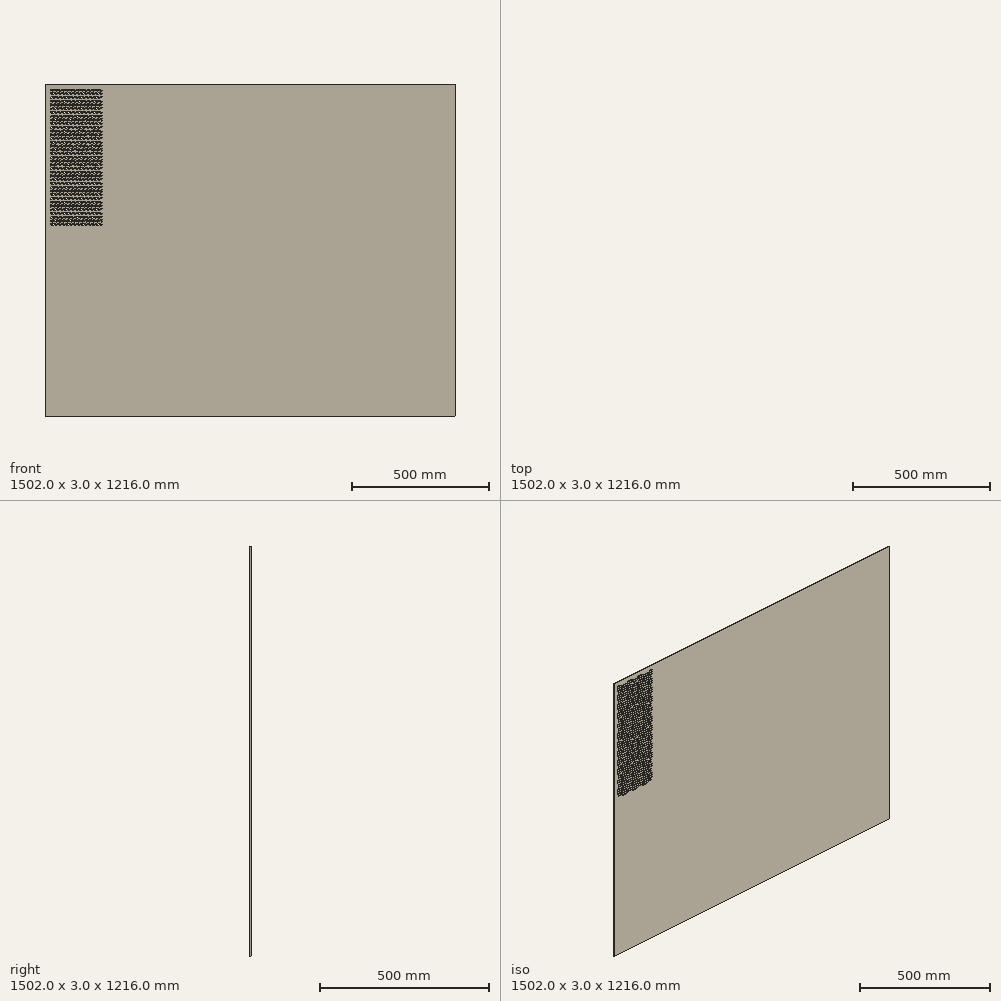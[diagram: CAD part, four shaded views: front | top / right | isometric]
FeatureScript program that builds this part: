
annotation { "Feature Type Name" : "Feature", "Feature Type Description" : "" }
export const myFeature = defineFeature(function(context is Context, id is Id, definition is map)
    precondition{}
    {
        {
            var Q0;
            Q0=qCreatedBy(makeId("Front.planeOp"),FACE);
            var sketch = newSketch(context, id + "F0", { "sketchPlane" : qUnion([Q0])});
            skLineSegment(sketch, "E0.bottom", {"start": v(-752.48, 576.01) * mm, "end": v(749.52, 576.01) * mm});
            skLineSegment(sketch, "E0.top", {"start": v(-752.48, -639.99) * mm, "end": v(749.52, -639.99) * mm});
            skLineSegment(sketch, "E0.left", {"start": v(-752.48, 576.01) * mm, "end": v(-752.48, -639.99) * mm});
            skLineSegment(sketch, "E0.right", {"start": v(749.52, 576.01) * mm, "end": v(749.52, -639.99) * mm});
            skCircle(sketch, "E1", {"center": v(-732.48, 556.01) * mm, "radius": 1.6 * mm});
            skCircle(sketch, "E2", {"center": v(-727.48, 556.01) * mm, "radius": 1.6 * mm});
            skCircle(sketch, "E3", {"center": v(-729.98, 551.01) * mm, "radius": 1.6 * mm});
            skCircle(sketch, "E4", {"center": v(-724.98, 551.01) * mm, "radius": 1.6 * mm});
            skCircle(sketch, "E5.0.1.0", {"center": v(-732.48, 546.01) * mm, "radius": 1.6 * mm});
            skCircle(sketch, "E5.0.1.1", {"center": v(-727.48, 546.01) * mm, "radius": 1.6 * mm});
            skCircle(sketch, "E5.0.1.2", {"center": v(-729.98, 541.01) * mm, "radius": 1.6 * mm});
            skCircle(sketch, "E5.0.1.3", {"center": v(-724.98, 541.01) * mm, "radius": 1.6 * mm});
            skCircle(sketch, "E5.0.2.0", {"center": v(-732.48, 536.01) * mm, "radius": 1.6 * mm});
            skCircle(sketch, "E5.0.2.1", {"center": v(-727.48, 536.01) * mm, "radius": 1.6 * mm});
            skCircle(sketch, "E5.0.2.2", {"center": v(-729.98, 531.01) * mm, "radius": 1.6 * mm});
            skCircle(sketch, "E5.0.2.3", {"center": v(-724.98, 531.01) * mm, "radius": 1.6 * mm});
            skCircle(sketch, "E5.0.3.0", {"center": v(-732.48, 526.01) * mm, "radius": 1.6 * mm});
            skCircle(sketch, "E5.0.3.1", {"center": v(-727.48, 526.01) * mm, "radius": 1.6 * mm});
            skCircle(sketch, "E5.0.3.2", {"center": v(-729.98, 521.01) * mm, "radius": 1.6 * mm});
            skCircle(sketch, "E5.0.3.3", {"center": v(-724.98, 521.01) * mm, "radius": 1.6 * mm});
            skCircle(sketch, "E5.0.4.0", {"center": v(-732.48, 516.01) * mm, "radius": 1.6 * mm});
            skCircle(sketch, "E5.0.4.1", {"center": v(-727.48, 516.01) * mm, "radius": 1.6 * mm});
            skCircle(sketch, "E5.0.4.2", {"center": v(-729.98, 511.01) * mm, "radius": 1.6 * mm});
            skCircle(sketch, "E5.0.4.3", {"center": v(-724.98, 511.01) * mm, "radius": 1.6 * mm});
            skCircle(sketch, "E5.0.5.0", {"center": v(-732.48, 506.01) * mm, "radius": 1.6 * mm});
            skCircle(sketch, "E5.0.5.1", {"center": v(-727.48, 506.01) * mm, "radius": 1.6 * mm});
            skCircle(sketch, "E5.0.5.2", {"center": v(-729.98, 501.01) * mm, "radius": 1.6 * mm});
            skCircle(sketch, "E5.0.5.3", {"center": v(-724.98, 501.01) * mm, "radius": 1.6 * mm});
            skCircle(sketch, "E5.0.6.0", {"center": v(-732.48, 496.01) * mm, "radius": 1.6 * mm});
            skCircle(sketch, "E5.0.6.1", {"center": v(-727.48, 496.01) * mm, "radius": 1.6 * mm});
            skCircle(sketch, "E5.0.6.2", {"center": v(-729.98, 491.01) * mm, "radius": 1.6 * mm});
            skCircle(sketch, "E5.0.6.3", {"center": v(-724.98, 491.01) * mm, "radius": 1.6 * mm});
            skCircle(sketch, "E5.0.7.0", {"center": v(-732.48, 486.01) * mm, "radius": 1.6 * mm});
            skCircle(sketch, "E5.0.7.1", {"center": v(-727.48, 486.01) * mm, "radius": 1.6 * mm});
            skCircle(sketch, "E5.0.7.2", {"center": v(-729.98, 481.01) * mm, "radius": 1.6 * mm});
            skCircle(sketch, "E5.0.7.3", {"center": v(-724.98, 481.01) * mm, "radius": 1.6 * mm});
            skCircle(sketch, "E5.0.8.0", {"center": v(-732.48, 476.01) * mm, "radius": 1.6 * mm});
            skCircle(sketch, "E5.0.8.1", {"center": v(-727.48, 476.01) * mm, "radius": 1.6 * mm});
            skCircle(sketch, "E5.0.8.2", {"center": v(-729.98, 471.01) * mm, "radius": 1.6 * mm});
            skCircle(sketch, "E5.0.8.3", {"center": v(-724.98, 471.01) * mm, "radius": 1.6 * mm});
            skCircle(sketch, "E5.0.9.0", {"center": v(-732.48, 466.01) * mm, "radius": 1.6 * mm});
            skCircle(sketch, "E5.0.9.1", {"center": v(-727.48, 466.01) * mm, "radius": 1.6 * mm});
            skCircle(sketch, "E5.0.9.2", {"center": v(-729.98, 461.01) * mm, "radius": 1.6 * mm});
            skCircle(sketch, "E5.0.9.3", {"center": v(-724.98, 461.01) * mm, "radius": 1.6 * mm});
            skCircle(sketch, "E5.0.10.0", {"center": v(-732.48, 456.01) * mm, "radius": 1.6 * mm});
            skCircle(sketch, "E5.0.10.1", {"center": v(-727.48, 456.01) * mm, "radius": 1.6 * mm});
            skCircle(sketch, "E5.0.10.2", {"center": v(-729.98, 451.01) * mm, "radius": 1.6 * mm});
            skCircle(sketch, "E5.0.10.3", {"center": v(-724.98, 451.01) * mm, "radius": 1.6 * mm});
            skCircle(sketch, "E5.0.11.0", {"center": v(-732.48, 446.01) * mm, "radius": 1.6 * mm});
            skCircle(sketch, "E5.0.11.1", {"center": v(-727.48, 446.01) * mm, "radius": 1.6 * mm});
            skCircle(sketch, "E5.0.11.2", {"center": v(-729.98, 441.01) * mm, "radius": 1.6 * mm});
            skCircle(sketch, "E5.0.11.3", {"center": v(-724.98, 441.01) * mm, "radius": 1.6 * mm});
            skCircle(sketch, "E5.0.12.0", {"center": v(-732.48, 436.01) * mm, "radius": 1.6 * mm});
            skCircle(sketch, "E5.0.12.1", {"center": v(-727.48, 436.01) * mm, "radius": 1.6 * mm});
            skCircle(sketch, "E5.0.12.2", {"center": v(-729.98, 431.01) * mm, "radius": 1.6 * mm});
            skCircle(sketch, "E5.0.12.3", {"center": v(-724.98, 431.01) * mm, "radius": 1.6 * mm});
            skCircle(sketch, "E5.0.13.0", {"center": v(-732.48, 426.01) * mm, "radius": 1.6 * mm});
            skCircle(sketch, "E5.0.13.1", {"center": v(-727.48, 426.01) * mm, "radius": 1.6 * mm});
            skCircle(sketch, "E5.0.13.2", {"center": v(-729.98, 421.01) * mm, "radius": 1.6 * mm});
            skCircle(sketch, "E5.0.13.3", {"center": v(-724.98, 421.01) * mm, "radius": 1.6 * mm});
            skCircle(sketch, "E5.0.14.0", {"center": v(-732.48, 416.01) * mm, "radius": 1.6 * mm});
            skCircle(sketch, "E5.0.14.1", {"center": v(-727.48, 416.01) * mm, "radius": 1.6 * mm});
            skCircle(sketch, "E5.0.14.2", {"center": v(-729.98, 411.01) * mm, "radius": 1.6 * mm});
            skCircle(sketch, "E5.0.14.3", {"center": v(-724.98, 411.01) * mm, "radius": 1.6 * mm});
            skCircle(sketch, "E5.0.15.0", {"center": v(-732.48, 406.01) * mm, "radius": 1.6 * mm});
            skCircle(sketch, "E5.0.15.1", {"center": v(-727.48, 406.01) * mm, "radius": 1.6 * mm});
            skCircle(sketch, "E5.0.15.2", {"center": v(-729.98, 401.01) * mm, "radius": 1.6 * mm});
            skCircle(sketch, "E5.0.15.3", {"center": v(-724.98, 401.01) * mm, "radius": 1.6 * mm});
            skCircle(sketch, "E5.0.16.0", {"center": v(-732.48, 396.01) * mm, "radius": 1.6 * mm});
            skCircle(sketch, "E5.0.16.1", {"center": v(-727.48, 396.01) * mm, "radius": 1.6 * mm});
            skCircle(sketch, "E5.0.16.2", {"center": v(-729.98, 391.01) * mm, "radius": 1.6 * mm});
            skCircle(sketch, "E5.0.16.3", {"center": v(-724.98, 391.01) * mm, "radius": 1.6 * mm});
            skCircle(sketch, "E5.0.17.0", {"center": v(-732.48, 386.01) * mm, "radius": 1.6 * mm});
            skCircle(sketch, "E5.0.17.1", {"center": v(-727.48, 386.01) * mm, "radius": 1.6 * mm});
            skCircle(sketch, "E5.0.17.2", {"center": v(-729.98, 381.01) * mm, "radius": 1.6 * mm});
            skCircle(sketch, "E5.0.17.3", {"center": v(-724.98, 381.01) * mm, "radius": 1.6 * mm});
            skCircle(sketch, "E5.0.18.0", {"center": v(-732.48, 376.01) * mm, "radius": 1.6 * mm});
            skCircle(sketch, "E5.0.18.1", {"center": v(-727.48, 376.01) * mm, "radius": 1.6 * mm});
            skCircle(sketch, "E5.0.18.2", {"center": v(-729.98, 371.01) * mm, "radius": 1.6 * mm});
            skCircle(sketch, "E5.0.18.3", {"center": v(-724.98, 371.01) * mm, "radius": 1.6 * mm});
            skCircle(sketch, "E5.0.19.0", {"center": v(-732.48, 366.01) * mm, "radius": 1.6 * mm});
            skCircle(sketch, "E5.0.19.1", {"center": v(-727.48, 366.01) * mm, "radius": 1.6 * mm});
            skCircle(sketch, "E5.0.19.2", {"center": v(-729.98, 361.01) * mm, "radius": 1.6 * mm});
            skCircle(sketch, "E5.0.19.3", {"center": v(-724.98, 361.01) * mm, "radius": 1.6 * mm});
            skCircle(sketch, "E5.0.20.0", {"center": v(-732.48, 356.01) * mm, "radius": 1.6 * mm});
            skCircle(sketch, "E5.0.20.1", {"center": v(-727.48, 356.01) * mm, "radius": 1.6 * mm});
            skCircle(sketch, "E5.0.20.2", {"center": v(-729.98, 351.01) * mm, "radius": 1.6 * mm});
            skCircle(sketch, "E5.0.20.3", {"center": v(-724.98, 351.01) * mm, "radius": 1.6 * mm});
            skCircle(sketch, "E5.0.21.0", {"center": v(-732.48, 346.01) * mm, "radius": 1.6 * mm});
            skCircle(sketch, "E5.0.21.1", {"center": v(-727.48, 346.01) * mm, "radius": 1.6 * mm});
            skCircle(sketch, "E5.0.21.2", {"center": v(-729.98, 341.01) * mm, "radius": 1.6 * mm});
            skCircle(sketch, "E5.0.21.3", {"center": v(-724.98, 341.01) * mm, "radius": 1.6 * mm});
            skCircle(sketch, "E5.0.22.0", {"center": v(-732.48, 336.01) * mm, "radius": 1.6 * mm});
            skCircle(sketch, "E5.0.22.1", {"center": v(-727.48, 336.01) * mm, "radius": 1.6 * mm});
            skCircle(sketch, "E5.0.22.2", {"center": v(-729.98, 331.01) * mm, "radius": 1.6 * mm});
            skCircle(sketch, "E5.0.22.3", {"center": v(-724.98, 331.01) * mm, "radius": 1.6 * mm});
            skCircle(sketch, "E5.0.23.0", {"center": v(-732.48, 326.01) * mm, "radius": 1.6 * mm});
            skCircle(sketch, "E5.0.23.1", {"center": v(-727.48, 326.01) * mm, "radius": 1.6 * mm});
            skCircle(sketch, "E5.0.23.2", {"center": v(-729.98, 321.01) * mm, "radius": 1.6 * mm});
            skCircle(sketch, "E5.0.23.3", {"center": v(-724.98, 321.01) * mm, "radius": 1.6 * mm});
            skCircle(sketch, "E5.0.24.0", {"center": v(-732.48, 316.01) * mm, "radius": 1.6 * mm});
            skCircle(sketch, "E5.0.24.1", {"center": v(-727.48, 316.01) * mm, "radius": 1.6 * mm});
            skCircle(sketch, "E5.0.24.2", {"center": v(-729.98, 311.01) * mm, "radius": 1.6 * mm});
            skCircle(sketch, "E5.0.24.3", {"center": v(-724.98, 311.01) * mm, "radius": 1.6 * mm});
            skCircle(sketch, "E5.0.25.0", {"center": v(-732.48, 306.01) * mm, "radius": 1.6 * mm});
            skCircle(sketch, "E5.0.25.1", {"center": v(-727.48, 306.01) * mm, "radius": 1.6 * mm});
            skCircle(sketch, "E5.0.25.2", {"center": v(-729.98, 301.01) * mm, "radius": 1.6 * mm});
            skCircle(sketch, "E5.0.25.3", {"center": v(-724.98, 301.01) * mm, "radius": 1.6 * mm});
            skCircle(sketch, "E5.0.26.0", {"center": v(-732.48, 296.01) * mm, "radius": 1.6 * mm});
            skCircle(sketch, "E5.0.26.1", {"center": v(-727.48, 296.01) * mm, "radius": 1.6 * mm});
            skCircle(sketch, "E5.0.26.2", {"center": v(-729.98, 291.01) * mm, "radius": 1.6 * mm});
            skCircle(sketch, "E5.0.26.3", {"center": v(-724.98, 291.01) * mm, "radius": 1.6 * mm});
            skCircle(sketch, "E5.0.27.0", {"center": v(-732.48, 286.01) * mm, "radius": 1.6 * mm});
            skCircle(sketch, "E5.0.27.1", {"center": v(-727.48, 286.01) * mm, "radius": 1.6 * mm});
            skCircle(sketch, "E5.0.27.2", {"center": v(-729.98, 281.01) * mm, "radius": 1.6 * mm});
            skCircle(sketch, "E5.0.27.3", {"center": v(-724.98, 281.01) * mm, "radius": 1.6 * mm});
            skCircle(sketch, "E5.0.28.0", {"center": v(-732.48, 276.01) * mm, "radius": 1.6 * mm});
            skCircle(sketch, "E5.0.28.1", {"center": v(-727.48, 276.01) * mm, "radius": 1.6 * mm});
            skCircle(sketch, "E5.0.28.2", {"center": v(-729.98, 271.01) * mm, "radius": 1.6 * mm});
            skCircle(sketch, "E5.0.28.3", {"center": v(-724.98, 271.01) * mm, "radius": 1.6 * mm});
            skCircle(sketch, "E5.0.29.0", {"center": v(-732.48, 266.01) * mm, "radius": 1.6 * mm});
            skCircle(sketch, "E5.0.29.1", {"center": v(-727.48, 266.01) * mm, "radius": 1.6 * mm});
            skCircle(sketch, "E5.0.29.2", {"center": v(-729.98, 261.01) * mm, "radius": 1.6 * mm});
            skCircle(sketch, "E5.0.29.3", {"center": v(-724.98, 261.01) * mm, "radius": 1.6 * mm});
            skCircle(sketch, "E5.0.30.0", {"center": v(-732.48, 256.01) * mm, "radius": 1.6 * mm});
            skCircle(sketch, "E5.0.30.1", {"center": v(-727.48, 256.01) * mm, "radius": 1.6 * mm});
            skCircle(sketch, "E5.0.30.2", {"center": v(-729.98, 251.01) * mm, "radius": 1.6 * mm});
            skCircle(sketch, "E5.0.30.3", {"center": v(-724.98, 251.01) * mm, "radius": 1.6 * mm});
            skCircle(sketch, "E5.0.31.0", {"center": v(-732.48, 246.01) * mm, "radius": 1.6 * mm});
            skCircle(sketch, "E5.0.31.1", {"center": v(-727.48, 246.01) * mm, "radius": 1.6 * mm});
            skCircle(sketch, "E5.0.31.2", {"center": v(-729.98, 241.01) * mm, "radius": 1.6 * mm});
            skCircle(sketch, "E5.0.31.3", {"center": v(-724.98, 241.01) * mm, "radius": 1.6 * mm});
            skCircle(sketch, "E5.0.32.0", {"center": v(-732.48, 236.01) * mm, "radius": 1.6 * mm});
            skCircle(sketch, "E5.0.32.1", {"center": v(-727.48, 236.01) * mm, "radius": 1.6 * mm});
            skCircle(sketch, "E5.0.32.2", {"center": v(-729.98, 231.01) * mm, "radius": 1.6 * mm});
            skCircle(sketch, "E5.0.32.3", {"center": v(-724.98, 231.01) * mm, "radius": 1.6 * mm});
            skCircle(sketch, "E5.0.33.0", {"center": v(-732.48, 226.01) * mm, "radius": 1.6 * mm});
            skCircle(sketch, "E5.0.33.1", {"center": v(-727.48, 226.01) * mm, "radius": 1.6 * mm});
            skCircle(sketch, "E5.0.33.2", {"center": v(-729.98, 221.01) * mm, "radius": 1.6 * mm});
            skCircle(sketch, "E5.0.33.3", {"center": v(-724.98, 221.01) * mm, "radius": 1.6 * mm});
            skCircle(sketch, "E5.0.34.0", {"center": v(-732.48, 216.01) * mm, "radius": 1.6 * mm});
            skCircle(sketch, "E5.0.34.1", {"center": v(-727.48, 216.01) * mm, "radius": 1.6 * mm});
            skCircle(sketch, "E5.0.34.2", {"center": v(-729.98, 211.01) * mm, "radius": 1.6 * mm});
            skCircle(sketch, "E5.0.34.3", {"center": v(-724.98, 211.01) * mm, "radius": 1.6 * mm});
            skCircle(sketch, "E5.0.35.0", {"center": v(-732.48, 206.01) * mm, "radius": 1.6 * mm});
            skCircle(sketch, "E5.0.35.1", {"center": v(-727.48, 206.01) * mm, "radius": 1.6 * mm});
            skCircle(sketch, "E5.0.35.2", {"center": v(-729.98, 201.01) * mm, "radius": 1.6 * mm});
            skCircle(sketch, "E5.0.35.3", {"center": v(-724.98, 201.01) * mm, "radius": 1.6 * mm});
            skCircle(sketch, "E5.0.36.0", {"center": v(-732.48, 196.01) * mm, "radius": 1.6 * mm});
            skCircle(sketch, "E5.0.36.1", {"center": v(-727.48, 196.01) * mm, "radius": 1.6 * mm});
            skCircle(sketch, "E5.0.36.2", {"center": v(-729.98, 191.01) * mm, "radius": 1.6 * mm});
            skCircle(sketch, "E5.0.36.3", {"center": v(-724.98, 191.01) * mm, "radius": 1.6 * mm});
            skCircle(sketch, "E5.0.37.0", {"center": v(-732.48, 186.01) * mm, "radius": 1.6 * mm});
            skCircle(sketch, "E5.0.37.1", {"center": v(-727.48, 186.01) * mm, "radius": 1.6 * mm});
            skCircle(sketch, "E5.0.37.2", {"center": v(-729.98, 181.01) * mm, "radius": 1.6 * mm});
            skCircle(sketch, "E5.0.37.3", {"center": v(-724.98, 181.01) * mm, "radius": 1.6 * mm});
            skCircle(sketch, "E5.0.38.0", {"center": v(-732.48, 176.01) * mm, "radius": 1.6 * mm});
            skCircle(sketch, "E5.0.38.1", {"center": v(-727.48, 176.01) * mm, "radius": 1.6 * mm});
            skCircle(sketch, "E5.0.38.2", {"center": v(-729.98, 171.01) * mm, "radius": 1.6 * mm});
            skCircle(sketch, "E5.0.38.3", {"center": v(-724.98, 171.01) * mm, "radius": 1.6 * mm});
            skCircle(sketch, "E5.0.39.0", {"center": v(-732.48, 166.01) * mm, "radius": 1.6 * mm});
            skCircle(sketch, "E5.0.39.1", {"center": v(-727.48, 166.01) * mm, "radius": 1.6 * mm});
            skCircle(sketch, "E5.0.39.2", {"center": v(-729.98, 161.01) * mm, "radius": 1.6 * mm});
            skCircle(sketch, "E5.0.39.3", {"center": v(-724.98, 161.01) * mm, "radius": 1.6 * mm});
            skCircle(sketch, "E5.0.40.0", {"center": v(-732.48, 156.01) * mm, "radius": 1.6 * mm});
            skCircle(sketch, "E5.0.40.1", {"center": v(-727.48, 156.01) * mm, "radius": 1.6 * mm});
            skCircle(sketch, "E5.0.40.2", {"center": v(-729.98, 151.01) * mm, "radius": 1.6 * mm});
            skCircle(sketch, "E5.0.40.3", {"center": v(-724.98, 151.01) * mm, "radius": 1.6 * mm});
            skCircle(sketch, "E5.0.41.0", {"center": v(-732.48, 146.01) * mm, "radius": 1.6 * mm});
            skCircle(sketch, "E5.0.41.1", {"center": v(-727.48, 146.01) * mm, "radius": 1.6 * mm});
            skCircle(sketch, "E5.0.41.2", {"center": v(-729.98, 141.01) * mm, "radius": 1.6 * mm});
            skCircle(sketch, "E5.0.41.3", {"center": v(-724.98, 141.01) * mm, "radius": 1.6 * mm});
            skCircle(sketch, "E5.0.42.0", {"center": v(-732.48, 136.01) * mm, "radius": 1.6 * mm});
            skCircle(sketch, "E5.0.42.1", {"center": v(-727.48, 136.01) * mm, "radius": 1.6 * mm});
            skCircle(sketch, "E5.0.42.2", {"center": v(-729.98, 131.01) * mm, "radius": 1.6 * mm});
            skCircle(sketch, "E5.0.42.3", {"center": v(-724.98, 131.01) * mm, "radius": 1.6 * mm});
            skCircle(sketch, "E5.0.43.0", {"center": v(-732.48, 126.01) * mm, "radius": 1.6 * mm});
            skCircle(sketch, "E5.0.43.1", {"center": v(-727.48, 126.01) * mm, "radius": 1.6 * mm});
            skCircle(sketch, "E5.0.43.2", {"center": v(-729.98, 121.01) * mm, "radius": 1.6 * mm});
            skCircle(sketch, "E5.0.43.3", {"center": v(-724.98, 121.01) * mm, "radius": 1.6 * mm});
            skCircle(sketch, "E5.0.44.0", {"center": v(-732.48, 116.01) * mm, "radius": 1.6 * mm});
            skCircle(sketch, "E5.0.44.1", {"center": v(-727.48, 116.01) * mm, "radius": 1.6 * mm});
            skCircle(sketch, "E5.0.44.2", {"center": v(-729.98, 111.01) * mm, "radius": 1.6 * mm});
            skCircle(sketch, "E5.0.44.3", {"center": v(-724.98, 111.01) * mm, "radius": 1.6 * mm});
            skCircle(sketch, "E5.0.45.0", {"center": v(-732.48, 106.01) * mm, "radius": 1.6 * mm});
            skCircle(sketch, "E5.0.45.1", {"center": v(-727.48, 106.01) * mm, "radius": 1.6 * mm});
            skCircle(sketch, "E5.0.45.2", {"center": v(-729.98, 101.01) * mm, "radius": 1.6 * mm});
            skCircle(sketch, "E5.0.45.3", {"center": v(-724.98, 101.01) * mm, "radius": 1.6 * mm});
            skCircle(sketch, "E5.0.46.0", {"center": v(-732.48, 96.01) * mm, "radius": 1.6 * mm});
            skCircle(sketch, "E5.0.46.1", {"center": v(-727.48, 96.01) * mm, "radius": 1.6 * mm});
            skCircle(sketch, "E5.0.46.2", {"center": v(-729.98, 91.01) * mm, "radius": 1.6 * mm});
            skCircle(sketch, "E5.0.46.3", {"center": v(-724.98, 91.01) * mm, "radius": 1.6 * mm});
            skCircle(sketch, "E5.0.47.0", {"center": v(-732.48, 86.01) * mm, "radius": 1.6 * mm});
            skCircle(sketch, "E5.0.47.1", {"center": v(-727.48, 86.01) * mm, "radius": 1.6 * mm});
            skCircle(sketch, "E5.0.47.2", {"center": v(-729.98, 81.01) * mm, "radius": 1.6 * mm});
            skCircle(sketch, "E5.0.47.3", {"center": v(-724.98, 81.01) * mm, "radius": 1.6 * mm});
            skCircle(sketch, "E5.0.48.0", {"center": v(-732.48, 76.01) * mm, "radius": 1.6 * mm});
            skCircle(sketch, "E5.0.48.1", {"center": v(-727.48, 76.01) * mm, "radius": 1.6 * mm});
            skCircle(sketch, "E5.0.48.2", {"center": v(-729.98, 71.01) * mm, "radius": 1.6 * mm});
            skCircle(sketch, "E5.0.48.3", {"center": v(-724.98, 71.01) * mm, "radius": 1.6 * mm});
            skCircle(sketch, "E5.0.49.0", {"center": v(-732.48, 66.01) * mm, "radius": 1.6 * mm});
            skCircle(sketch, "E5.0.49.1", {"center": v(-727.48, 66.01) * mm, "radius": 1.6 * mm});
            skCircle(sketch, "E5.0.49.2", {"center": v(-729.98, 61.01) * mm, "radius": 1.6 * mm});
            skCircle(sketch, "E5.0.49.3", {"center": v(-724.98, 61.01) * mm, "radius": 1.6 * mm});
            skCircle(sketch, "E5.1.0.0", {"center": v(-722.48, 556.01) * mm, "radius": 1.6 * mm});
            skCircle(sketch, "E5.1.0.1", {"center": v(-717.48, 556.01) * mm, "radius": 1.6 * mm});
            skCircle(sketch, "E5.1.0.2", {"center": v(-719.98, 551.01) * mm, "radius": 1.6 * mm});
            skCircle(sketch, "E5.1.0.3", {"center": v(-714.98, 551.01) * mm, "radius": 1.6 * mm});
            skCircle(sketch, "E5.1.1.0", {"center": v(-722.48, 546.01) * mm, "radius": 1.6 * mm});
            skCircle(sketch, "E5.1.1.1", {"center": v(-717.48, 546.01) * mm, "radius": 1.6 * mm});
            skCircle(sketch, "E5.1.1.2", {"center": v(-719.98, 541.01) * mm, "radius": 1.6 * mm});
            skCircle(sketch, "E5.1.1.3", {"center": v(-714.98, 541.01) * mm, "radius": 1.6 * mm});
            skCircle(sketch, "E5.1.2.0", {"center": v(-722.48, 536.01) * mm, "radius": 1.6 * mm});
            skCircle(sketch, "E5.1.2.1", {"center": v(-717.48, 536.01) * mm, "radius": 1.6 * mm});
            skCircle(sketch, "E5.1.2.2", {"center": v(-719.98, 531.01) * mm, "radius": 1.6 * mm});
            skCircle(sketch, "E5.1.2.3", {"center": v(-714.98, 531.01) * mm, "radius": 1.6 * mm});
            skCircle(sketch, "E5.1.3.0", {"center": v(-722.48, 526.01) * mm, "radius": 1.6 * mm});
            skCircle(sketch, "E5.1.3.1", {"center": v(-717.48, 526.01) * mm, "radius": 1.6 * mm});
            skCircle(sketch, "E5.1.3.2", {"center": v(-719.98, 521.01) * mm, "radius": 1.6 * mm});
            skCircle(sketch, "E5.1.3.3", {"center": v(-714.98, 521.01) * mm, "radius": 1.6 * mm});
            skCircle(sketch, "E5.1.4.0", {"center": v(-722.48, 516.01) * mm, "radius": 1.6 * mm});
            skCircle(sketch, "E5.1.4.1", {"center": v(-717.48, 516.01) * mm, "radius": 1.6 * mm});
            skCircle(sketch, "E5.1.4.2", {"center": v(-719.98, 511.01) * mm, "radius": 1.6 * mm});
            skCircle(sketch, "E5.1.4.3", {"center": v(-714.98, 511.01) * mm, "radius": 1.6 * mm});
            skCircle(sketch, "E5.1.5.0", {"center": v(-722.48, 506.01) * mm, "radius": 1.6 * mm});
            skCircle(sketch, "E5.1.5.1", {"center": v(-717.48, 506.01) * mm, "radius": 1.6 * mm});
            skCircle(sketch, "E5.1.5.2", {"center": v(-719.98, 501.01) * mm, "radius": 1.6 * mm});
            skCircle(sketch, "E5.1.5.3", {"center": v(-714.98, 501.01) * mm, "radius": 1.6 * mm});
            skCircle(sketch, "E5.1.6.0", {"center": v(-722.48, 496.01) * mm, "radius": 1.6 * mm});
            skCircle(sketch, "E5.1.6.1", {"center": v(-717.48, 496.01) * mm, "radius": 1.6 * mm});
            skCircle(sketch, "E5.1.6.2", {"center": v(-719.98, 491.01) * mm, "radius": 1.6 * mm});
            skCircle(sketch, "E5.1.6.3", {"center": v(-714.98, 491.01) * mm, "radius": 1.6 * mm});
            skCircle(sketch, "E5.1.7.0", {"center": v(-722.48, 486.01) * mm, "radius": 1.6 * mm});
            skCircle(sketch, "E5.1.7.1", {"center": v(-717.48, 486.01) * mm, "radius": 1.6 * mm});
            skCircle(sketch, "E5.1.7.2", {"center": v(-719.98, 481.01) * mm, "radius": 1.6 * mm});
            skCircle(sketch, "E5.1.7.3", {"center": v(-714.98, 481.01) * mm, "radius": 1.6 * mm});
            skCircle(sketch, "E5.1.8.0", {"center": v(-722.48, 476.01) * mm, "radius": 1.6 * mm});
            skCircle(sketch, "E5.1.8.1", {"center": v(-717.48, 476.01) * mm, "radius": 1.6 * mm});
            skCircle(sketch, "E5.1.8.2", {"center": v(-719.98, 471.01) * mm, "radius": 1.6 * mm});
            skCircle(sketch, "E5.1.8.3", {"center": v(-714.98, 471.01) * mm, "radius": 1.6 * mm});
            skCircle(sketch, "E5.1.9.0", {"center": v(-722.48, 466.01) * mm, "radius": 1.6 * mm});
            skCircle(sketch, "E5.1.9.1", {"center": v(-717.48, 466.01) * mm, "radius": 1.6 * mm});
            skCircle(sketch, "E5.1.9.2", {"center": v(-719.98, 461.01) * mm, "radius": 1.6 * mm});
            skCircle(sketch, "E5.1.9.3", {"center": v(-714.98, 461.01) * mm, "radius": 1.6 * mm});
            skCircle(sketch, "E5.1.10.0", {"center": v(-722.48, 456.01) * mm, "radius": 1.6 * mm});
            skCircle(sketch, "E5.1.10.1", {"center": v(-717.48, 456.01) * mm, "radius": 1.6 * mm});
            skCircle(sketch, "E5.1.10.2", {"center": v(-719.98, 451.01) * mm, "radius": 1.6 * mm});
            skCircle(sketch, "E5.1.10.3", {"center": v(-714.98, 451.01) * mm, "radius": 1.6 * mm});
            skCircle(sketch, "E5.1.11.0", {"center": v(-722.48, 446.01) * mm, "radius": 1.6 * mm});
            skCircle(sketch, "E5.1.11.1", {"center": v(-717.48, 446.01) * mm, "radius": 1.6 * mm});
            skCircle(sketch, "E5.1.11.2", {"center": v(-719.98, 441.01) * mm, "radius": 1.6 * mm});
            skCircle(sketch, "E5.1.11.3", {"center": v(-714.98, 441.01) * mm, "radius": 1.6 * mm});
            skCircle(sketch, "E5.1.12.0", {"center": v(-722.48, 436.01) * mm, "radius": 1.6 * mm});
            skCircle(sketch, "E5.1.12.1", {"center": v(-717.48, 436.01) * mm, "radius": 1.6 * mm});
            skCircle(sketch, "E5.1.12.2", {"center": v(-719.98, 431.01) * mm, "radius": 1.6 * mm});
            skCircle(sketch, "E5.1.12.3", {"center": v(-714.98, 431.01) * mm, "radius": 1.6 * mm});
            skCircle(sketch, "E5.1.13.0", {"center": v(-722.48, 426.01) * mm, "radius": 1.6 * mm});
            skCircle(sketch, "E5.1.13.1", {"center": v(-717.48, 426.01) * mm, "radius": 1.6 * mm});
            skCircle(sketch, "E5.1.13.2", {"center": v(-719.98, 421.01) * mm, "radius": 1.6 * mm});
            skCircle(sketch, "E5.1.13.3", {"center": v(-714.98, 421.01) * mm, "radius": 1.6 * mm});
            skCircle(sketch, "E5.1.14.0", {"center": v(-722.48, 416.01) * mm, "radius": 1.6 * mm});
            skCircle(sketch, "E5.1.14.1", {"center": v(-717.48, 416.01) * mm, "radius": 1.6 * mm});
            skCircle(sketch, "E5.1.14.2", {"center": v(-719.98, 411.01) * mm, "radius": 1.6 * mm});
            skCircle(sketch, "E5.1.14.3", {"center": v(-714.98, 411.01) * mm, "radius": 1.6 * mm});
            skCircle(sketch, "E5.1.15.0", {"center": v(-722.48, 406.01) * mm, "radius": 1.6 * mm});
            skCircle(sketch, "E5.1.15.1", {"center": v(-717.48, 406.01) * mm, "radius": 1.6 * mm});
            skCircle(sketch, "E5.1.15.2", {"center": v(-719.98, 401.01) * mm, "radius": 1.6 * mm});
            skCircle(sketch, "E5.1.15.3", {"center": v(-714.98, 401.01) * mm, "radius": 1.6 * mm});
            skCircle(sketch, "E5.1.16.0", {"center": v(-722.48, 396.01) * mm, "radius": 1.6 * mm});
            skCircle(sketch, "E5.1.16.1", {"center": v(-717.48, 396.01) * mm, "radius": 1.6 * mm});
            skCircle(sketch, "E5.1.16.2", {"center": v(-719.98, 391.01) * mm, "radius": 1.6 * mm});
            skCircle(sketch, "E5.1.16.3", {"center": v(-714.98, 391.01) * mm, "radius": 1.6 * mm});
            skCircle(sketch, "E5.1.17.0", {"center": v(-722.48, 386.01) * mm, "radius": 1.6 * mm});
            skCircle(sketch, "E5.1.17.1", {"center": v(-717.48, 386.01) * mm, "radius": 1.6 * mm});
            skCircle(sketch, "E5.1.17.2", {"center": v(-719.98, 381.01) * mm, "radius": 1.6 * mm});
            skCircle(sketch, "E5.1.17.3", {"center": v(-714.98, 381.01) * mm, "radius": 1.6 * mm});
            skCircle(sketch, "E5.1.18.0", {"center": v(-722.48, 376.01) * mm, "radius": 1.6 * mm});
            skCircle(sketch, "E5.1.18.1", {"center": v(-717.48, 376.01) * mm, "radius": 1.6 * mm});
            skCircle(sketch, "E5.1.18.2", {"center": v(-719.98, 371.01) * mm, "radius": 1.6 * mm});
            skCircle(sketch, "E5.1.18.3", {"center": v(-714.98, 371.01) * mm, "radius": 1.6 * mm});
            skCircle(sketch, "E5.1.19.0", {"center": v(-722.48, 366.01) * mm, "radius": 1.6 * mm});
            skCircle(sketch, "E5.1.19.1", {"center": v(-717.48, 366.01) * mm, "radius": 1.6 * mm});
            skCircle(sketch, "E5.1.19.2", {"center": v(-719.98, 361.01) * mm, "radius": 1.6 * mm});
            skCircle(sketch, "E5.1.19.3", {"center": v(-714.98, 361.01) * mm, "radius": 1.6 * mm});
            skCircle(sketch, "E5.1.20.0", {"center": v(-722.48, 356.01) * mm, "radius": 1.6 * mm});
            skCircle(sketch, "E5.1.20.1", {"center": v(-717.48, 356.01) * mm, "radius": 1.6 * mm});
            skCircle(sketch, "E5.1.20.2", {"center": v(-719.98, 351.01) * mm, "radius": 1.6 * mm});
            skCircle(sketch, "E5.1.20.3", {"center": v(-714.98, 351.01) * mm, "radius": 1.6 * mm});
            skCircle(sketch, "E5.1.21.0", {"center": v(-722.48, 346.01) * mm, "radius": 1.6 * mm});
            skCircle(sketch, "E5.1.21.1", {"center": v(-717.48, 346.01) * mm, "radius": 1.6 * mm});
            skCircle(sketch, "E5.1.21.2", {"center": v(-719.98, 341.01) * mm, "radius": 1.6 * mm});
            skCircle(sketch, "E5.1.21.3", {"center": v(-714.98, 341.01) * mm, "radius": 1.6 * mm});
            skCircle(sketch, "E5.1.22.0", {"center": v(-722.48, 336.01) * mm, "radius": 1.6 * mm});
            skCircle(sketch, "E5.1.22.1", {"center": v(-717.48, 336.01) * mm, "radius": 1.6 * mm});
            skCircle(sketch, "E5.1.22.2", {"center": v(-719.98, 331.01) * mm, "radius": 1.6 * mm});
            skCircle(sketch, "E5.1.22.3", {"center": v(-714.98, 331.01) * mm, "radius": 1.6 * mm});
            skCircle(sketch, "E5.1.23.0", {"center": v(-722.48, 326.01) * mm, "radius": 1.6 * mm});
            skCircle(sketch, "E5.1.23.1", {"center": v(-717.48, 326.01) * mm, "radius": 1.6 * mm});
            skCircle(sketch, "E5.1.23.2", {"center": v(-719.98, 321.01) * mm, "radius": 1.6 * mm});
            skCircle(sketch, "E5.1.23.3", {"center": v(-714.98, 321.01) * mm, "radius": 1.6 * mm});
            skCircle(sketch, "E5.1.24.0", {"center": v(-722.48, 316.01) * mm, "radius": 1.6 * mm});
            skCircle(sketch, "E5.1.24.1", {"center": v(-717.48, 316.01) * mm, "radius": 1.6 * mm});
            skCircle(sketch, "E5.1.24.2", {"center": v(-719.98, 311.01) * mm, "radius": 1.6 * mm});
            skCircle(sketch, "E5.1.24.3", {"center": v(-714.98, 311.01) * mm, "radius": 1.6 * mm});
            skCircle(sketch, "E5.1.25.0", {"center": v(-722.48, 306.01) * mm, "radius": 1.6 * mm});
            skCircle(sketch, "E5.1.25.1", {"center": v(-717.48, 306.01) * mm, "radius": 1.6 * mm});
            skCircle(sketch, "E5.1.25.2", {"center": v(-719.98, 301.01) * mm, "radius": 1.6 * mm});
            skCircle(sketch, "E5.1.25.3", {"center": v(-714.98, 301.01) * mm, "radius": 1.6 * mm});
            skCircle(sketch, "E5.1.26.0", {"center": v(-722.48, 296.01) * mm, "radius": 1.6 * mm});
            skCircle(sketch, "E5.1.26.1", {"center": v(-717.48, 296.01) * mm, "radius": 1.6 * mm});
            skCircle(sketch, "E5.1.26.2", {"center": v(-719.98, 291.01) * mm, "radius": 1.6 * mm});
            skCircle(sketch, "E5.1.26.3", {"center": v(-714.98, 291.01) * mm, "radius": 1.6 * mm});
            skCircle(sketch, "E5.1.27.0", {"center": v(-722.48, 286.01) * mm, "radius": 1.6 * mm});
            skCircle(sketch, "E5.1.27.1", {"center": v(-717.48, 286.01) * mm, "radius": 1.6 * mm});
            skCircle(sketch, "E5.1.27.2", {"center": v(-719.98, 281.01) * mm, "radius": 1.6 * mm});
            skCircle(sketch, "E5.1.27.3", {"center": v(-714.98, 281.01) * mm, "radius": 1.6 * mm});
            skCircle(sketch, "E5.1.28.0", {"center": v(-722.48, 276.01) * mm, "radius": 1.6 * mm});
            skCircle(sketch, "E5.1.28.1", {"center": v(-717.48, 276.01) * mm, "radius": 1.6 * mm});
            skCircle(sketch, "E5.1.28.2", {"center": v(-719.98, 271.01) * mm, "radius": 1.6 * mm});
            skCircle(sketch, "E5.1.28.3", {"center": v(-714.98, 271.01) * mm, "radius": 1.6 * mm});
            skCircle(sketch, "E5.1.29.0", {"center": v(-722.48, 266.01) * mm, "radius": 1.6 * mm});
            skCircle(sketch, "E5.1.29.1", {"center": v(-717.48, 266.01) * mm, "radius": 1.6 * mm});
            skCircle(sketch, "E5.1.29.2", {"center": v(-719.98, 261.01) * mm, "radius": 1.6 * mm});
            skCircle(sketch, "E5.1.29.3", {"center": v(-714.98, 261.01) * mm, "radius": 1.6 * mm});
            skCircle(sketch, "E5.1.30.0", {"center": v(-722.48, 256.01) * mm, "radius": 1.6 * mm});
            skCircle(sketch, "E5.1.30.1", {"center": v(-717.48, 256.01) * mm, "radius": 1.6 * mm});
            skCircle(sketch, "E5.1.30.2", {"center": v(-719.98, 251.01) * mm, "radius": 1.6 * mm});
            skCircle(sketch, "E5.1.30.3", {"center": v(-714.98, 251.01) * mm, "radius": 1.6 * mm});
            skCircle(sketch, "E5.1.31.0", {"center": v(-722.48, 246.01) * mm, "radius": 1.6 * mm});
            skCircle(sketch, "E5.1.31.1", {"center": v(-717.48, 246.01) * mm, "radius": 1.6 * mm});
            skCircle(sketch, "E5.1.31.2", {"center": v(-719.98, 241.01) * mm, "radius": 1.6 * mm});
            skCircle(sketch, "E5.1.31.3", {"center": v(-714.98, 241.01) * mm, "radius": 1.6 * mm});
            skCircle(sketch, "E5.1.32.0", {"center": v(-722.48, 236.01) * mm, "radius": 1.6 * mm});
            skCircle(sketch, "E5.1.32.1", {"center": v(-717.48, 236.01) * mm, "radius": 1.6 * mm});
            skCircle(sketch, "E5.1.32.2", {"center": v(-719.98, 231.01) * mm, "radius": 1.6 * mm});
            skCircle(sketch, "E5.1.32.3", {"center": v(-714.98, 231.01) * mm, "radius": 1.6 * mm});
            skCircle(sketch, "E5.1.33.0", {"center": v(-722.48, 226.01) * mm, "radius": 1.6 * mm});
            skCircle(sketch, "E5.1.33.1", {"center": v(-717.48, 226.01) * mm, "radius": 1.6 * mm});
            skCircle(sketch, "E5.1.33.2", {"center": v(-719.98, 221.01) * mm, "radius": 1.6 * mm});
            skCircle(sketch, "E5.1.33.3", {"center": v(-714.98, 221.01) * mm, "radius": 1.6 * mm});
            skCircle(sketch, "E5.1.34.0", {"center": v(-722.48, 216.01) * mm, "radius": 1.6 * mm});
            skCircle(sketch, "E5.1.34.1", {"center": v(-717.48, 216.01) * mm, "radius": 1.6 * mm});
            skCircle(sketch, "E5.1.34.2", {"center": v(-719.98, 211.01) * mm, "radius": 1.6 * mm});
            skCircle(sketch, "E5.1.34.3", {"center": v(-714.98, 211.01) * mm, "radius": 1.6 * mm});
            skCircle(sketch, "E5.1.35.0", {"center": v(-722.48, 206.01) * mm, "radius": 1.6 * mm});
            skCircle(sketch, "E5.1.35.1", {"center": v(-717.48, 206.01) * mm, "radius": 1.6 * mm});
            skCircle(sketch, "E5.1.35.2", {"center": v(-719.98, 201.01) * mm, "radius": 1.6 * mm});
            skCircle(sketch, "E5.1.35.3", {"center": v(-714.98, 201.01) * mm, "radius": 1.6 * mm});
            skCircle(sketch, "E5.1.36.0", {"center": v(-722.48, 196.01) * mm, "radius": 1.6 * mm});
            skCircle(sketch, "E5.1.36.1", {"center": v(-717.48, 196.01) * mm, "radius": 1.6 * mm});
            skCircle(sketch, "E5.1.36.2", {"center": v(-719.98, 191.01) * mm, "radius": 1.6 * mm});
            skCircle(sketch, "E5.1.36.3", {"center": v(-714.98, 191.01) * mm, "radius": 1.6 * mm});
            skCircle(sketch, "E5.1.37.0", {"center": v(-722.48, 186.01) * mm, "radius": 1.6 * mm});
            skCircle(sketch, "E5.1.37.1", {"center": v(-717.48, 186.01) * mm, "radius": 1.6 * mm});
            skCircle(sketch, "E5.1.37.2", {"center": v(-719.98, 181.01) * mm, "radius": 1.6 * mm});
            skCircle(sketch, "E5.1.37.3", {"center": v(-714.98, 181.01) * mm, "radius": 1.6 * mm});
            skCircle(sketch, "E5.1.38.0", {"center": v(-722.48, 176.01) * mm, "radius": 1.6 * mm});
            skCircle(sketch, "E5.1.38.1", {"center": v(-717.48, 176.01) * mm, "radius": 1.6 * mm});
            skCircle(sketch, "E5.1.38.2", {"center": v(-719.98, 171.01) * mm, "radius": 1.6 * mm});
            skCircle(sketch, "E5.1.38.3", {"center": v(-714.98, 171.01) * mm, "radius": 1.6 * mm});
            skCircle(sketch, "E5.1.39.0", {"center": v(-722.48, 166.01) * mm, "radius": 1.6 * mm});
            skCircle(sketch, "E5.1.39.1", {"center": v(-717.48, 166.01) * mm, "radius": 1.6 * mm});
            skCircle(sketch, "E5.1.39.2", {"center": v(-719.98, 161.01) * mm, "radius": 1.6 * mm});
            skCircle(sketch, "E5.1.39.3", {"center": v(-714.98, 161.01) * mm, "radius": 1.6 * mm});
            skCircle(sketch, "E5.1.40.0", {"center": v(-722.48, 156.01) * mm, "radius": 1.6 * mm});
            skCircle(sketch, "E5.1.40.1", {"center": v(-717.48, 156.01) * mm, "radius": 1.6 * mm});
            skCircle(sketch, "E5.1.40.2", {"center": v(-719.98, 151.01) * mm, "radius": 1.6 * mm});
            skCircle(sketch, "E5.1.40.3", {"center": v(-714.98, 151.01) * mm, "radius": 1.6 * mm});
            skCircle(sketch, "E5.1.41.0", {"center": v(-722.48, 146.01) * mm, "radius": 1.6 * mm});
            skCircle(sketch, "E5.1.41.1", {"center": v(-717.48, 146.01) * mm, "radius": 1.6 * mm});
            skCircle(sketch, "E5.1.41.2", {"center": v(-719.98, 141.01) * mm, "radius": 1.6 * mm});
            skCircle(sketch, "E5.1.41.3", {"center": v(-714.98, 141.01) * mm, "radius": 1.6 * mm});
            skCircle(sketch, "E5.1.42.0", {"center": v(-722.48, 136.01) * mm, "radius": 1.6 * mm});
            skCircle(sketch, "E5.1.42.1", {"center": v(-717.48, 136.01) * mm, "radius": 1.6 * mm});
            skCircle(sketch, "E5.1.42.2", {"center": v(-719.98, 131.01) * mm, "radius": 1.6 * mm});
            skCircle(sketch, "E5.1.42.3", {"center": v(-714.98, 131.01) * mm, "radius": 1.6 * mm});
            skCircle(sketch, "E5.1.43.0", {"center": v(-722.48, 126.01) * mm, "radius": 1.6 * mm});
            skCircle(sketch, "E5.1.43.1", {"center": v(-717.48, 126.01) * mm, "radius": 1.6 * mm});
            skCircle(sketch, "E5.1.43.2", {"center": v(-719.98, 121.01) * mm, "radius": 1.6 * mm});
            skCircle(sketch, "E5.1.43.3", {"center": v(-714.98, 121.01) * mm, "radius": 1.6 * mm});
            skCircle(sketch, "E5.1.44.0", {"center": v(-722.48, 116.01) * mm, "radius": 1.6 * mm});
            skCircle(sketch, "E5.1.44.1", {"center": v(-717.48, 116.01) * mm, "radius": 1.6 * mm});
            skCircle(sketch, "E5.1.44.2", {"center": v(-719.98, 111.01) * mm, "radius": 1.6 * mm});
            skCircle(sketch, "E5.1.44.3", {"center": v(-714.98, 111.01) * mm, "radius": 1.6 * mm});
            skCircle(sketch, "E5.1.45.0", {"center": v(-722.48, 106.01) * mm, "radius": 1.6 * mm});
            skCircle(sketch, "E5.1.45.1", {"center": v(-717.48, 106.01) * mm, "radius": 1.6 * mm});
            skCircle(sketch, "E5.1.45.2", {"center": v(-719.98, 101.01) * mm, "radius": 1.6 * mm});
            skCircle(sketch, "E5.1.45.3", {"center": v(-714.98, 101.01) * mm, "radius": 1.6 * mm});
            skCircle(sketch, "E5.1.46.0", {"center": v(-722.48, 96.01) * mm, "radius": 1.6 * mm});
            skCircle(sketch, "E5.1.46.1", {"center": v(-717.48, 96.01) * mm, "radius": 1.6 * mm});
            skCircle(sketch, "E5.1.46.2", {"center": v(-719.98, 91.01) * mm, "radius": 1.6 * mm});
            skCircle(sketch, "E5.1.46.3", {"center": v(-714.98, 91.01) * mm, "radius": 1.6 * mm});
            skCircle(sketch, "E5.1.47.0", {"center": v(-722.48, 86.01) * mm, "radius": 1.6 * mm});
            skCircle(sketch, "E5.1.47.1", {"center": v(-717.48, 86.01) * mm, "radius": 1.6 * mm});
            skCircle(sketch, "E5.1.47.2", {"center": v(-719.98, 81.01) * mm, "radius": 1.6 * mm});
            skCircle(sketch, "E5.1.47.3", {"center": v(-714.98, 81.01) * mm, "radius": 1.6 * mm});
            skCircle(sketch, "E5.1.48.0", {"center": v(-722.48, 76.01) * mm, "radius": 1.6 * mm});
            skCircle(sketch, "E5.1.48.1", {"center": v(-717.48, 76.01) * mm, "radius": 1.6 * mm});
            skCircle(sketch, "E5.1.48.2", {"center": v(-719.98, 71.01) * mm, "radius": 1.6 * mm});
            skCircle(sketch, "E5.1.48.3", {"center": v(-714.98, 71.01) * mm, "radius": 1.6 * mm});
            skCircle(sketch, "E5.1.49.0", {"center": v(-722.48, 66.01) * mm, "radius": 1.6 * mm});
            skCircle(sketch, "E5.1.49.1", {"center": v(-717.48, 66.01) * mm, "radius": 1.6 * mm});
            skCircle(sketch, "E5.1.49.2", {"center": v(-719.98, 61.01) * mm, "radius": 1.6 * mm});
            skCircle(sketch, "E5.1.49.3", {"center": v(-714.98, 61.01) * mm, "radius": 1.6 * mm});
            skCircle(sketch, "E5.2.0.0", {"center": v(-712.48, 556.01) * mm, "radius": 1.6 * mm});
            skCircle(sketch, "E5.2.0.1", {"center": v(-707.48, 556.01) * mm, "radius": 1.6 * mm});
            skCircle(sketch, "E5.2.0.2", {"center": v(-709.98, 551.01) * mm, "radius": 1.6 * mm});
            skCircle(sketch, "E5.2.0.3", {"center": v(-704.98, 551.01) * mm, "radius": 1.6 * mm});
            skCircle(sketch, "E5.2.1.0", {"center": v(-712.48, 546.01) * mm, "radius": 1.6 * mm});
            skCircle(sketch, "E5.2.1.1", {"center": v(-707.48, 546.01) * mm, "radius": 1.6 * mm});
            skCircle(sketch, "E5.2.1.2", {"center": v(-709.98, 541.01) * mm, "radius": 1.6 * mm});
            skCircle(sketch, "E5.2.1.3", {"center": v(-704.98, 541.01) * mm, "radius": 1.6 * mm});
            skCircle(sketch, "E5.2.2.0", {"center": v(-712.48, 536.01) * mm, "radius": 1.6 * mm});
            skCircle(sketch, "E5.2.2.1", {"center": v(-707.48, 536.01) * mm, "radius": 1.6 * mm});
            skCircle(sketch, "E5.2.2.2", {"center": v(-709.98, 531.01) * mm, "radius": 1.6 * mm});
            skCircle(sketch, "E5.2.2.3", {"center": v(-704.98, 531.01) * mm, "radius": 1.6 * mm});
            skCircle(sketch, "E5.2.3.0", {"center": v(-712.48, 526.01) * mm, "radius": 1.6 * mm});
            skCircle(sketch, "E5.2.3.1", {"center": v(-707.48, 526.01) * mm, "radius": 1.6 * mm});
            skCircle(sketch, "E5.2.3.2", {"center": v(-709.98, 521.01) * mm, "radius": 1.6 * mm});
            skCircle(sketch, "E5.2.3.3", {"center": v(-704.98, 521.01) * mm, "radius": 1.6 * mm});
            skCircle(sketch, "E5.2.4.0", {"center": v(-712.48, 516.01) * mm, "radius": 1.6 * mm});
            skCircle(sketch, "E5.2.4.1", {"center": v(-707.48, 516.01) * mm, "radius": 1.6 * mm});
            skCircle(sketch, "E5.2.4.2", {"center": v(-709.98, 511.01) * mm, "radius": 1.6 * mm});
            skCircle(sketch, "E5.2.4.3", {"center": v(-704.98, 511.01) * mm, "radius": 1.6 * mm});
            skCircle(sketch, "E5.2.5.0", {"center": v(-712.48, 506.01) * mm, "radius": 1.6 * mm});
            skCircle(sketch, "E5.2.5.1", {"center": v(-707.48, 506.01) * mm, "radius": 1.6 * mm});
            skCircle(sketch, "E5.2.5.2", {"center": v(-709.98, 501.01) * mm, "radius": 1.6 * mm});
            skCircle(sketch, "E5.2.5.3", {"center": v(-704.98, 501.01) * mm, "radius": 1.6 * mm});
            skCircle(sketch, "E5.2.6.0", {"center": v(-712.48, 496.01) * mm, "radius": 1.6 * mm});
            skCircle(sketch, "E5.2.6.1", {"center": v(-707.48, 496.01) * mm, "radius": 1.6 * mm});
            skCircle(sketch, "E5.2.6.2", {"center": v(-709.98, 491.01) * mm, "radius": 1.6 * mm});
            skCircle(sketch, "E5.2.6.3", {"center": v(-704.98, 491.01) * mm, "radius": 1.6 * mm});
            skCircle(sketch, "E5.2.7.0", {"center": v(-712.48, 486.01) * mm, "radius": 1.6 * mm});
            skCircle(sketch, "E5.2.7.1", {"center": v(-707.48, 486.01) * mm, "radius": 1.6 * mm});
            skCircle(sketch, "E5.2.7.2", {"center": v(-709.98, 481.01) * mm, "radius": 1.6 * mm});
            skCircle(sketch, "E5.2.7.3", {"center": v(-704.98, 481.01) * mm, "radius": 1.6 * mm});
            skCircle(sketch, "E5.2.8.0", {"center": v(-712.48, 476.01) * mm, "radius": 1.6 * mm});
            skCircle(sketch, "E5.2.8.1", {"center": v(-707.48, 476.01) * mm, "radius": 1.6 * mm});
            skCircle(sketch, "E5.2.8.2", {"center": v(-709.98, 471.01) * mm, "radius": 1.6 * mm});
            skCircle(sketch, "E5.2.8.3", {"center": v(-704.98, 471.01) * mm, "radius": 1.6 * mm});
            skCircle(sketch, "E5.2.9.0", {"center": v(-712.48, 466.01) * mm, "radius": 1.6 * mm});
            skCircle(sketch, "E5.2.9.1", {"center": v(-707.48, 466.01) * mm, "radius": 1.6 * mm});
            skCircle(sketch, "E5.2.9.2", {"center": v(-709.98, 461.01) * mm, "radius": 1.6 * mm});
            skCircle(sketch, "E5.2.9.3", {"center": v(-704.98, 461.01) * mm, "radius": 1.6 * mm});
            skCircle(sketch, "E5.2.10.0", {"center": v(-712.48, 456.01) * mm, "radius": 1.6 * mm});
            skCircle(sketch, "E5.2.10.1", {"center": v(-707.48, 456.01) * mm, "radius": 1.6 * mm});
            skCircle(sketch, "E5.2.10.2", {"center": v(-709.98, 451.01) * mm, "radius": 1.6 * mm});
            skCircle(sketch, "E5.2.10.3", {"center": v(-704.98, 451.01) * mm, "radius": 1.6 * mm});
            skCircle(sketch, "E5.2.11.0", {"center": v(-712.48, 446.01) * mm, "radius": 1.6 * mm});
            skCircle(sketch, "E5.2.11.1", {"center": v(-707.48, 446.01) * mm, "radius": 1.6 * mm});
            skCircle(sketch, "E5.2.11.2", {"center": v(-709.98, 441.01) * mm, "radius": 1.6 * mm});
            skCircle(sketch, "E5.2.11.3", {"center": v(-704.98, 441.01) * mm, "radius": 1.6 * mm});
            skCircle(sketch, "E5.2.12.0", {"center": v(-712.48, 436.01) * mm, "radius": 1.6 * mm});
            skCircle(sketch, "E5.2.12.1", {"center": v(-707.48, 436.01) * mm, "radius": 1.6 * mm});
            skCircle(sketch, "E5.2.12.2", {"center": v(-709.98, 431.01) * mm, "radius": 1.6 * mm});
            skCircle(sketch, "E5.2.12.3", {"center": v(-704.98, 431.01) * mm, "radius": 1.6 * mm});
            skCircle(sketch, "E5.2.13.0", {"center": v(-712.48, 426.01) * mm, "radius": 1.6 * mm});
            skCircle(sketch, "E5.2.13.1", {"center": v(-707.48, 426.01) * mm, "radius": 1.6 * mm});
            skCircle(sketch, "E5.2.13.2", {"center": v(-709.98, 421.01) * mm, "radius": 1.6 * mm});
            skCircle(sketch, "E5.2.13.3", {"center": v(-704.98, 421.01) * mm, "radius": 1.6 * mm});
            skCircle(sketch, "E5.2.14.0", {"center": v(-712.48, 416.01) * mm, "radius": 1.6 * mm});
            skCircle(sketch, "E5.2.14.1", {"center": v(-707.48, 416.01) * mm, "radius": 1.6 * mm});
            skCircle(sketch, "E5.2.14.2", {"center": v(-709.98, 411.01) * mm, "radius": 1.6 * mm});
            skCircle(sketch, "E5.2.14.3", {"center": v(-704.98, 411.01) * mm, "radius": 1.6 * mm});
            skCircle(sketch, "E5.2.15.0", {"center": v(-712.48, 406.01) * mm, "radius": 1.6 * mm});
            skCircle(sketch, "E5.2.15.1", {"center": v(-707.48, 406.01) * mm, "radius": 1.6 * mm});
            skCircle(sketch, "E5.2.15.2", {"center": v(-709.98, 401.01) * mm, "radius": 1.6 * mm});
            skCircle(sketch, "E5.2.15.3", {"center": v(-704.98, 401.01) * mm, "radius": 1.6 * mm});
            skCircle(sketch, "E5.2.16.0", {"center": v(-712.48, 396.01) * mm, "radius": 1.6 * mm});
            skCircle(sketch, "E5.2.16.1", {"center": v(-707.48, 396.01) * mm, "radius": 1.6 * mm});
            skCircle(sketch, "E5.2.16.2", {"center": v(-709.98, 391.01) * mm, "radius": 1.6 * mm});
            skCircle(sketch, "E5.2.16.3", {"center": v(-704.98, 391.01) * mm, "radius": 1.6 * mm});
            skCircle(sketch, "E5.2.17.0", {"center": v(-712.48, 386.01) * mm, "radius": 1.6 * mm});
            skCircle(sketch, "E5.2.17.1", {"center": v(-707.48, 386.01) * mm, "radius": 1.6 * mm});
            skCircle(sketch, "E5.2.17.2", {"center": v(-709.98, 381.01) * mm, "radius": 1.6 * mm});
            skCircle(sketch, "E5.2.17.3", {"center": v(-704.98, 381.01) * mm, "radius": 1.6 * mm});
            skCircle(sketch, "E5.2.18.0", {"center": v(-712.48, 376.01) * mm, "radius": 1.6 * mm});
            skCircle(sketch, "E5.2.18.1", {"center": v(-707.48, 376.01) * mm, "radius": 1.6 * mm});
            skCircle(sketch, "E5.2.18.2", {"center": v(-709.98, 371.01) * mm, "radius": 1.6 * mm});
            skCircle(sketch, "E5.2.18.3", {"center": v(-704.98, 371.01) * mm, "radius": 1.6 * mm});
            skCircle(sketch, "E5.2.19.0", {"center": v(-712.48, 366.01) * mm, "radius": 1.6 * mm});
            skCircle(sketch, "E5.2.19.1", {"center": v(-707.48, 366.01) * mm, "radius": 1.6 * mm});
            skCircle(sketch, "E5.2.19.2", {"center": v(-709.98, 361.01) * mm, "radius": 1.6 * mm});
            skCircle(sketch, "E5.2.19.3", {"center": v(-704.98, 361.01) * mm, "radius": 1.6 * mm});
            skCircle(sketch, "E5.2.20.0", {"center": v(-712.48, 356.01) * mm, "radius": 1.6 * mm});
            skCircle(sketch, "E5.2.20.1", {"center": v(-707.48, 356.01) * mm, "radius": 1.6 * mm});
            skCircle(sketch, "E5.2.20.2", {"center": v(-709.98, 351.01) * mm, "radius": 1.6 * mm});
            skCircle(sketch, "E5.2.20.3", {"center": v(-704.98, 351.01) * mm, "radius": 1.6 * mm});
            skCircle(sketch, "E5.2.21.0", {"center": v(-712.48, 346.01) * mm, "radius": 1.6 * mm});
            skCircle(sketch, "E5.2.21.1", {"center": v(-707.48, 346.01) * mm, "radius": 1.6 * mm});
            skCircle(sketch, "E5.2.21.2", {"center": v(-709.98, 341.01) * mm, "radius": 1.6 * mm});
            skCircle(sketch, "E5.2.21.3", {"center": v(-704.98, 341.01) * mm, "radius": 1.6 * mm});
            skCircle(sketch, "E5.2.22.0", {"center": v(-712.48, 336.01) * mm, "radius": 1.6 * mm});
            skCircle(sketch, "E5.2.22.1", {"center": v(-707.48, 336.01) * mm, "radius": 1.6 * mm});
            skCircle(sketch, "E5.2.22.2", {"center": v(-709.98, 331.01) * mm, "radius": 1.6 * mm});
            skCircle(sketch, "E5.2.22.3", {"center": v(-704.98, 331.01) * mm, "radius": 1.6 * mm});
            skCircle(sketch, "E5.2.23.0", {"center": v(-712.48, 326.01) * mm, "radius": 1.6 * mm});
            skCircle(sketch, "E5.2.23.1", {"center": v(-707.48, 326.01) * mm, "radius": 1.6 * mm});
            skCircle(sketch, "E5.2.23.2", {"center": v(-709.98, 321.01) * mm, "radius": 1.6 * mm});
            skCircle(sketch, "E5.2.23.3", {"center": v(-704.98, 321.01) * mm, "radius": 1.6 * mm});
            skCircle(sketch, "E5.2.24.0", {"center": v(-712.48, 316.01) * mm, "radius": 1.6 * mm});
            skCircle(sketch, "E5.2.24.1", {"center": v(-707.48, 316.01) * mm, "radius": 1.6 * mm});
            skCircle(sketch, "E5.2.24.2", {"center": v(-709.98, 311.01) * mm, "radius": 1.6 * mm});
            skCircle(sketch, "E5.2.24.3", {"center": v(-704.98, 311.01) * mm, "radius": 1.6 * mm});
            skCircle(sketch, "E5.2.25.0", {"center": v(-712.48, 306.01) * mm, "radius": 1.6 * mm});
            skCircle(sketch, "E5.2.25.1", {"center": v(-707.48, 306.01) * mm, "radius": 1.6 * mm});
            skCircle(sketch, "E5.2.25.2", {"center": v(-709.98, 301.01) * mm, "radius": 1.6 * mm});
            skCircle(sketch, "E5.2.25.3", {"center": v(-704.98, 301.01) * mm, "radius": 1.6 * mm});
            skCircle(sketch, "E5.2.26.0", {"center": v(-712.48, 296.01) * mm, "radius": 1.6 * mm});
            skCircle(sketch, "E5.2.26.1", {"center": v(-707.48, 296.01) * mm, "radius": 1.6 * mm});
            skCircle(sketch, "E5.2.26.2", {"center": v(-709.98, 291.01) * mm, "radius": 1.6 * mm});
            skCircle(sketch, "E5.2.26.3", {"center": v(-704.98, 291.01) * mm, "radius": 1.6 * mm});
            skCircle(sketch, "E5.2.27.0", {"center": v(-712.48, 286.01) * mm, "radius": 1.6 * mm});
            skCircle(sketch, "E5.2.27.1", {"center": v(-707.48, 286.01) * mm, "radius": 1.6 * mm});
            skCircle(sketch, "E5.2.27.2", {"center": v(-709.98, 281.01) * mm, "radius": 1.6 * mm});
            skCircle(sketch, "E5.2.27.3", {"center": v(-704.98, 281.01) * mm, "radius": 1.6 * mm});
            skCircle(sketch, "E5.2.28.0", {"center": v(-712.48, 276.01) * mm, "radius": 1.6 * mm});
            skCircle(sketch, "E5.2.28.1", {"center": v(-707.48, 276.01) * mm, "radius": 1.6 * mm});
            skCircle(sketch, "E5.2.28.2", {"center": v(-709.98, 271.01) * mm, "radius": 1.6 * mm});
            skCircle(sketch, "E5.2.28.3", {"center": v(-704.98, 271.01) * mm, "radius": 1.6 * mm});
            skCircle(sketch, "E5.2.29.0", {"center": v(-712.48, 266.01) * mm, "radius": 1.6 * mm});
            skCircle(sketch, "E5.2.29.1", {"center": v(-707.48, 266.01) * mm, "radius": 1.6 * mm});
            skCircle(sketch, "E5.2.29.2", {"center": v(-709.98, 261.01) * mm, "radius": 1.6 * mm});
            skCircle(sketch, "E5.2.29.3", {"center": v(-704.98, 261.01) * mm, "radius": 1.6 * mm});
            skCircle(sketch, "E5.2.30.0", {"center": v(-712.48, 256.01) * mm, "radius": 1.6 * mm});
            skCircle(sketch, "E5.2.30.1", {"center": v(-707.48, 256.01) * mm, "radius": 1.6 * mm});
            skCircle(sketch, "E5.2.30.2", {"center": v(-709.98, 251.01) * mm, "radius": 1.6 * mm});
            skCircle(sketch, "E5.2.30.3", {"center": v(-704.98, 251.01) * mm, "radius": 1.6 * mm});
            skCircle(sketch, "E5.2.31.0", {"center": v(-712.48, 246.01) * mm, "radius": 1.6 * mm});
            skCircle(sketch, "E5.2.31.1", {"center": v(-707.48, 246.01) * mm, "radius": 1.6 * mm});
            skCircle(sketch, "E5.2.31.2", {"center": v(-709.98, 241.01) * mm, "radius": 1.6 * mm});
            skCircle(sketch, "E5.2.31.3", {"center": v(-704.98, 241.01) * mm, "radius": 1.6 * mm});
            skCircle(sketch, "E5.2.32.0", {"center": v(-712.48, 236.01) * mm, "radius": 1.6 * mm});
            skCircle(sketch, "E5.2.32.1", {"center": v(-707.48, 236.01) * mm, "radius": 1.6 * mm});
            skCircle(sketch, "E5.2.32.2", {"center": v(-709.98, 231.01) * mm, "radius": 1.6 * mm});
            skCircle(sketch, "E5.2.32.3", {"center": v(-704.98, 231.01) * mm, "radius": 1.6 * mm});
            skCircle(sketch, "E5.2.33.0", {"center": v(-712.48, 226.01) * mm, "radius": 1.6 * mm});
            skCircle(sketch, "E5.2.33.1", {"center": v(-707.48, 226.01) * mm, "radius": 1.6 * mm});
            skCircle(sketch, "E5.2.33.2", {"center": v(-709.98, 221.01) * mm, "radius": 1.6 * mm});
            skCircle(sketch, "E5.2.33.3", {"center": v(-704.98, 221.01) * mm, "radius": 1.6 * mm});
            skCircle(sketch, "E5.2.34.0", {"center": v(-712.48, 216.01) * mm, "radius": 1.6 * mm});
            skCircle(sketch, "E5.2.34.1", {"center": v(-707.48, 216.01) * mm, "radius": 1.6 * mm});
            skCircle(sketch, "E5.2.34.2", {"center": v(-709.98, 211.01) * mm, "radius": 1.6 * mm});
            skCircle(sketch, "E5.2.34.3", {"center": v(-704.98, 211.01) * mm, "radius": 1.6 * mm});
            skCircle(sketch, "E5.2.35.0", {"center": v(-712.48, 206.01) * mm, "radius": 1.6 * mm});
            skCircle(sketch, "E5.2.35.1", {"center": v(-707.48, 206.01) * mm, "radius": 1.6 * mm});
            skCircle(sketch, "E5.2.35.2", {"center": v(-709.98, 201.01) * mm, "radius": 1.6 * mm});
            skCircle(sketch, "E5.2.35.3", {"center": v(-704.98, 201.01) * mm, "radius": 1.6 * mm});
            skCircle(sketch, "E5.2.36.0", {"center": v(-712.48, 196.01) * mm, "radius": 1.6 * mm});
            skCircle(sketch, "E5.2.36.1", {"center": v(-707.48, 196.01) * mm, "radius": 1.6 * mm});
            skCircle(sketch, "E5.2.36.2", {"center": v(-709.98, 191.01) * mm, "radius": 1.6 * mm});
            skCircle(sketch, "E5.2.36.3", {"center": v(-704.98, 191.01) * mm, "radius": 1.6 * mm});
            skCircle(sketch, "E5.2.37.0", {"center": v(-712.48, 186.01) * mm, "radius": 1.6 * mm});
            skCircle(sketch, "E5.2.37.1", {"center": v(-707.48, 186.01) * mm, "radius": 1.6 * mm});
            skCircle(sketch, "E5.2.37.2", {"center": v(-709.98, 181.01) * mm, "radius": 1.6 * mm});
            skCircle(sketch, "E5.2.37.3", {"center": v(-704.98, 181.01) * mm, "radius": 1.6 * mm});
            skCircle(sketch, "E5.2.38.0", {"center": v(-712.48, 176.01) * mm, "radius": 1.6 * mm});
            skCircle(sketch, "E5.2.38.1", {"center": v(-707.48, 176.01) * mm, "radius": 1.6 * mm});
            skCircle(sketch, "E5.2.38.2", {"center": v(-709.98, 171.01) * mm, "radius": 1.6 * mm});
            skCircle(sketch, "E5.2.38.3", {"center": v(-704.98, 171.01) * mm, "radius": 1.6 * mm});
            skCircle(sketch, "E5.2.39.0", {"center": v(-712.48, 166.01) * mm, "radius": 1.6 * mm});
            skCircle(sketch, "E5.2.39.1", {"center": v(-707.48, 166.01) * mm, "radius": 1.6 * mm});
            skCircle(sketch, "E5.2.39.2", {"center": v(-709.98, 161.01) * mm, "radius": 1.6 * mm});
            skCircle(sketch, "E5.2.39.3", {"center": v(-704.98, 161.01) * mm, "radius": 1.6 * mm});
            skCircle(sketch, "E5.2.40.0", {"center": v(-712.48, 156.01) * mm, "radius": 1.6 * mm});
            skCircle(sketch, "E5.2.40.1", {"center": v(-707.48, 156.01) * mm, "radius": 1.6 * mm});
            skCircle(sketch, "E5.2.40.2", {"center": v(-709.98, 151.01) * mm, "radius": 1.6 * mm});
            skCircle(sketch, "E5.2.40.3", {"center": v(-704.98, 151.01) * mm, "radius": 1.6 * mm});
            skCircle(sketch, "E5.2.41.0", {"center": v(-712.48, 146.01) * mm, "radius": 1.6 * mm});
            skCircle(sketch, "E5.2.41.1", {"center": v(-707.48, 146.01) * mm, "radius": 1.6 * mm});
            skCircle(sketch, "E5.2.41.2", {"center": v(-709.98, 141.01) * mm, "radius": 1.6 * mm});
            skCircle(sketch, "E5.2.41.3", {"center": v(-704.98, 141.01) * mm, "radius": 1.6 * mm});
            skCircle(sketch, "E5.2.42.0", {"center": v(-712.48, 136.01) * mm, "radius": 1.6 * mm});
            skCircle(sketch, "E5.2.42.1", {"center": v(-707.48, 136.01) * mm, "radius": 1.6 * mm});
            skCircle(sketch, "E5.2.42.2", {"center": v(-709.98, 131.01) * mm, "radius": 1.6 * mm});
            skCircle(sketch, "E5.2.42.3", {"center": v(-704.98, 131.01) * mm, "radius": 1.6 * mm});
            skCircle(sketch, "E5.2.43.0", {"center": v(-712.48, 126.01) * mm, "radius": 1.6 * mm});
            skCircle(sketch, "E5.2.43.1", {"center": v(-707.48, 126.01) * mm, "radius": 1.6 * mm});
            skCircle(sketch, "E5.2.43.2", {"center": v(-709.98, 121.01) * mm, "radius": 1.6 * mm});
            skCircle(sketch, "E5.2.43.3", {"center": v(-704.98, 121.01) * mm, "radius": 1.6 * mm});
            skCircle(sketch, "E5.2.44.0", {"center": v(-712.48, 116.01) * mm, "radius": 1.6 * mm});
            skCircle(sketch, "E5.2.44.1", {"center": v(-707.48, 116.01) * mm, "radius": 1.6 * mm});
            skCircle(sketch, "E5.2.44.2", {"center": v(-709.98, 111.01) * mm, "radius": 1.6 * mm});
            skCircle(sketch, "E5.2.44.3", {"center": v(-704.98, 111.01) * mm, "radius": 1.6 * mm});
            skCircle(sketch, "E5.2.45.0", {"center": v(-712.48, 106.01) * mm, "radius": 1.6 * mm});
            skCircle(sketch, "E5.2.45.1", {"center": v(-707.48, 106.01) * mm, "radius": 1.6 * mm});
            skCircle(sketch, "E5.2.45.2", {"center": v(-709.98, 101.01) * mm, "radius": 1.6 * mm});
            skCircle(sketch, "E5.2.45.3", {"center": v(-704.98, 101.01) * mm, "radius": 1.6 * mm});
            skCircle(sketch, "E5.2.46.0", {"center": v(-712.48, 96.01) * mm, "radius": 1.6 * mm});
            skCircle(sketch, "E5.2.46.1", {"center": v(-707.48, 96.01) * mm, "radius": 1.6 * mm});
            skCircle(sketch, "E5.2.46.2", {"center": v(-709.98, 91.01) * mm, "radius": 1.6 * mm});
            skCircle(sketch, "E5.2.46.3", {"center": v(-704.98, 91.01) * mm, "radius": 1.6 * mm});
            skCircle(sketch, "E5.2.47.0", {"center": v(-712.48, 86.01) * mm, "radius": 1.6 * mm});
            skCircle(sketch, "E5.2.47.1", {"center": v(-707.48, 86.01) * mm, "radius": 1.6 * mm});
            skCircle(sketch, "E5.2.47.2", {"center": v(-709.98, 81.01) * mm, "radius": 1.6 * mm});
            skCircle(sketch, "E5.2.47.3", {"center": v(-704.98, 81.01) * mm, "radius": 1.6 * mm});
            skCircle(sketch, "E5.2.48.0", {"center": v(-712.48, 76.01) * mm, "radius": 1.6 * mm});
            skCircle(sketch, "E5.2.48.1", {"center": v(-707.48, 76.01) * mm, "radius": 1.6 * mm});
            skCircle(sketch, "E5.2.48.2", {"center": v(-709.98, 71.01) * mm, "radius": 1.6 * mm});
            skCircle(sketch, "E5.2.48.3", {"center": v(-704.98, 71.01) * mm, "radius": 1.6 * mm});
            skCircle(sketch, "E5.2.49.0", {"center": v(-712.48, 66.01) * mm, "radius": 1.6 * mm});
            skCircle(sketch, "E5.2.49.1", {"center": v(-707.48, 66.01) * mm, "radius": 1.6 * mm});
            skCircle(sketch, "E5.2.49.2", {"center": v(-709.98, 61.01) * mm, "radius": 1.6 * mm});
            skCircle(sketch, "E5.2.49.3", {"center": v(-704.98, 61.01) * mm, "radius": 1.6 * mm});
            skCircle(sketch, "E5.3.0.0", {"center": v(-702.48, 556.01) * mm, "radius": 1.6 * mm});
            skCircle(sketch, "E5.3.0.1", {"center": v(-697.48, 556.01) * mm, "radius": 1.6 * mm});
            skCircle(sketch, "E5.3.0.2", {"center": v(-699.98, 551.01) * mm, "radius": 1.6 * mm});
            skCircle(sketch, "E5.3.0.3", {"center": v(-694.98, 551.01) * mm, "radius": 1.6 * mm});
            skCircle(sketch, "E5.3.1.0", {"center": v(-702.48, 546.01) * mm, "radius": 1.6 * mm});
            skCircle(sketch, "E5.3.1.1", {"center": v(-697.48, 546.01) * mm, "radius": 1.6 * mm});
            skCircle(sketch, "E5.3.1.2", {"center": v(-699.98, 541.01) * mm, "radius": 1.6 * mm});
            skCircle(sketch, "E5.3.1.3", {"center": v(-694.98, 541.01) * mm, "radius": 1.6 * mm});
            skCircle(sketch, "E5.3.2.0", {"center": v(-702.48, 536.01) * mm, "radius": 1.6 * mm});
            skCircle(sketch, "E5.3.2.1", {"center": v(-697.48, 536.01) * mm, "radius": 1.6 * mm});
            skCircle(sketch, "E5.3.2.2", {"center": v(-699.98, 531.01) * mm, "radius": 1.6 * mm});
            skCircle(sketch, "E5.3.2.3", {"center": v(-694.98, 531.01) * mm, "radius": 1.6 * mm});
            skCircle(sketch, "E5.3.3.0", {"center": v(-702.48, 526.01) * mm, "radius": 1.6 * mm});
            skCircle(sketch, "E5.3.3.1", {"center": v(-697.48, 526.01) * mm, "radius": 1.6 * mm});
            skCircle(sketch, "E5.3.3.2", {"center": v(-699.98, 521.01) * mm, "radius": 1.6 * mm});
            skCircle(sketch, "E5.3.3.3", {"center": v(-694.98, 521.01) * mm, "radius": 1.6 * mm});
            skCircle(sketch, "E5.3.4.0", {"center": v(-702.48, 516.01) * mm, "radius": 1.6 * mm});
            skCircle(sketch, "E5.3.4.1", {"center": v(-697.48, 516.01) * mm, "radius": 1.6 * mm});
            skCircle(sketch, "E5.3.4.2", {"center": v(-699.98, 511.01) * mm, "radius": 1.6 * mm});
            skCircle(sketch, "E5.3.4.3", {"center": v(-694.98, 511.01) * mm, "radius": 1.6 * mm});
            skCircle(sketch, "E5.3.5.0", {"center": v(-702.48, 506.01) * mm, "radius": 1.6 * mm});
            skCircle(sketch, "E5.3.5.1", {"center": v(-697.48, 506.01) * mm, "radius": 1.6 * mm});
            skCircle(sketch, "E5.3.5.2", {"center": v(-699.98, 501.01) * mm, "radius": 1.6 * mm});
            skCircle(sketch, "E5.3.5.3", {"center": v(-694.98, 501.01) * mm, "radius": 1.6 * mm});
            skCircle(sketch, "E5.3.6.0", {"center": v(-702.48, 496.01) * mm, "radius": 1.6 * mm});
            skCircle(sketch, "E5.3.6.1", {"center": v(-697.48, 496.01) * mm, "radius": 1.6 * mm});
            skCircle(sketch, "E5.3.6.2", {"center": v(-699.98, 491.01) * mm, "radius": 1.6 * mm});
            skCircle(sketch, "E5.3.6.3", {"center": v(-694.98, 491.01) * mm, "radius": 1.6 * mm});
            skCircle(sketch, "E5.3.7.0", {"center": v(-702.48, 486.01) * mm, "radius": 1.6 * mm});
            skCircle(sketch, "E5.3.7.1", {"center": v(-697.48, 486.01) * mm, "radius": 1.6 * mm});
            skCircle(sketch, "E5.3.7.2", {"center": v(-699.98, 481.01) * mm, "radius": 1.6 * mm});
            skCircle(sketch, "E5.3.7.3", {"center": v(-694.98, 481.01) * mm, "radius": 1.6 * mm});
            skCircle(sketch, "E5.3.8.0", {"center": v(-702.48, 476.01) * mm, "radius": 1.6 * mm});
            skCircle(sketch, "E5.3.8.1", {"center": v(-697.48, 476.01) * mm, "radius": 1.6 * mm});
            skCircle(sketch, "E5.3.8.2", {"center": v(-699.98, 471.01) * mm, "radius": 1.6 * mm});
            skCircle(sketch, "E5.3.8.3", {"center": v(-694.98, 471.01) * mm, "radius": 1.6 * mm});
            skCircle(sketch, "E5.3.9.0", {"center": v(-702.48, 466.01) * mm, "radius": 1.6 * mm});
            skCircle(sketch, "E5.3.9.1", {"center": v(-697.48, 466.01) * mm, "radius": 1.6 * mm});
            skCircle(sketch, "E5.3.9.2", {"center": v(-699.98, 461.01) * mm, "radius": 1.6 * mm});
            skCircle(sketch, "E5.3.9.3", {"center": v(-694.98, 461.01) * mm, "radius": 1.6 * mm});
            skCircle(sketch, "E5.3.10.0", {"center": v(-702.48, 456.01) * mm, "radius": 1.6 * mm});
            skCircle(sketch, "E5.3.10.1", {"center": v(-697.48, 456.01) * mm, "radius": 1.6 * mm});
            skCircle(sketch, "E5.3.10.2", {"center": v(-699.98, 451.01) * mm, "radius": 1.6 * mm});
            skCircle(sketch, "E5.3.10.3", {"center": v(-694.98, 451.01) * mm, "radius": 1.6 * mm});
            skCircle(sketch, "E5.3.11.0", {"center": v(-702.48, 446.01) * mm, "radius": 1.6 * mm});
            skCircle(sketch, "E5.3.11.1", {"center": v(-697.48, 446.01) * mm, "radius": 1.6 * mm});
            skCircle(sketch, "E5.3.11.2", {"center": v(-699.98, 441.01) * mm, "radius": 1.6 * mm});
            skCircle(sketch, "E5.3.11.3", {"center": v(-694.98, 441.01) * mm, "radius": 1.6 * mm});
            skCircle(sketch, "E5.3.12.0", {"center": v(-702.48, 436.01) * mm, "radius": 1.6 * mm});
            skCircle(sketch, "E5.3.12.1", {"center": v(-697.48, 436.01) * mm, "radius": 1.6 * mm});
            skCircle(sketch, "E5.3.12.2", {"center": v(-699.98, 431.01) * mm, "radius": 1.6 * mm});
            skCircle(sketch, "E5.3.12.3", {"center": v(-694.98, 431.01) * mm, "radius": 1.6 * mm});
            skCircle(sketch, "E5.3.13.0", {"center": v(-702.48, 426.01) * mm, "radius": 1.6 * mm});
            skCircle(sketch, "E5.3.13.1", {"center": v(-697.48, 426.01) * mm, "radius": 1.6 * mm});
            skCircle(sketch, "E5.3.13.2", {"center": v(-699.98, 421.01) * mm, "radius": 1.6 * mm});
            skCircle(sketch, "E5.3.13.3", {"center": v(-694.98, 421.01) * mm, "radius": 1.6 * mm});
            skCircle(sketch, "E5.3.14.0", {"center": v(-702.48, 416.01) * mm, "radius": 1.6 * mm});
            skCircle(sketch, "E5.3.14.1", {"center": v(-697.48, 416.01) * mm, "radius": 1.6 * mm});
            skCircle(sketch, "E5.3.14.2", {"center": v(-699.98, 411.01) * mm, "radius": 1.6 * mm});
            skCircle(sketch, "E5.3.14.3", {"center": v(-694.98, 411.01) * mm, "radius": 1.6 * mm});
            skCircle(sketch, "E5.3.15.0", {"center": v(-702.48, 406.01) * mm, "radius": 1.6 * mm});
            skCircle(sketch, "E5.3.15.1", {"center": v(-697.48, 406.01) * mm, "radius": 1.6 * mm});
            skCircle(sketch, "E5.3.15.2", {"center": v(-699.98, 401.01) * mm, "radius": 1.6 * mm});
            skCircle(sketch, "E5.3.15.3", {"center": v(-694.98, 401.01) * mm, "radius": 1.6 * mm});
            skCircle(sketch, "E5.3.16.0", {"center": v(-702.48, 396.01) * mm, "radius": 1.6 * mm});
            skCircle(sketch, "E5.3.16.1", {"center": v(-697.48, 396.01) * mm, "radius": 1.6 * mm});
            skCircle(sketch, "E5.3.16.2", {"center": v(-699.98, 391.01) * mm, "radius": 1.6 * mm});
            skCircle(sketch, "E5.3.16.3", {"center": v(-694.98, 391.01) * mm, "radius": 1.6 * mm});
            skCircle(sketch, "E5.3.17.0", {"center": v(-702.48, 386.01) * mm, "radius": 1.6 * mm});
            skCircle(sketch, "E5.3.17.1", {"center": v(-697.48, 386.01) * mm, "radius": 1.6 * mm});
            skCircle(sketch, "E5.3.17.2", {"center": v(-699.98, 381.01) * mm, "radius": 1.6 * mm});
            skCircle(sketch, "E5.3.17.3", {"center": v(-694.98, 381.01) * mm, "radius": 1.6 * mm});
            skCircle(sketch, "E5.3.18.0", {"center": v(-702.48, 376.01) * mm, "radius": 1.6 * mm});
            skCircle(sketch, "E5.3.18.1", {"center": v(-697.48, 376.01) * mm, "radius": 1.6 * mm});
            skCircle(sketch, "E5.3.18.2", {"center": v(-699.98, 371.01) * mm, "radius": 1.6 * mm});
            skCircle(sketch, "E5.3.18.3", {"center": v(-694.98, 371.01) * mm, "radius": 1.6 * mm});
            skCircle(sketch, "E5.3.19.0", {"center": v(-702.48, 366.01) * mm, "radius": 1.6 * mm});
            skCircle(sketch, "E5.3.19.1", {"center": v(-697.48, 366.01) * mm, "radius": 1.6 * mm});
            skCircle(sketch, "E5.3.19.2", {"center": v(-699.98, 361.01) * mm, "radius": 1.6 * mm});
            skCircle(sketch, "E5.3.19.3", {"center": v(-694.98, 361.01) * mm, "radius": 1.6 * mm});
            skCircle(sketch, "E5.3.20.0", {"center": v(-702.48, 356.01) * mm, "radius": 1.6 * mm});
            skCircle(sketch, "E5.3.20.1", {"center": v(-697.48, 356.01) * mm, "radius": 1.6 * mm});
            skCircle(sketch, "E5.3.20.2", {"center": v(-699.98, 351.01) * mm, "radius": 1.6 * mm});
            skCircle(sketch, "E5.3.20.3", {"center": v(-694.98, 351.01) * mm, "radius": 1.6 * mm});
            skCircle(sketch, "E5.3.21.0", {"center": v(-702.48, 346.01) * mm, "radius": 1.6 * mm});
            skCircle(sketch, "E5.3.21.1", {"center": v(-697.48, 346.01) * mm, "radius": 1.6 * mm});
            skCircle(sketch, "E5.3.21.2", {"center": v(-699.98, 341.01) * mm, "radius": 1.6 * mm});
            skCircle(sketch, "E5.3.21.3", {"center": v(-694.98, 341.01) * mm, "radius": 1.6 * mm});
            skCircle(sketch, "E5.3.22.0", {"center": v(-702.48, 336.01) * mm, "radius": 1.6 * mm});
            skCircle(sketch, "E5.3.22.1", {"center": v(-697.48, 336.01) * mm, "radius": 1.6 * mm});
            skCircle(sketch, "E5.3.22.2", {"center": v(-699.98, 331.01) * mm, "radius": 1.6 * mm});
            skCircle(sketch, "E5.3.22.3", {"center": v(-694.98, 331.01) * mm, "radius": 1.6 * mm});
            skCircle(sketch, "E5.3.23.0", {"center": v(-702.48, 326.01) * mm, "radius": 1.6 * mm});
            skCircle(sketch, "E5.3.23.1", {"center": v(-697.48, 326.01) * mm, "radius": 1.6 * mm});
            skCircle(sketch, "E5.3.23.2", {"center": v(-699.98, 321.01) * mm, "radius": 1.6 * mm});
            skCircle(sketch, "E5.3.23.3", {"center": v(-694.98, 321.01) * mm, "radius": 1.6 * mm});
            skCircle(sketch, "E5.3.24.0", {"center": v(-702.48, 316.01) * mm, "radius": 1.6 * mm});
            skCircle(sketch, "E5.3.24.1", {"center": v(-697.48, 316.01) * mm, "radius": 1.6 * mm});
            skCircle(sketch, "E5.3.24.2", {"center": v(-699.98, 311.01) * mm, "radius": 1.6 * mm});
            skCircle(sketch, "E5.3.24.3", {"center": v(-694.98, 311.01) * mm, "radius": 1.6 * mm});
            skCircle(sketch, "E5.3.25.0", {"center": v(-702.48, 306.01) * mm, "radius": 1.6 * mm});
            skCircle(sketch, "E5.3.25.1", {"center": v(-697.48, 306.01) * mm, "radius": 1.6 * mm});
            skCircle(sketch, "E5.3.25.2", {"center": v(-699.98, 301.01) * mm, "radius": 1.6 * mm});
            skCircle(sketch, "E5.3.25.3", {"center": v(-694.98, 301.01) * mm, "radius": 1.6 * mm});
            skCircle(sketch, "E5.3.26.0", {"center": v(-702.48, 296.01) * mm, "radius": 1.6 * mm});
            skCircle(sketch, "E5.3.26.1", {"center": v(-697.48, 296.01) * mm, "radius": 1.6 * mm});
            skCircle(sketch, "E5.3.26.2", {"center": v(-699.98, 291.01) * mm, "radius": 1.6 * mm});
            skCircle(sketch, "E5.3.26.3", {"center": v(-694.98, 291.01) * mm, "radius": 1.6 * mm});
            skCircle(sketch, "E5.3.27.0", {"center": v(-702.48, 286.01) * mm, "radius": 1.6 * mm});
            skCircle(sketch, "E5.3.27.1", {"center": v(-697.48, 286.01) * mm, "radius": 1.6 * mm});
            skCircle(sketch, "E5.3.27.2", {"center": v(-699.98, 281.01) * mm, "radius": 1.6 * mm});
            skCircle(sketch, "E5.3.27.3", {"center": v(-694.98, 281.01) * mm, "radius": 1.6 * mm});
            skCircle(sketch, "E5.3.28.0", {"center": v(-702.48, 276.01) * mm, "radius": 1.6 * mm});
            skCircle(sketch, "E5.3.28.1", {"center": v(-697.48, 276.01) * mm, "radius": 1.6 * mm});
            skCircle(sketch, "E5.3.28.2", {"center": v(-699.98, 271.01) * mm, "radius": 1.6 * mm});
            skCircle(sketch, "E5.3.28.3", {"center": v(-694.98, 271.01) * mm, "radius": 1.6 * mm});
            skCircle(sketch, "E5.3.29.0", {"center": v(-702.48, 266.01) * mm, "radius": 1.6 * mm});
            skCircle(sketch, "E5.3.29.1", {"center": v(-697.48, 266.01) * mm, "radius": 1.6 * mm});
            skCircle(sketch, "E5.3.29.2", {"center": v(-699.98, 261.01) * mm, "radius": 1.6 * mm});
            skCircle(sketch, "E5.3.29.3", {"center": v(-694.98, 261.01) * mm, "radius": 1.6 * mm});
            skCircle(sketch, "E5.3.30.0", {"center": v(-702.48, 256.01) * mm, "radius": 1.6 * mm});
            skCircle(sketch, "E5.3.30.1", {"center": v(-697.48, 256.01) * mm, "radius": 1.6 * mm});
            skCircle(sketch, "E5.3.30.2", {"center": v(-699.98, 251.01) * mm, "radius": 1.6 * mm});
            skCircle(sketch, "E5.3.30.3", {"center": v(-694.98, 251.01) * mm, "radius": 1.6 * mm});
            skCircle(sketch, "E5.3.31.0", {"center": v(-702.48, 246.01) * mm, "radius": 1.6 * mm});
            skCircle(sketch, "E5.3.31.1", {"center": v(-697.48, 246.01) * mm, "radius": 1.6 * mm});
            skCircle(sketch, "E5.3.31.2", {"center": v(-699.98, 241.01) * mm, "radius": 1.6 * mm});
            skCircle(sketch, "E5.3.31.3", {"center": v(-694.98, 241.01) * mm, "radius": 1.6 * mm});
            skCircle(sketch, "E5.3.32.0", {"center": v(-702.48, 236.01) * mm, "radius": 1.6 * mm});
            skCircle(sketch, "E5.3.32.1", {"center": v(-697.48, 236.01) * mm, "radius": 1.6 * mm});
            skCircle(sketch, "E5.3.32.2", {"center": v(-699.98, 231.01) * mm, "radius": 1.6 * mm});
            skCircle(sketch, "E5.3.32.3", {"center": v(-694.98, 231.01) * mm, "radius": 1.6 * mm});
            skCircle(sketch, "E5.3.33.0", {"center": v(-702.48, 226.01) * mm, "radius": 1.6 * mm});
            skCircle(sketch, "E5.3.33.1", {"center": v(-697.48, 226.01) * mm, "radius": 1.6 * mm});
            skCircle(sketch, "E5.3.33.2", {"center": v(-699.98, 221.01) * mm, "radius": 1.6 * mm});
            skCircle(sketch, "E5.3.33.3", {"center": v(-694.98, 221.01) * mm, "radius": 1.6 * mm});
            skCircle(sketch, "E5.3.34.0", {"center": v(-702.48, 216.01) * mm, "radius": 1.6 * mm});
            skCircle(sketch, "E5.3.34.1", {"center": v(-697.48, 216.01) * mm, "radius": 1.6 * mm});
            skCircle(sketch, "E5.3.34.2", {"center": v(-699.98, 211.01) * mm, "radius": 1.6 * mm});
            skCircle(sketch, "E5.3.34.3", {"center": v(-694.98, 211.01) * mm, "radius": 1.6 * mm});
            skCircle(sketch, "E5.3.35.0", {"center": v(-702.48, 206.01) * mm, "radius": 1.6 * mm});
            skCircle(sketch, "E5.3.35.1", {"center": v(-697.48, 206.01) * mm, "radius": 1.6 * mm});
            skCircle(sketch, "E5.3.35.2", {"center": v(-699.98, 201.01) * mm, "radius": 1.6 * mm});
            skCircle(sketch, "E5.3.35.3", {"center": v(-694.98, 201.01) * mm, "radius": 1.6 * mm});
            skCircle(sketch, "E5.3.36.0", {"center": v(-702.48, 196.01) * mm, "radius": 1.6 * mm});
            skCircle(sketch, "E5.3.36.1", {"center": v(-697.48, 196.01) * mm, "radius": 1.6 * mm});
            skCircle(sketch, "E5.3.36.2", {"center": v(-699.98, 191.01) * mm, "radius": 1.6 * mm});
            skCircle(sketch, "E5.3.36.3", {"center": v(-694.98, 191.01) * mm, "radius": 1.6 * mm});
            skCircle(sketch, "E5.3.37.0", {"center": v(-702.48, 186.01) * mm, "radius": 1.6 * mm});
            skCircle(sketch, "E5.3.37.1", {"center": v(-697.48, 186.01) * mm, "radius": 1.6 * mm});
            skCircle(sketch, "E5.3.37.2", {"center": v(-699.98, 181.01) * mm, "radius": 1.6 * mm});
            skCircle(sketch, "E5.3.37.3", {"center": v(-694.98, 181.01) * mm, "radius": 1.6 * mm});
            skCircle(sketch, "E5.3.38.0", {"center": v(-702.48, 176.01) * mm, "radius": 1.6 * mm});
            skCircle(sketch, "E5.3.38.1", {"center": v(-697.48, 176.01) * mm, "radius": 1.6 * mm});
            skCircle(sketch, "E5.3.38.2", {"center": v(-699.98, 171.01) * mm, "radius": 1.6 * mm});
            skCircle(sketch, "E5.3.38.3", {"center": v(-694.98, 171.01) * mm, "radius": 1.6 * mm});
            skCircle(sketch, "E5.3.39.0", {"center": v(-702.48, 166.01) * mm, "radius": 1.6 * mm});
            skCircle(sketch, "E5.3.39.1", {"center": v(-697.48, 166.01) * mm, "radius": 1.6 * mm});
            skCircle(sketch, "E5.3.39.2", {"center": v(-699.98, 161.01) * mm, "radius": 1.6 * mm});
            skCircle(sketch, "E5.3.39.3", {"center": v(-694.98, 161.01) * mm, "radius": 1.6 * mm});
            skCircle(sketch, "E5.3.40.0", {"center": v(-702.48, 156.01) * mm, "radius": 1.6 * mm});
            skCircle(sketch, "E5.3.40.1", {"center": v(-697.48, 156.01) * mm, "radius": 1.6 * mm});
            skCircle(sketch, "E5.3.40.2", {"center": v(-699.98, 151.01) * mm, "radius": 1.6 * mm});
            skCircle(sketch, "E5.3.40.3", {"center": v(-694.98, 151.01) * mm, "radius": 1.6 * mm});
            skCircle(sketch, "E5.3.41.0", {"center": v(-702.48, 146.01) * mm, "radius": 1.6 * mm});
            skCircle(sketch, "E5.3.41.1", {"center": v(-697.48, 146.01) * mm, "radius": 1.6 * mm});
            skCircle(sketch, "E5.3.41.2", {"center": v(-699.98, 141.01) * mm, "radius": 1.6 * mm});
            skCircle(sketch, "E5.3.41.3", {"center": v(-694.98, 141.01) * mm, "radius": 1.6 * mm});
            skCircle(sketch, "E5.3.42.0", {"center": v(-702.48, 136.01) * mm, "radius": 1.6 * mm});
            skCircle(sketch, "E5.3.42.1", {"center": v(-697.48, 136.01) * mm, "radius": 1.6 * mm});
            skCircle(sketch, "E5.3.42.2", {"center": v(-699.98, 131.01) * mm, "radius": 1.6 * mm});
            skCircle(sketch, "E5.3.42.3", {"center": v(-694.98, 131.01) * mm, "radius": 1.6 * mm});
            skCircle(sketch, "E5.3.43.0", {"center": v(-702.48, 126.01) * mm, "radius": 1.6 * mm});
            skCircle(sketch, "E5.3.43.1", {"center": v(-697.48, 126.01) * mm, "radius": 1.6 * mm});
            skCircle(sketch, "E5.3.43.2", {"center": v(-699.98, 121.01) * mm, "radius": 1.6 * mm});
            skCircle(sketch, "E5.3.43.3", {"center": v(-694.98, 121.01) * mm, "radius": 1.6 * mm});
            skCircle(sketch, "E5.3.44.0", {"center": v(-702.48, 116.01) * mm, "radius": 1.6 * mm});
            skCircle(sketch, "E5.3.44.1", {"center": v(-697.48, 116.01) * mm, "radius": 1.6 * mm});
            skCircle(sketch, "E5.3.44.2", {"center": v(-699.98, 111.01) * mm, "radius": 1.6 * mm});
            skCircle(sketch, "E5.3.44.3", {"center": v(-694.98, 111.01) * mm, "radius": 1.6 * mm});
            skCircle(sketch, "E5.3.45.0", {"center": v(-702.48, 106.01) * mm, "radius": 1.6 * mm});
            skCircle(sketch, "E5.3.45.1", {"center": v(-697.48, 106.01) * mm, "radius": 1.6 * mm});
            skCircle(sketch, "E5.3.45.2", {"center": v(-699.98, 101.01) * mm, "radius": 1.6 * mm});
            skCircle(sketch, "E5.3.45.3", {"center": v(-694.98, 101.01) * mm, "radius": 1.6 * mm});
            skCircle(sketch, "E5.3.46.0", {"center": v(-702.48, 96.01) * mm, "radius": 1.6 * mm});
            skCircle(sketch, "E5.3.46.1", {"center": v(-697.48, 96.01) * mm, "radius": 1.6 * mm});
            skCircle(sketch, "E5.3.46.2", {"center": v(-699.98, 91.01) * mm, "radius": 1.6 * mm});
            skCircle(sketch, "E5.3.46.3", {"center": v(-694.98, 91.01) * mm, "radius": 1.6 * mm});
            skCircle(sketch, "E5.3.47.0", {"center": v(-702.48, 86.01) * mm, "radius": 1.6 * mm});
            skCircle(sketch, "E5.3.47.1", {"center": v(-697.48, 86.01) * mm, "radius": 1.6 * mm});
            skCircle(sketch, "E5.3.47.2", {"center": v(-699.98, 81.01) * mm, "radius": 1.6 * mm});
            skCircle(sketch, "E5.3.47.3", {"center": v(-694.98, 81.01) * mm, "radius": 1.6 * mm});
            skCircle(sketch, "E5.3.48.0", {"center": v(-702.48, 76.01) * mm, "radius": 1.6 * mm});
            skCircle(sketch, "E5.3.48.1", {"center": v(-697.48, 76.01) * mm, "radius": 1.6 * mm});
            skCircle(sketch, "E5.3.48.2", {"center": v(-699.98, 71.01) * mm, "radius": 1.6 * mm});
            skCircle(sketch, "E5.3.48.3", {"center": v(-694.98, 71.01) * mm, "radius": 1.6 * mm});
            skCircle(sketch, "E5.3.49.0", {"center": v(-702.48, 66.01) * mm, "radius": 1.6 * mm});
            skCircle(sketch, "E5.3.49.1", {"center": v(-697.48, 66.01) * mm, "radius": 1.6 * mm});
            skCircle(sketch, "E5.3.49.2", {"center": v(-699.98, 61.01) * mm, "radius": 1.6 * mm});
            skCircle(sketch, "E5.3.49.3", {"center": v(-694.98, 61.01) * mm, "radius": 1.6 * mm});
            skCircle(sketch, "E5.4.0.0", {"center": v(-692.48, 556.01) * mm, "radius": 1.6 * mm});
            skCircle(sketch, "E5.4.0.1", {"center": v(-687.48, 556.01) * mm, "radius": 1.6 * mm});
            skCircle(sketch, "E5.4.0.2", {"center": v(-689.98, 551.01) * mm, "radius": 1.6 * mm});
            skCircle(sketch, "E5.4.0.3", {"center": v(-684.98, 551.01) * mm, "radius": 1.6 * mm});
            skCircle(sketch, "E5.4.1.0", {"center": v(-692.48, 546.01) * mm, "radius": 1.6 * mm});
            skCircle(sketch, "E5.4.1.1", {"center": v(-687.48, 546.01) * mm, "radius": 1.6 * mm});
            skCircle(sketch, "E5.4.1.2", {"center": v(-689.98, 541.01) * mm, "radius": 1.6 * mm});
            skCircle(sketch, "E5.4.1.3", {"center": v(-684.98, 541.01) * mm, "radius": 1.6 * mm});
            skCircle(sketch, "E5.4.2.0", {"center": v(-692.48, 536.01) * mm, "radius": 1.6 * mm});
            skCircle(sketch, "E5.4.2.1", {"center": v(-687.48, 536.01) * mm, "radius": 1.6 * mm});
            skCircle(sketch, "E5.4.2.2", {"center": v(-689.98, 531.01) * mm, "radius": 1.6 * mm});
            skCircle(sketch, "E5.4.2.3", {"center": v(-684.98, 531.01) * mm, "radius": 1.6 * mm});
            skCircle(sketch, "E5.4.3.0", {"center": v(-692.48, 526.01) * mm, "radius": 1.6 * mm});
            skCircle(sketch, "E5.4.3.1", {"center": v(-687.48, 526.01) * mm, "radius": 1.6 * mm});
            skCircle(sketch, "E5.4.3.2", {"center": v(-689.98, 521.01) * mm, "radius": 1.6 * mm});
            skCircle(sketch, "E5.4.3.3", {"center": v(-684.98, 521.01) * mm, "radius": 1.6 * mm});
            skCircle(sketch, "E5.4.4.0", {"center": v(-692.48, 516.01) * mm, "radius": 1.6 * mm});
            skCircle(sketch, "E5.4.4.1", {"center": v(-687.48, 516.01) * mm, "radius": 1.6 * mm});
            skCircle(sketch, "E5.4.4.2", {"center": v(-689.98, 511.01) * mm, "radius": 1.6 * mm});
            skCircle(sketch, "E5.4.4.3", {"center": v(-684.98, 511.01) * mm, "radius": 1.6 * mm});
            skCircle(sketch, "E5.4.5.0", {"center": v(-692.48, 506.01) * mm, "radius": 1.6 * mm});
            skCircle(sketch, "E5.4.5.1", {"center": v(-687.48, 506.01) * mm, "radius": 1.6 * mm});
            skCircle(sketch, "E5.4.5.2", {"center": v(-689.98, 501.01) * mm, "radius": 1.6 * mm});
            skCircle(sketch, "E5.4.5.3", {"center": v(-684.98, 501.01) * mm, "radius": 1.6 * mm});
            skCircle(sketch, "E5.4.6.0", {"center": v(-692.48, 496.01) * mm, "radius": 1.6 * mm});
            skCircle(sketch, "E5.4.6.1", {"center": v(-687.48, 496.01) * mm, "radius": 1.6 * mm});
            skCircle(sketch, "E5.4.6.2", {"center": v(-689.98, 491.01) * mm, "radius": 1.6 * mm});
            skCircle(sketch, "E5.4.6.3", {"center": v(-684.98, 491.01) * mm, "radius": 1.6 * mm});
            skCircle(sketch, "E5.4.7.0", {"center": v(-692.48, 486.01) * mm, "radius": 1.6 * mm});
            skCircle(sketch, "E5.4.7.1", {"center": v(-687.48, 486.01) * mm, "radius": 1.6 * mm});
            skCircle(sketch, "E5.4.7.2", {"center": v(-689.98, 481.01) * mm, "radius": 1.6 * mm});
            skCircle(sketch, "E5.4.7.3", {"center": v(-684.98, 481.01) * mm, "radius": 1.6 * mm});
            skCircle(sketch, "E5.4.8.0", {"center": v(-692.48, 476.01) * mm, "radius": 1.6 * mm});
            skCircle(sketch, "E5.4.8.1", {"center": v(-687.48, 476.01) * mm, "radius": 1.6 * mm});
            skCircle(sketch, "E5.4.8.2", {"center": v(-689.98, 471.01) * mm, "radius": 1.6 * mm});
            skCircle(sketch, "E5.4.8.3", {"center": v(-684.98, 471.01) * mm, "radius": 1.6 * mm});
            skCircle(sketch, "E5.4.9.0", {"center": v(-692.48, 466.01) * mm, "radius": 1.6 * mm});
            skCircle(sketch, "E5.4.9.1", {"center": v(-687.48, 466.01) * mm, "radius": 1.6 * mm});
            skCircle(sketch, "E5.4.9.2", {"center": v(-689.98, 461.01) * mm, "radius": 1.6 * mm});
            skCircle(sketch, "E5.4.9.3", {"center": v(-684.98, 461.01) * mm, "radius": 1.6 * mm});
            skCircle(sketch, "E5.4.10.0", {"center": v(-692.48, 456.01) * mm, "radius": 1.6 * mm});
            skCircle(sketch, "E5.4.10.1", {"center": v(-687.48, 456.01) * mm, "radius": 1.6 * mm});
            skCircle(sketch, "E5.4.10.2", {"center": v(-689.98, 451.01) * mm, "radius": 1.6 * mm});
            skCircle(sketch, "E5.4.10.3", {"center": v(-684.98, 451.01) * mm, "radius": 1.6 * mm});
            skCircle(sketch, "E5.4.11.0", {"center": v(-692.48, 446.01) * mm, "radius": 1.6 * mm});
            skCircle(sketch, "E5.4.11.1", {"center": v(-687.48, 446.01) * mm, "radius": 1.6 * mm});
            skCircle(sketch, "E5.4.11.2", {"center": v(-689.98, 441.01) * mm, "radius": 1.6 * mm});
            skCircle(sketch, "E5.4.11.3", {"center": v(-684.98, 441.01) * mm, "radius": 1.6 * mm});
            skCircle(sketch, "E5.4.12.0", {"center": v(-692.48, 436.01) * mm, "radius": 1.6 * mm});
            skCircle(sketch, "E5.4.12.1", {"center": v(-687.48, 436.01) * mm, "radius": 1.6 * mm});
            skCircle(sketch, "E5.4.12.2", {"center": v(-689.98, 431.01) * mm, "radius": 1.6 * mm});
            skCircle(sketch, "E5.4.12.3", {"center": v(-684.98, 431.01) * mm, "radius": 1.6 * mm});
            skCircle(sketch, "E5.4.13.0", {"center": v(-692.48, 426.01) * mm, "radius": 1.6 * mm});
            skCircle(sketch, "E5.4.13.1", {"center": v(-687.48, 426.01) * mm, "radius": 1.6 * mm});
            skCircle(sketch, "E5.4.13.2", {"center": v(-689.98, 421.01) * mm, "radius": 1.6 * mm});
            skCircle(sketch, "E5.4.13.3", {"center": v(-684.98, 421.01) * mm, "radius": 1.6 * mm});
            skCircle(sketch, "E5.4.14.0", {"center": v(-692.48, 416.01) * mm, "radius": 1.6 * mm});
            skCircle(sketch, "E5.4.14.1", {"center": v(-687.48, 416.01) * mm, "radius": 1.6 * mm});
            skCircle(sketch, "E5.4.14.2", {"center": v(-689.98, 411.01) * mm, "radius": 1.6 * mm});
            skCircle(sketch, "E5.4.14.3", {"center": v(-684.98, 411.01) * mm, "radius": 1.6 * mm});
            skCircle(sketch, "E5.4.15.0", {"center": v(-692.48, 406.01) * mm, "radius": 1.6 * mm});
            skCircle(sketch, "E5.4.15.1", {"center": v(-687.48, 406.01) * mm, "radius": 1.6 * mm});
            skCircle(sketch, "E5.4.15.2", {"center": v(-689.98, 401.01) * mm, "radius": 1.6 * mm});
            skCircle(sketch, "E5.4.15.3", {"center": v(-684.98, 401.01) * mm, "radius": 1.6 * mm});
            skCircle(sketch, "E5.4.16.0", {"center": v(-692.48, 396.01) * mm, "radius": 1.6 * mm});
            skCircle(sketch, "E5.4.16.1", {"center": v(-687.48, 396.01) * mm, "radius": 1.6 * mm});
            skCircle(sketch, "E5.4.16.2", {"center": v(-689.98, 391.01) * mm, "radius": 1.6 * mm});
            skCircle(sketch, "E5.4.16.3", {"center": v(-684.98, 391.01) * mm, "radius": 1.6 * mm});
            skCircle(sketch, "E5.4.17.0", {"center": v(-692.48, 386.01) * mm, "radius": 1.6 * mm});
            skCircle(sketch, "E5.4.17.1", {"center": v(-687.48, 386.01) * mm, "radius": 1.6 * mm});
            skCircle(sketch, "E5.4.17.2", {"center": v(-689.98, 381.01) * mm, "radius": 1.6 * mm});
            skCircle(sketch, "E5.4.17.3", {"center": v(-684.98, 381.01) * mm, "radius": 1.6 * mm});
            skCircle(sketch, "E5.4.18.0", {"center": v(-692.48, 376.01) * mm, "radius": 1.6 * mm});
            skCircle(sketch, "E5.4.18.1", {"center": v(-687.48, 376.01) * mm, "radius": 1.6 * mm});
            skCircle(sketch, "E5.4.18.2", {"center": v(-689.98, 371.01) * mm, "radius": 1.6 * mm});
            skCircle(sketch, "E5.4.18.3", {"center": v(-684.98, 371.01) * mm, "radius": 1.6 * mm});
            skCircle(sketch, "E5.4.19.0", {"center": v(-692.48, 366.01) * mm, "radius": 1.6 * mm});
            skCircle(sketch, "E5.4.19.1", {"center": v(-687.48, 366.01) * mm, "radius": 1.6 * mm});
            skCircle(sketch, "E5.4.19.2", {"center": v(-689.98, 361.01) * mm, "radius": 1.6 * mm});
            skCircle(sketch, "E5.4.19.3", {"center": v(-684.98, 361.01) * mm, "radius": 1.6 * mm});
            skCircle(sketch, "E5.4.20.0", {"center": v(-692.48, 356.01) * mm, "radius": 1.6 * mm});
            skCircle(sketch, "E5.4.20.1", {"center": v(-687.48, 356.01) * mm, "radius": 1.6 * mm});
            skCircle(sketch, "E5.4.20.2", {"center": v(-689.98, 351.01) * mm, "radius": 1.6 * mm});
            skCircle(sketch, "E5.4.20.3", {"center": v(-684.98, 351.01) * mm, "radius": 1.6 * mm});
            skCircle(sketch, "E5.4.21.0", {"center": v(-692.48, 346.01) * mm, "radius": 1.6 * mm});
            skCircle(sketch, "E5.4.21.1", {"center": v(-687.48, 346.01) * mm, "radius": 1.6 * mm});
            skCircle(sketch, "E5.4.21.2", {"center": v(-689.98, 341.01) * mm, "radius": 1.6 * mm});
            skCircle(sketch, "E5.4.21.3", {"center": v(-684.98, 341.01) * mm, "radius": 1.6 * mm});
            skCircle(sketch, "E5.4.22.0", {"center": v(-692.48, 336.01) * mm, "radius": 1.6 * mm});
            skCircle(sketch, "E5.4.22.1", {"center": v(-687.48, 336.01) * mm, "radius": 1.6 * mm});
            skCircle(sketch, "E5.4.22.2", {"center": v(-689.98, 331.01) * mm, "radius": 1.6 * mm});
            skCircle(sketch, "E5.4.22.3", {"center": v(-684.98, 331.01) * mm, "radius": 1.6 * mm});
            skCircle(sketch, "E5.4.23.0", {"center": v(-692.48, 326.01) * mm, "radius": 1.6 * mm});
            skCircle(sketch, "E5.4.23.1", {"center": v(-687.48, 326.01) * mm, "radius": 1.6 * mm});
            skCircle(sketch, "E5.4.23.2", {"center": v(-689.98, 321.01) * mm, "radius": 1.6 * mm});
            skCircle(sketch, "E5.4.23.3", {"center": v(-684.98, 321.01) * mm, "radius": 1.6 * mm});
            skCircle(sketch, "E5.4.24.0", {"center": v(-692.48, 316.01) * mm, "radius": 1.6 * mm});
            skCircle(sketch, "E5.4.24.1", {"center": v(-687.48, 316.01) * mm, "radius": 1.6 * mm});
            skCircle(sketch, "E5.4.24.2", {"center": v(-689.98, 311.01) * mm, "radius": 1.6 * mm});
            skCircle(sketch, "E5.4.24.3", {"center": v(-684.98, 311.01) * mm, "radius": 1.6 * mm});
            skCircle(sketch, "E5.4.25.0", {"center": v(-692.48, 306.01) * mm, "radius": 1.6 * mm});
            skCircle(sketch, "E5.4.25.1", {"center": v(-687.48, 306.01) * mm, "radius": 1.6 * mm});
            skCircle(sketch, "E5.4.25.2", {"center": v(-689.98, 301.01) * mm, "radius": 1.6 * mm});
            skCircle(sketch, "E5.4.25.3", {"center": v(-684.98, 301.01) * mm, "radius": 1.6 * mm});
            skCircle(sketch, "E5.4.26.0", {"center": v(-692.48, 296.01) * mm, "radius": 1.6 * mm});
            skCircle(sketch, "E5.4.26.1", {"center": v(-687.48, 296.01) * mm, "radius": 1.6 * mm});
            skCircle(sketch, "E5.4.26.2", {"center": v(-689.98, 291.01) * mm, "radius": 1.6 * mm});
            skCircle(sketch, "E5.4.26.3", {"center": v(-684.98, 291.01) * mm, "radius": 1.6 * mm});
            skCircle(sketch, "E5.4.27.0", {"center": v(-692.48, 286.01) * mm, "radius": 1.6 * mm});
            skCircle(sketch, "E5.4.27.1", {"center": v(-687.48, 286.01) * mm, "radius": 1.6 * mm});
            skCircle(sketch, "E5.4.27.2", {"center": v(-689.98, 281.01) * mm, "radius": 1.6 * mm});
            skCircle(sketch, "E5.4.27.3", {"center": v(-684.98, 281.01) * mm, "radius": 1.6 * mm});
            skCircle(sketch, "E5.4.28.0", {"center": v(-692.48, 276.01) * mm, "radius": 1.6 * mm});
            skCircle(sketch, "E5.4.28.1", {"center": v(-687.48, 276.01) * mm, "radius": 1.6 * mm});
            skCircle(sketch, "E5.4.28.2", {"center": v(-689.98, 271.01) * mm, "radius": 1.6 * mm});
            skCircle(sketch, "E5.4.28.3", {"center": v(-684.98, 271.01) * mm, "radius": 1.6 * mm});
            skCircle(sketch, "E5.4.29.0", {"center": v(-692.48, 266.01) * mm, "radius": 1.6 * mm});
            skCircle(sketch, "E5.4.29.1", {"center": v(-687.48, 266.01) * mm, "radius": 1.6 * mm});
            skCircle(sketch, "E5.4.29.2", {"center": v(-689.98, 261.01) * mm, "radius": 1.6 * mm});
            skCircle(sketch, "E5.4.29.3", {"center": v(-684.98, 261.01) * mm, "radius": 1.6 * mm});
            skCircle(sketch, "E5.4.30.0", {"center": v(-692.48, 256.01) * mm, "radius": 1.6 * mm});
            skCircle(sketch, "E5.4.30.1", {"center": v(-687.48, 256.01) * mm, "radius": 1.6 * mm});
            skCircle(sketch, "E5.4.30.2", {"center": v(-689.98, 251.01) * mm, "radius": 1.6 * mm});
            skCircle(sketch, "E5.4.30.3", {"center": v(-684.98, 251.01) * mm, "radius": 1.6 * mm});
            skCircle(sketch, "E5.4.31.0", {"center": v(-692.48, 246.01) * mm, "radius": 1.6 * mm});
            skCircle(sketch, "E5.4.31.1", {"center": v(-687.48, 246.01) * mm, "radius": 1.6 * mm});
            skCircle(sketch, "E5.4.31.2", {"center": v(-689.98, 241.01) * mm, "radius": 1.6 * mm});
            skCircle(sketch, "E5.4.31.3", {"center": v(-684.98, 241.01) * mm, "radius": 1.6 * mm});
            skCircle(sketch, "E5.4.32.0", {"center": v(-692.48, 236.01) * mm, "radius": 1.6 * mm});
            skCircle(sketch, "E5.4.32.1", {"center": v(-687.48, 236.01) * mm, "radius": 1.6 * mm});
            skCircle(sketch, "E5.4.32.2", {"center": v(-689.98, 231.01) * mm, "radius": 1.6 * mm});
            skCircle(sketch, "E5.4.32.3", {"center": v(-684.98, 231.01) * mm, "radius": 1.6 * mm});
            skCircle(sketch, "E5.4.33.0", {"center": v(-692.48, 226.01) * mm, "radius": 1.6 * mm});
            skCircle(sketch, "E5.4.33.1", {"center": v(-687.48, 226.01) * mm, "radius": 1.6 * mm});
            skCircle(sketch, "E5.4.33.2", {"center": v(-689.98, 221.01) * mm, "radius": 1.6 * mm});
            skCircle(sketch, "E5.4.33.3", {"center": v(-684.98, 221.01) * mm, "radius": 1.6 * mm});
            skCircle(sketch, "E5.4.34.0", {"center": v(-692.48, 216.01) * mm, "radius": 1.6 * mm});
            skCircle(sketch, "E5.4.34.1", {"center": v(-687.48, 216.01) * mm, "radius": 1.6 * mm});
            skCircle(sketch, "E5.4.34.2", {"center": v(-689.98, 211.01) * mm, "radius": 1.6 * mm});
            skCircle(sketch, "E5.4.34.3", {"center": v(-684.98, 211.01) * mm, "radius": 1.6 * mm});
            skCircle(sketch, "E5.4.35.0", {"center": v(-692.48, 206.01) * mm, "radius": 1.6 * mm});
            skCircle(sketch, "E5.4.35.1", {"center": v(-687.48, 206.01) * mm, "radius": 1.6 * mm});
            skCircle(sketch, "E5.4.35.2", {"center": v(-689.98, 201.01) * mm, "radius": 1.6 * mm});
            skCircle(sketch, "E5.4.35.3", {"center": v(-684.98, 201.01) * mm, "radius": 1.6 * mm});
            skCircle(sketch, "E5.4.36.0", {"center": v(-692.48, 196.01) * mm, "radius": 1.6 * mm});
            skCircle(sketch, "E5.4.36.1", {"center": v(-687.48, 196.01) * mm, "radius": 1.6 * mm});
            skCircle(sketch, "E5.4.36.2", {"center": v(-689.98, 191.01) * mm, "radius": 1.6 * mm});
            skCircle(sketch, "E5.4.36.3", {"center": v(-684.98, 191.01) * mm, "radius": 1.6 * mm});
            skCircle(sketch, "E5.4.37.0", {"center": v(-692.48, 186.01) * mm, "radius": 1.6 * mm});
            skCircle(sketch, "E5.4.37.1", {"center": v(-687.48, 186.01) * mm, "radius": 1.6 * mm});
            skCircle(sketch, "E5.4.37.2", {"center": v(-689.98, 181.01) * mm, "radius": 1.6 * mm});
            skCircle(sketch, "E5.4.37.3", {"center": v(-684.98, 181.01) * mm, "radius": 1.6 * mm});
            skCircle(sketch, "E5.4.38.0", {"center": v(-692.48, 176.01) * mm, "radius": 1.6 * mm});
            skCircle(sketch, "E5.4.38.1", {"center": v(-687.48, 176.01) * mm, "radius": 1.6 * mm});
            skCircle(sketch, "E5.4.38.2", {"center": v(-689.98, 171.01) * mm, "radius": 1.6 * mm});
            skCircle(sketch, "E5.4.38.3", {"center": v(-684.98, 171.01) * mm, "radius": 1.6 * mm});
            skCircle(sketch, "E5.4.39.0", {"center": v(-692.48, 166.01) * mm, "radius": 1.6 * mm});
            skCircle(sketch, "E5.4.39.1", {"center": v(-687.48, 166.01) * mm, "radius": 1.6 * mm});
            skCircle(sketch, "E5.4.39.2", {"center": v(-689.98, 161.01) * mm, "radius": 1.6 * mm});
            skCircle(sketch, "E5.4.39.3", {"center": v(-684.98, 161.01) * mm, "radius": 1.6 * mm});
            skCircle(sketch, "E5.4.40.0", {"center": v(-692.48, 156.01) * mm, "radius": 1.6 * mm});
            skCircle(sketch, "E5.4.40.1", {"center": v(-687.48, 156.01) * mm, "radius": 1.6 * mm});
            skCircle(sketch, "E5.4.40.2", {"center": v(-689.98, 151.01) * mm, "radius": 1.6 * mm});
            skCircle(sketch, "E5.4.40.3", {"center": v(-684.98, 151.01) * mm, "radius": 1.6 * mm});
            skCircle(sketch, "E5.4.41.0", {"center": v(-692.48, 146.01) * mm, "radius": 1.6 * mm});
            skCircle(sketch, "E5.4.41.1", {"center": v(-687.48, 146.01) * mm, "radius": 1.6 * mm});
            skCircle(sketch, "E5.4.41.2", {"center": v(-689.98, 141.01) * mm, "radius": 1.6 * mm});
            skCircle(sketch, "E5.4.41.3", {"center": v(-684.98, 141.01) * mm, "radius": 1.6 * mm});
            skCircle(sketch, "E5.4.42.0", {"center": v(-692.48, 136.01) * mm, "radius": 1.6 * mm});
            skCircle(sketch, "E5.4.42.1", {"center": v(-687.48, 136.01) * mm, "radius": 1.6 * mm});
            skCircle(sketch, "E5.4.42.2", {"center": v(-689.98, 131.01) * mm, "radius": 1.6 * mm});
            skCircle(sketch, "E5.4.42.3", {"center": v(-684.98, 131.01) * mm, "radius": 1.6 * mm});
            skCircle(sketch, "E5.4.43.0", {"center": v(-692.48, 126.01) * mm, "radius": 1.6 * mm});
            skCircle(sketch, "E5.4.43.1", {"center": v(-687.48, 126.01) * mm, "radius": 1.6 * mm});
            skCircle(sketch, "E5.4.43.2", {"center": v(-689.98, 121.01) * mm, "radius": 1.6 * mm});
            skCircle(sketch, "E5.4.43.3", {"center": v(-684.98, 121.01) * mm, "radius": 1.6 * mm});
            skCircle(sketch, "E5.4.44.0", {"center": v(-692.48, 116.01) * mm, "radius": 1.6 * mm});
            skCircle(sketch, "E5.4.44.1", {"center": v(-687.48, 116.01) * mm, "radius": 1.6 * mm});
            skCircle(sketch, "E5.4.44.2", {"center": v(-689.98, 111.01) * mm, "radius": 1.6 * mm});
            skCircle(sketch, "E5.4.44.3", {"center": v(-684.98, 111.01) * mm, "radius": 1.6 * mm});
            skCircle(sketch, "E5.4.45.0", {"center": v(-692.48, 106.01) * mm, "radius": 1.6 * mm});
            skCircle(sketch, "E5.4.45.1", {"center": v(-687.48, 106.01) * mm, "radius": 1.6 * mm});
            skCircle(sketch, "E5.4.45.2", {"center": v(-689.98, 101.01) * mm, "radius": 1.6 * mm});
            skCircle(sketch, "E5.4.45.3", {"center": v(-684.98, 101.01) * mm, "radius": 1.6 * mm});
            skCircle(sketch, "E5.4.46.0", {"center": v(-692.48, 96.01) * mm, "radius": 1.6 * mm});
            skCircle(sketch, "E5.4.46.1", {"center": v(-687.48, 96.01) * mm, "radius": 1.6 * mm});
            skCircle(sketch, "E5.4.46.2", {"center": v(-689.98, 91.01) * mm, "radius": 1.6 * mm});
            skCircle(sketch, "E5.4.46.3", {"center": v(-684.98, 91.01) * mm, "radius": 1.6 * mm});
            skCircle(sketch, "E5.4.47.0", {"center": v(-692.48, 86.01) * mm, "radius": 1.6 * mm});
            skCircle(sketch, "E5.4.47.1", {"center": v(-687.48, 86.01) * mm, "radius": 1.6 * mm});
            skCircle(sketch, "E5.4.47.2", {"center": v(-689.98, 81.01) * mm, "radius": 1.6 * mm});
            skCircle(sketch, "E5.4.47.3", {"center": v(-684.98, 81.01) * mm, "radius": 1.6 * mm});
            skCircle(sketch, "E5.4.48.0", {"center": v(-692.48, 76.01) * mm, "radius": 1.6 * mm});
            skCircle(sketch, "E5.4.48.1", {"center": v(-687.48, 76.01) * mm, "radius": 1.6 * mm});
            skCircle(sketch, "E5.4.48.2", {"center": v(-689.98, 71.01) * mm, "radius": 1.6 * mm});
            skCircle(sketch, "E5.4.48.3", {"center": v(-684.98, 71.01) * mm, "radius": 1.6 * mm});
            skCircle(sketch, "E5.4.49.0", {"center": v(-692.48, 66.01) * mm, "radius": 1.6 * mm});
            skCircle(sketch, "E5.4.49.1", {"center": v(-687.48, 66.01) * mm, "radius": 1.6 * mm});
            skCircle(sketch, "E5.4.49.2", {"center": v(-689.98, 61.01) * mm, "radius": 1.6 * mm});
            skCircle(sketch, "E5.4.49.3", {"center": v(-684.98, 61.01) * mm, "radius": 1.6 * mm});
            skCircle(sketch, "E5.5.0.0", {"center": v(-682.48, 556.01) * mm, "radius": 1.6 * mm});
            skCircle(sketch, "E5.5.0.1", {"center": v(-677.48, 556.01) * mm, "radius": 1.6 * mm});
            skCircle(sketch, "E5.5.0.2", {"center": v(-679.98, 551.01) * mm, "radius": 1.6 * mm});
            skCircle(sketch, "E5.5.0.3", {"center": v(-674.98, 551.01) * mm, "radius": 1.6 * mm});
            skCircle(sketch, "E5.5.1.0", {"center": v(-682.48, 546.01) * mm, "radius": 1.6 * mm});
            skCircle(sketch, "E5.5.1.1", {"center": v(-677.48, 546.01) * mm, "radius": 1.6 * mm});
            skCircle(sketch, "E5.5.1.2", {"center": v(-679.98, 541.01) * mm, "radius": 1.6 * mm});
            skCircle(sketch, "E5.5.1.3", {"center": v(-674.98, 541.01) * mm, "radius": 1.6 * mm});
            skCircle(sketch, "E5.5.2.0", {"center": v(-682.48, 536.01) * mm, "radius": 1.6 * mm});
            skCircle(sketch, "E5.5.2.1", {"center": v(-677.48, 536.01) * mm, "radius": 1.6 * mm});
            skCircle(sketch, "E5.5.2.2", {"center": v(-679.98, 531.01) * mm, "radius": 1.6 * mm});
            skCircle(sketch, "E5.5.2.3", {"center": v(-674.98, 531.01) * mm, "radius": 1.6 * mm});
            skCircle(sketch, "E5.5.3.0", {"center": v(-682.48, 526.01) * mm, "radius": 1.6 * mm});
            skCircle(sketch, "E5.5.3.1", {"center": v(-677.48, 526.01) * mm, "radius": 1.6 * mm});
            skCircle(sketch, "E5.5.3.2", {"center": v(-679.98, 521.01) * mm, "radius": 1.6 * mm});
            skCircle(sketch, "E5.5.3.3", {"center": v(-674.98, 521.01) * mm, "radius": 1.6 * mm});
            skCircle(sketch, "E5.5.4.0", {"center": v(-682.48, 516.01) * mm, "radius": 1.6 * mm});
            skCircle(sketch, "E5.5.4.1", {"center": v(-677.48, 516.01) * mm, "radius": 1.6 * mm});
            skCircle(sketch, "E5.5.4.2", {"center": v(-679.98, 511.01) * mm, "radius": 1.6 * mm});
            skCircle(sketch, "E5.5.4.3", {"center": v(-674.98, 511.01) * mm, "radius": 1.6 * mm});
            skCircle(sketch, "E5.5.5.0", {"center": v(-682.48, 506.01) * mm, "radius": 1.6 * mm});
            skCircle(sketch, "E5.5.5.1", {"center": v(-677.48, 506.01) * mm, "radius": 1.6 * mm});
            skCircle(sketch, "E5.5.5.2", {"center": v(-679.98, 501.01) * mm, "radius": 1.6 * mm});
            skCircle(sketch, "E5.5.5.3", {"center": v(-674.98, 501.01) * mm, "radius": 1.6 * mm});
            skCircle(sketch, "E5.5.6.0", {"center": v(-682.48, 496.01) * mm, "radius": 1.6 * mm});
            skCircle(sketch, "E5.5.6.1", {"center": v(-677.48, 496.01) * mm, "radius": 1.6 * mm});
            skCircle(sketch, "E5.5.6.2", {"center": v(-679.98, 491.01) * mm, "radius": 1.6 * mm});
            skCircle(sketch, "E5.5.6.3", {"center": v(-674.98, 491.01) * mm, "radius": 1.6 * mm});
            skCircle(sketch, "E5.5.7.0", {"center": v(-682.48, 486.01) * mm, "radius": 1.6 * mm});
            skCircle(sketch, "E5.5.7.1", {"center": v(-677.48, 486.01) * mm, "radius": 1.6 * mm});
            skCircle(sketch, "E5.5.7.2", {"center": v(-679.98, 481.01) * mm, "radius": 1.6 * mm});
            skCircle(sketch, "E5.5.7.3", {"center": v(-674.98, 481.01) * mm, "radius": 1.6 * mm});
            skCircle(sketch, "E5.5.8.0", {"center": v(-682.48, 476.01) * mm, "radius": 1.6 * mm});
            skCircle(sketch, "E5.5.8.1", {"center": v(-677.48, 476.01) * mm, "radius": 1.6 * mm});
            skCircle(sketch, "E5.5.8.2", {"center": v(-679.98, 471.01) * mm, "radius": 1.6 * mm});
            skCircle(sketch, "E5.5.8.3", {"center": v(-674.98, 471.01) * mm, "radius": 1.6 * mm});
            skCircle(sketch, "E5.5.9.0", {"center": v(-682.48, 466.01) * mm, "radius": 1.6 * mm});
            skCircle(sketch, "E5.5.9.1", {"center": v(-677.48, 466.01) * mm, "radius": 1.6 * mm});
            skCircle(sketch, "E5.5.9.2", {"center": v(-679.98, 461.01) * mm, "radius": 1.6 * mm});
            skCircle(sketch, "E5.5.9.3", {"center": v(-674.98, 461.01) * mm, "radius": 1.6 * mm});
            skCircle(sketch, "E5.5.10.0", {"center": v(-682.48, 456.01) * mm, "radius": 1.6 * mm});
            skCircle(sketch, "E5.5.10.1", {"center": v(-677.48, 456.01) * mm, "radius": 1.6 * mm});
            skCircle(sketch, "E5.5.10.2", {"center": v(-679.98, 451.01) * mm, "radius": 1.6 * mm});
            skCircle(sketch, "E5.5.10.3", {"center": v(-674.98, 451.01) * mm, "radius": 1.6 * mm});
            skCircle(sketch, "E5.5.11.0", {"center": v(-682.48, 446.01) * mm, "radius": 1.6 * mm});
            skCircle(sketch, "E5.5.11.1", {"center": v(-677.48, 446.01) * mm, "radius": 1.6 * mm});
            skCircle(sketch, "E5.5.11.2", {"center": v(-679.98, 441.01) * mm, "radius": 1.6 * mm});
            skCircle(sketch, "E5.5.11.3", {"center": v(-674.98, 441.01) * mm, "radius": 1.6 * mm});
            skCircle(sketch, "E5.5.12.0", {"center": v(-682.48, 436.01) * mm, "radius": 1.6 * mm});
            skCircle(sketch, "E5.5.12.1", {"center": v(-677.48, 436.01) * mm, "radius": 1.6 * mm});
            skCircle(sketch, "E5.5.12.2", {"center": v(-679.98, 431.01) * mm, "radius": 1.6 * mm});
            skCircle(sketch, "E5.5.12.3", {"center": v(-674.98, 431.01) * mm, "radius": 1.6 * mm});
            skCircle(sketch, "E5.5.13.0", {"center": v(-682.48, 426.01) * mm, "radius": 1.6 * mm});
            skCircle(sketch, "E5.5.13.1", {"center": v(-677.48, 426.01) * mm, "radius": 1.6 * mm});
            skCircle(sketch, "E5.5.13.2", {"center": v(-679.98, 421.01) * mm, "radius": 1.6 * mm});
            skCircle(sketch, "E5.5.13.3", {"center": v(-674.98, 421.01) * mm, "radius": 1.6 * mm});
            skCircle(sketch, "E5.5.14.0", {"center": v(-682.48, 416.01) * mm, "radius": 1.6 * mm});
            skCircle(sketch, "E5.5.14.1", {"center": v(-677.48, 416.01) * mm, "radius": 1.6 * mm});
            skCircle(sketch, "E5.5.14.2", {"center": v(-679.98, 411.01) * mm, "radius": 1.6 * mm});
            skCircle(sketch, "E5.5.14.3", {"center": v(-674.98, 411.01) * mm, "radius": 1.6 * mm});
            skCircle(sketch, "E5.5.15.0", {"center": v(-682.48, 406.01) * mm, "radius": 1.6 * mm});
            skCircle(sketch, "E5.5.15.1", {"center": v(-677.48, 406.01) * mm, "radius": 1.6 * mm});
            skCircle(sketch, "E5.5.15.2", {"center": v(-679.98, 401.01) * mm, "radius": 1.6 * mm});
            skCircle(sketch, "E5.5.15.3", {"center": v(-674.98, 401.01) * mm, "radius": 1.6 * mm});
            skCircle(sketch, "E5.5.16.0", {"center": v(-682.48, 396.01) * mm, "radius": 1.6 * mm});
            skCircle(sketch, "E5.5.16.1", {"center": v(-677.48, 396.01) * mm, "radius": 1.6 * mm});
            skCircle(sketch, "E5.5.16.2", {"center": v(-679.98, 391.01) * mm, "radius": 1.6 * mm});
            skCircle(sketch, "E5.5.16.3", {"center": v(-674.98, 391.01) * mm, "radius": 1.6 * mm});
            skCircle(sketch, "E5.5.17.0", {"center": v(-682.48, 386.01) * mm, "radius": 1.6 * mm});
            skCircle(sketch, "E5.5.17.1", {"center": v(-677.48, 386.01) * mm, "radius": 1.6 * mm});
            skCircle(sketch, "E5.5.17.2", {"center": v(-679.98, 381.01) * mm, "radius": 1.6 * mm});
            skCircle(sketch, "E5.5.17.3", {"center": v(-674.98, 381.01) * mm, "radius": 1.6 * mm});
            skCircle(sketch, "E5.5.18.0", {"center": v(-682.48, 376.01) * mm, "radius": 1.6 * mm});
            skCircle(sketch, "E5.5.18.1", {"center": v(-677.48, 376.01) * mm, "radius": 1.6 * mm});
            skCircle(sketch, "E5.5.18.2", {"center": v(-679.98, 371.01) * mm, "radius": 1.6 * mm});
            skCircle(sketch, "E5.5.18.3", {"center": v(-674.98, 371.01) * mm, "radius": 1.6 * mm});
            skCircle(sketch, "E5.5.19.0", {"center": v(-682.48, 366.01) * mm, "radius": 1.6 * mm});
            skCircle(sketch, "E5.5.19.1", {"center": v(-677.48, 366.01) * mm, "radius": 1.6 * mm});
            skCircle(sketch, "E5.5.19.2", {"center": v(-679.98, 361.01) * mm, "radius": 1.6 * mm});
            skCircle(sketch, "E5.5.19.3", {"center": v(-674.98, 361.01) * mm, "radius": 1.6 * mm});
            skCircle(sketch, "E5.5.20.0", {"center": v(-682.48, 356.01) * mm, "radius": 1.6 * mm});
            skCircle(sketch, "E5.5.20.1", {"center": v(-677.48, 356.01) * mm, "radius": 1.6 * mm});
            skCircle(sketch, "E5.5.20.2", {"center": v(-679.98, 351.01) * mm, "radius": 1.6 * mm});
            skCircle(sketch, "E5.5.20.3", {"center": v(-674.98, 351.01) * mm, "radius": 1.6 * mm});
            skCircle(sketch, "E5.5.21.0", {"center": v(-682.48, 346.01) * mm, "radius": 1.6 * mm});
            skCircle(sketch, "E5.5.21.1", {"center": v(-677.48, 346.01) * mm, "radius": 1.6 * mm});
            skCircle(sketch, "E5.5.21.2", {"center": v(-679.98, 341.01) * mm, "radius": 1.6 * mm});
            skCircle(sketch, "E5.5.21.3", {"center": v(-674.98, 341.01) * mm, "radius": 1.6 * mm});
            skCircle(sketch, "E5.5.22.0", {"center": v(-682.48, 336.01) * mm, "radius": 1.6 * mm});
            skCircle(sketch, "E5.5.22.1", {"center": v(-677.48, 336.01) * mm, "radius": 1.6 * mm});
            skCircle(sketch, "E5.5.22.2", {"center": v(-679.98, 331.01) * mm, "radius": 1.6 * mm});
            skCircle(sketch, "E5.5.22.3", {"center": v(-674.98, 331.01) * mm, "radius": 1.6 * mm});
            skCircle(sketch, "E5.5.23.0", {"center": v(-682.48, 326.01) * mm, "radius": 1.6 * mm});
            skCircle(sketch, "E5.5.23.1", {"center": v(-677.48, 326.01) * mm, "radius": 1.6 * mm});
            skCircle(sketch, "E5.5.23.2", {"center": v(-679.98, 321.01) * mm, "radius": 1.6 * mm});
            skCircle(sketch, "E5.5.23.3", {"center": v(-674.98, 321.01) * mm, "radius": 1.6 * mm});
            skCircle(sketch, "E5.5.24.0", {"center": v(-682.48, 316.01) * mm, "radius": 1.6 * mm});
            skCircle(sketch, "E5.5.24.1", {"center": v(-677.48, 316.01) * mm, "radius": 1.6 * mm});
            skCircle(sketch, "E5.5.24.2", {"center": v(-679.98, 311.01) * mm, "radius": 1.6 * mm});
            skCircle(sketch, "E5.5.24.3", {"center": v(-674.98, 311.01) * mm, "radius": 1.6 * mm});
            skCircle(sketch, "E5.5.25.0", {"center": v(-682.48, 306.01) * mm, "radius": 1.6 * mm});
            skCircle(sketch, "E5.5.25.1", {"center": v(-677.48, 306.01) * mm, "radius": 1.6 * mm});
            skCircle(sketch, "E5.5.25.2", {"center": v(-679.98, 301.01) * mm, "radius": 1.6 * mm});
            skCircle(sketch, "E5.5.25.3", {"center": v(-674.98, 301.01) * mm, "radius": 1.6 * mm});
            skCircle(sketch, "E5.5.26.0", {"center": v(-682.48, 296.01) * mm, "radius": 1.6 * mm});
            skCircle(sketch, "E5.5.26.1", {"center": v(-677.48, 296.01) * mm, "radius": 1.6 * mm});
            skCircle(sketch, "E5.5.26.2", {"center": v(-679.98, 291.01) * mm, "radius": 1.6 * mm});
            skCircle(sketch, "E5.5.26.3", {"center": v(-674.98, 291.01) * mm, "radius": 1.6 * mm});
            skCircle(sketch, "E5.5.27.0", {"center": v(-682.48, 286.01) * mm, "radius": 1.6 * mm});
            skCircle(sketch, "E5.5.27.1", {"center": v(-677.48, 286.01) * mm, "radius": 1.6 * mm});
            skCircle(sketch, "E5.5.27.2", {"center": v(-679.98, 281.01) * mm, "radius": 1.6 * mm});
            skCircle(sketch, "E5.5.27.3", {"center": v(-674.98, 281.01) * mm, "radius": 1.6 * mm});
            skCircle(sketch, "E5.5.28.0", {"center": v(-682.48, 276.01) * mm, "radius": 1.6 * mm});
            skCircle(sketch, "E5.5.28.1", {"center": v(-677.48, 276.01) * mm, "radius": 1.6 * mm});
            skCircle(sketch, "E5.5.28.2", {"center": v(-679.98, 271.01) * mm, "radius": 1.6 * mm});
            skCircle(sketch, "E5.5.28.3", {"center": v(-674.98, 271.01) * mm, "radius": 1.6 * mm});
            skCircle(sketch, "E5.5.29.0", {"center": v(-682.48, 266.01) * mm, "radius": 1.6 * mm});
            skCircle(sketch, "E5.5.29.1", {"center": v(-677.48, 266.01) * mm, "radius": 1.6 * mm});
            skCircle(sketch, "E5.5.29.2", {"center": v(-679.98, 261.01) * mm, "radius": 1.6 * mm});
            skCircle(sketch, "E5.5.29.3", {"center": v(-674.98, 261.01) * mm, "radius": 1.6 * mm});
            skCircle(sketch, "E5.5.30.0", {"center": v(-682.48, 256.01) * mm, "radius": 1.6 * mm});
            skCircle(sketch, "E5.5.30.1", {"center": v(-677.48, 256.01) * mm, "radius": 1.6 * mm});
            skCircle(sketch, "E5.5.30.2", {"center": v(-679.98, 251.01) * mm, "radius": 1.6 * mm});
            skCircle(sketch, "E5.5.30.3", {"center": v(-674.98, 251.01) * mm, "radius": 1.6 * mm});
            skCircle(sketch, "E5.5.31.0", {"center": v(-682.48, 246.01) * mm, "radius": 1.6 * mm});
            skCircle(sketch, "E5.5.31.1", {"center": v(-677.48, 246.01) * mm, "radius": 1.6 * mm});
            skCircle(sketch, "E5.5.31.2", {"center": v(-679.98, 241.01) * mm, "radius": 1.6 * mm});
            skCircle(sketch, "E5.5.31.3", {"center": v(-674.98, 241.01) * mm, "radius": 1.6 * mm});
            skCircle(sketch, "E5.5.32.0", {"center": v(-682.48, 236.01) * mm, "radius": 1.6 * mm});
            skCircle(sketch, "E5.5.32.1", {"center": v(-677.48, 236.01) * mm, "radius": 1.6 * mm});
            skCircle(sketch, "E5.5.32.2", {"center": v(-679.98, 231.01) * mm, "radius": 1.6 * mm});
            skCircle(sketch, "E5.5.32.3", {"center": v(-674.98, 231.01) * mm, "radius": 1.6 * mm});
            skCircle(sketch, "E5.5.33.0", {"center": v(-682.48, 226.01) * mm, "radius": 1.6 * mm});
            skCircle(sketch, "E5.5.33.1", {"center": v(-677.48, 226.01) * mm, "radius": 1.6 * mm});
            skCircle(sketch, "E5.5.33.2", {"center": v(-679.98, 221.01) * mm, "radius": 1.6 * mm});
            skCircle(sketch, "E5.5.33.3", {"center": v(-674.98, 221.01) * mm, "radius": 1.6 * mm});
            skCircle(sketch, "E5.5.34.0", {"center": v(-682.48, 216.01) * mm, "radius": 1.6 * mm});
            skCircle(sketch, "E5.5.34.1", {"center": v(-677.48, 216.01) * mm, "radius": 1.6 * mm});
            skCircle(sketch, "E5.5.34.2", {"center": v(-679.98, 211.01) * mm, "radius": 1.6 * mm});
            skCircle(sketch, "E5.5.34.3", {"center": v(-674.98, 211.01) * mm, "radius": 1.6 * mm});
            skCircle(sketch, "E5.5.35.0", {"center": v(-682.48, 206.01) * mm, "radius": 1.6 * mm});
            skCircle(sketch, "E5.5.35.1", {"center": v(-677.48, 206.01) * mm, "radius": 1.6 * mm});
            skCircle(sketch, "E5.5.35.2", {"center": v(-679.98, 201.01) * mm, "radius": 1.6 * mm});
            skCircle(sketch, "E5.5.35.3", {"center": v(-674.98, 201.01) * mm, "radius": 1.6 * mm});
            skCircle(sketch, "E5.5.36.0", {"center": v(-682.48, 196.01) * mm, "radius": 1.6 * mm});
            skCircle(sketch, "E5.5.36.1", {"center": v(-677.48, 196.01) * mm, "radius": 1.6 * mm});
            skCircle(sketch, "E5.5.36.2", {"center": v(-679.98, 191.01) * mm, "radius": 1.6 * mm});
            skCircle(sketch, "E5.5.36.3", {"center": v(-674.98, 191.01) * mm, "radius": 1.6 * mm});
            skCircle(sketch, "E5.5.37.0", {"center": v(-682.48, 186.01) * mm, "radius": 1.6 * mm});
            skCircle(sketch, "E5.5.37.1", {"center": v(-677.48, 186.01) * mm, "radius": 1.6 * mm});
            skCircle(sketch, "E5.5.37.2", {"center": v(-679.98, 181.01) * mm, "radius": 1.6 * mm});
            skCircle(sketch, "E5.5.37.3", {"center": v(-674.98, 181.01) * mm, "radius": 1.6 * mm});
            skCircle(sketch, "E5.5.38.0", {"center": v(-682.48, 176.01) * mm, "radius": 1.6 * mm});
            skCircle(sketch, "E5.5.38.1", {"center": v(-677.48, 176.01) * mm, "radius": 1.6 * mm});
            skCircle(sketch, "E5.5.38.2", {"center": v(-679.98, 171.01) * mm, "radius": 1.6 * mm});
            skCircle(sketch, "E5.5.38.3", {"center": v(-674.98, 171.01) * mm, "radius": 1.6 * mm});
            skCircle(sketch, "E5.5.39.0", {"center": v(-682.48, 166.01) * mm, "radius": 1.6 * mm});
            skCircle(sketch, "E5.5.39.1", {"center": v(-677.48, 166.01) * mm, "radius": 1.6 * mm});
            skCircle(sketch, "E5.5.39.2", {"center": v(-679.98, 161.01) * mm, "radius": 1.6 * mm});
            skCircle(sketch, "E5.5.39.3", {"center": v(-674.98, 161.01) * mm, "radius": 1.6 * mm});
            skCircle(sketch, "E5.5.40.0", {"center": v(-682.48, 156.01) * mm, "radius": 1.6 * mm});
            skCircle(sketch, "E5.5.40.1", {"center": v(-677.48, 156.01) * mm, "radius": 1.6 * mm});
            skCircle(sketch, "E5.5.40.2", {"center": v(-679.98, 151.01) * mm, "radius": 1.6 * mm});
            skCircle(sketch, "E5.5.40.3", {"center": v(-674.98, 151.01) * mm, "radius": 1.6 * mm});
            skCircle(sketch, "E5.5.41.0", {"center": v(-682.48, 146.01) * mm, "radius": 1.6 * mm});
            skCircle(sketch, "E5.5.41.1", {"center": v(-677.48, 146.01) * mm, "radius": 1.6 * mm});
            skCircle(sketch, "E5.5.41.2", {"center": v(-679.98, 141.01) * mm, "radius": 1.6 * mm});
            skCircle(sketch, "E5.5.41.3", {"center": v(-674.98, 141.01) * mm, "radius": 1.6 * mm});
            skCircle(sketch, "E5.5.42.0", {"center": v(-682.48, 136.01) * mm, "radius": 1.6 * mm});
            skCircle(sketch, "E5.5.42.1", {"center": v(-677.48, 136.01) * mm, "radius": 1.6 * mm});
            skCircle(sketch, "E5.5.42.2", {"center": v(-679.98, 131.01) * mm, "radius": 1.6 * mm});
            skCircle(sketch, "E5.5.42.3", {"center": v(-674.98, 131.01) * mm, "radius": 1.6 * mm});
            skCircle(sketch, "E5.5.43.0", {"center": v(-682.48, 126.01) * mm, "radius": 1.6 * mm});
            skCircle(sketch, "E5.5.43.1", {"center": v(-677.48, 126.01) * mm, "radius": 1.6 * mm});
            skCircle(sketch, "E5.5.43.2", {"center": v(-679.98, 121.01) * mm, "radius": 1.6 * mm});
            skCircle(sketch, "E5.5.43.3", {"center": v(-674.98, 121.01) * mm, "radius": 1.6 * mm});
            skCircle(sketch, "E5.5.44.0", {"center": v(-682.48, 116.01) * mm, "radius": 1.6 * mm});
            skCircle(sketch, "E5.5.44.1", {"center": v(-677.48, 116.01) * mm, "radius": 1.6 * mm});
            skCircle(sketch, "E5.5.44.2", {"center": v(-679.98, 111.01) * mm, "radius": 1.6 * mm});
            skCircle(sketch, "E5.5.44.3", {"center": v(-674.98, 111.01) * mm, "radius": 1.6 * mm});
            skCircle(sketch, "E5.5.45.0", {"center": v(-682.48, 106.01) * mm, "radius": 1.6 * mm});
            skCircle(sketch, "E5.5.45.1", {"center": v(-677.48, 106.01) * mm, "radius": 1.6 * mm});
            skCircle(sketch, "E5.5.45.2", {"center": v(-679.98, 101.01) * mm, "radius": 1.6 * mm});
            skCircle(sketch, "E5.5.45.3", {"center": v(-674.98, 101.01) * mm, "radius": 1.6 * mm});
            skCircle(sketch, "E5.5.46.0", {"center": v(-682.48, 96.01) * mm, "radius": 1.6 * mm});
            skCircle(sketch, "E5.5.46.1", {"center": v(-677.48, 96.01) * mm, "radius": 1.6 * mm});
            skCircle(sketch, "E5.5.46.2", {"center": v(-679.98, 91.01) * mm, "radius": 1.6 * mm});
            skCircle(sketch, "E5.5.46.3", {"center": v(-674.98, 91.01) * mm, "radius": 1.6 * mm});
            skCircle(sketch, "E5.5.47.0", {"center": v(-682.48, 86.01) * mm, "radius": 1.6 * mm});
            skCircle(sketch, "E5.5.47.1", {"center": v(-677.48, 86.01) * mm, "radius": 1.6 * mm});
            skCircle(sketch, "E5.5.47.2", {"center": v(-679.98, 81.01) * mm, "radius": 1.6 * mm});
            skCircle(sketch, "E5.5.47.3", {"center": v(-674.98, 81.01) * mm, "radius": 1.6 * mm});
            skCircle(sketch, "E5.5.48.0", {"center": v(-682.48, 76.01) * mm, "radius": 1.6 * mm});
            skCircle(sketch, "E5.5.48.1", {"center": v(-677.48, 76.01) * mm, "radius": 1.6 * mm});
            skCircle(sketch, "E5.5.48.2", {"center": v(-679.98, 71.01) * mm, "radius": 1.6 * mm});
            skCircle(sketch, "E5.5.48.3", {"center": v(-674.98, 71.01) * mm, "radius": 1.6 * mm});
            skCircle(sketch, "E5.5.49.0", {"center": v(-682.48, 66.01) * mm, "radius": 1.6 * mm});
            skCircle(sketch, "E5.5.49.1", {"center": v(-677.48, 66.01) * mm, "radius": 1.6 * mm});
            skCircle(sketch, "E5.5.49.2", {"center": v(-679.98, 61.01) * mm, "radius": 1.6 * mm});
            skCircle(sketch, "E5.5.49.3", {"center": v(-674.98, 61.01) * mm, "radius": 1.6 * mm});
            skCircle(sketch, "E5.6.0.0", {"center": v(-672.48, 556.01) * mm, "radius": 1.6 * mm});
            skCircle(sketch, "E5.6.0.1", {"center": v(-667.48, 556.01) * mm, "radius": 1.6 * mm});
            skCircle(sketch, "E5.6.0.2", {"center": v(-669.98, 551.01) * mm, "radius": 1.6 * mm});
            skCircle(sketch, "E5.6.0.3", {"center": v(-664.98, 551.01) * mm, "radius": 1.6 * mm});
            skCircle(sketch, "E5.6.1.0", {"center": v(-672.48, 546.01) * mm, "radius": 1.6 * mm});
            skCircle(sketch, "E5.6.1.1", {"center": v(-667.48, 546.01) * mm, "radius": 1.6 * mm});
            skCircle(sketch, "E5.6.1.2", {"center": v(-669.98, 541.01) * mm, "radius": 1.6 * mm});
            skCircle(sketch, "E5.6.1.3", {"center": v(-664.98, 541.01) * mm, "radius": 1.6 * mm});
            skCircle(sketch, "E5.6.2.0", {"center": v(-672.48, 536.01) * mm, "radius": 1.6 * mm});
            skCircle(sketch, "E5.6.2.1", {"center": v(-667.48, 536.01) * mm, "radius": 1.6 * mm});
            skCircle(sketch, "E5.6.2.2", {"center": v(-669.98, 531.01) * mm, "radius": 1.6 * mm});
            skCircle(sketch, "E5.6.2.3", {"center": v(-664.98, 531.01) * mm, "radius": 1.6 * mm});
            skCircle(sketch, "E5.6.3.0", {"center": v(-672.48, 526.01) * mm, "radius": 1.6 * mm});
            skCircle(sketch, "E5.6.3.1", {"center": v(-667.48, 526.01) * mm, "radius": 1.6 * mm});
            skCircle(sketch, "E5.6.3.2", {"center": v(-669.98, 521.01) * mm, "radius": 1.6 * mm});
            skCircle(sketch, "E5.6.3.3", {"center": v(-664.98, 521.01) * mm, "radius": 1.6 * mm});
            skCircle(sketch, "E5.6.4.0", {"center": v(-672.48, 516.01) * mm, "radius": 1.6 * mm});
            skCircle(sketch, "E5.6.4.1", {"center": v(-667.48, 516.01) * mm, "radius": 1.6 * mm});
            skCircle(sketch, "E5.6.4.2", {"center": v(-669.98, 511.01) * mm, "radius": 1.6 * mm});
            skCircle(sketch, "E5.6.4.3", {"center": v(-664.98, 511.01) * mm, "radius": 1.6 * mm});
            skCircle(sketch, "E5.6.5.0", {"center": v(-672.48, 506.01) * mm, "radius": 1.6 * mm});
            skCircle(sketch, "E5.6.5.1", {"center": v(-667.48, 506.01) * mm, "radius": 1.6 * mm});
            skCircle(sketch, "E5.6.5.2", {"center": v(-669.98, 501.01) * mm, "radius": 1.6 * mm});
            skCircle(sketch, "E5.6.5.3", {"center": v(-664.98, 501.01) * mm, "radius": 1.6 * mm});
            skCircle(sketch, "E5.6.6.0", {"center": v(-672.48, 496.01) * mm, "radius": 1.6 * mm});
            skCircle(sketch, "E5.6.6.1", {"center": v(-667.48, 496.01) * mm, "radius": 1.6 * mm});
            skCircle(sketch, "E5.6.6.2", {"center": v(-669.98, 491.01) * mm, "radius": 1.6 * mm});
            skCircle(sketch, "E5.6.6.3", {"center": v(-664.98, 491.01) * mm, "radius": 1.6 * mm});
            skCircle(sketch, "E5.6.7.0", {"center": v(-672.48, 486.01) * mm, "radius": 1.6 * mm});
            skCircle(sketch, "E5.6.7.1", {"center": v(-667.48, 486.01) * mm, "radius": 1.6 * mm});
            skCircle(sketch, "E5.6.7.2", {"center": v(-669.98, 481.01) * mm, "radius": 1.6 * mm});
            skCircle(sketch, "E5.6.7.3", {"center": v(-664.98, 481.01) * mm, "radius": 1.6 * mm});
            skCircle(sketch, "E5.6.8.0", {"center": v(-672.48, 476.01) * mm, "radius": 1.6 * mm});
            skCircle(sketch, "E5.6.8.1", {"center": v(-667.48, 476.01) * mm, "radius": 1.6 * mm});
            skCircle(sketch, "E5.6.8.2", {"center": v(-669.98, 471.01) * mm, "radius": 1.6 * mm});
            skCircle(sketch, "E5.6.8.3", {"center": v(-664.98, 471.01) * mm, "radius": 1.6 * mm});
            skCircle(sketch, "E5.6.9.0", {"center": v(-672.48, 466.01) * mm, "radius": 1.6 * mm});
            skCircle(sketch, "E5.6.9.1", {"center": v(-667.48, 466.01) * mm, "radius": 1.6 * mm});
            skCircle(sketch, "E5.6.9.2", {"center": v(-669.98, 461.01) * mm, "radius": 1.6 * mm});
            skCircle(sketch, "E5.6.9.3", {"center": v(-664.98, 461.01) * mm, "radius": 1.6 * mm});
            skCircle(sketch, "E5.6.10.0", {"center": v(-672.48, 456.01) * mm, "radius": 1.6 * mm});
            skCircle(sketch, "E5.6.10.1", {"center": v(-667.48, 456.01) * mm, "radius": 1.6 * mm});
            skCircle(sketch, "E5.6.10.2", {"center": v(-669.98, 451.01) * mm, "radius": 1.6 * mm});
            skCircle(sketch, "E5.6.10.3", {"center": v(-664.98, 451.01) * mm, "radius": 1.6 * mm});
            skCircle(sketch, "E5.6.11.0", {"center": v(-672.48, 446.01) * mm, "radius": 1.6 * mm});
            skCircle(sketch, "E5.6.11.1", {"center": v(-667.48, 446.01) * mm, "radius": 1.6 * mm});
            skCircle(sketch, "E5.6.11.2", {"center": v(-669.98, 441.01) * mm, "radius": 1.6 * mm});
            skCircle(sketch, "E5.6.11.3", {"center": v(-664.98, 441.01) * mm, "radius": 1.6 * mm});
            skCircle(sketch, "E5.6.12.0", {"center": v(-672.48, 436.01) * mm, "radius": 1.6 * mm});
            skCircle(sketch, "E5.6.12.1", {"center": v(-667.48, 436.01) * mm, "radius": 1.6 * mm});
            skCircle(sketch, "E5.6.12.2", {"center": v(-669.98, 431.01) * mm, "radius": 1.6 * mm});
            skCircle(sketch, "E5.6.12.3", {"center": v(-664.98, 431.01) * mm, "radius": 1.6 * mm});
            skCircle(sketch, "E5.6.13.0", {"center": v(-672.48, 426.01) * mm, "radius": 1.6 * mm});
            skCircle(sketch, "E5.6.13.1", {"center": v(-667.48, 426.01) * mm, "radius": 1.6 * mm});
            skCircle(sketch, "E5.6.13.2", {"center": v(-669.98, 421.01) * mm, "radius": 1.6 * mm});
            skCircle(sketch, "E5.6.13.3", {"center": v(-664.98, 421.01) * mm, "radius": 1.6 * mm});
            skCircle(sketch, "E5.6.14.0", {"center": v(-672.48, 416.01) * mm, "radius": 1.6 * mm});
            skCircle(sketch, "E5.6.14.1", {"center": v(-667.48, 416.01) * mm, "radius": 1.6 * mm});
            skCircle(sketch, "E5.6.14.2", {"center": v(-669.98, 411.01) * mm, "radius": 1.6 * mm});
            skCircle(sketch, "E5.6.14.3", {"center": v(-664.98, 411.01) * mm, "radius": 1.6 * mm});
            skCircle(sketch, "E5.6.15.0", {"center": v(-672.48, 406.01) * mm, "radius": 1.6 * mm});
            skCircle(sketch, "E5.6.15.1", {"center": v(-667.48, 406.01) * mm, "radius": 1.6 * mm});
            skCircle(sketch, "E5.6.15.2", {"center": v(-669.98, 401.01) * mm, "radius": 1.6 * mm});
            skCircle(sketch, "E5.6.15.3", {"center": v(-664.98, 401.01) * mm, "radius": 1.6 * mm});
            skCircle(sketch, "E5.6.16.0", {"center": v(-672.48, 396.01) * mm, "radius": 1.6 * mm});
            skCircle(sketch, "E5.6.16.1", {"center": v(-667.48, 396.01) * mm, "radius": 1.6 * mm});
            skCircle(sketch, "E5.6.16.2", {"center": v(-669.98, 391.01) * mm, "radius": 1.6 * mm});
            skCircle(sketch, "E5.6.16.3", {"center": v(-664.98, 391.01) * mm, "radius": 1.6 * mm});
            skCircle(sketch, "E5.6.17.0", {"center": v(-672.48, 386.01) * mm, "radius": 1.6 * mm});
            skCircle(sketch, "E5.6.17.1", {"center": v(-667.48, 386.01) * mm, "radius": 1.6 * mm});
            skCircle(sketch, "E5.6.17.2", {"center": v(-669.98, 381.01) * mm, "radius": 1.6 * mm});
            skCircle(sketch, "E5.6.17.3", {"center": v(-664.98, 381.01) * mm, "radius": 1.6 * mm});
            skCircle(sketch, "E5.6.18.0", {"center": v(-672.48, 376.01) * mm, "radius": 1.6 * mm});
            skCircle(sketch, "E5.6.18.1", {"center": v(-667.48, 376.01) * mm, "radius": 1.6 * mm});
            skCircle(sketch, "E5.6.18.2", {"center": v(-669.98, 371.01) * mm, "radius": 1.6 * mm});
            skCircle(sketch, "E5.6.18.3", {"center": v(-664.98, 371.01) * mm, "radius": 1.6 * mm});
            skCircle(sketch, "E5.6.19.0", {"center": v(-672.48, 366.01) * mm, "radius": 1.6 * mm});
            skCircle(sketch, "E5.6.19.1", {"center": v(-667.48, 366.01) * mm, "radius": 1.6 * mm});
            skCircle(sketch, "E5.6.19.2", {"center": v(-669.98, 361.01) * mm, "radius": 1.6 * mm});
            skCircle(sketch, "E5.6.19.3", {"center": v(-664.98, 361.01) * mm, "radius": 1.6 * mm});
            skCircle(sketch, "E5.6.20.0", {"center": v(-672.48, 356.01) * mm, "radius": 1.6 * mm});
            skCircle(sketch, "E5.6.20.1", {"center": v(-667.48, 356.01) * mm, "radius": 1.6 * mm});
            skCircle(sketch, "E5.6.20.2", {"center": v(-669.98, 351.01) * mm, "radius": 1.6 * mm});
            skCircle(sketch, "E5.6.20.3", {"center": v(-664.98, 351.01) * mm, "radius": 1.6 * mm});
            skCircle(sketch, "E5.6.21.0", {"center": v(-672.48, 346.01) * mm, "radius": 1.6 * mm});
            skCircle(sketch, "E5.6.21.1", {"center": v(-667.48, 346.01) * mm, "radius": 1.6 * mm});
            skCircle(sketch, "E5.6.21.2", {"center": v(-669.98, 341.01) * mm, "radius": 1.6 * mm});
            skCircle(sketch, "E5.6.21.3", {"center": v(-664.98, 341.01) * mm, "radius": 1.6 * mm});
            skCircle(sketch, "E5.6.22.0", {"center": v(-672.48, 336.01) * mm, "radius": 1.6 * mm});
            skCircle(sketch, "E5.6.22.1", {"center": v(-667.48, 336.01) * mm, "radius": 1.6 * mm});
            skCircle(sketch, "E5.6.22.2", {"center": v(-669.98, 331.01) * mm, "radius": 1.6 * mm});
            skCircle(sketch, "E5.6.22.3", {"center": v(-664.98, 331.01) * mm, "radius": 1.6 * mm});
            skCircle(sketch, "E5.6.23.0", {"center": v(-672.48, 326.01) * mm, "radius": 1.6 * mm});
            skCircle(sketch, "E5.6.23.1", {"center": v(-667.48, 326.01) * mm, "radius": 1.6 * mm});
            skCircle(sketch, "E5.6.23.2", {"center": v(-669.98, 321.01) * mm, "radius": 1.6 * mm});
            skCircle(sketch, "E5.6.23.3", {"center": v(-664.98, 321.01) * mm, "radius": 1.6 * mm});
            skCircle(sketch, "E5.6.24.0", {"center": v(-672.48, 316.01) * mm, "radius": 1.6 * mm});
            skCircle(sketch, "E5.6.24.1", {"center": v(-667.48, 316.01) * mm, "radius": 1.6 * mm});
            skCircle(sketch, "E5.6.24.2", {"center": v(-669.98, 311.01) * mm, "radius": 1.6 * mm});
            skCircle(sketch, "E5.6.24.3", {"center": v(-664.98, 311.01) * mm, "radius": 1.6 * mm});
            skCircle(sketch, "E5.6.25.0", {"center": v(-672.48, 306.01) * mm, "radius": 1.6 * mm});
            skCircle(sketch, "E5.6.25.1", {"center": v(-667.48, 306.01) * mm, "radius": 1.6 * mm});
            skCircle(sketch, "E5.6.25.2", {"center": v(-669.98, 301.01) * mm, "radius": 1.6 * mm});
            skCircle(sketch, "E5.6.25.3", {"center": v(-664.98, 301.01) * mm, "radius": 1.6 * mm});
            skCircle(sketch, "E5.6.26.0", {"center": v(-672.48, 296.01) * mm, "radius": 1.6 * mm});
            skCircle(sketch, "E5.6.26.1", {"center": v(-667.48, 296.01) * mm, "radius": 1.6 * mm});
            skCircle(sketch, "E5.6.26.2", {"center": v(-669.98, 291.01) * mm, "radius": 1.6 * mm});
            skCircle(sketch, "E5.6.26.3", {"center": v(-664.98, 291.01) * mm, "radius": 1.6 * mm});
            skCircle(sketch, "E5.6.27.0", {"center": v(-672.48, 286.01) * mm, "radius": 1.6 * mm});
            skCircle(sketch, "E5.6.27.1", {"center": v(-667.48, 286.01) * mm, "radius": 1.6 * mm});
            skCircle(sketch, "E5.6.27.2", {"center": v(-669.98, 281.01) * mm, "radius": 1.6 * mm});
            skCircle(sketch, "E5.6.27.3", {"center": v(-664.98, 281.01) * mm, "radius": 1.6 * mm});
            skCircle(sketch, "E5.6.28.0", {"center": v(-672.48, 276.01) * mm, "radius": 1.6 * mm});
            skCircle(sketch, "E5.6.28.1", {"center": v(-667.48, 276.01) * mm, "radius": 1.6 * mm});
            skCircle(sketch, "E5.6.28.2", {"center": v(-669.98, 271.01) * mm, "radius": 1.6 * mm});
            skCircle(sketch, "E5.6.28.3", {"center": v(-664.98, 271.01) * mm, "radius": 1.6 * mm});
            skCircle(sketch, "E5.6.29.0", {"center": v(-672.48, 266.01) * mm, "radius": 1.6 * mm});
            skCircle(sketch, "E5.6.29.1", {"center": v(-667.48, 266.01) * mm, "radius": 1.6 * mm});
            skCircle(sketch, "E5.6.29.2", {"center": v(-669.98, 261.01) * mm, "radius": 1.6 * mm});
            skCircle(sketch, "E5.6.29.3", {"center": v(-664.98, 261.01) * mm, "radius": 1.6 * mm});
            skCircle(sketch, "E5.6.30.0", {"center": v(-672.48, 256.01) * mm, "radius": 1.6 * mm});
            skCircle(sketch, "E5.6.30.1", {"center": v(-667.48, 256.01) * mm, "radius": 1.6 * mm});
            skCircle(sketch, "E5.6.30.2", {"center": v(-669.98, 251.01) * mm, "radius": 1.6 * mm});
            skCircle(sketch, "E5.6.30.3", {"center": v(-664.98, 251.01) * mm, "radius": 1.6 * mm});
            skCircle(sketch, "E5.6.31.0", {"center": v(-672.48, 246.01) * mm, "radius": 1.6 * mm});
            skCircle(sketch, "E5.6.31.1", {"center": v(-667.48, 246.01) * mm, "radius": 1.6 * mm});
            skCircle(sketch, "E5.6.31.2", {"center": v(-669.98, 241.01) * mm, "radius": 1.6 * mm});
            skCircle(sketch, "E5.6.31.3", {"center": v(-664.98, 241.01) * mm, "radius": 1.6 * mm});
            skCircle(sketch, "E5.6.32.0", {"center": v(-672.48, 236.01) * mm, "radius": 1.6 * mm});
            skCircle(sketch, "E5.6.32.1", {"center": v(-667.48, 236.01) * mm, "radius": 1.6 * mm});
            skCircle(sketch, "E5.6.32.2", {"center": v(-669.98, 231.01) * mm, "radius": 1.6 * mm});
            skCircle(sketch, "E5.6.32.3", {"center": v(-664.98, 231.01) * mm, "radius": 1.6 * mm});
            skCircle(sketch, "E5.6.33.0", {"center": v(-672.48, 226.01) * mm, "radius": 1.6 * mm});
            skCircle(sketch, "E5.6.33.1", {"center": v(-667.48, 226.01) * mm, "radius": 1.6 * mm});
            skCircle(sketch, "E5.6.33.2", {"center": v(-669.98, 221.01) * mm, "radius": 1.6 * mm});
            skCircle(sketch, "E5.6.33.3", {"center": v(-664.98, 221.01) * mm, "radius": 1.6 * mm});
            skCircle(sketch, "E5.6.34.0", {"center": v(-672.48, 216.01) * mm, "radius": 1.6 * mm});
            skCircle(sketch, "E5.6.34.1", {"center": v(-667.48, 216.01) * mm, "radius": 1.6 * mm});
            skCircle(sketch, "E5.6.34.2", {"center": v(-669.98, 211.01) * mm, "radius": 1.6 * mm});
            skCircle(sketch, "E5.6.34.3", {"center": v(-664.98, 211.01) * mm, "radius": 1.6 * mm});
            skCircle(sketch, "E5.6.35.0", {"center": v(-672.48, 206.01) * mm, "radius": 1.6 * mm});
            skCircle(sketch, "E5.6.35.1", {"center": v(-667.48, 206.01) * mm, "radius": 1.6 * mm});
            skCircle(sketch, "E5.6.35.2", {"center": v(-669.98, 201.01) * mm, "radius": 1.6 * mm});
            skCircle(sketch, "E5.6.35.3", {"center": v(-664.98, 201.01) * mm, "radius": 1.6 * mm});
            skCircle(sketch, "E5.6.36.0", {"center": v(-672.48, 196.01) * mm, "radius": 1.6 * mm});
            skCircle(sketch, "E5.6.36.1", {"center": v(-667.48, 196.01) * mm, "radius": 1.6 * mm});
            skCircle(sketch, "E5.6.36.2", {"center": v(-669.98, 191.01) * mm, "radius": 1.6 * mm});
            skCircle(sketch, "E5.6.36.3", {"center": v(-664.98, 191.01) * mm, "radius": 1.6 * mm});
            skCircle(sketch, "E5.6.37.0", {"center": v(-672.48, 186.01) * mm, "radius": 1.6 * mm});
            skCircle(sketch, "E5.6.37.1", {"center": v(-667.48, 186.01) * mm, "radius": 1.6 * mm});
            skCircle(sketch, "E5.6.37.2", {"center": v(-669.98, 181.01) * mm, "radius": 1.6 * mm});
            skCircle(sketch, "E5.6.37.3", {"center": v(-664.98, 181.01) * mm, "radius": 1.6 * mm});
            skCircle(sketch, "E5.6.38.0", {"center": v(-672.48, 176.01) * mm, "radius": 1.6 * mm});
            skCircle(sketch, "E5.6.38.1", {"center": v(-667.48, 176.01) * mm, "radius": 1.6 * mm});
            skCircle(sketch, "E5.6.38.2", {"center": v(-669.98, 171.01) * mm, "radius": 1.6 * mm});
            skCircle(sketch, "E5.6.38.3", {"center": v(-664.98, 171.01) * mm, "radius": 1.6 * mm});
            skCircle(sketch, "E5.6.39.0", {"center": v(-672.48, 166.01) * mm, "radius": 1.6 * mm});
            skCircle(sketch, "E5.6.39.1", {"center": v(-667.48, 166.01) * mm, "radius": 1.6 * mm});
            skCircle(sketch, "E5.6.39.2", {"center": v(-669.98, 161.01) * mm, "radius": 1.6 * mm});
            skCircle(sketch, "E5.6.39.3", {"center": v(-664.98, 161.01) * mm, "radius": 1.6 * mm});
            skCircle(sketch, "E5.6.40.0", {"center": v(-672.48, 156.01) * mm, "radius": 1.6 * mm});
            skCircle(sketch, "E5.6.40.1", {"center": v(-667.48, 156.01) * mm, "radius": 1.6 * mm});
            skCircle(sketch, "E5.6.40.2", {"center": v(-669.98, 151.01) * mm, "radius": 1.6 * mm});
            skCircle(sketch, "E5.6.40.3", {"center": v(-664.98, 151.01) * mm, "radius": 1.6 * mm});
            skCircle(sketch, "E5.6.41.0", {"center": v(-672.48, 146.01) * mm, "radius": 1.6 * mm});
            skCircle(sketch, "E5.6.41.1", {"center": v(-667.48, 146.01) * mm, "radius": 1.6 * mm});
            skCircle(sketch, "E5.6.41.2", {"center": v(-669.98, 141.01) * mm, "radius": 1.6 * mm});
            skCircle(sketch, "E5.6.41.3", {"center": v(-664.98, 141.01) * mm, "radius": 1.6 * mm});
            skCircle(sketch, "E5.6.42.0", {"center": v(-672.48, 136.01) * mm, "radius": 1.6 * mm});
            skCircle(sketch, "E5.6.42.1", {"center": v(-667.48, 136.01) * mm, "radius": 1.6 * mm});
            skCircle(sketch, "E5.6.42.2", {"center": v(-669.98, 131.01) * mm, "radius": 1.6 * mm});
            skCircle(sketch, "E5.6.42.3", {"center": v(-664.98, 131.01) * mm, "radius": 1.6 * mm});
            skCircle(sketch, "E5.6.43.0", {"center": v(-672.48, 126.01) * mm, "radius": 1.6 * mm});
            skCircle(sketch, "E5.6.43.1", {"center": v(-667.48, 126.01) * mm, "radius": 1.6 * mm});
            skCircle(sketch, "E5.6.43.2", {"center": v(-669.98, 121.01) * mm, "radius": 1.6 * mm});
            skCircle(sketch, "E5.6.43.3", {"center": v(-664.98, 121.01) * mm, "radius": 1.6 * mm});
            skCircle(sketch, "E5.6.44.0", {"center": v(-672.48, 116.01) * mm, "radius": 1.6 * mm});
            skCircle(sketch, "E5.6.44.1", {"center": v(-667.48, 116.01) * mm, "radius": 1.6 * mm});
            skCircle(sketch, "E5.6.44.2", {"center": v(-669.98, 111.01) * mm, "radius": 1.6 * mm});
            skCircle(sketch, "E5.6.44.3", {"center": v(-664.98, 111.01) * mm, "radius": 1.6 * mm});
            skCircle(sketch, "E5.6.45.0", {"center": v(-672.48, 106.01) * mm, "radius": 1.6 * mm});
            skCircle(sketch, "E5.6.45.1", {"center": v(-667.48, 106.01) * mm, "radius": 1.6 * mm});
            skCircle(sketch, "E5.6.45.2", {"center": v(-669.98, 101.01) * mm, "radius": 1.6 * mm});
            skCircle(sketch, "E5.6.45.3", {"center": v(-664.98, 101.01) * mm, "radius": 1.6 * mm});
            skCircle(sketch, "E5.6.46.0", {"center": v(-672.48, 96.01) * mm, "radius": 1.6 * mm});
            skCircle(sketch, "E5.6.46.1", {"center": v(-667.48, 96.01) * mm, "radius": 1.6 * mm});
            skCircle(sketch, "E5.6.46.2", {"center": v(-669.98, 91.01) * mm, "radius": 1.6 * mm});
            skCircle(sketch, "E5.6.46.3", {"center": v(-664.98, 91.01) * mm, "radius": 1.6 * mm});
            skCircle(sketch, "E5.6.47.0", {"center": v(-672.48, 86.01) * mm, "radius": 1.6 * mm});
            skCircle(sketch, "E5.6.47.1", {"center": v(-667.48, 86.01) * mm, "radius": 1.6 * mm});
            skCircle(sketch, "E5.6.47.2", {"center": v(-669.98, 81.01) * mm, "radius": 1.6 * mm});
            skCircle(sketch, "E5.6.47.3", {"center": v(-664.98, 81.01) * mm, "radius": 1.6 * mm});
            skCircle(sketch, "E5.6.48.0", {"center": v(-672.48, 76.01) * mm, "radius": 1.6 * mm});
            skCircle(sketch, "E5.6.48.1", {"center": v(-667.48, 76.01) * mm, "radius": 1.6 * mm});
            skCircle(sketch, "E5.6.48.2", {"center": v(-669.98, 71.01) * mm, "radius": 1.6 * mm});
            skCircle(sketch, "E5.6.48.3", {"center": v(-664.98, 71.01) * mm, "radius": 1.6 * mm});
            skCircle(sketch, "E5.6.49.0", {"center": v(-672.48, 66.01) * mm, "radius": 1.6 * mm});
            skCircle(sketch, "E5.6.49.1", {"center": v(-667.48, 66.01) * mm, "radius": 1.6 * mm});
            skCircle(sketch, "E5.6.49.2", {"center": v(-669.98, 61.01) * mm, "radius": 1.6 * mm});
            skCircle(sketch, "E5.6.49.3", {"center": v(-664.98, 61.01) * mm, "radius": 1.6 * mm});
            skCircle(sketch, "E5.7.0.0", {"center": v(-662.48, 556.01) * mm, "radius": 1.6 * mm});
            skCircle(sketch, "E5.7.0.1", {"center": v(-657.48, 556.01) * mm, "radius": 1.6 * mm});
            skCircle(sketch, "E5.7.0.2", {"center": v(-659.98, 551.01) * mm, "radius": 1.6 * mm});
            skCircle(sketch, "E5.7.0.3", {"center": v(-654.98, 551.01) * mm, "radius": 1.6 * mm});
            skCircle(sketch, "E5.7.1.0", {"center": v(-662.48, 546.01) * mm, "radius": 1.6 * mm});
            skCircle(sketch, "E5.7.1.1", {"center": v(-657.48, 546.01) * mm, "radius": 1.6 * mm});
            skCircle(sketch, "E5.7.1.2", {"center": v(-659.98, 541.01) * mm, "radius": 1.6 * mm});
            skCircle(sketch, "E5.7.1.3", {"center": v(-654.98, 541.01) * mm, "radius": 1.6 * mm});
            skCircle(sketch, "E5.7.2.0", {"center": v(-662.48, 536.01) * mm, "radius": 1.6 * mm});
            skCircle(sketch, "E5.7.2.1", {"center": v(-657.48, 536.01) * mm, "radius": 1.6 * mm});
            skCircle(sketch, "E5.7.2.2", {"center": v(-659.98, 531.01) * mm, "radius": 1.6 * mm});
            skCircle(sketch, "E5.7.2.3", {"center": v(-654.98, 531.01) * mm, "radius": 1.6 * mm});
            skCircle(sketch, "E5.7.3.0", {"center": v(-662.48, 526.01) * mm, "radius": 1.6 * mm});
            skCircle(sketch, "E5.7.3.1", {"center": v(-657.48, 526.01) * mm, "radius": 1.6 * mm});
            skCircle(sketch, "E5.7.3.2", {"center": v(-659.98, 521.01) * mm, "radius": 1.6 * mm});
            skCircle(sketch, "E5.7.3.3", {"center": v(-654.98, 521.01) * mm, "radius": 1.6 * mm});
            skCircle(sketch, "E5.7.4.0", {"center": v(-662.48, 516.01) * mm, "radius": 1.6 * mm});
            skCircle(sketch, "E5.7.4.1", {"center": v(-657.48, 516.01) * mm, "radius": 1.6 * mm});
            skCircle(sketch, "E5.7.4.2", {"center": v(-659.98, 511.01) * mm, "radius": 1.6 * mm});
            skCircle(sketch, "E5.7.4.3", {"center": v(-654.98, 511.01) * mm, "radius": 1.6 * mm});
            skCircle(sketch, "E5.7.5.0", {"center": v(-662.48, 506.01) * mm, "radius": 1.6 * mm});
            skCircle(sketch, "E5.7.5.1", {"center": v(-657.48, 506.01) * mm, "radius": 1.6 * mm});
            skCircle(sketch, "E5.7.5.2", {"center": v(-659.98, 501.01) * mm, "radius": 1.6 * mm});
            skCircle(sketch, "E5.7.5.3", {"center": v(-654.98, 501.01) * mm, "radius": 1.6 * mm});
            skCircle(sketch, "E5.7.6.0", {"center": v(-662.48, 496.01) * mm, "radius": 1.6 * mm});
            skCircle(sketch, "E5.7.6.1", {"center": v(-657.48, 496.01) * mm, "radius": 1.6 * mm});
            skCircle(sketch, "E5.7.6.2", {"center": v(-659.98, 491.01) * mm, "radius": 1.6 * mm});
            skCircle(sketch, "E5.7.6.3", {"center": v(-654.98, 491.01) * mm, "radius": 1.6 * mm});
            skCircle(sketch, "E5.7.7.0", {"center": v(-662.48, 486.01) * mm, "radius": 1.6 * mm});
            skCircle(sketch, "E5.7.7.1", {"center": v(-657.48, 486.01) * mm, "radius": 1.6 * mm});
            skCircle(sketch, "E5.7.7.2", {"center": v(-659.98, 481.01) * mm, "radius": 1.6 * mm});
            skCircle(sketch, "E5.7.7.3", {"center": v(-654.98, 481.01) * mm, "radius": 1.6 * mm});
            skCircle(sketch, "E5.7.8.0", {"center": v(-662.48, 476.01) * mm, "radius": 1.6 * mm});
            skCircle(sketch, "E5.7.8.1", {"center": v(-657.48, 476.01) * mm, "radius": 1.6 * mm});
            skCircle(sketch, "E5.7.8.2", {"center": v(-659.98, 471.01) * mm, "radius": 1.6 * mm});
            skCircle(sketch, "E5.7.8.3", {"center": v(-654.98, 471.01) * mm, "radius": 1.6 * mm});
            skCircle(sketch, "E5.7.9.0", {"center": v(-662.48, 466.01) * mm, "radius": 1.6 * mm});
            skCircle(sketch, "E5.7.9.1", {"center": v(-657.48, 466.01) * mm, "radius": 1.6 * mm});
            skCircle(sketch, "E5.7.9.2", {"center": v(-659.98, 461.01) * mm, "radius": 1.6 * mm});
            skCircle(sketch, "E5.7.9.3", {"center": v(-654.98, 461.01) * mm, "radius": 1.6 * mm});
            skCircle(sketch, "E5.7.10.0", {"center": v(-662.48, 456.01) * mm, "radius": 1.6 * mm});
            skCircle(sketch, "E5.7.10.1", {"center": v(-657.48, 456.01) * mm, "radius": 1.6 * mm});
            skCircle(sketch, "E5.7.10.2", {"center": v(-659.98, 451.01) * mm, "radius": 1.6 * mm});
            skCircle(sketch, "E5.7.10.3", {"center": v(-654.98, 451.01) * mm, "radius": 1.6 * mm});
            skCircle(sketch, "E5.7.11.0", {"center": v(-662.48, 446.01) * mm, "radius": 1.6 * mm});
            skCircle(sketch, "E5.7.11.1", {"center": v(-657.48, 446.01) * mm, "radius": 1.6 * mm});
            skCircle(sketch, "E5.7.11.2", {"center": v(-659.98, 441.01) * mm, "radius": 1.6 * mm});
            skCircle(sketch, "E5.7.11.3", {"center": v(-654.98, 441.01) * mm, "radius": 1.6 * mm});
            skCircle(sketch, "E5.7.12.0", {"center": v(-662.48, 436.01) * mm, "radius": 1.6 * mm});
            skCircle(sketch, "E5.7.12.1", {"center": v(-657.48, 436.01) * mm, "radius": 1.6 * mm});
            skCircle(sketch, "E5.7.12.2", {"center": v(-659.98, 431.01) * mm, "radius": 1.6 * mm});
            skCircle(sketch, "E5.7.12.3", {"center": v(-654.98, 431.01) * mm, "radius": 1.6 * mm});
            skCircle(sketch, "E5.7.13.0", {"center": v(-662.48, 426.01) * mm, "radius": 1.6 * mm});
            skCircle(sketch, "E5.7.13.1", {"center": v(-657.48, 426.01) * mm, "radius": 1.6 * mm});
            skCircle(sketch, "E5.7.13.2", {"center": v(-659.98, 421.01) * mm, "radius": 1.6 * mm});
            skCircle(sketch, "E5.7.13.3", {"center": v(-654.98, 421.01) * mm, "radius": 1.6 * mm});
            skCircle(sketch, "E5.7.14.0", {"center": v(-662.48, 416.01) * mm, "radius": 1.6 * mm});
            skCircle(sketch, "E5.7.14.1", {"center": v(-657.48, 416.01) * mm, "radius": 1.6 * mm});
            skCircle(sketch, "E5.7.14.2", {"center": v(-659.98, 411.01) * mm, "radius": 1.6 * mm});
            skCircle(sketch, "E5.7.14.3", {"center": v(-654.98, 411.01) * mm, "radius": 1.6 * mm});
            skCircle(sketch, "E5.7.15.0", {"center": v(-662.48, 406.01) * mm, "radius": 1.6 * mm});
            skCircle(sketch, "E5.7.15.1", {"center": v(-657.48, 406.01) * mm, "radius": 1.6 * mm});
            skCircle(sketch, "E5.7.15.2", {"center": v(-659.98, 401.01) * mm, "radius": 1.6 * mm});
            skCircle(sketch, "E5.7.15.3", {"center": v(-654.98, 401.01) * mm, "radius": 1.6 * mm});
            skCircle(sketch, "E5.7.16.0", {"center": v(-662.48, 396.01) * mm, "radius": 1.6 * mm});
            skCircle(sketch, "E5.7.16.1", {"center": v(-657.48, 396.01) * mm, "radius": 1.6 * mm});
            skCircle(sketch, "E5.7.16.2", {"center": v(-659.98, 391.01) * mm, "radius": 1.6 * mm});
            skCircle(sketch, "E5.7.16.3", {"center": v(-654.98, 391.01) * mm, "radius": 1.6 * mm});
            skCircle(sketch, "E5.7.17.0", {"center": v(-662.48, 386.01) * mm, "radius": 1.6 * mm});
            skCircle(sketch, "E5.7.17.1", {"center": v(-657.48, 386.01) * mm, "radius": 1.6 * mm});
            skCircle(sketch, "E5.7.17.2", {"center": v(-659.98, 381.01) * mm, "radius": 1.6 * mm});
            skCircle(sketch, "E5.7.17.3", {"center": v(-654.98, 381.01) * mm, "radius": 1.6 * mm});
            skCircle(sketch, "E5.7.18.0", {"center": v(-662.48, 376.01) * mm, "radius": 1.6 * mm});
            skCircle(sketch, "E5.7.18.1", {"center": v(-657.48, 376.01) * mm, "radius": 1.6 * mm});
            skCircle(sketch, "E5.7.18.2", {"center": v(-659.98, 371.01) * mm, "radius": 1.6 * mm});
            skCircle(sketch, "E5.7.18.3", {"center": v(-654.98, 371.01) * mm, "radius": 1.6 * mm});
            skCircle(sketch, "E5.7.19.0", {"center": v(-662.48, 366.01) * mm, "radius": 1.6 * mm});
            skCircle(sketch, "E5.7.19.1", {"center": v(-657.48, 366.01) * mm, "radius": 1.6 * mm});
            skCircle(sketch, "E5.7.19.2", {"center": v(-659.98, 361.01) * mm, "radius": 1.6 * mm});
            skCircle(sketch, "E5.7.19.3", {"center": v(-654.98, 361.01) * mm, "radius": 1.6 * mm});
            skCircle(sketch, "E5.7.20.0", {"center": v(-662.48, 356.01) * mm, "radius": 1.6 * mm});
            skCircle(sketch, "E5.7.20.1", {"center": v(-657.48, 356.01) * mm, "radius": 1.6 * mm});
            skCircle(sketch, "E5.7.20.2", {"center": v(-659.98, 351.01) * mm, "radius": 1.6 * mm});
            skCircle(sketch, "E5.7.20.3", {"center": v(-654.98, 351.01) * mm, "radius": 1.6 * mm});
            skCircle(sketch, "E5.7.21.0", {"center": v(-662.48, 346.01) * mm, "radius": 1.6 * mm});
            skCircle(sketch, "E5.7.21.1", {"center": v(-657.48, 346.01) * mm, "radius": 1.6 * mm});
            skCircle(sketch, "E5.7.21.2", {"center": v(-659.98, 341.01) * mm, "radius": 1.6 * mm});
            skCircle(sketch, "E5.7.21.3", {"center": v(-654.98, 341.01) * mm, "radius": 1.6 * mm});
            skCircle(sketch, "E5.7.22.0", {"center": v(-662.48, 336.01) * mm, "radius": 1.6 * mm});
            skCircle(sketch, "E5.7.22.1", {"center": v(-657.48, 336.01) * mm, "radius": 1.6 * mm});
            skCircle(sketch, "E5.7.22.2", {"center": v(-659.98, 331.01) * mm, "radius": 1.6 * mm});
            skCircle(sketch, "E5.7.22.3", {"center": v(-654.98, 331.01) * mm, "radius": 1.6 * mm});
            skCircle(sketch, "E5.7.23.0", {"center": v(-662.48, 326.01) * mm, "radius": 1.6 * mm});
            skCircle(sketch, "E5.7.23.1", {"center": v(-657.48, 326.01) * mm, "radius": 1.6 * mm});
            skCircle(sketch, "E5.7.23.2", {"center": v(-659.98, 321.01) * mm, "radius": 1.6 * mm});
            skCircle(sketch, "E5.7.23.3", {"center": v(-654.98, 321.01) * mm, "radius": 1.6 * mm});
            skCircle(sketch, "E5.7.24.0", {"center": v(-662.48, 316.01) * mm, "radius": 1.6 * mm});
            skCircle(sketch, "E5.7.24.1", {"center": v(-657.48, 316.01) * mm, "radius": 1.6 * mm});
            skCircle(sketch, "E5.7.24.2", {"center": v(-659.98, 311.01) * mm, "radius": 1.6 * mm});
            skCircle(sketch, "E5.7.24.3", {"center": v(-654.98, 311.01) * mm, "radius": 1.6 * mm});
            skCircle(sketch, "E5.7.25.0", {"center": v(-662.48, 306.01) * mm, "radius": 1.6 * mm});
            skCircle(sketch, "E5.7.25.1", {"center": v(-657.48, 306.01) * mm, "radius": 1.6 * mm});
            skCircle(sketch, "E5.7.25.2", {"center": v(-659.98, 301.01) * mm, "radius": 1.6 * mm});
            skCircle(sketch, "E5.7.25.3", {"center": v(-654.98, 301.01) * mm, "radius": 1.6 * mm});
            skCircle(sketch, "E5.7.26.0", {"center": v(-662.48, 296.01) * mm, "radius": 1.6 * mm});
            skCircle(sketch, "E5.7.26.1", {"center": v(-657.48, 296.01) * mm, "radius": 1.6 * mm});
            skCircle(sketch, "E5.7.26.2", {"center": v(-659.98, 291.01) * mm, "radius": 1.6 * mm});
            skCircle(sketch, "E5.7.26.3", {"center": v(-654.98, 291.01) * mm, "radius": 1.6 * mm});
            skCircle(sketch, "E5.7.27.0", {"center": v(-662.48, 286.01) * mm, "radius": 1.6 * mm});
            skCircle(sketch, "E5.7.27.1", {"center": v(-657.48, 286.01) * mm, "radius": 1.6 * mm});
            skCircle(sketch, "E5.7.27.2", {"center": v(-659.98, 281.01) * mm, "radius": 1.6 * mm});
            skCircle(sketch, "E5.7.27.3", {"center": v(-654.98, 281.01) * mm, "radius": 1.6 * mm});
            skCircle(sketch, "E5.7.28.0", {"center": v(-662.48, 276.01) * mm, "radius": 1.6 * mm});
            skCircle(sketch, "E5.7.28.1", {"center": v(-657.48, 276.01) * mm, "radius": 1.6 * mm});
            skCircle(sketch, "E5.7.28.2", {"center": v(-659.98, 271.01) * mm, "radius": 1.6 * mm});
            skCircle(sketch, "E5.7.28.3", {"center": v(-654.98, 271.01) * mm, "radius": 1.6 * mm});
            skCircle(sketch, "E5.7.29.0", {"center": v(-662.48, 266.01) * mm, "radius": 1.6 * mm});
            skCircle(sketch, "E5.7.29.1", {"center": v(-657.48, 266.01) * mm, "radius": 1.6 * mm});
            skCircle(sketch, "E5.7.29.2", {"center": v(-659.98, 261.01) * mm, "radius": 1.6 * mm});
            skCircle(sketch, "E5.7.29.3", {"center": v(-654.98, 261.01) * mm, "radius": 1.6 * mm});
            skCircle(sketch, "E5.7.30.0", {"center": v(-662.48, 256.01) * mm, "radius": 1.6 * mm});
            skCircle(sketch, "E5.7.30.1", {"center": v(-657.48, 256.01) * mm, "radius": 1.6 * mm});
            skCircle(sketch, "E5.7.30.2", {"center": v(-659.98, 251.01) * mm, "radius": 1.6 * mm});
            skCircle(sketch, "E5.7.30.3", {"center": v(-654.98, 251.01) * mm, "radius": 1.6 * mm});
            skCircle(sketch, "E5.7.31.0", {"center": v(-662.48, 246.01) * mm, "radius": 1.6 * mm});
            skCircle(sketch, "E5.7.31.1", {"center": v(-657.48, 246.01) * mm, "radius": 1.6 * mm});
            skCircle(sketch, "E5.7.31.2", {"center": v(-659.98, 241.01) * mm, "radius": 1.6 * mm});
            skCircle(sketch, "E5.7.31.3", {"center": v(-654.98, 241.01) * mm, "radius": 1.6 * mm});
            skCircle(sketch, "E5.7.32.0", {"center": v(-662.48, 236.01) * mm, "radius": 1.6 * mm});
            skCircle(sketch, "E5.7.32.1", {"center": v(-657.48, 236.01) * mm, "radius": 1.6 * mm});
            skCircle(sketch, "E5.7.32.2", {"center": v(-659.98, 231.01) * mm, "radius": 1.6 * mm});
            skCircle(sketch, "E5.7.32.3", {"center": v(-654.98, 231.01) * mm, "radius": 1.6 * mm});
            skCircle(sketch, "E5.7.33.0", {"center": v(-662.48, 226.01) * mm, "radius": 1.6 * mm});
            skCircle(sketch, "E5.7.33.1", {"center": v(-657.48, 226.01) * mm, "radius": 1.6 * mm});
            skCircle(sketch, "E5.7.33.2", {"center": v(-659.98, 221.01) * mm, "radius": 1.6 * mm});
            skCircle(sketch, "E5.7.33.3", {"center": v(-654.98, 221.01) * mm, "radius": 1.6 * mm});
            skCircle(sketch, "E5.7.34.0", {"center": v(-662.48, 216.01) * mm, "radius": 1.6 * mm});
            skCircle(sketch, "E5.7.34.1", {"center": v(-657.48, 216.01) * mm, "radius": 1.6 * mm});
            skCircle(sketch, "E5.7.34.2", {"center": v(-659.98, 211.01) * mm, "radius": 1.6 * mm});
            skCircle(sketch, "E5.7.34.3", {"center": v(-654.98, 211.01) * mm, "radius": 1.6 * mm});
            skCircle(sketch, "E5.7.35.0", {"center": v(-662.48, 206.01) * mm, "radius": 1.6 * mm});
            skCircle(sketch, "E5.7.35.1", {"center": v(-657.48, 206.01) * mm, "radius": 1.6 * mm});
            skCircle(sketch, "E5.7.35.2", {"center": v(-659.98, 201.01) * mm, "radius": 1.6 * mm});
            skCircle(sketch, "E5.7.35.3", {"center": v(-654.98, 201.01) * mm, "radius": 1.6 * mm});
            skCircle(sketch, "E5.7.36.0", {"center": v(-662.48, 196.01) * mm, "radius": 1.6 * mm});
            skCircle(sketch, "E5.7.36.1", {"center": v(-657.48, 196.01) * mm, "radius": 1.6 * mm});
            skCircle(sketch, "E5.7.36.2", {"center": v(-659.98, 191.01) * mm, "radius": 1.6 * mm});
            skCircle(sketch, "E5.7.36.3", {"center": v(-654.98, 191.01) * mm, "radius": 1.6 * mm});
            skCircle(sketch, "E5.7.37.0", {"center": v(-662.48, 186.01) * mm, "radius": 1.6 * mm});
            skCircle(sketch, "E5.7.37.1", {"center": v(-657.48, 186.01) * mm, "radius": 1.6 * mm});
            skCircle(sketch, "E5.7.37.2", {"center": v(-659.98, 181.01) * mm, "radius": 1.6 * mm});
            skCircle(sketch, "E5.7.37.3", {"center": v(-654.98, 181.01) * mm, "radius": 1.6 * mm});
            skCircle(sketch, "E5.7.38.0", {"center": v(-662.48, 176.01) * mm, "radius": 1.6 * mm});
            skCircle(sketch, "E5.7.38.1", {"center": v(-657.48, 176.01) * mm, "radius": 1.6 * mm});
            skCircle(sketch, "E5.7.38.2", {"center": v(-659.98, 171.01) * mm, "radius": 1.6 * mm});
            skCircle(sketch, "E5.7.38.3", {"center": v(-654.98, 171.01) * mm, "radius": 1.6 * mm});
            skCircle(sketch, "E5.7.39.0", {"center": v(-662.48, 166.01) * mm, "radius": 1.6 * mm});
            skCircle(sketch, "E5.7.39.1", {"center": v(-657.48, 166.01) * mm, "radius": 1.6 * mm});
            skCircle(sketch, "E5.7.39.2", {"center": v(-659.98, 161.01) * mm, "radius": 1.6 * mm});
            skCircle(sketch, "E5.7.39.3", {"center": v(-654.98, 161.01) * mm, "radius": 1.6 * mm});
            skCircle(sketch, "E5.7.40.0", {"center": v(-662.48, 156.01) * mm, "radius": 1.6 * mm});
            skCircle(sketch, "E5.7.40.1", {"center": v(-657.48, 156.01) * mm, "radius": 1.6 * mm});
            skCircle(sketch, "E5.7.40.2", {"center": v(-659.98, 151.01) * mm, "radius": 1.6 * mm});
            skCircle(sketch, "E5.7.40.3", {"center": v(-654.98, 151.01) * mm, "radius": 1.6 * mm});
            skCircle(sketch, "E5.7.41.0", {"center": v(-662.48, 146.01) * mm, "radius": 1.6 * mm});
            skCircle(sketch, "E5.7.41.1", {"center": v(-657.48, 146.01) * mm, "radius": 1.6 * mm});
            skCircle(sketch, "E5.7.41.2", {"center": v(-659.98, 141.01) * mm, "radius": 1.6 * mm});
            skCircle(sketch, "E5.7.41.3", {"center": v(-654.98, 141.01) * mm, "radius": 1.6 * mm});
            skCircle(sketch, "E5.7.42.0", {"center": v(-662.48, 136.01) * mm, "radius": 1.6 * mm});
            skCircle(sketch, "E5.7.42.1", {"center": v(-657.48, 136.01) * mm, "radius": 1.6 * mm});
            skCircle(sketch, "E5.7.42.2", {"center": v(-659.98, 131.01) * mm, "radius": 1.6 * mm});
            skCircle(sketch, "E5.7.42.3", {"center": v(-654.98, 131.01) * mm, "radius": 1.6 * mm});
            skCircle(sketch, "E5.7.43.0", {"center": v(-662.48, 126.01) * mm, "radius": 1.6 * mm});
            skCircle(sketch, "E5.7.43.1", {"center": v(-657.48, 126.01) * mm, "radius": 1.6 * mm});
            skCircle(sketch, "E5.7.43.2", {"center": v(-659.98, 121.01) * mm, "radius": 1.6 * mm});
            skCircle(sketch, "E5.7.43.3", {"center": v(-654.98, 121.01) * mm, "radius": 1.6 * mm});
            skCircle(sketch, "E5.7.44.0", {"center": v(-662.48, 116.01) * mm, "radius": 1.6 * mm});
            skCircle(sketch, "E5.7.44.1", {"center": v(-657.48, 116.01) * mm, "radius": 1.6 * mm});
            skCircle(sketch, "E5.7.44.2", {"center": v(-659.98, 111.01) * mm, "radius": 1.6 * mm});
            skCircle(sketch, "E5.7.44.3", {"center": v(-654.98, 111.01) * mm, "radius": 1.6 * mm});
            skCircle(sketch, "E5.7.45.0", {"center": v(-662.48, 106.01) * mm, "radius": 1.6 * mm});
            skCircle(sketch, "E5.7.45.1", {"center": v(-657.48, 106.01) * mm, "radius": 1.6 * mm});
            skCircle(sketch, "E5.7.45.2", {"center": v(-659.98, 101.01) * mm, "radius": 1.6 * mm});
            skCircle(sketch, "E5.7.45.3", {"center": v(-654.98, 101.01) * mm, "radius": 1.6 * mm});
            skCircle(sketch, "E5.7.46.0", {"center": v(-662.48, 96.01) * mm, "radius": 1.6 * mm});
            skCircle(sketch, "E5.7.46.1", {"center": v(-657.48, 96.01) * mm, "radius": 1.6 * mm});
            skCircle(sketch, "E5.7.46.2", {"center": v(-659.98, 91.01) * mm, "radius": 1.6 * mm});
            skCircle(sketch, "E5.7.46.3", {"center": v(-654.98, 91.01) * mm, "radius": 1.6 * mm});
            skCircle(sketch, "E5.7.47.0", {"center": v(-662.48, 86.01) * mm, "radius": 1.6 * mm});
            skCircle(sketch, "E5.7.47.1", {"center": v(-657.48, 86.01) * mm, "radius": 1.6 * mm});
            skCircle(sketch, "E5.7.47.2", {"center": v(-659.98, 81.01) * mm, "radius": 1.6 * mm});
            skCircle(sketch, "E5.7.47.3", {"center": v(-654.98, 81.01) * mm, "radius": 1.6 * mm});
            skCircle(sketch, "E5.7.48.0", {"center": v(-662.48, 76.01) * mm, "radius": 1.6 * mm});
            skCircle(sketch, "E5.7.48.1", {"center": v(-657.48, 76.01) * mm, "radius": 1.6 * mm});
            skCircle(sketch, "E5.7.48.2", {"center": v(-659.98, 71.01) * mm, "radius": 1.6 * mm});
            skCircle(sketch, "E5.7.48.3", {"center": v(-654.98, 71.01) * mm, "radius": 1.6 * mm});
            skCircle(sketch, "E5.7.49.0", {"center": v(-662.48, 66.01) * mm, "radius": 1.6 * mm});
            skCircle(sketch, "E5.7.49.1", {"center": v(-657.48, 66.01) * mm, "radius": 1.6 * mm});
            skCircle(sketch, "E5.7.49.2", {"center": v(-659.98, 61.01) * mm, "radius": 1.6 * mm});
            skCircle(sketch, "E5.7.49.3", {"center": v(-654.98, 61.01) * mm, "radius": 1.6 * mm});
            skCircle(sketch, "E5.8.0.0", {"center": v(-652.48, 556.01) * mm, "radius": 1.6 * mm});
            skCircle(sketch, "E5.8.0.1", {"center": v(-647.48, 556.01) * mm, "radius": 1.6 * mm});
            skCircle(sketch, "E5.8.0.2", {"center": v(-649.98, 551.01) * mm, "radius": 1.6 * mm});
            skCircle(sketch, "E5.8.0.3", {"center": v(-644.98, 551.01) * mm, "radius": 1.6 * mm});
            skCircle(sketch, "E5.8.1.0", {"center": v(-652.48, 546.01) * mm, "radius": 1.6 * mm});
            skCircle(sketch, "E5.8.1.1", {"center": v(-647.48, 546.01) * mm, "radius": 1.6 * mm});
            skCircle(sketch, "E5.8.1.2", {"center": v(-649.98, 541.01) * mm, "radius": 1.6 * mm});
            skCircle(sketch, "E5.8.1.3", {"center": v(-644.98, 541.01) * mm, "radius": 1.6 * mm});
            skCircle(sketch, "E5.8.2.0", {"center": v(-652.48, 536.01) * mm, "radius": 1.6 * mm});
            skCircle(sketch, "E5.8.2.1", {"center": v(-647.48, 536.01) * mm, "radius": 1.6 * mm});
            skCircle(sketch, "E5.8.2.2", {"center": v(-649.98, 531.01) * mm, "radius": 1.6 * mm});
            skCircle(sketch, "E5.8.2.3", {"center": v(-644.98, 531.01) * mm, "radius": 1.6 * mm});
            skCircle(sketch, "E5.8.3.0", {"center": v(-652.48, 526.01) * mm, "radius": 1.6 * mm});
            skCircle(sketch, "E5.8.3.1", {"center": v(-647.48, 526.01) * mm, "radius": 1.6 * mm});
            skCircle(sketch, "E5.8.3.2", {"center": v(-649.98, 521.01) * mm, "radius": 1.6 * mm});
            skCircle(sketch, "E5.8.3.3", {"center": v(-644.98, 521.01) * mm, "radius": 1.6 * mm});
            skCircle(sketch, "E5.8.4.0", {"center": v(-652.48, 516.01) * mm, "radius": 1.6 * mm});
            skCircle(sketch, "E5.8.4.1", {"center": v(-647.48, 516.01) * mm, "radius": 1.6 * mm});
            skCircle(sketch, "E5.8.4.2", {"center": v(-649.98, 511.01) * mm, "radius": 1.6 * mm});
            skCircle(sketch, "E5.8.4.3", {"center": v(-644.98, 511.01) * mm, "radius": 1.6 * mm});
            skCircle(sketch, "E5.8.5.0", {"center": v(-652.48, 506.01) * mm, "radius": 1.6 * mm});
            skCircle(sketch, "E5.8.5.1", {"center": v(-647.48, 506.01) * mm, "radius": 1.6 * mm});
            skCircle(sketch, "E5.8.5.2", {"center": v(-649.98, 501.01) * mm, "radius": 1.6 * mm});
            skCircle(sketch, "E5.8.5.3", {"center": v(-644.98, 501.01) * mm, "radius": 1.6 * mm});
            skCircle(sketch, "E5.8.6.0", {"center": v(-652.48, 496.01) * mm, "radius": 1.6 * mm});
            skCircle(sketch, "E5.8.6.1", {"center": v(-647.48, 496.01) * mm, "radius": 1.6 * mm});
            skCircle(sketch, "E5.8.6.2", {"center": v(-649.98, 491.01) * mm, "radius": 1.6 * mm});
            skCircle(sketch, "E5.8.6.3", {"center": v(-644.98, 491.01) * mm, "radius": 1.6 * mm});
            skCircle(sketch, "E5.8.7.0", {"center": v(-652.48, 486.01) * mm, "radius": 1.6 * mm});
            skCircle(sketch, "E5.8.7.1", {"center": v(-647.48, 486.01) * mm, "radius": 1.6 * mm});
            skCircle(sketch, "E5.8.7.2", {"center": v(-649.98, 481.01) * mm, "radius": 1.6 * mm});
            skCircle(sketch, "E5.8.7.3", {"center": v(-644.98, 481.01) * mm, "radius": 1.6 * mm});
            skCircle(sketch, "E5.8.8.0", {"center": v(-652.48, 476.01) * mm, "radius": 1.6 * mm});
            skCircle(sketch, "E5.8.8.1", {"center": v(-647.48, 476.01) * mm, "radius": 1.6 * mm});
            skCircle(sketch, "E5.8.8.2", {"center": v(-649.98, 471.01) * mm, "radius": 1.6 * mm});
            skCircle(sketch, "E5.8.8.3", {"center": v(-644.98, 471.01) * mm, "radius": 1.6 * mm});
            skCircle(sketch, "E5.8.9.0", {"center": v(-652.48, 466.01) * mm, "radius": 1.6 * mm});
            skCircle(sketch, "E5.8.9.1", {"center": v(-647.48, 466.01) * mm, "radius": 1.6 * mm});
            skCircle(sketch, "E5.8.9.2", {"center": v(-649.98, 461.01) * mm, "radius": 1.6 * mm});
            skCircle(sketch, "E5.8.9.3", {"center": v(-644.98, 461.01) * mm, "radius": 1.6 * mm});
            skCircle(sketch, "E5.8.10.0", {"center": v(-652.48, 456.01) * mm, "radius": 1.6 * mm});
            skCircle(sketch, "E5.8.10.1", {"center": v(-647.48, 456.01) * mm, "radius": 1.6 * mm});
            skCircle(sketch, "E5.8.10.2", {"center": v(-649.98, 451.01) * mm, "radius": 1.6 * mm});
            skCircle(sketch, "E5.8.10.3", {"center": v(-644.98, 451.01) * mm, "radius": 1.6 * mm});
            skCircle(sketch, "E5.8.11.0", {"center": v(-652.48, 446.01) * mm, "radius": 1.6 * mm});
            skCircle(sketch, "E5.8.11.1", {"center": v(-647.48, 446.01) * mm, "radius": 1.6 * mm});
            skCircle(sketch, "E5.8.11.2", {"center": v(-649.98, 441.01) * mm, "radius": 1.6 * mm});
            skCircle(sketch, "E5.8.11.3", {"center": v(-644.98, 441.01) * mm, "radius": 1.6 * mm});
            skCircle(sketch, "E5.8.12.0", {"center": v(-652.48, 436.01) * mm, "radius": 1.6 * mm});
            skCircle(sketch, "E5.8.12.1", {"center": v(-647.48, 436.01) * mm, "radius": 1.6 * mm});
            skCircle(sketch, "E5.8.12.2", {"center": v(-649.98, 431.01) * mm, "radius": 1.6 * mm});
            skCircle(sketch, "E5.8.12.3", {"center": v(-644.98, 431.01) * mm, "radius": 1.6 * mm});
            skCircle(sketch, "E5.8.13.0", {"center": v(-652.48, 426.01) * mm, "radius": 1.6 * mm});
            skCircle(sketch, "E5.8.13.1", {"center": v(-647.48, 426.01) * mm, "radius": 1.6 * mm});
            skCircle(sketch, "E5.8.13.2", {"center": v(-649.98, 421.01) * mm, "radius": 1.6 * mm});
            skCircle(sketch, "E5.8.13.3", {"center": v(-644.98, 421.01) * mm, "radius": 1.6 * mm});
            skCircle(sketch, "E5.8.14.0", {"center": v(-652.48, 416.01) * mm, "radius": 1.6 * mm});
            skCircle(sketch, "E5.8.14.1", {"center": v(-647.48, 416.01) * mm, "radius": 1.6 * mm});
            skCircle(sketch, "E5.8.14.2", {"center": v(-649.98, 411.01) * mm, "radius": 1.6 * mm});
            skCircle(sketch, "E5.8.14.3", {"center": v(-644.98, 411.01) * mm, "radius": 1.6 * mm});
            skCircle(sketch, "E5.8.15.0", {"center": v(-652.48, 406.01) * mm, "radius": 1.6 * mm});
            skCircle(sketch, "E5.8.15.1", {"center": v(-647.48, 406.01) * mm, "radius": 1.6 * mm});
            skCircle(sketch, "E5.8.15.2", {"center": v(-649.98, 401.01) * mm, "radius": 1.6 * mm});
            skCircle(sketch, "E5.8.15.3", {"center": v(-644.98, 401.01) * mm, "radius": 1.6 * mm});
            skCircle(sketch, "E5.8.16.0", {"center": v(-652.48, 396.01) * mm, "radius": 1.6 * mm});
            skCircle(sketch, "E5.8.16.1", {"center": v(-647.48, 396.01) * mm, "radius": 1.6 * mm});
            skCircle(sketch, "E5.8.16.2", {"center": v(-649.98, 391.01) * mm, "radius": 1.6 * mm});
            skCircle(sketch, "E5.8.16.3", {"center": v(-644.98, 391.01) * mm, "radius": 1.6 * mm});
            skCircle(sketch, "E5.8.17.0", {"center": v(-652.48, 386.01) * mm, "radius": 1.6 * mm});
            skCircle(sketch, "E5.8.17.1", {"center": v(-647.48, 386.01) * mm, "radius": 1.6 * mm});
            skCircle(sketch, "E5.8.17.2", {"center": v(-649.98, 381.01) * mm, "radius": 1.6 * mm});
            skCircle(sketch, "E5.8.17.3", {"center": v(-644.98, 381.01) * mm, "radius": 1.6 * mm});
            skCircle(sketch, "E5.8.18.0", {"center": v(-652.48, 376.01) * mm, "radius": 1.6 * mm});
            skCircle(sketch, "E5.8.18.1", {"center": v(-647.48, 376.01) * mm, "radius": 1.6 * mm});
            skCircle(sketch, "E5.8.18.2", {"center": v(-649.98, 371.01) * mm, "radius": 1.6 * mm});
            skCircle(sketch, "E5.8.18.3", {"center": v(-644.98, 371.01) * mm, "radius": 1.6 * mm});
            skCircle(sketch, "E5.8.19.0", {"center": v(-652.48, 366.01) * mm, "radius": 1.6 * mm});
            skCircle(sketch, "E5.8.19.1", {"center": v(-647.48, 366.01) * mm, "radius": 1.6 * mm});
            skCircle(sketch, "E5.8.19.2", {"center": v(-649.98, 361.01) * mm, "radius": 1.6 * mm});
            skCircle(sketch, "E5.8.19.3", {"center": v(-644.98, 361.01) * mm, "radius": 1.6 * mm});
            skCircle(sketch, "E5.8.20.0", {"center": v(-652.48, 356.01) * mm, "radius": 1.6 * mm});
            skCircle(sketch, "E5.8.20.1", {"center": v(-647.48, 356.01) * mm, "radius": 1.6 * mm});
            skCircle(sketch, "E5.8.20.2", {"center": v(-649.98, 351.01) * mm, "radius": 1.6 * mm});
            skCircle(sketch, "E5.8.20.3", {"center": v(-644.98, 351.01) * mm, "radius": 1.6 * mm});
            skCircle(sketch, "E5.8.21.0", {"center": v(-652.48, 346.01) * mm, "radius": 1.6 * mm});
            skCircle(sketch, "E5.8.21.1", {"center": v(-647.48, 346.01) * mm, "radius": 1.6 * mm});
            skCircle(sketch, "E5.8.21.2", {"center": v(-649.98, 341.01) * mm, "radius": 1.6 * mm});
            skCircle(sketch, "E5.8.21.3", {"center": v(-644.98, 341.01) * mm, "radius": 1.6 * mm});
            skCircle(sketch, "E5.8.22.0", {"center": v(-652.48, 336.01) * mm, "radius": 1.6 * mm});
            skCircle(sketch, "E5.8.22.1", {"center": v(-647.48, 336.01) * mm, "radius": 1.6 * mm});
            skCircle(sketch, "E5.8.22.2", {"center": v(-649.98, 331.01) * mm, "radius": 1.6 * mm});
            skCircle(sketch, "E5.8.22.3", {"center": v(-644.98, 331.01) * mm, "radius": 1.6 * mm});
            skCircle(sketch, "E5.8.23.0", {"center": v(-652.48, 326.01) * mm, "radius": 1.6 * mm});
            skCircle(sketch, "E5.8.23.1", {"center": v(-647.48, 326.01) * mm, "radius": 1.6 * mm});
            skCircle(sketch, "E5.8.23.2", {"center": v(-649.98, 321.01) * mm, "radius": 1.6 * mm});
            skCircle(sketch, "E5.8.23.3", {"center": v(-644.98, 321.01) * mm, "radius": 1.6 * mm});
            skCircle(sketch, "E5.8.24.0", {"center": v(-652.48, 316.01) * mm, "radius": 1.6 * mm});
            skCircle(sketch, "E5.8.24.1", {"center": v(-647.48, 316.01) * mm, "radius": 1.6 * mm});
            skCircle(sketch, "E5.8.24.2", {"center": v(-649.98, 311.01) * mm, "radius": 1.6 * mm});
            skCircle(sketch, "E5.8.24.3", {"center": v(-644.98, 311.01) * mm, "radius": 1.6 * mm});
            skCircle(sketch, "E5.8.25.0", {"center": v(-652.48, 306.01) * mm, "radius": 1.6 * mm});
            skCircle(sketch, "E5.8.25.1", {"center": v(-647.48, 306.01) * mm, "radius": 1.6 * mm});
            skCircle(sketch, "E5.8.25.2", {"center": v(-649.98, 301.01) * mm, "radius": 1.6 * mm});
            skCircle(sketch, "E5.8.25.3", {"center": v(-644.98, 301.01) * mm, "radius": 1.6 * mm});
            skCircle(sketch, "E5.8.26.0", {"center": v(-652.48, 296.01) * mm, "radius": 1.6 * mm});
            skCircle(sketch, "E5.8.26.1", {"center": v(-647.48, 296.01) * mm, "radius": 1.6 * mm});
            skCircle(sketch, "E5.8.26.2", {"center": v(-649.98, 291.01) * mm, "radius": 1.6 * mm});
            skCircle(sketch, "E5.8.26.3", {"center": v(-644.98, 291.01) * mm, "radius": 1.6 * mm});
            skCircle(sketch, "E5.8.27.0", {"center": v(-652.48, 286.01) * mm, "radius": 1.6 * mm});
            skCircle(sketch, "E5.8.27.1", {"center": v(-647.48, 286.01) * mm, "radius": 1.6 * mm});
            skCircle(sketch, "E5.8.27.2", {"center": v(-649.98, 281.01) * mm, "radius": 1.6 * mm});
            skCircle(sketch, "E5.8.27.3", {"center": v(-644.98, 281.01) * mm, "radius": 1.6 * mm});
            skCircle(sketch, "E5.8.28.0", {"center": v(-652.48, 276.01) * mm, "radius": 1.6 * mm});
            skCircle(sketch, "E5.8.28.1", {"center": v(-647.48, 276.01) * mm, "radius": 1.6 * mm});
            skCircle(sketch, "E5.8.28.2", {"center": v(-649.98, 271.01) * mm, "radius": 1.6 * mm});
            skCircle(sketch, "E5.8.28.3", {"center": v(-644.98, 271.01) * mm, "radius": 1.6 * mm});
            skCircle(sketch, "E5.8.29.0", {"center": v(-652.48, 266.01) * mm, "radius": 1.6 * mm});
            skCircle(sketch, "E5.8.29.1", {"center": v(-647.48, 266.01) * mm, "radius": 1.6 * mm});
            skCircle(sketch, "E5.8.29.2", {"center": v(-649.98, 261.01) * mm, "radius": 1.6 * mm});
            skCircle(sketch, "E5.8.29.3", {"center": v(-644.98, 261.01) * mm, "radius": 1.6 * mm});
            skCircle(sketch, "E5.8.30.0", {"center": v(-652.48, 256.01) * mm, "radius": 1.6 * mm});
            skCircle(sketch, "E5.8.30.1", {"center": v(-647.48, 256.01) * mm, "radius": 1.6 * mm});
            skCircle(sketch, "E5.8.30.2", {"center": v(-649.98, 251.01) * mm, "radius": 1.6 * mm});
            skCircle(sketch, "E5.8.30.3", {"center": v(-644.98, 251.01) * mm, "radius": 1.6 * mm});
            skCircle(sketch, "E5.8.31.0", {"center": v(-652.48, 246.01) * mm, "radius": 1.6 * mm});
            skCircle(sketch, "E5.8.31.1", {"center": v(-647.48, 246.01) * mm, "radius": 1.6 * mm});
            skCircle(sketch, "E5.8.31.2", {"center": v(-649.98, 241.01) * mm, "radius": 1.6 * mm});
            skCircle(sketch, "E5.8.31.3", {"center": v(-644.98, 241.01) * mm, "radius": 1.6 * mm});
            skCircle(sketch, "E5.8.32.0", {"center": v(-652.48, 236.01) * mm, "radius": 1.6 * mm});
            skCircle(sketch, "E5.8.32.1", {"center": v(-647.48, 236.01) * mm, "radius": 1.6 * mm});
            skCircle(sketch, "E5.8.32.2", {"center": v(-649.98, 231.01) * mm, "radius": 1.6 * mm});
            skCircle(sketch, "E5.8.32.3", {"center": v(-644.98, 231.01) * mm, "radius": 1.6 * mm});
            skCircle(sketch, "E5.8.33.0", {"center": v(-652.48, 226.01) * mm, "radius": 1.6 * mm});
            skCircle(sketch, "E5.8.33.1", {"center": v(-647.48, 226.01) * mm, "radius": 1.6 * mm});
            skCircle(sketch, "E5.8.33.2", {"center": v(-649.98, 221.01) * mm, "radius": 1.6 * mm});
            skCircle(sketch, "E5.8.33.3", {"center": v(-644.98, 221.01) * mm, "radius": 1.6 * mm});
            skCircle(sketch, "E5.8.34.0", {"center": v(-652.48, 216.01) * mm, "radius": 1.6 * mm});
            skCircle(sketch, "E5.8.34.1", {"center": v(-647.48, 216.01) * mm, "radius": 1.6 * mm});
            skCircle(sketch, "E5.8.34.2", {"center": v(-649.98, 211.01) * mm, "radius": 1.6 * mm});
            skCircle(sketch, "E5.8.34.3", {"center": v(-644.98, 211.01) * mm, "radius": 1.6 * mm});
            skCircle(sketch, "E5.8.35.0", {"center": v(-652.48, 206.01) * mm, "radius": 1.6 * mm});
            skCircle(sketch, "E5.8.35.1", {"center": v(-647.48, 206.01) * mm, "radius": 1.6 * mm});
            skCircle(sketch, "E5.8.35.2", {"center": v(-649.98, 201.01) * mm, "radius": 1.6 * mm});
            skCircle(sketch, "E5.8.35.3", {"center": v(-644.98, 201.01) * mm, "radius": 1.6 * mm});
            skCircle(sketch, "E5.8.36.0", {"center": v(-652.48, 196.01) * mm, "radius": 1.6 * mm});
            skCircle(sketch, "E5.8.36.1", {"center": v(-647.48, 196.01) * mm, "radius": 1.6 * mm});
            skCircle(sketch, "E5.8.36.2", {"center": v(-649.98, 191.01) * mm, "radius": 1.6 * mm});
            skCircle(sketch, "E5.8.36.3", {"center": v(-644.98, 191.01) * mm, "radius": 1.6 * mm});
            skCircle(sketch, "E5.8.37.0", {"center": v(-652.48, 186.01) * mm, "radius": 1.6 * mm});
            skCircle(sketch, "E5.8.37.1", {"center": v(-647.48, 186.01) * mm, "radius": 1.6 * mm});
            skCircle(sketch, "E5.8.37.2", {"center": v(-649.98, 181.01) * mm, "radius": 1.6 * mm});
            skCircle(sketch, "E5.8.37.3", {"center": v(-644.98, 181.01) * mm, "radius": 1.6 * mm});
            skCircle(sketch, "E5.8.38.0", {"center": v(-652.48, 176.01) * mm, "radius": 1.6 * mm});
            skCircle(sketch, "E5.8.38.1", {"center": v(-647.48, 176.01) * mm, "radius": 1.6 * mm});
            skCircle(sketch, "E5.8.38.2", {"center": v(-649.98, 171.01) * mm, "radius": 1.6 * mm});
            skCircle(sketch, "E5.8.38.3", {"center": v(-644.98, 171.01) * mm, "radius": 1.6 * mm});
            skCircle(sketch, "E5.8.39.0", {"center": v(-652.48, 166.01) * mm, "radius": 1.6 * mm});
            skCircle(sketch, "E5.8.39.1", {"center": v(-647.48, 166.01) * mm, "radius": 1.6 * mm});
            skCircle(sketch, "E5.8.39.2", {"center": v(-649.98, 161.01) * mm, "radius": 1.6 * mm});
            skCircle(sketch, "E5.8.39.3", {"center": v(-644.98, 161.01) * mm, "radius": 1.6 * mm});
            skCircle(sketch, "E5.8.40.0", {"center": v(-652.48, 156.01) * mm, "radius": 1.6 * mm});
            skCircle(sketch, "E5.8.40.1", {"center": v(-647.48, 156.01) * mm, "radius": 1.6 * mm});
            skCircle(sketch, "E5.8.40.2", {"center": v(-649.98, 151.01) * mm, "radius": 1.6 * mm});
            skCircle(sketch, "E5.8.40.3", {"center": v(-644.98, 151.01) * mm, "radius": 1.6 * mm});
            skCircle(sketch, "E5.8.41.0", {"center": v(-652.48, 146.01) * mm, "radius": 1.6 * mm});
            skCircle(sketch, "E5.8.41.1", {"center": v(-647.48, 146.01) * mm, "radius": 1.6 * mm});
            skCircle(sketch, "E5.8.41.2", {"center": v(-649.98, 141.01) * mm, "radius": 1.6 * mm});
            skCircle(sketch, "E5.8.41.3", {"center": v(-644.98, 141.01) * mm, "radius": 1.6 * mm});
            skCircle(sketch, "E5.8.42.0", {"center": v(-652.48, 136.01) * mm, "radius": 1.6 * mm});
            skCircle(sketch, "E5.8.42.1", {"center": v(-647.48, 136.01) * mm, "radius": 1.6 * mm});
            skCircle(sketch, "E5.8.42.2", {"center": v(-649.98, 131.01) * mm, "radius": 1.6 * mm});
            skCircle(sketch, "E5.8.42.3", {"center": v(-644.98, 131.01) * mm, "radius": 1.6 * mm});
            skCircle(sketch, "E5.8.43.0", {"center": v(-652.48, 126.01) * mm, "radius": 1.6 * mm});
            skCircle(sketch, "E5.8.43.1", {"center": v(-647.48, 126.01) * mm, "radius": 1.6 * mm});
            skCircle(sketch, "E5.8.43.2", {"center": v(-649.98, 121.01) * mm, "radius": 1.6 * mm});
            skCircle(sketch, "E5.8.43.3", {"center": v(-644.98, 121.01) * mm, "radius": 1.6 * mm});
            skCircle(sketch, "E5.8.44.0", {"center": v(-652.48, 116.01) * mm, "radius": 1.6 * mm});
            skCircle(sketch, "E5.8.44.1", {"center": v(-647.48, 116.01) * mm, "radius": 1.6 * mm});
            skCircle(sketch, "E5.8.44.2", {"center": v(-649.98, 111.01) * mm, "radius": 1.6 * mm});
            skCircle(sketch, "E5.8.44.3", {"center": v(-644.98, 111.01) * mm, "radius": 1.6 * mm});
            skCircle(sketch, "E5.8.45.0", {"center": v(-652.48, 106.01) * mm, "radius": 1.6 * mm});
            skCircle(sketch, "E5.8.45.1", {"center": v(-647.48, 106.01) * mm, "radius": 1.6 * mm});
            skCircle(sketch, "E5.8.45.2", {"center": v(-649.98, 101.01) * mm, "radius": 1.6 * mm});
            skCircle(sketch, "E5.8.45.3", {"center": v(-644.98, 101.01) * mm, "radius": 1.6 * mm});
            skCircle(sketch, "E5.8.46.0", {"center": v(-652.48, 96.01) * mm, "radius": 1.6 * mm});
            skCircle(sketch, "E5.8.46.1", {"center": v(-647.48, 96.01) * mm, "radius": 1.6 * mm});
            skCircle(sketch, "E5.8.46.2", {"center": v(-649.98, 91.01) * mm, "radius": 1.6 * mm});
            skCircle(sketch, "E5.8.46.3", {"center": v(-644.98, 91.01) * mm, "radius": 1.6 * mm});
            skCircle(sketch, "E5.8.47.0", {"center": v(-652.48, 86.01) * mm, "radius": 1.6 * mm});
            skCircle(sketch, "E5.8.47.1", {"center": v(-647.48, 86.01) * mm, "radius": 1.6 * mm});
            skCircle(sketch, "E5.8.47.2", {"center": v(-649.98, 81.01) * mm, "radius": 1.6 * mm});
            skCircle(sketch, "E5.8.47.3", {"center": v(-644.98, 81.01) * mm, "radius": 1.6 * mm});
            skCircle(sketch, "E5.8.48.0", {"center": v(-652.48, 76.01) * mm, "radius": 1.6 * mm});
            skCircle(sketch, "E5.8.48.1", {"center": v(-647.48, 76.01) * mm, "radius": 1.6 * mm});
            skCircle(sketch, "E5.8.48.2", {"center": v(-649.98, 71.01) * mm, "radius": 1.6 * mm});
            skCircle(sketch, "E5.8.48.3", {"center": v(-644.98, 71.01) * mm, "radius": 1.6 * mm});
            skCircle(sketch, "E5.8.49.0", {"center": v(-652.48, 66.01) * mm, "radius": 1.6 * mm});
            skCircle(sketch, "E5.8.49.1", {"center": v(-647.48, 66.01) * mm, "radius": 1.6 * mm});
            skCircle(sketch, "E5.8.49.2", {"center": v(-649.98, 61.01) * mm, "radius": 1.6 * mm});
            skCircle(sketch, "E5.8.49.3", {"center": v(-644.98, 61.01) * mm, "radius": 1.6 * mm});
            skCircle(sketch, "E5.9.0.0", {"center": v(-642.48, 556.01) * mm, "radius": 1.6 * mm});
            skCircle(sketch, "E5.9.0.1", {"center": v(-637.48, 556.01) * mm, "radius": 1.6 * mm});
            skCircle(sketch, "E5.9.0.2", {"center": v(-639.98, 551.01) * mm, "radius": 1.6 * mm});
            skCircle(sketch, "E5.9.0.3", {"center": v(-634.98, 551.01) * mm, "radius": 1.6 * mm});
            skCircle(sketch, "E5.9.1.0", {"center": v(-642.48, 546.01) * mm, "radius": 1.6 * mm});
            skCircle(sketch, "E5.9.1.1", {"center": v(-637.48, 546.01) * mm, "radius": 1.6 * mm});
            skCircle(sketch, "E5.9.1.2", {"center": v(-639.98, 541.01) * mm, "radius": 1.6 * mm});
            skCircle(sketch, "E5.9.1.3", {"center": v(-634.98, 541.01) * mm, "radius": 1.6 * mm});
            skCircle(sketch, "E5.9.2.0", {"center": v(-642.48, 536.01) * mm, "radius": 1.6 * mm});
            skCircle(sketch, "E5.9.2.1", {"center": v(-637.48, 536.01) * mm, "radius": 1.6 * mm});
            skCircle(sketch, "E5.9.2.2", {"center": v(-639.98, 531.01) * mm, "radius": 1.6 * mm});
            skCircle(sketch, "E5.9.2.3", {"center": v(-634.98, 531.01) * mm, "radius": 1.6 * mm});
            skCircle(sketch, "E5.9.3.0", {"center": v(-642.48, 526.01) * mm, "radius": 1.6 * mm});
            skCircle(sketch, "E5.9.3.1", {"center": v(-637.48, 526.01) * mm, "radius": 1.6 * mm});
            skCircle(sketch, "E5.9.3.2", {"center": v(-639.98, 521.01) * mm, "radius": 1.6 * mm});
            skCircle(sketch, "E5.9.3.3", {"center": v(-634.98, 521.01) * mm, "radius": 1.6 * mm});
            skCircle(sketch, "E5.9.4.0", {"center": v(-642.48, 516.01) * mm, "radius": 1.6 * mm});
            skCircle(sketch, "E5.9.4.1", {"center": v(-637.48, 516.01) * mm, "radius": 1.6 * mm});
            skCircle(sketch, "E5.9.4.2", {"center": v(-639.98, 511.01) * mm, "radius": 1.6 * mm});
            skCircle(sketch, "E5.9.4.3", {"center": v(-634.98, 511.01) * mm, "radius": 1.6 * mm});
            skCircle(sketch, "E5.9.5.0", {"center": v(-642.48, 506.01) * mm, "radius": 1.6 * mm});
            skCircle(sketch, "E5.9.5.1", {"center": v(-637.48, 506.01) * mm, "radius": 1.6 * mm});
            skCircle(sketch, "E5.9.5.2", {"center": v(-639.98, 501.01) * mm, "radius": 1.6 * mm});
            skCircle(sketch, "E5.9.5.3", {"center": v(-634.98, 501.01) * mm, "radius": 1.6 * mm});
            skCircle(sketch, "E5.9.6.0", {"center": v(-642.48, 496.01) * mm, "radius": 1.6 * mm});
            skCircle(sketch, "E5.9.6.1", {"center": v(-637.48, 496.01) * mm, "radius": 1.6 * mm});
            skCircle(sketch, "E5.9.6.2", {"center": v(-639.98, 491.01) * mm, "radius": 1.6 * mm});
            skCircle(sketch, "E5.9.6.3", {"center": v(-634.98, 491.01) * mm, "radius": 1.6 * mm});
            skCircle(sketch, "E5.9.7.0", {"center": v(-642.48, 486.01) * mm, "radius": 1.6 * mm});
            skCircle(sketch, "E5.9.7.1", {"center": v(-637.48, 486.01) * mm, "radius": 1.6 * mm});
            skCircle(sketch, "E5.9.7.2", {"center": v(-639.98, 481.01) * mm, "radius": 1.6 * mm});
            skCircle(sketch, "E5.9.7.3", {"center": v(-634.98, 481.01) * mm, "radius": 1.6 * mm});
            skCircle(sketch, "E5.9.8.0", {"center": v(-642.48, 476.01) * mm, "radius": 1.6 * mm});
            skCircle(sketch, "E5.9.8.1", {"center": v(-637.48, 476.01) * mm, "radius": 1.6 * mm});
            skCircle(sketch, "E5.9.8.2", {"center": v(-639.98, 471.01) * mm, "radius": 1.6 * mm});
            skCircle(sketch, "E5.9.8.3", {"center": v(-634.98, 471.01) * mm, "radius": 1.6 * mm});
            skCircle(sketch, "E5.9.9.0", {"center": v(-642.48, 466.01) * mm, "radius": 1.6 * mm});
            skCircle(sketch, "E5.9.9.1", {"center": v(-637.48, 466.01) * mm, "radius": 1.6 * mm});
            skCircle(sketch, "E5.9.9.2", {"center": v(-639.98, 461.01) * mm, "radius": 1.6 * mm});
            skCircle(sketch, "E5.9.9.3", {"center": v(-634.98, 461.01) * mm, "radius": 1.6 * mm});
            skCircle(sketch, "E5.9.10.0", {"center": v(-642.48, 456.01) * mm, "radius": 1.6 * mm});
            skCircle(sketch, "E5.9.10.1", {"center": v(-637.48, 456.01) * mm, "radius": 1.6 * mm});
            skCircle(sketch, "E5.9.10.2", {"center": v(-639.98, 451.01) * mm, "radius": 1.6 * mm});
            skCircle(sketch, "E5.9.10.3", {"center": v(-634.98, 451.01) * mm, "radius": 1.6 * mm});
            skCircle(sketch, "E5.9.11.0", {"center": v(-642.48, 446.01) * mm, "radius": 1.6 * mm});
            skCircle(sketch, "E5.9.11.1", {"center": v(-637.48, 446.01) * mm, "radius": 1.6 * mm});
            skCircle(sketch, "E5.9.11.2", {"center": v(-639.98, 441.01) * mm, "radius": 1.6 * mm});
            skCircle(sketch, "E5.9.11.3", {"center": v(-634.98, 441.01) * mm, "radius": 1.6 * mm});
            skCircle(sketch, "E5.9.12.0", {"center": v(-642.48, 436.01) * mm, "radius": 1.6 * mm});
            skCircle(sketch, "E5.9.12.1", {"center": v(-637.48, 436.01) * mm, "radius": 1.6 * mm});
            skCircle(sketch, "E5.9.12.2", {"center": v(-639.98, 431.01) * mm, "radius": 1.6 * mm});
            skCircle(sketch, "E5.9.12.3", {"center": v(-634.98, 431.01) * mm, "radius": 1.6 * mm});
            skCircle(sketch, "E5.9.13.0", {"center": v(-642.48, 426.01) * mm, "radius": 1.6 * mm});
            skCircle(sketch, "E5.9.13.1", {"center": v(-637.48, 426.01) * mm, "radius": 1.6 * mm});
            skCircle(sketch, "E5.9.13.2", {"center": v(-639.98, 421.01) * mm, "radius": 1.6 * mm});
            skCircle(sketch, "E5.9.13.3", {"center": v(-634.98, 421.01) * mm, "radius": 1.6 * mm});
            skCircle(sketch, "E5.9.14.0", {"center": v(-642.48, 416.01) * mm, "radius": 1.6 * mm});
            skCircle(sketch, "E5.9.14.1", {"center": v(-637.48, 416.01) * mm, "radius": 1.6 * mm});
            skCircle(sketch, "E5.9.14.2", {"center": v(-639.98, 411.01) * mm, "radius": 1.6 * mm});
            skCircle(sketch, "E5.9.14.3", {"center": v(-634.98, 411.01) * mm, "radius": 1.6 * mm});
            skCircle(sketch, "E5.9.15.0", {"center": v(-642.48, 406.01) * mm, "radius": 1.6 * mm});
            skCircle(sketch, "E5.9.15.1", {"center": v(-637.48, 406.01) * mm, "radius": 1.6 * mm});
            skCircle(sketch, "E5.9.15.2", {"center": v(-639.98, 401.01) * mm, "radius": 1.6 * mm});
            skCircle(sketch, "E5.9.15.3", {"center": v(-634.98, 401.01) * mm, "radius": 1.6 * mm});
            skCircle(sketch, "E5.9.16.0", {"center": v(-642.48, 396.01) * mm, "radius": 1.6 * mm});
            skCircle(sketch, "E5.9.16.1", {"center": v(-637.48, 396.01) * mm, "radius": 1.6 * mm});
            skCircle(sketch, "E5.9.16.2", {"center": v(-639.98, 391.01) * mm, "radius": 1.6 * mm});
            skCircle(sketch, "E5.9.16.3", {"center": v(-634.98, 391.01) * mm, "radius": 1.6 * mm});
            skCircle(sketch, "E5.9.17.0", {"center": v(-642.48, 386.01) * mm, "radius": 1.6 * mm});
            skCircle(sketch, "E5.9.17.1", {"center": v(-637.48, 386.01) * mm, "radius": 1.6 * mm});
            skCircle(sketch, "E5.9.17.2", {"center": v(-639.98, 381.01) * mm, "radius": 1.6 * mm});
            skCircle(sketch, "E5.9.17.3", {"center": v(-634.98, 381.01) * mm, "radius": 1.6 * mm});
            skCircle(sketch, "E5.9.18.0", {"center": v(-642.48, 376.01) * mm, "radius": 1.6 * mm});
            skCircle(sketch, "E5.9.18.1", {"center": v(-637.48, 376.01) * mm, "radius": 1.6 * mm});
            skCircle(sketch, "E5.9.18.2", {"center": v(-639.98, 371.01) * mm, "radius": 1.6 * mm});
            skCircle(sketch, "E5.9.18.3", {"center": v(-634.98, 371.01) * mm, "radius": 1.6 * mm});
            skCircle(sketch, "E5.9.19.0", {"center": v(-642.48, 366.01) * mm, "radius": 1.6 * mm});
            skCircle(sketch, "E5.9.19.1", {"center": v(-637.48, 366.01) * mm, "radius": 1.6 * mm});
            skCircle(sketch, "E5.9.19.2", {"center": v(-639.98, 361.01) * mm, "radius": 1.6 * mm});
            skCircle(sketch, "E5.9.19.3", {"center": v(-634.98, 361.01) * mm, "radius": 1.6 * mm});
            skCircle(sketch, "E5.9.20.0", {"center": v(-642.48, 356.01) * mm, "radius": 1.6 * mm});
            skCircle(sketch, "E5.9.20.1", {"center": v(-637.48, 356.01) * mm, "radius": 1.6 * mm});
            skCircle(sketch, "E5.9.20.2", {"center": v(-639.98, 351.01) * mm, "radius": 1.6 * mm});
            skCircle(sketch, "E5.9.20.3", {"center": v(-634.98, 351.01) * mm, "radius": 1.6 * mm});
            skCircle(sketch, "E5.9.21.0", {"center": v(-642.48, 346.01) * mm, "radius": 1.6 * mm});
            skCircle(sketch, "E5.9.21.1", {"center": v(-637.48, 346.01) * mm, "radius": 1.6 * mm});
            skCircle(sketch, "E5.9.21.2", {"center": v(-639.98, 341.01) * mm, "radius": 1.6 * mm});
            skCircle(sketch, "E5.9.21.3", {"center": v(-634.98, 341.01) * mm, "radius": 1.6 * mm});
            skCircle(sketch, "E5.9.22.0", {"center": v(-642.48, 336.01) * mm, "radius": 1.6 * mm});
            skCircle(sketch, "E5.9.22.1", {"center": v(-637.48, 336.01) * mm, "radius": 1.6 * mm});
            skCircle(sketch, "E5.9.22.2", {"center": v(-639.98, 331.01) * mm, "radius": 1.6 * mm});
            skCircle(sketch, "E5.9.22.3", {"center": v(-634.98, 331.01) * mm, "radius": 1.6 * mm});
            skCircle(sketch, "E5.9.23.0", {"center": v(-642.48, 326.01) * mm, "radius": 1.6 * mm});
            skCircle(sketch, "E5.9.23.1", {"center": v(-637.48, 326.01) * mm, "radius": 1.6 * mm});
            skCircle(sketch, "E5.9.23.2", {"center": v(-639.98, 321.01) * mm, "radius": 1.6 * mm});
            skCircle(sketch, "E5.9.23.3", {"center": v(-634.98, 321.01) * mm, "radius": 1.6 * mm});
            skCircle(sketch, "E5.9.24.0", {"center": v(-642.48, 316.01) * mm, "radius": 1.6 * mm});
            skCircle(sketch, "E5.9.24.1", {"center": v(-637.48, 316.01) * mm, "radius": 1.6 * mm});
            skCircle(sketch, "E5.9.24.2", {"center": v(-639.98, 311.01) * mm, "radius": 1.6 * mm});
            skCircle(sketch, "E5.9.24.3", {"center": v(-634.98, 311.01) * mm, "radius": 1.6 * mm});
            skCircle(sketch, "E5.9.25.0", {"center": v(-642.48, 306.01) * mm, "radius": 1.6 * mm});
            skCircle(sketch, "E5.9.25.1", {"center": v(-637.48, 306.01) * mm, "radius": 1.6 * mm});
            skCircle(sketch, "E5.9.25.2", {"center": v(-639.98, 301.01) * mm, "radius": 1.6 * mm});
            skCircle(sketch, "E5.9.25.3", {"center": v(-634.98, 301.01) * mm, "radius": 1.6 * mm});
            skCircle(sketch, "E5.9.26.0", {"center": v(-642.48, 296.01) * mm, "radius": 1.6 * mm});
            skCircle(sketch, "E5.9.26.1", {"center": v(-637.48, 296.01) * mm, "radius": 1.6 * mm});
            skCircle(sketch, "E5.9.26.2", {"center": v(-639.98, 291.01) * mm, "radius": 1.6 * mm});
            skCircle(sketch, "E5.9.26.3", {"center": v(-634.98, 291.01) * mm, "radius": 1.6 * mm});
            skCircle(sketch, "E5.9.27.0", {"center": v(-642.48, 286.01) * mm, "radius": 1.6 * mm});
            skCircle(sketch, "E5.9.27.1", {"center": v(-637.48, 286.01) * mm, "radius": 1.6 * mm});
            skCircle(sketch, "E5.9.27.2", {"center": v(-639.98, 281.01) * mm, "radius": 1.6 * mm});
            skCircle(sketch, "E5.9.27.3", {"center": v(-634.98, 281.01) * mm, "radius": 1.6 * mm});
            skCircle(sketch, "E5.9.28.0", {"center": v(-642.48, 276.01) * mm, "radius": 1.6 * mm});
            skCircle(sketch, "E5.9.28.1", {"center": v(-637.48, 276.01) * mm, "radius": 1.6 * mm});
            skCircle(sketch, "E5.9.28.2", {"center": v(-639.98, 271.01) * mm, "radius": 1.6 * mm});
            skCircle(sketch, "E5.9.28.3", {"center": v(-634.98, 271.01) * mm, "radius": 1.6 * mm});
            skCircle(sketch, "E5.9.29.0", {"center": v(-642.48, 266.01) * mm, "radius": 1.6 * mm});
            skCircle(sketch, "E5.9.29.1", {"center": v(-637.48, 266.01) * mm, "radius": 1.6 * mm});
            skCircle(sketch, "E5.9.29.2", {"center": v(-639.98, 261.01) * mm, "radius": 1.6 * mm});
            skCircle(sketch, "E5.9.29.3", {"center": v(-634.98, 261.01) * mm, "radius": 1.6 * mm});
            skCircle(sketch, "E5.9.30.0", {"center": v(-642.48, 256.01) * mm, "radius": 1.6 * mm});
            skCircle(sketch, "E5.9.30.1", {"center": v(-637.48, 256.01) * mm, "radius": 1.6 * mm});
            skCircle(sketch, "E5.9.30.2", {"center": v(-639.98, 251.01) * mm, "radius": 1.6 * mm});
            skCircle(sketch, "E5.9.30.3", {"center": v(-634.98, 251.01) * mm, "radius": 1.6 * mm});
            skCircle(sketch, "E5.9.31.0", {"center": v(-642.48, 246.01) * mm, "radius": 1.6 * mm});
            skCircle(sketch, "E5.9.31.1", {"center": v(-637.48, 246.01) * mm, "radius": 1.6 * mm});
            skCircle(sketch, "E5.9.31.2", {"center": v(-639.98, 241.01) * mm, "radius": 1.6 * mm});
            skCircle(sketch, "E5.9.31.3", {"center": v(-634.98, 241.01) * mm, "radius": 1.6 * mm});
            skCircle(sketch, "E5.9.32.0", {"center": v(-642.48, 236.01) * mm, "radius": 1.6 * mm});
            skCircle(sketch, "E5.9.32.1", {"center": v(-637.48, 236.01) * mm, "radius": 1.6 * mm});
            skCircle(sketch, "E5.9.32.2", {"center": v(-639.98, 231.01) * mm, "radius": 1.6 * mm});
            skCircle(sketch, "E5.9.32.3", {"center": v(-634.98, 231.01) * mm, "radius": 1.6 * mm});
            skCircle(sketch, "E5.9.33.0", {"center": v(-642.48, 226.01) * mm, "radius": 1.6 * mm});
            skCircle(sketch, "E5.9.33.1", {"center": v(-637.48, 226.01) * mm, "radius": 1.6 * mm});
            skCircle(sketch, "E5.9.33.2", {"center": v(-639.98, 221.01) * mm, "radius": 1.6 * mm});
            skCircle(sketch, "E5.9.33.3", {"center": v(-634.98, 221.01) * mm, "radius": 1.6 * mm});
            skCircle(sketch, "E5.9.34.0", {"center": v(-642.48, 216.01) * mm, "radius": 1.6 * mm});
            skCircle(sketch, "E5.9.34.1", {"center": v(-637.48, 216.01) * mm, "radius": 1.6 * mm});
            skCircle(sketch, "E5.9.34.2", {"center": v(-639.98, 211.01) * mm, "radius": 1.6 * mm});
            skCircle(sketch, "E5.9.34.3", {"center": v(-634.98, 211.01) * mm, "radius": 1.6 * mm});
            skCircle(sketch, "E5.9.35.0", {"center": v(-642.48, 206.01) * mm, "radius": 1.6 * mm});
            skCircle(sketch, "E5.9.35.1", {"center": v(-637.48, 206.01) * mm, "radius": 1.6 * mm});
            skCircle(sketch, "E5.9.35.2", {"center": v(-639.98, 201.01) * mm, "radius": 1.6 * mm});
            skCircle(sketch, "E5.9.35.3", {"center": v(-634.98, 201.01) * mm, "radius": 1.6 * mm});
            skCircle(sketch, "E5.9.36.0", {"center": v(-642.48, 196.01) * mm, "radius": 1.6 * mm});
            skCircle(sketch, "E5.9.36.1", {"center": v(-637.48, 196.01) * mm, "radius": 1.6 * mm});
            skCircle(sketch, "E5.9.36.2", {"center": v(-639.98, 191.01) * mm, "radius": 1.6 * mm});
            skCircle(sketch, "E5.9.36.3", {"center": v(-634.98, 191.01) * mm, "radius": 1.6 * mm});
            skCircle(sketch, "E5.9.37.0", {"center": v(-642.48, 186.01) * mm, "radius": 1.6 * mm});
            skCircle(sketch, "E5.9.37.1", {"center": v(-637.48, 186.01) * mm, "radius": 1.6 * mm});
            skCircle(sketch, "E5.9.37.2", {"center": v(-639.98, 181.01) * mm, "radius": 1.6 * mm});
            skCircle(sketch, "E5.9.37.3", {"center": v(-634.98, 181.01) * mm, "radius": 1.6 * mm});
            skCircle(sketch, "E5.9.38.0", {"center": v(-642.48, 176.01) * mm, "radius": 1.6 * mm});
            skCircle(sketch, "E5.9.38.1", {"center": v(-637.48, 176.01) * mm, "radius": 1.6 * mm});
            skCircle(sketch, "E5.9.38.2", {"center": v(-639.98, 171.01) * mm, "radius": 1.6 * mm});
            skCircle(sketch, "E5.9.38.3", {"center": v(-634.98, 171.01) * mm, "radius": 1.6 * mm});
            skCircle(sketch, "E5.9.39.0", {"center": v(-642.48, 166.01) * mm, "radius": 1.6 * mm});
            skCircle(sketch, "E5.9.39.1", {"center": v(-637.48, 166.01) * mm, "radius": 1.6 * mm});
            skCircle(sketch, "E5.9.39.2", {"center": v(-639.98, 161.01) * mm, "radius": 1.6 * mm});
            skCircle(sketch, "E5.9.39.3", {"center": v(-634.98, 161.01) * mm, "radius": 1.6 * mm});
            skCircle(sketch, "E5.9.40.0", {"center": v(-642.48, 156.01) * mm, "radius": 1.6 * mm});
            skCircle(sketch, "E5.9.40.1", {"center": v(-637.48, 156.01) * mm, "radius": 1.6 * mm});
            skCircle(sketch, "E5.9.40.2", {"center": v(-639.98, 151.01) * mm, "radius": 1.6 * mm});
            skCircle(sketch, "E5.9.40.3", {"center": v(-634.98, 151.01) * mm, "radius": 1.6 * mm});
            skCircle(sketch, "E5.9.41.0", {"center": v(-642.48, 146.01) * mm, "radius": 1.6 * mm});
            skCircle(sketch, "E5.9.41.1", {"center": v(-637.48, 146.01) * mm, "radius": 1.6 * mm});
            skCircle(sketch, "E5.9.41.2", {"center": v(-639.98, 141.01) * mm, "radius": 1.6 * mm});
            skCircle(sketch, "E5.9.41.3", {"center": v(-634.98, 141.01) * mm, "radius": 1.6 * mm});
            skCircle(sketch, "E5.9.42.0", {"center": v(-642.48, 136.01) * mm, "radius": 1.6 * mm});
            skCircle(sketch, "E5.9.42.1", {"center": v(-637.48, 136.01) * mm, "radius": 1.6 * mm});
            skCircle(sketch, "E5.9.42.2", {"center": v(-639.98, 131.01) * mm, "radius": 1.6 * mm});
            skCircle(sketch, "E5.9.42.3", {"center": v(-634.98, 131.01) * mm, "radius": 1.6 * mm});
            skCircle(sketch, "E5.9.43.0", {"center": v(-642.48, 126.01) * mm, "radius": 1.6 * mm});
            skCircle(sketch, "E5.9.43.1", {"center": v(-637.48, 126.01) * mm, "radius": 1.6 * mm});
            skCircle(sketch, "E5.9.43.2", {"center": v(-639.98, 121.01) * mm, "radius": 1.6 * mm});
            skCircle(sketch, "E5.9.43.3", {"center": v(-634.98, 121.01) * mm, "radius": 1.6 * mm});
            skCircle(sketch, "E5.9.44.0", {"center": v(-642.48, 116.01) * mm, "radius": 1.6 * mm});
            skCircle(sketch, "E5.9.44.1", {"center": v(-637.48, 116.01) * mm, "radius": 1.6 * mm});
            skCircle(sketch, "E5.9.44.2", {"center": v(-639.98, 111.01) * mm, "radius": 1.6 * mm});
            skCircle(sketch, "E5.9.44.3", {"center": v(-634.98, 111.01) * mm, "radius": 1.6 * mm});
            skCircle(sketch, "E5.9.45.0", {"center": v(-642.48, 106.01) * mm, "radius": 1.6 * mm});
            skCircle(sketch, "E5.9.45.1", {"center": v(-637.48, 106.01) * mm, "radius": 1.6 * mm});
            skCircle(sketch, "E5.9.45.2", {"center": v(-639.98, 101.01) * mm, "radius": 1.6 * mm});
            skCircle(sketch, "E5.9.45.3", {"center": v(-634.98, 101.01) * mm, "radius": 1.6 * mm});
            skCircle(sketch, "E5.9.46.0", {"center": v(-642.48, 96.01) * mm, "radius": 1.6 * mm});
            skCircle(sketch, "E5.9.46.1", {"center": v(-637.48, 96.01) * mm, "radius": 1.6 * mm});
            skCircle(sketch, "E5.9.46.2", {"center": v(-639.98, 91.01) * mm, "radius": 1.6 * mm});
            skCircle(sketch, "E5.9.46.3", {"center": v(-634.98, 91.01) * mm, "radius": 1.6 * mm});
            skCircle(sketch, "E5.9.47.0", {"center": v(-642.48, 86.01) * mm, "radius": 1.6 * mm});
            skCircle(sketch, "E5.9.47.1", {"center": v(-637.48, 86.01) * mm, "radius": 1.6 * mm});
            skCircle(sketch, "E5.9.47.2", {"center": v(-639.98, 81.01) * mm, "radius": 1.6 * mm});
            skCircle(sketch, "E5.9.47.3", {"center": v(-634.98, 81.01) * mm, "radius": 1.6 * mm});
            skCircle(sketch, "E5.9.48.0", {"center": v(-642.48, 76.01) * mm, "radius": 1.6 * mm});
            skCircle(sketch, "E5.9.48.1", {"center": v(-637.48, 76.01) * mm, "radius": 1.6 * mm});
            skCircle(sketch, "E5.9.48.2", {"center": v(-639.98, 71.01) * mm, "radius": 1.6 * mm});
            skCircle(sketch, "E5.9.48.3", {"center": v(-634.98, 71.01) * mm, "radius": 1.6 * mm});
            skCircle(sketch, "E5.9.49.0", {"center": v(-642.48, 66.01) * mm, "radius": 1.6 * mm});
            skCircle(sketch, "E5.9.49.1", {"center": v(-637.48, 66.01) * mm, "radius": 1.6 * mm});
            skCircle(sketch, "E5.9.49.2", {"center": v(-639.98, 61.01) * mm, "radius": 1.6 * mm});
            skCircle(sketch, "E5.9.49.3", {"center": v(-634.98, 61.01) * mm, "radius": 1.6 * mm});
            skCircle(sketch, "E5.10.0.0", {"center": v(-632.48, 556.01) * mm, "radius": 1.6 * mm});
            skCircle(sketch, "E5.10.0.1", {"center": v(-627.48, 556.01) * mm, "radius": 1.6 * mm});
            skCircle(sketch, "E5.10.0.2", {"center": v(-629.98, 551.01) * mm, "radius": 1.6 * mm});
            skCircle(sketch, "E5.10.0.3", {"center": v(-624.98, 551.01) * mm, "radius": 1.6 * mm});
            skCircle(sketch, "E5.10.1.0", {"center": v(-632.48, 546.01) * mm, "radius": 1.6 * mm});
            skCircle(sketch, "E5.10.1.1", {"center": v(-627.48, 546.01) * mm, "radius": 1.6 * mm});
            skCircle(sketch, "E5.10.1.2", {"center": v(-629.98, 541.01) * mm, "radius": 1.6 * mm});
            skCircle(sketch, "E5.10.1.3", {"center": v(-624.98, 541.01) * mm, "radius": 1.6 * mm});
            skCircle(sketch, "E5.10.2.0", {"center": v(-632.48, 536.01) * mm, "radius": 1.6 * mm});
            skCircle(sketch, "E5.10.2.1", {"center": v(-627.48, 536.01) * mm, "radius": 1.6 * mm});
            skCircle(sketch, "E5.10.2.2", {"center": v(-629.98, 531.01) * mm, "radius": 1.6 * mm});
            skCircle(sketch, "E5.10.2.3", {"center": v(-624.98, 531.01) * mm, "radius": 1.6 * mm});
            skCircle(sketch, "E5.10.3.0", {"center": v(-632.48, 526.01) * mm, "radius": 1.6 * mm});
            skCircle(sketch, "E5.10.3.1", {"center": v(-627.48, 526.01) * mm, "radius": 1.6 * mm});
            skCircle(sketch, "E5.10.3.2", {"center": v(-629.98, 521.01) * mm, "radius": 1.6 * mm});
            skCircle(sketch, "E5.10.3.3", {"center": v(-624.98, 521.01) * mm, "radius": 1.6 * mm});
            skCircle(sketch, "E5.10.4.0", {"center": v(-632.48, 516.01) * mm, "radius": 1.6 * mm});
            skCircle(sketch, "E5.10.4.1", {"center": v(-627.48, 516.01) * mm, "radius": 1.6 * mm});
            skCircle(sketch, "E5.10.4.2", {"center": v(-629.98, 511.01) * mm, "radius": 1.6 * mm});
            skCircle(sketch, "E5.10.4.3", {"center": v(-624.98, 511.01) * mm, "radius": 1.6 * mm});
            skCircle(sketch, "E5.10.5.0", {"center": v(-632.48, 506.01) * mm, "radius": 1.6 * mm});
            skCircle(sketch, "E5.10.5.1", {"center": v(-627.48, 506.01) * mm, "radius": 1.6 * mm});
            skCircle(sketch, "E5.10.5.2", {"center": v(-629.98, 501.01) * mm, "radius": 1.6 * mm});
            skCircle(sketch, "E5.10.5.3", {"center": v(-624.98, 501.01) * mm, "radius": 1.6 * mm});
            skCircle(sketch, "E5.10.6.0", {"center": v(-632.48, 496.01) * mm, "radius": 1.6 * mm});
            skCircle(sketch, "E5.10.6.1", {"center": v(-627.48, 496.01) * mm, "radius": 1.6 * mm});
            skCircle(sketch, "E5.10.6.2", {"center": v(-629.98, 491.01) * mm, "radius": 1.6 * mm});
            skCircle(sketch, "E5.10.6.3", {"center": v(-624.98, 491.01) * mm, "radius": 1.6 * mm});
            skCircle(sketch, "E5.10.7.0", {"center": v(-632.48, 486.01) * mm, "radius": 1.6 * mm});
            skCircle(sketch, "E5.10.7.1", {"center": v(-627.48, 486.01) * mm, "radius": 1.6 * mm});
            skCircle(sketch, "E5.10.7.2", {"center": v(-629.98, 481.01) * mm, "radius": 1.6 * mm});
            skCircle(sketch, "E5.10.7.3", {"center": v(-624.98, 481.01) * mm, "radius": 1.6 * mm});
            skCircle(sketch, "E5.10.8.0", {"center": v(-632.48, 476.01) * mm, "radius": 1.6 * mm});
            skCircle(sketch, "E5.10.8.1", {"center": v(-627.48, 476.01) * mm, "radius": 1.6 * mm});
            skCircle(sketch, "E5.10.8.2", {"center": v(-629.98, 471.01) * mm, "radius": 1.6 * mm});
            skCircle(sketch, "E5.10.8.3", {"center": v(-624.98, 471.01) * mm, "radius": 1.6 * mm});
            skCircle(sketch, "E5.10.9.0", {"center": v(-632.48, 466.01) * mm, "radius": 1.6 * mm});
            skCircle(sketch, "E5.10.9.1", {"center": v(-627.48, 466.01) * mm, "radius": 1.6 * mm});
            skCircle(sketch, "E5.10.9.2", {"center": v(-629.98, 461.01) * mm, "radius": 1.6 * mm});
            skCircle(sketch, "E5.10.9.3", {"center": v(-624.98, 461.01) * mm, "radius": 1.6 * mm});
            skCircle(sketch, "E5.10.10.0", {"center": v(-632.48, 456.01) * mm, "radius": 1.6 * mm});
            skCircle(sketch, "E5.10.10.1", {"center": v(-627.48, 456.01) * mm, "radius": 1.6 * mm});
            skCircle(sketch, "E5.10.10.2", {"center": v(-629.98, 451.01) * mm, "radius": 1.6 * mm});
            skCircle(sketch, "E5.10.10.3", {"center": v(-624.98, 451.01) * mm, "radius": 1.6 * mm});
            skCircle(sketch, "E5.10.11.0", {"center": v(-632.48, 446.01) * mm, "radius": 1.6 * mm});
            skCircle(sketch, "E5.10.11.1", {"center": v(-627.48, 446.01) * mm, "radius": 1.6 * mm});
            skCircle(sketch, "E5.10.11.2", {"center": v(-629.98, 441.01) * mm, "radius": 1.6 * mm});
            skCircle(sketch, "E5.10.11.3", {"center": v(-624.98, 441.01) * mm, "radius": 1.6 * mm});
            skCircle(sketch, "E5.10.12.0", {"center": v(-632.48, 436.01) * mm, "radius": 1.6 * mm});
            skCircle(sketch, "E5.10.12.1", {"center": v(-627.48, 436.01) * mm, "radius": 1.6 * mm});
            skCircle(sketch, "E5.10.12.2", {"center": v(-629.98, 431.01) * mm, "radius": 1.6 * mm});
            skCircle(sketch, "E5.10.12.3", {"center": v(-624.98, 431.01) * mm, "radius": 1.6 * mm});
            skCircle(sketch, "E5.10.13.0", {"center": v(-632.48, 426.01) * mm, "radius": 1.6 * mm});
            skCircle(sketch, "E5.10.13.1", {"center": v(-627.48, 426.01) * mm, "radius": 1.6 * mm});
            skCircle(sketch, "E5.10.13.2", {"center": v(-629.98, 421.01) * mm, "radius": 1.6 * mm});
            skCircle(sketch, "E5.10.13.3", {"center": v(-624.98, 421.01) * mm, "radius": 1.6 * mm});
            skCircle(sketch, "E5.10.14.0", {"center": v(-632.48, 416.01) * mm, "radius": 1.6 * mm});
            skCircle(sketch, "E5.10.14.1", {"center": v(-627.48, 416.01) * mm, "radius": 1.6 * mm});
            skCircle(sketch, "E5.10.14.2", {"center": v(-629.98, 411.01) * mm, "radius": 1.6 * mm});
            skCircle(sketch, "E5.10.14.3", {"center": v(-624.98, 411.01) * mm, "radius": 1.6 * mm});
            skCircle(sketch, "E5.10.15.0", {"center": v(-632.48, 406.01) * mm, "radius": 1.6 * mm});
            skCircle(sketch, "E5.10.15.1", {"center": v(-627.48, 406.01) * mm, "radius": 1.6 * mm});
            skCircle(sketch, "E5.10.15.2", {"center": v(-629.98, 401.01) * mm, "radius": 1.6 * mm});
            skCircle(sketch, "E5.10.15.3", {"center": v(-624.98, 401.01) * mm, "radius": 1.6 * mm});
            skCircle(sketch, "E5.10.16.0", {"center": v(-632.48, 396.01) * mm, "radius": 1.6 * mm});
            skCircle(sketch, "E5.10.16.1", {"center": v(-627.48, 396.01) * mm, "radius": 1.6 * mm});
            skCircle(sketch, "E5.10.16.2", {"center": v(-629.98, 391.01) * mm, "radius": 1.6 * mm});
            skCircle(sketch, "E5.10.16.3", {"center": v(-624.98, 391.01) * mm, "radius": 1.6 * mm});
            skCircle(sketch, "E5.10.17.0", {"center": v(-632.48, 386.01) * mm, "radius": 1.6 * mm});
            skCircle(sketch, "E5.10.17.1", {"center": v(-627.48, 386.01) * mm, "radius": 1.6 * mm});
            skCircle(sketch, "E5.10.17.2", {"center": v(-629.98, 381.01) * mm, "radius": 1.6 * mm});
            skCircle(sketch, "E5.10.17.3", {"center": v(-624.98, 381.01) * mm, "radius": 1.6 * mm});
            skCircle(sketch, "E5.10.18.0", {"center": v(-632.48, 376.01) * mm, "radius": 1.6 * mm});
            skCircle(sketch, "E5.10.18.1", {"center": v(-627.48, 376.01) * mm, "radius": 1.6 * mm});
            skCircle(sketch, "E5.10.18.2", {"center": v(-629.98, 371.01) * mm, "radius": 1.6 * mm});
            skCircle(sketch, "E5.10.18.3", {"center": v(-624.98, 371.01) * mm, "radius": 1.6 * mm});
            skCircle(sketch, "E5.10.19.0", {"center": v(-632.48, 366.01) * mm, "radius": 1.6 * mm});
            skCircle(sketch, "E5.10.19.1", {"center": v(-627.48, 366.01) * mm, "radius": 1.6 * mm});
            skCircle(sketch, "E5.10.19.2", {"center": v(-629.98, 361.01) * mm, "radius": 1.6 * mm});
            skCircle(sketch, "E5.10.19.3", {"center": v(-624.98, 361.01) * mm, "radius": 1.6 * mm});
            skCircle(sketch, "E5.10.20.0", {"center": v(-632.48, 356.01) * mm, "radius": 1.6 * mm});
            skCircle(sketch, "E5.10.20.1", {"center": v(-627.48, 356.01) * mm, "radius": 1.6 * mm});
            skCircle(sketch, "E5.10.20.2", {"center": v(-629.98, 351.01) * mm, "radius": 1.6 * mm});
            skCircle(sketch, "E5.10.20.3", {"center": v(-624.98, 351.01) * mm, "radius": 1.6 * mm});
            skCircle(sketch, "E5.10.21.0", {"center": v(-632.48, 346.01) * mm, "radius": 1.6 * mm});
            skCircle(sketch, "E5.10.21.1", {"center": v(-627.48, 346.01) * mm, "radius": 1.6 * mm});
            skCircle(sketch, "E5.10.21.2", {"center": v(-629.98, 341.01) * mm, "radius": 1.6 * mm});
            skCircle(sketch, "E5.10.21.3", {"center": v(-624.98, 341.01) * mm, "radius": 1.6 * mm});
            skCircle(sketch, "E5.10.22.0", {"center": v(-632.48, 336.01) * mm, "radius": 1.6 * mm});
            skCircle(sketch, "E5.10.22.1", {"center": v(-627.48, 336.01) * mm, "radius": 1.6 * mm});
            skCircle(sketch, "E5.10.22.2", {"center": v(-629.98, 331.01) * mm, "radius": 1.6 * mm});
            skCircle(sketch, "E5.10.22.3", {"center": v(-624.98, 331.01) * mm, "radius": 1.6 * mm});
            skCircle(sketch, "E5.10.23.0", {"center": v(-632.48, 326.01) * mm, "radius": 1.6 * mm});
            skCircle(sketch, "E5.10.23.1", {"center": v(-627.48, 326.01) * mm, "radius": 1.6 * mm});
            skCircle(sketch, "E5.10.23.2", {"center": v(-629.98, 321.01) * mm, "radius": 1.6 * mm});
            skCircle(sketch, "E5.10.23.3", {"center": v(-624.98, 321.01) * mm, "radius": 1.6 * mm});
            skCircle(sketch, "E5.10.24.0", {"center": v(-632.48, 316.01) * mm, "radius": 1.6 * mm});
            skCircle(sketch, "E5.10.24.1", {"center": v(-627.48, 316.01) * mm, "radius": 1.6 * mm});
            skCircle(sketch, "E5.10.24.2", {"center": v(-629.98, 311.01) * mm, "radius": 1.6 * mm});
            skCircle(sketch, "E5.10.24.3", {"center": v(-624.98, 311.01) * mm, "radius": 1.6 * mm});
            skCircle(sketch, "E5.10.25.0", {"center": v(-632.48, 306.01) * mm, "radius": 1.6 * mm});
            skCircle(sketch, "E5.10.25.1", {"center": v(-627.48, 306.01) * mm, "radius": 1.6 * mm});
            skCircle(sketch, "E5.10.25.2", {"center": v(-629.98, 301.01) * mm, "radius": 1.6 * mm});
            skCircle(sketch, "E5.10.25.3", {"center": v(-624.98, 301.01) * mm, "radius": 1.6 * mm});
            skCircle(sketch, "E5.10.26.0", {"center": v(-632.48, 296.01) * mm, "radius": 1.6 * mm});
            skCircle(sketch, "E5.10.26.1", {"center": v(-627.48, 296.01) * mm, "radius": 1.6 * mm});
            skCircle(sketch, "E5.10.26.2", {"center": v(-629.98, 291.01) * mm, "radius": 1.6 * mm});
            skCircle(sketch, "E5.10.26.3", {"center": v(-624.98, 291.01) * mm, "radius": 1.6 * mm});
            skCircle(sketch, "E5.10.27.0", {"center": v(-632.48, 286.01) * mm, "radius": 1.6 * mm});
            skCircle(sketch, "E5.10.27.1", {"center": v(-627.48, 286.01) * mm, "radius": 1.6 * mm});
            skCircle(sketch, "E5.10.27.2", {"center": v(-629.98, 281.01) * mm, "radius": 1.6 * mm});
            skCircle(sketch, "E5.10.27.3", {"center": v(-624.98, 281.01) * mm, "radius": 1.6 * mm});
            skCircle(sketch, "E5.10.28.0", {"center": v(-632.48, 276.01) * mm, "radius": 1.6 * mm});
            skCircle(sketch, "E5.10.28.1", {"center": v(-627.48, 276.01) * mm, "radius": 1.6 * mm});
            skCircle(sketch, "E5.10.28.2", {"center": v(-629.98, 271.01) * mm, "radius": 1.6 * mm});
            skCircle(sketch, "E5.10.28.3", {"center": v(-624.98, 271.01) * mm, "radius": 1.6 * mm});
            skCircle(sketch, "E5.10.29.0", {"center": v(-632.48, 266.01) * mm, "radius": 1.6 * mm});
            skCircle(sketch, "E5.10.29.1", {"center": v(-627.48, 266.01) * mm, "radius": 1.6 * mm});
            skCircle(sketch, "E5.10.29.2", {"center": v(-629.98, 261.01) * mm, "radius": 1.6 * mm});
            skCircle(sketch, "E5.10.29.3", {"center": v(-624.98, 261.01) * mm, "radius": 1.6 * mm});
            skCircle(sketch, "E5.10.30.0", {"center": v(-632.48, 256.01) * mm, "radius": 1.6 * mm});
            skCircle(sketch, "E5.10.30.1", {"center": v(-627.48, 256.01) * mm, "radius": 1.6 * mm});
            skCircle(sketch, "E5.10.30.2", {"center": v(-629.98, 251.01) * mm, "radius": 1.6 * mm});
            skCircle(sketch, "E5.10.30.3", {"center": v(-624.98, 251.01) * mm, "radius": 1.6 * mm});
            skCircle(sketch, "E5.10.31.0", {"center": v(-632.48, 246.01) * mm, "radius": 1.6 * mm});
            skCircle(sketch, "E5.10.31.1", {"center": v(-627.48, 246.01) * mm, "radius": 1.6 * mm});
            skCircle(sketch, "E5.10.31.2", {"center": v(-629.98, 241.01) * mm, "radius": 1.6 * mm});
            skCircle(sketch, "E5.10.31.3", {"center": v(-624.98, 241.01) * mm, "radius": 1.6 * mm});
            skCircle(sketch, "E5.10.32.0", {"center": v(-632.48, 236.01) * mm, "radius": 1.6 * mm});
            skCircle(sketch, "E5.10.32.1", {"center": v(-627.48, 236.01) * mm, "radius": 1.6 * mm});
            skCircle(sketch, "E5.10.32.2", {"center": v(-629.98, 231.01) * mm, "radius": 1.6 * mm});
            skCircle(sketch, "E5.10.32.3", {"center": v(-624.98, 231.01) * mm, "radius": 1.6 * mm});
            skCircle(sketch, "E5.10.33.0", {"center": v(-632.48, 226.01) * mm, "radius": 1.6 * mm});
            skCircle(sketch, "E5.10.33.1", {"center": v(-627.48, 226.01) * mm, "radius": 1.6 * mm});
            skCircle(sketch, "E5.10.33.2", {"center": v(-629.98, 221.01) * mm, "radius": 1.6 * mm});
            skCircle(sketch, "E5.10.33.3", {"center": v(-624.98, 221.01) * mm, "radius": 1.6 * mm});
            skCircle(sketch, "E5.10.34.0", {"center": v(-632.48, 216.01) * mm, "radius": 1.6 * mm});
            skCircle(sketch, "E5.10.34.1", {"center": v(-627.48, 216.01) * mm, "radius": 1.6 * mm});
            skCircle(sketch, "E5.10.34.2", {"center": v(-629.98, 211.01) * mm, "radius": 1.6 * mm});
            skCircle(sketch, "E5.10.34.3", {"center": v(-624.98, 211.01) * mm, "radius": 1.6 * mm});
            skCircle(sketch, "E5.10.35.0", {"center": v(-632.48, 206.01) * mm, "radius": 1.6 * mm});
            skCircle(sketch, "E5.10.35.1", {"center": v(-627.48, 206.01) * mm, "radius": 1.6 * mm});
            skCircle(sketch, "E5.10.35.2", {"center": v(-629.98, 201.01) * mm, "radius": 1.6 * mm});
            skCircle(sketch, "E5.10.35.3", {"center": v(-624.98, 201.01) * mm, "radius": 1.6 * mm});
            skCircle(sketch, "E5.10.36.0", {"center": v(-632.48, 196.01) * mm, "radius": 1.6 * mm});
            skCircle(sketch, "E5.10.36.1", {"center": v(-627.48, 196.01) * mm, "radius": 1.6 * mm});
            skCircle(sketch, "E5.10.36.2", {"center": v(-629.98, 191.01) * mm, "radius": 1.6 * mm});
            skCircle(sketch, "E5.10.36.3", {"center": v(-624.98, 191.01) * mm, "radius": 1.6 * mm});
            skCircle(sketch, "E5.10.37.0", {"center": v(-632.48, 186.01) * mm, "radius": 1.6 * mm});
            skCircle(sketch, "E5.10.37.1", {"center": v(-627.48, 186.01) * mm, "radius": 1.6 * mm});
            skCircle(sketch, "E5.10.37.2", {"center": v(-629.98, 181.01) * mm, "radius": 1.6 * mm});
            skCircle(sketch, "E5.10.37.3", {"center": v(-624.98, 181.01) * mm, "radius": 1.6 * mm});
            skCircle(sketch, "E5.10.38.0", {"center": v(-632.48, 176.01) * mm, "radius": 1.6 * mm});
            skCircle(sketch, "E5.10.38.1", {"center": v(-627.48, 176.01) * mm, "radius": 1.6 * mm});
            skCircle(sketch, "E5.10.38.2", {"center": v(-629.98, 171.01) * mm, "radius": 1.6 * mm});
            skCircle(sketch, "E5.10.38.3", {"center": v(-624.98, 171.01) * mm, "radius": 1.6 * mm});
            skCircle(sketch, "E5.10.39.0", {"center": v(-632.48, 166.01) * mm, "radius": 1.6 * mm});
            skCircle(sketch, "E5.10.39.1", {"center": v(-627.48, 166.01) * mm, "radius": 1.6 * mm});
            skCircle(sketch, "E5.10.39.2", {"center": v(-629.98, 161.01) * mm, "radius": 1.6 * mm});
            skCircle(sketch, "E5.10.39.3", {"center": v(-624.98, 161.01) * mm, "radius": 1.6 * mm});
            skCircle(sketch, "E5.10.40.0", {"center": v(-632.48, 156.01) * mm, "radius": 1.6 * mm});
            skCircle(sketch, "E5.10.40.1", {"center": v(-627.48, 156.01) * mm, "radius": 1.6 * mm});
            skCircle(sketch, "E5.10.40.2", {"center": v(-629.98, 151.01) * mm, "radius": 1.6 * mm});
            skCircle(sketch, "E5.10.40.3", {"center": v(-624.98, 151.01) * mm, "radius": 1.6 * mm});
            skCircle(sketch, "E5.10.41.0", {"center": v(-632.48, 146.01) * mm, "radius": 1.6 * mm});
            skCircle(sketch, "E5.10.41.1", {"center": v(-627.48, 146.01) * mm, "radius": 1.6 * mm});
            skCircle(sketch, "E5.10.41.2", {"center": v(-629.98, 141.01) * mm, "radius": 1.6 * mm});
            skCircle(sketch, "E5.10.41.3", {"center": v(-624.98, 141.01) * mm, "radius": 1.6 * mm});
            skCircle(sketch, "E5.10.42.0", {"center": v(-632.48, 136.01) * mm, "radius": 1.6 * mm});
            skCircle(sketch, "E5.10.42.1", {"center": v(-627.48, 136.01) * mm, "radius": 1.6 * mm});
            skCircle(sketch, "E5.10.42.2", {"center": v(-629.98, 131.01) * mm, "radius": 1.6 * mm});
            skCircle(sketch, "E5.10.42.3", {"center": v(-624.98, 131.01) * mm, "radius": 1.6 * mm});
            skCircle(sketch, "E5.10.43.0", {"center": v(-632.48, 126.01) * mm, "radius": 1.6 * mm});
            skCircle(sketch, "E5.10.43.1", {"center": v(-627.48, 126.01) * mm, "radius": 1.6 * mm});
            skCircle(sketch, "E5.10.43.2", {"center": v(-629.98, 121.01) * mm, "radius": 1.6 * mm});
            skCircle(sketch, "E5.10.43.3", {"center": v(-624.98, 121.01) * mm, "radius": 1.6 * mm});
            skCircle(sketch, "E5.10.44.0", {"center": v(-632.48, 116.01) * mm, "radius": 1.6 * mm});
            skCircle(sketch, "E5.10.44.1", {"center": v(-627.48, 116.01) * mm, "radius": 1.6 * mm});
            skCircle(sketch, "E5.10.44.2", {"center": v(-629.98, 111.01) * mm, "radius": 1.6 * mm});
            skCircle(sketch, "E5.10.44.3", {"center": v(-624.98, 111.01) * mm, "radius": 1.6 * mm});
            skCircle(sketch, "E5.10.45.0", {"center": v(-632.48, 106.01) * mm, "radius": 1.6 * mm});
            skCircle(sketch, "E5.10.45.1", {"center": v(-627.48, 106.01) * mm, "radius": 1.6 * mm});
            skCircle(sketch, "E5.10.45.2", {"center": v(-629.98, 101.01) * mm, "radius": 1.6 * mm});
            skCircle(sketch, "E5.10.45.3", {"center": v(-624.98, 101.01) * mm, "radius": 1.6 * mm});
            skCircle(sketch, "E5.10.46.0", {"center": v(-632.48, 96.01) * mm, "radius": 1.6 * mm});
            skCircle(sketch, "E5.10.46.1", {"center": v(-627.48, 96.01) * mm, "radius": 1.6 * mm});
            skCircle(sketch, "E5.10.46.2", {"center": v(-629.98, 91.01) * mm, "radius": 1.6 * mm});
            skCircle(sketch, "E5.10.46.3", {"center": v(-624.98, 91.01) * mm, "radius": 1.6 * mm});
            skCircle(sketch, "E5.10.47.0", {"center": v(-632.48, 86.01) * mm, "radius": 1.6 * mm});
            skCircle(sketch, "E5.10.47.1", {"center": v(-627.48, 86.01) * mm, "radius": 1.6 * mm});
            skCircle(sketch, "E5.10.47.2", {"center": v(-629.98, 81.01) * mm, "radius": 1.6 * mm});
            skCircle(sketch, "E5.10.47.3", {"center": v(-624.98, 81.01) * mm, "radius": 1.6 * mm});
            skCircle(sketch, "E5.10.48.0", {"center": v(-632.48, 76.01) * mm, "radius": 1.6 * mm});
            skCircle(sketch, "E5.10.48.1", {"center": v(-627.48, 76.01) * mm, "radius": 1.6 * mm});
            skCircle(sketch, "E5.10.48.2", {"center": v(-629.98, 71.01) * mm, "radius": 1.6 * mm});
            skCircle(sketch, "E5.10.48.3", {"center": v(-624.98, 71.01) * mm, "radius": 1.6 * mm});
            skCircle(sketch, "E5.10.49.0", {"center": v(-632.48, 66.01) * mm, "radius": 1.6 * mm});
            skCircle(sketch, "E5.10.49.1", {"center": v(-627.48, 66.01) * mm, "radius": 1.6 * mm});
            skCircle(sketch, "E5.10.49.2", {"center": v(-629.98, 61.01) * mm, "radius": 1.6 * mm});
            skCircle(sketch, "E5.10.49.3", {"center": v(-624.98, 61.01) * mm, "radius": 1.6 * mm});
            skCircle(sketch, "E5.11.0.0", {"center": v(-622.48, 556.01) * mm, "radius": 1.6 * mm});
            skCircle(sketch, "E5.11.0.1", {"center": v(-617.48, 556.01) * mm, "radius": 1.6 * mm});
            skCircle(sketch, "E5.11.0.2", {"center": v(-619.98, 551.01) * mm, "radius": 1.6 * mm});
            skCircle(sketch, "E5.11.0.3", {"center": v(-614.98, 551.01) * mm, "radius": 1.6 * mm});
            skCircle(sketch, "E5.11.1.0", {"center": v(-622.48, 546.01) * mm, "radius": 1.6 * mm});
            skCircle(sketch, "E5.11.1.1", {"center": v(-617.48, 546.01) * mm, "radius": 1.6 * mm});
            skCircle(sketch, "E5.11.1.2", {"center": v(-619.98, 541.01) * mm, "radius": 1.6 * mm});
            skCircle(sketch, "E5.11.1.3", {"center": v(-614.98, 541.01) * mm, "radius": 1.6 * mm});
            skCircle(sketch, "E5.11.2.0", {"center": v(-622.48, 536.01) * mm, "radius": 1.6 * mm});
            skCircle(sketch, "E5.11.2.1", {"center": v(-617.48, 536.01) * mm, "radius": 1.6 * mm});
            skCircle(sketch, "E5.11.2.2", {"center": v(-619.98, 531.01) * mm, "radius": 1.6 * mm});
            skCircle(sketch, "E5.11.2.3", {"center": v(-614.98, 531.01) * mm, "radius": 1.6 * mm});
            skCircle(sketch, "E5.11.3.0", {"center": v(-622.48, 526.01) * mm, "radius": 1.6 * mm});
            skCircle(sketch, "E5.11.3.1", {"center": v(-617.48, 526.01) * mm, "radius": 1.6 * mm});
            skCircle(sketch, "E5.11.3.2", {"center": v(-619.98, 521.01) * mm, "radius": 1.6 * mm});
            skCircle(sketch, "E5.11.3.3", {"center": v(-614.98, 521.01) * mm, "radius": 1.6 * mm});
            skCircle(sketch, "E5.11.4.0", {"center": v(-622.48, 516.01) * mm, "radius": 1.6 * mm});
            skCircle(sketch, "E5.11.4.1", {"center": v(-617.48, 516.01) * mm, "radius": 1.6 * mm});
            skCircle(sketch, "E5.11.4.2", {"center": v(-619.98, 511.01) * mm, "radius": 1.6 * mm});
            skCircle(sketch, "E5.11.4.3", {"center": v(-614.98, 511.01) * mm, "radius": 1.6 * mm});
            skCircle(sketch, "E5.11.5.0", {"center": v(-622.48, 506.01) * mm, "radius": 1.6 * mm});
            skCircle(sketch, "E5.11.5.1", {"center": v(-617.48, 506.01) * mm, "radius": 1.6 * mm});
            skCircle(sketch, "E5.11.5.2", {"center": v(-619.98, 501.01) * mm, "radius": 1.6 * mm});
            skCircle(sketch, "E5.11.5.3", {"center": v(-614.98, 501.01) * mm, "radius": 1.6 * mm});
            skCircle(sketch, "E5.11.6.0", {"center": v(-622.48, 496.01) * mm, "radius": 1.6 * mm});
            skCircle(sketch, "E5.11.6.1", {"center": v(-617.48, 496.01) * mm, "radius": 1.6 * mm});
            skCircle(sketch, "E5.11.6.2", {"center": v(-619.98, 491.01) * mm, "radius": 1.6 * mm});
            skCircle(sketch, "E5.11.6.3", {"center": v(-614.98, 491.01) * mm, "radius": 1.6 * mm});
            skCircle(sketch, "E5.11.7.0", {"center": v(-622.48, 486.01) * mm, "radius": 1.6 * mm});
            skCircle(sketch, "E5.11.7.1", {"center": v(-617.48, 486.01) * mm, "radius": 1.6 * mm});
            skCircle(sketch, "E5.11.7.2", {"center": v(-619.98, 481.01) * mm, "radius": 1.6 * mm});
            skCircle(sketch, "E5.11.7.3", {"center": v(-614.98, 481.01) * mm, "radius": 1.6 * mm});
            skCircle(sketch, "E5.11.8.0", {"center": v(-622.48, 476.01) * mm, "radius": 1.6 * mm});
            skCircle(sketch, "E5.11.8.1", {"center": v(-617.48, 476.01) * mm, "radius": 1.6 * mm});
            skCircle(sketch, "E5.11.8.2", {"center": v(-619.98, 471.01) * mm, "radius": 1.6 * mm});
            skCircle(sketch, "E5.11.8.3", {"center": v(-614.98, 471.01) * mm, "radius": 1.6 * mm});
            skCircle(sketch, "E5.11.9.0", {"center": v(-622.48, 466.01) * mm, "radius": 1.6 * mm});
            skCircle(sketch, "E5.11.9.1", {"center": v(-617.48, 466.01) * mm, "radius": 1.6 * mm});
            skCircle(sketch, "E5.11.9.2", {"center": v(-619.98, 461.01) * mm, "radius": 1.6 * mm});
            skCircle(sketch, "E5.11.9.3", {"center": v(-614.98, 461.01) * mm, "radius": 1.6 * mm});
            skCircle(sketch, "E5.11.10.0", {"center": v(-622.48, 456.01) * mm, "radius": 1.6 * mm});
            skCircle(sketch, "E5.11.10.1", {"center": v(-617.48, 456.01) * mm, "radius": 1.6 * mm});
            skCircle(sketch, "E5.11.10.2", {"center": v(-619.98, 451.01) * mm, "radius": 1.6 * mm});
            skCircle(sketch, "E5.11.10.3", {"center": v(-614.98, 451.01) * mm, "radius": 1.6 * mm});
            skCircle(sketch, "E5.11.11.0", {"center": v(-622.48, 446.01) * mm, "radius": 1.6 * mm});
            skCircle(sketch, "E5.11.11.1", {"center": v(-617.48, 446.01) * mm, "radius": 1.6 * mm});
            skCircle(sketch, "E5.11.11.2", {"center": v(-619.98, 441.01) * mm, "radius": 1.6 * mm});
            skCircle(sketch, "E5.11.11.3", {"center": v(-614.98, 441.01) * mm, "radius": 1.6 * mm});
            skCircle(sketch, "E5.11.12.0", {"center": v(-622.48, 436.01) * mm, "radius": 1.6 * mm});
            skCircle(sketch, "E5.11.12.1", {"center": v(-617.48, 436.01) * mm, "radius": 1.6 * mm});
            skCircle(sketch, "E5.11.12.2", {"center": v(-619.98, 431.01) * mm, "radius": 1.6 * mm});
            skCircle(sketch, "E5.11.12.3", {"center": v(-614.98, 431.01) * mm, "radius": 1.6 * mm});
            skCircle(sketch, "E5.11.13.0", {"center": v(-622.48, 426.01) * mm, "radius": 1.6 * mm});
            skCircle(sketch, "E5.11.13.1", {"center": v(-617.48, 426.01) * mm, "radius": 1.6 * mm});
            skCircle(sketch, "E5.11.13.2", {"center": v(-619.98, 421.01) * mm, "radius": 1.6 * mm});
            skCircle(sketch, "E5.11.13.3", {"center": v(-614.98, 421.01) * mm, "radius": 1.6 * mm});
            skCircle(sketch, "E5.11.14.0", {"center": v(-622.48, 416.01) * mm, "radius": 1.6 * mm});
            skCircle(sketch, "E5.11.14.1", {"center": v(-617.48, 416.01) * mm, "radius": 1.6 * mm});
            skCircle(sketch, "E5.11.14.2", {"center": v(-619.98, 411.01) * mm, "radius": 1.6 * mm});
            skCircle(sketch, "E5.11.14.3", {"center": v(-614.98, 411.01) * mm, "radius": 1.6 * mm});
            skCircle(sketch, "E5.11.15.0", {"center": v(-622.48, 406.01) * mm, "radius": 1.6 * mm});
            skCircle(sketch, "E5.11.15.1", {"center": v(-617.48, 406.01) * mm, "radius": 1.6 * mm});
            skCircle(sketch, "E5.11.15.2", {"center": v(-619.98, 401.01) * mm, "radius": 1.6 * mm});
            skCircle(sketch, "E5.11.15.3", {"center": v(-614.98, 401.01) * mm, "radius": 1.6 * mm});
            skCircle(sketch, "E5.11.16.0", {"center": v(-622.48, 396.01) * mm, "radius": 1.6 * mm});
            skCircle(sketch, "E5.11.16.1", {"center": v(-617.48, 396.01) * mm, "radius": 1.6 * mm});
            skCircle(sketch, "E5.11.16.2", {"center": v(-619.98, 391.01) * mm, "radius": 1.6 * mm});
            skCircle(sketch, "E5.11.16.3", {"center": v(-614.98, 391.01) * mm, "radius": 1.6 * mm});
            skCircle(sketch, "E5.11.17.0", {"center": v(-622.48, 386.01) * mm, "radius": 1.6 * mm});
            skCircle(sketch, "E5.11.17.1", {"center": v(-617.48, 386.01) * mm, "radius": 1.6 * mm});
            skCircle(sketch, "E5.11.17.2", {"center": v(-619.98, 381.01) * mm, "radius": 1.6 * mm});
            skCircle(sketch, "E5.11.17.3", {"center": v(-614.98, 381.01) * mm, "radius": 1.6 * mm});
            skCircle(sketch, "E5.11.18.0", {"center": v(-622.48, 376.01) * mm, "radius": 1.6 * mm});
            skCircle(sketch, "E5.11.18.1", {"center": v(-617.48, 376.01) * mm, "radius": 1.6 * mm});
            skCircle(sketch, "E5.11.18.2", {"center": v(-619.98, 371.01) * mm, "radius": 1.6 * mm});
            skCircle(sketch, "E5.11.18.3", {"center": v(-614.98, 371.01) * mm, "radius": 1.6 * mm});
            skCircle(sketch, "E5.11.19.0", {"center": v(-622.48, 366.01) * mm, "radius": 1.6 * mm});
            skCircle(sketch, "E5.11.19.1", {"center": v(-617.48, 366.01) * mm, "radius": 1.6 * mm});
            skCircle(sketch, "E5.11.19.2", {"center": v(-619.98, 361.01) * mm, "radius": 1.6 * mm});
            skCircle(sketch, "E5.11.19.3", {"center": v(-614.98, 361.01) * mm, "radius": 1.6 * mm});
            skCircle(sketch, "E5.11.20.0", {"center": v(-622.48, 356.01) * mm, "radius": 1.6 * mm});
            skCircle(sketch, "E5.11.20.1", {"center": v(-617.48, 356.01) * mm, "radius": 1.6 * mm});
            skCircle(sketch, "E5.11.20.2", {"center": v(-619.98, 351.01) * mm, "radius": 1.6 * mm});
            skCircle(sketch, "E5.11.20.3", {"center": v(-614.98, 351.01) * mm, "radius": 1.6 * mm});
            skCircle(sketch, "E5.11.21.0", {"center": v(-622.48, 346.01) * mm, "radius": 1.6 * mm});
            skCircle(sketch, "E5.11.21.1", {"center": v(-617.48, 346.01) * mm, "radius": 1.6 * mm});
            skCircle(sketch, "E5.11.21.2", {"center": v(-619.98, 341.01) * mm, "radius": 1.6 * mm});
            skCircle(sketch, "E5.11.21.3", {"center": v(-614.98, 341.01) * mm, "radius": 1.6 * mm});
            skCircle(sketch, "E5.11.22.0", {"center": v(-622.48, 336.01) * mm, "radius": 1.6 * mm});
            skCircle(sketch, "E5.11.22.1", {"center": v(-617.48, 336.01) * mm, "radius": 1.6 * mm});
            skCircle(sketch, "E5.11.22.2", {"center": v(-619.98, 331.01) * mm, "radius": 1.6 * mm});
            skCircle(sketch, "E5.11.22.3", {"center": v(-614.98, 331.01) * mm, "radius": 1.6 * mm});
            skCircle(sketch, "E5.11.23.0", {"center": v(-622.48, 326.01) * mm, "radius": 1.6 * mm});
            skCircle(sketch, "E5.11.23.1", {"center": v(-617.48, 326.01) * mm, "radius": 1.6 * mm});
            skCircle(sketch, "E5.11.23.2", {"center": v(-619.98, 321.01) * mm, "radius": 1.6 * mm});
            skCircle(sketch, "E5.11.23.3", {"center": v(-614.98, 321.01) * mm, "radius": 1.6 * mm});
            skCircle(sketch, "E5.11.24.0", {"center": v(-622.48, 316.01) * mm, "radius": 1.6 * mm});
            skCircle(sketch, "E5.11.24.1", {"center": v(-617.48, 316.01) * mm, "radius": 1.6 * mm});
            skCircle(sketch, "E5.11.24.2", {"center": v(-619.98, 311.01) * mm, "radius": 1.6 * mm});
            skCircle(sketch, "E5.11.24.3", {"center": v(-614.98, 311.01) * mm, "radius": 1.6 * mm});
            skCircle(sketch, "E5.11.25.0", {"center": v(-622.48, 306.01) * mm, "radius": 1.6 * mm});
            skCircle(sketch, "E5.11.25.1", {"center": v(-617.48, 306.01) * mm, "radius": 1.6 * mm});
            skCircle(sketch, "E5.11.25.2", {"center": v(-619.98, 301.01) * mm, "radius": 1.6 * mm});
            skCircle(sketch, "E5.11.25.3", {"center": v(-614.98, 301.01) * mm, "radius": 1.6 * mm});
            skCircle(sketch, "E5.11.26.0", {"center": v(-622.48, 296.01) * mm, "radius": 1.6 * mm});
            skCircle(sketch, "E5.11.26.1", {"center": v(-617.48, 296.01) * mm, "radius": 1.6 * mm});
            skCircle(sketch, "E5.11.26.2", {"center": v(-619.98, 291.01) * mm, "radius": 1.6 * mm});
            skCircle(sketch, "E5.11.26.3", {"center": v(-614.98, 291.01) * mm, "radius": 1.6 * mm});
            skCircle(sketch, "E5.11.27.0", {"center": v(-622.48, 286.01) * mm, "radius": 1.6 * mm});
            skCircle(sketch, "E5.11.27.1", {"center": v(-617.48, 286.01) * mm, "radius": 1.6 * mm});
            skCircle(sketch, "E5.11.27.2", {"center": v(-619.98, 281.01) * mm, "radius": 1.6 * mm});
            skCircle(sketch, "E5.11.27.3", {"center": v(-614.98, 281.01) * mm, "radius": 1.6 * mm});
            skCircle(sketch, "E5.11.28.0", {"center": v(-622.48, 276.01) * mm, "radius": 1.6 * mm});
            skCircle(sketch, "E5.11.28.1", {"center": v(-617.48, 276.01) * mm, "radius": 1.6 * mm});
            skCircle(sketch, "E5.11.28.2", {"center": v(-619.98, 271.01) * mm, "radius": 1.6 * mm});
            skCircle(sketch, "E5.11.28.3", {"center": v(-614.98, 271.01) * mm, "radius": 1.6 * mm});
            skCircle(sketch, "E5.11.29.0", {"center": v(-622.48, 266.01) * mm, "radius": 1.6 * mm});
            skCircle(sketch, "E5.11.29.1", {"center": v(-617.48, 266.01) * mm, "radius": 1.6 * mm});
            skCircle(sketch, "E5.11.29.2", {"center": v(-619.98, 261.01) * mm, "radius": 1.6 * mm});
            skCircle(sketch, "E5.11.29.3", {"center": v(-614.98, 261.01) * mm, "radius": 1.6 * mm});
            skCircle(sketch, "E5.11.30.0", {"center": v(-622.48, 256.01) * mm, "radius": 1.6 * mm});
            skCircle(sketch, "E5.11.30.1", {"center": v(-617.48, 256.01) * mm, "radius": 1.6 * mm});
            skCircle(sketch, "E5.11.30.2", {"center": v(-619.98, 251.01) * mm, "radius": 1.6 * mm});
            skCircle(sketch, "E5.11.30.3", {"center": v(-614.98, 251.01) * mm, "radius": 1.6 * mm});
            skCircle(sketch, "E5.11.31.0", {"center": v(-622.48, 246.01) * mm, "radius": 1.6 * mm});
            skCircle(sketch, "E5.11.31.1", {"center": v(-617.48, 246.01) * mm, "radius": 1.6 * mm});
            skCircle(sketch, "E5.11.31.2", {"center": v(-619.98, 241.01) * mm, "radius": 1.6 * mm});
            skCircle(sketch, "E5.11.31.3", {"center": v(-614.98, 241.01) * mm, "radius": 1.6 * mm});
            skCircle(sketch, "E5.11.32.0", {"center": v(-622.48, 236.01) * mm, "radius": 1.6 * mm});
            skCircle(sketch, "E5.11.32.1", {"center": v(-617.48, 236.01) * mm, "radius": 1.6 * mm});
            skCircle(sketch, "E5.11.32.2", {"center": v(-619.98, 231.01) * mm, "radius": 1.6 * mm});
            skCircle(sketch, "E5.11.32.3", {"center": v(-614.98, 231.01) * mm, "radius": 1.6 * mm});
            skCircle(sketch, "E5.11.33.0", {"center": v(-622.48, 226.01) * mm, "radius": 1.6 * mm});
            skCircle(sketch, "E5.11.33.1", {"center": v(-617.48, 226.01) * mm, "radius": 1.6 * mm});
            skCircle(sketch, "E5.11.33.2", {"center": v(-619.98, 221.01) * mm, "radius": 1.6 * mm});
            skCircle(sketch, "E5.11.33.3", {"center": v(-614.98, 221.01) * mm, "radius": 1.6 * mm});
            skCircle(sketch, "E5.11.34.0", {"center": v(-622.48, 216.01) * mm, "radius": 1.6 * mm});
            skCircle(sketch, "E5.11.34.1", {"center": v(-617.48, 216.01) * mm, "radius": 1.6 * mm});
            skCircle(sketch, "E5.11.34.2", {"center": v(-619.98, 211.01) * mm, "radius": 1.6 * mm});
            skCircle(sketch, "E5.11.34.3", {"center": v(-614.98, 211.01) * mm, "radius": 1.6 * mm});
            skCircle(sketch, "E5.11.35.0", {"center": v(-622.48, 206.01) * mm, "radius": 1.6 * mm});
            skCircle(sketch, "E5.11.35.1", {"center": v(-617.48, 206.01) * mm, "radius": 1.6 * mm});
            skCircle(sketch, "E5.11.35.2", {"center": v(-619.98, 201.01) * mm, "radius": 1.6 * mm});
            skCircle(sketch, "E5.11.35.3", {"center": v(-614.98, 201.01) * mm, "radius": 1.6 * mm});
            skCircle(sketch, "E5.11.36.0", {"center": v(-622.48, 196.01) * mm, "radius": 1.6 * mm});
            skCircle(sketch, "E5.11.36.1", {"center": v(-617.48, 196.01) * mm, "radius": 1.6 * mm});
            skCircle(sketch, "E5.11.36.2", {"center": v(-619.98, 191.01) * mm, "radius": 1.6 * mm});
            skCircle(sketch, "E5.11.36.3", {"center": v(-614.98, 191.01) * mm, "radius": 1.6 * mm});
            skCircle(sketch, "E5.11.37.0", {"center": v(-622.48, 186.01) * mm, "radius": 1.6 * mm});
            skCircle(sketch, "E5.11.37.1", {"center": v(-617.48, 186.01) * mm, "radius": 1.6 * mm});
            skCircle(sketch, "E5.11.37.2", {"center": v(-619.98, 181.01) * mm, "radius": 1.6 * mm});
            skCircle(sketch, "E5.11.37.3", {"center": v(-614.98, 181.01) * mm, "radius": 1.6 * mm});
            skCircle(sketch, "E5.11.38.0", {"center": v(-622.48, 176.01) * mm, "radius": 1.6 * mm});
            skCircle(sketch, "E5.11.38.1", {"center": v(-617.48, 176.01) * mm, "radius": 1.6 * mm});
            skCircle(sketch, "E5.11.38.2", {"center": v(-619.98, 171.01) * mm, "radius": 1.6 * mm});
            skCircle(sketch, "E5.11.38.3", {"center": v(-614.98, 171.01) * mm, "radius": 1.6 * mm});
            skCircle(sketch, "E5.11.39.0", {"center": v(-622.48, 166.01) * mm, "radius": 1.6 * mm});
            skCircle(sketch, "E5.11.39.1", {"center": v(-617.48, 166.01) * mm, "radius": 1.6 * mm});
            skCircle(sketch, "E5.11.39.2", {"center": v(-619.98, 161.01) * mm, "radius": 1.6 * mm});
            skCircle(sketch, "E5.11.39.3", {"center": v(-614.98, 161.01) * mm, "radius": 1.6 * mm});
            skCircle(sketch, "E5.11.40.0", {"center": v(-622.48, 156.01) * mm, "radius": 1.6 * mm});
            skCircle(sketch, "E5.11.40.1", {"center": v(-617.48, 156.01) * mm, "radius": 1.6 * mm});
            skCircle(sketch, "E5.11.40.2", {"center": v(-619.98, 151.01) * mm, "radius": 1.6 * mm});
            skCircle(sketch, "E5.11.40.3", {"center": v(-614.98, 151.01) * mm, "radius": 1.6 * mm});
            skCircle(sketch, "E5.11.41.0", {"center": v(-622.48, 146.01) * mm, "radius": 1.6 * mm});
            skCircle(sketch, "E5.11.41.1", {"center": v(-617.48, 146.01) * mm, "radius": 1.6 * mm});
            skCircle(sketch, "E5.11.41.2", {"center": v(-619.98, 141.01) * mm, "radius": 1.6 * mm});
            skCircle(sketch, "E5.11.41.3", {"center": v(-614.98, 141.01) * mm, "radius": 1.6 * mm});
            skCircle(sketch, "E5.11.42.0", {"center": v(-622.48, 136.01) * mm, "radius": 1.6 * mm});
            skCircle(sketch, "E5.11.42.1", {"center": v(-617.48, 136.01) * mm, "radius": 1.6 * mm});
            skCircle(sketch, "E5.11.42.2", {"center": v(-619.98, 131.01) * mm, "radius": 1.6 * mm});
            skCircle(sketch, "E5.11.42.3", {"center": v(-614.98, 131.01) * mm, "radius": 1.6 * mm});
            skCircle(sketch, "E5.11.43.0", {"center": v(-622.48, 126.01) * mm, "radius": 1.6 * mm});
            skCircle(sketch, "E5.11.43.1", {"center": v(-617.48, 126.01) * mm, "radius": 1.6 * mm});
            skCircle(sketch, "E5.11.43.2", {"center": v(-619.98, 121.01) * mm, "radius": 1.6 * mm});
            skCircle(sketch, "E5.11.43.3", {"center": v(-614.98, 121.01) * mm, "radius": 1.6 * mm});
            skCircle(sketch, "E5.11.44.0", {"center": v(-622.48, 116.01) * mm, "radius": 1.6 * mm});
            skCircle(sketch, "E5.11.44.1", {"center": v(-617.48, 116.01) * mm, "radius": 1.6 * mm});
            skCircle(sketch, "E5.11.44.2", {"center": v(-619.98, 111.01) * mm, "radius": 1.6 * mm});
            skCircle(sketch, "E5.11.44.3", {"center": v(-614.98, 111.01) * mm, "radius": 1.6 * mm});
            skCircle(sketch, "E5.11.45.0", {"center": v(-622.48, 106.01) * mm, "radius": 1.6 * mm});
            skCircle(sketch, "E5.11.45.1", {"center": v(-617.48, 106.01) * mm, "radius": 1.6 * mm});
            skCircle(sketch, "E5.11.45.2", {"center": v(-619.98, 101.01) * mm, "radius": 1.6 * mm});
            skCircle(sketch, "E5.11.45.3", {"center": v(-614.98, 101.01) * mm, "radius": 1.6 * mm});
            skCircle(sketch, "E5.11.46.0", {"center": v(-622.48, 96.01) * mm, "radius": 1.6 * mm});
            skCircle(sketch, "E5.11.46.1", {"center": v(-617.48, 96.01) * mm, "radius": 1.6 * mm});
            skCircle(sketch, "E5.11.46.2", {"center": v(-619.98, 91.01) * mm, "radius": 1.6 * mm});
            skCircle(sketch, "E5.11.46.3", {"center": v(-614.98, 91.01) * mm, "radius": 1.6 * mm});
            skCircle(sketch, "E5.11.47.0", {"center": v(-622.48, 86.01) * mm, "radius": 1.6 * mm});
            skCircle(sketch, "E5.11.47.1", {"center": v(-617.48, 86.01) * mm, "radius": 1.6 * mm});
            skCircle(sketch, "E5.11.47.2", {"center": v(-619.98, 81.01) * mm, "radius": 1.6 * mm});
            skCircle(sketch, "E5.11.47.3", {"center": v(-614.98, 81.01) * mm, "radius": 1.6 * mm});
            skCircle(sketch, "E5.11.48.0", {"center": v(-622.48, 76.01) * mm, "radius": 1.6 * mm});
            skCircle(sketch, "E5.11.48.1", {"center": v(-617.48, 76.01) * mm, "radius": 1.6 * mm});
            skCircle(sketch, "E5.11.48.2", {"center": v(-619.98, 71.01) * mm, "radius": 1.6 * mm});
            skCircle(sketch, "E5.11.48.3", {"center": v(-614.98, 71.01) * mm, "radius": 1.6 * mm});
            skCircle(sketch, "E5.11.49.0", {"center": v(-622.48, 66.01) * mm, "radius": 1.6 * mm});
            skCircle(sketch, "E5.11.49.1", {"center": v(-617.48, 66.01) * mm, "radius": 1.6 * mm});
            skCircle(sketch, "E5.11.49.2", {"center": v(-619.98, 61.01) * mm, "radius": 1.6 * mm});
            skCircle(sketch, "E5.11.49.3", {"center": v(-614.98, 61.01) * mm, "radius": 1.6 * mm});
            skCircle(sketch, "E5.12.0.0", {"center": v(-612.48, 556.01) * mm, "radius": 1.6 * mm});
            skCircle(sketch, "E5.12.0.1", {"center": v(-607.48, 556.01) * mm, "radius": 1.6 * mm});
            skCircle(sketch, "E5.12.0.2", {"center": v(-609.98, 551.01) * mm, "radius": 1.6 * mm});
            skCircle(sketch, "E5.12.0.3", {"center": v(-604.98, 551.01) * mm, "radius": 1.6 * mm});
            skCircle(sketch, "E5.12.1.0", {"center": v(-612.48, 546.01) * mm, "radius": 1.6 * mm});
            skCircle(sketch, "E5.12.1.1", {"center": v(-607.48, 546.01) * mm, "radius": 1.6 * mm});
            skCircle(sketch, "E5.12.1.2", {"center": v(-609.98, 541.01) * mm, "radius": 1.6 * mm});
            skCircle(sketch, "E5.12.1.3", {"center": v(-604.98, 541.01) * mm, "radius": 1.6 * mm});
            skCircle(sketch, "E5.12.2.0", {"center": v(-612.48, 536.01) * mm, "radius": 1.6 * mm});
            skCircle(sketch, "E5.12.2.1", {"center": v(-607.48, 536.01) * mm, "radius": 1.6 * mm});
            skCircle(sketch, "E5.12.2.2", {"center": v(-609.98, 531.01) * mm, "radius": 1.6 * mm});
            skCircle(sketch, "E5.12.2.3", {"center": v(-604.98, 531.01) * mm, "radius": 1.6 * mm});
            skCircle(sketch, "E5.12.3.0", {"center": v(-612.48, 526.01) * mm, "radius": 1.6 * mm});
            skCircle(sketch, "E5.12.3.1", {"center": v(-607.48, 526.01) * mm, "radius": 1.6 * mm});
            skCircle(sketch, "E5.12.3.2", {"center": v(-609.98, 521.01) * mm, "radius": 1.6 * mm});
            skCircle(sketch, "E5.12.3.3", {"center": v(-604.98, 521.01) * mm, "radius": 1.6 * mm});
            skCircle(sketch, "E5.12.4.0", {"center": v(-612.48, 516.01) * mm, "radius": 1.6 * mm});
            skCircle(sketch, "E5.12.4.1", {"center": v(-607.48, 516.01) * mm, "radius": 1.6 * mm});
            skCircle(sketch, "E5.12.4.2", {"center": v(-609.98, 511.01) * mm, "radius": 1.6 * mm});
            skCircle(sketch, "E5.12.4.3", {"center": v(-604.98, 511.01) * mm, "radius": 1.6 * mm});
            skCircle(sketch, "E5.12.5.0", {"center": v(-612.48, 506.01) * mm, "radius": 1.6 * mm});
            skCircle(sketch, "E5.12.5.1", {"center": v(-607.48, 506.01) * mm, "radius": 1.6 * mm});
            skCircle(sketch, "E5.12.5.2", {"center": v(-609.98, 501.01) * mm, "radius": 1.6 * mm});
            skCircle(sketch, "E5.12.5.3", {"center": v(-604.98, 501.01) * mm, "radius": 1.6 * mm});
            skCircle(sketch, "E5.12.6.0", {"center": v(-612.48, 496.01) * mm, "radius": 1.6 * mm});
            skCircle(sketch, "E5.12.6.1", {"center": v(-607.48, 496.01) * mm, "radius": 1.6 * mm});
            skCircle(sketch, "E5.12.6.2", {"center": v(-609.98, 491.01) * mm, "radius": 1.6 * mm});
            skCircle(sketch, "E5.12.6.3", {"center": v(-604.98, 491.01) * mm, "radius": 1.6 * mm});
            skCircle(sketch, "E5.12.7.0", {"center": v(-612.48, 486.01) * mm, "radius": 1.6 * mm});
            skCircle(sketch, "E5.12.7.1", {"center": v(-607.48, 486.01) * mm, "radius": 1.6 * mm});
            skCircle(sketch, "E5.12.7.2", {"center": v(-609.98, 481.01) * mm, "radius": 1.6 * mm});
            skCircle(sketch, "E5.12.7.3", {"center": v(-604.98, 481.01) * mm, "radius": 1.6 * mm});
            skCircle(sketch, "E5.12.8.0", {"center": v(-612.48, 476.01) * mm, "radius": 1.6 * mm});
            skCircle(sketch, "E5.12.8.1", {"center": v(-607.48, 476.01) * mm, "radius": 1.6 * mm});
            skCircle(sketch, "E5.12.8.2", {"center": v(-609.98, 471.01) * mm, "radius": 1.6 * mm});
            skCircle(sketch, "E5.12.8.3", {"center": v(-604.98, 471.01) * mm, "radius": 1.6 * mm});
            skCircle(sketch, "E5.12.9.0", {"center": v(-612.48, 466.01) * mm, "radius": 1.6 * mm});
            skCircle(sketch, "E5.12.9.1", {"center": v(-607.48, 466.01) * mm, "radius": 1.6 * mm});
            skCircle(sketch, "E5.12.9.2", {"center": v(-609.98, 461.01) * mm, "radius": 1.6 * mm});
            skCircle(sketch, "E5.12.9.3", {"center": v(-604.98, 461.01) * mm, "radius": 1.6 * mm});
            skCircle(sketch, "E5.12.10.0", {"center": v(-612.48, 456.01) * mm, "radius": 1.6 * mm});
            skCircle(sketch, "E5.12.10.1", {"center": v(-607.48, 456.01) * mm, "radius": 1.6 * mm});
            skCircle(sketch, "E5.12.10.2", {"center": v(-609.98, 451.01) * mm, "radius": 1.6 * mm});
            skCircle(sketch, "E5.12.10.3", {"center": v(-604.98, 451.01) * mm, "radius": 1.6 * mm});
            skCircle(sketch, "E5.12.11.0", {"center": v(-612.48, 446.01) * mm, "radius": 1.6 * mm});
            skCircle(sketch, "E5.12.11.1", {"center": v(-607.48, 446.01) * mm, "radius": 1.6 * mm});
            skCircle(sketch, "E5.12.11.2", {"center": v(-609.98, 441.01) * mm, "radius": 1.6 * mm});
            skCircle(sketch, "E5.12.11.3", {"center": v(-604.98, 441.01) * mm, "radius": 1.6 * mm});
            skCircle(sketch, "E5.12.12.0", {"center": v(-612.48, 436.01) * mm, "radius": 1.6 * mm});
            skCircle(sketch, "E5.12.12.1", {"center": v(-607.48, 436.01) * mm, "radius": 1.6 * mm});
            skCircle(sketch, "E5.12.12.2", {"center": v(-609.98, 431.01) * mm, "radius": 1.6 * mm});
            skCircle(sketch, "E5.12.12.3", {"center": v(-604.98, 431.01) * mm, "radius": 1.6 * mm});
            skCircle(sketch, "E5.12.13.0", {"center": v(-612.48, 426.01) * mm, "radius": 1.6 * mm});
            skCircle(sketch, "E5.12.13.1", {"center": v(-607.48, 426.01) * mm, "radius": 1.6 * mm});
            skCircle(sketch, "E5.12.13.2", {"center": v(-609.98, 421.01) * mm, "radius": 1.6 * mm});
            skCircle(sketch, "E5.12.13.3", {"center": v(-604.98, 421.01) * mm, "radius": 1.6 * mm});
            skCircle(sketch, "E5.12.14.0", {"center": v(-612.48, 416.01) * mm, "radius": 1.6 * mm});
            skCircle(sketch, "E5.12.14.1", {"center": v(-607.48, 416.01) * mm, "radius": 1.6 * mm});
            skCircle(sketch, "E5.12.14.2", {"center": v(-609.98, 411.01) * mm, "radius": 1.6 * mm});
            skCircle(sketch, "E5.12.14.3", {"center": v(-604.98, 411.01) * mm, "radius": 1.6 * mm});
            skCircle(sketch, "E5.12.15.0", {"center": v(-612.48, 406.01) * mm, "radius": 1.6 * mm});
            skCircle(sketch, "E5.12.15.1", {"center": v(-607.48, 406.01) * mm, "radius": 1.6 * mm});
            skCircle(sketch, "E5.12.15.2", {"center": v(-609.98, 401.01) * mm, "radius": 1.6 * mm});
            skCircle(sketch, "E5.12.15.3", {"center": v(-604.98, 401.01) * mm, "radius": 1.6 * mm});
            skCircle(sketch, "E5.12.16.0", {"center": v(-612.48, 396.01) * mm, "radius": 1.6 * mm});
            skCircle(sketch, "E5.12.16.1", {"center": v(-607.48, 396.01) * mm, "radius": 1.6 * mm});
            skCircle(sketch, "E5.12.16.2", {"center": v(-609.98, 391.01) * mm, "radius": 1.6 * mm});
            skCircle(sketch, "E5.12.16.3", {"center": v(-604.98, 391.01) * mm, "radius": 1.6 * mm});
            skCircle(sketch, "E5.12.17.0", {"center": v(-612.48, 386.01) * mm, "radius": 1.6 * mm});
            skCircle(sketch, "E5.12.17.1", {"center": v(-607.48, 386.01) * mm, "radius": 1.6 * mm});
            skCircle(sketch, "E5.12.17.2", {"center": v(-609.98, 381.01) * mm, "radius": 1.6 * mm});
            skCircle(sketch, "E5.12.17.3", {"center": v(-604.98, 381.01) * mm, "radius": 1.6 * mm});
            skCircle(sketch, "E5.12.18.0", {"center": v(-612.48, 376.01) * mm, "radius": 1.6 * mm});
            skCircle(sketch, "E5.12.18.1", {"center": v(-607.48, 376.01) * mm, "radius": 1.6 * mm});
            skCircle(sketch, "E5.12.18.2", {"center": v(-609.98, 371.01) * mm, "radius": 1.6 * mm});
            skCircle(sketch, "E5.12.18.3", {"center": v(-604.98, 371.01) * mm, "radius": 1.6 * mm});
            skCircle(sketch, "E5.12.19.0", {"center": v(-612.48, 366.01) * mm, "radius": 1.6 * mm});
            skCircle(sketch, "E5.12.19.1", {"center": v(-607.48, 366.01) * mm, "radius": 1.6 * mm});
            skCircle(sketch, "E5.12.19.2", {"center": v(-609.98, 361.01) * mm, "radius": 1.6 * mm});
            skCircle(sketch, "E5.12.19.3", {"center": v(-604.98, 361.01) * mm, "radius": 1.6 * mm});
            skCircle(sketch, "E5.12.20.0", {"center": v(-612.48, 356.01) * mm, "radius": 1.6 * mm});
            skCircle(sketch, "E5.12.20.1", {"center": v(-607.48, 356.01) * mm, "radius": 1.6 * mm});
            skCircle(sketch, "E5.12.20.2", {"center": v(-609.98, 351.01) * mm, "radius": 1.6 * mm});
            skCircle(sketch, "E5.12.20.3", {"center": v(-604.98, 351.01) * mm, "radius": 1.6 * mm});
            skCircle(sketch, "E5.12.21.0", {"center": v(-612.48, 346.01) * mm, "radius": 1.6 * mm});
            skCircle(sketch, "E5.12.21.1", {"center": v(-607.48, 346.01) * mm, "radius": 1.6 * mm});
            skCircle(sketch, "E5.12.21.2", {"center": v(-609.98, 341.01) * mm, "radius": 1.6 * mm});
            skCircle(sketch, "E5.12.21.3", {"center": v(-604.98, 341.01) * mm, "radius": 1.6 * mm});
            skCircle(sketch, "E5.12.22.0", {"center": v(-612.48, 336.01) * mm, "radius": 1.6 * mm});
            skCircle(sketch, "E5.12.22.1", {"center": v(-607.48, 336.01) * mm, "radius": 1.6 * mm});
            skCircle(sketch, "E5.12.22.2", {"center": v(-609.98, 331.01) * mm, "radius": 1.6 * mm});
            skCircle(sketch, "E5.12.22.3", {"center": v(-604.98, 331.01) * mm, "radius": 1.6 * mm});
            skCircle(sketch, "E5.12.23.0", {"center": v(-612.48, 326.01) * mm, "radius": 1.6 * mm});
            skCircle(sketch, "E5.12.23.1", {"center": v(-607.48, 326.01) * mm, "radius": 1.6 * mm});
            skCircle(sketch, "E5.12.23.2", {"center": v(-609.98, 321.01) * mm, "radius": 1.6 * mm});
            skCircle(sketch, "E5.12.23.3", {"center": v(-604.98, 321.01) * mm, "radius": 1.6 * mm});
            skCircle(sketch, "E5.12.24.0", {"center": v(-612.48, 316.01) * mm, "radius": 1.6 * mm});
            skCircle(sketch, "E5.12.24.1", {"center": v(-607.48, 316.01) * mm, "radius": 1.6 * mm});
            skCircle(sketch, "E5.12.24.2", {"center": v(-609.98, 311.01) * mm, "radius": 1.6 * mm});
            skCircle(sketch, "E5.12.24.3", {"center": v(-604.98, 311.01) * mm, "radius": 1.6 * mm});
            skCircle(sketch, "E5.12.25.0", {"center": v(-612.48, 306.01) * mm, "radius": 1.6 * mm});
            skCircle(sketch, "E5.12.25.1", {"center": v(-607.48, 306.01) * mm, "radius": 1.6 * mm});
            skCircle(sketch, "E5.12.25.2", {"center": v(-609.98, 301.01) * mm, "radius": 1.6 * mm});
            skCircle(sketch, "E5.12.25.3", {"center": v(-604.98, 301.01) * mm, "radius": 1.6 * mm});
            skCircle(sketch, "E5.12.26.0", {"center": v(-612.48, 296.01) * mm, "radius": 1.6 * mm});
            skCircle(sketch, "E5.12.26.1", {"center": v(-607.48, 296.01) * mm, "radius": 1.6 * mm});
            skCircle(sketch, "E5.12.26.2", {"center": v(-609.98, 291.01) * mm, "radius": 1.6 * mm});
            skCircle(sketch, "E5.12.26.3", {"center": v(-604.98, 291.01) * mm, "radius": 1.6 * mm});
            skCircle(sketch, "E5.12.27.0", {"center": v(-612.48, 286.01) * mm, "radius": 1.6 * mm});
            skCircle(sketch, "E5.12.27.1", {"center": v(-607.48, 286.01) * mm, "radius": 1.6 * mm});
            skCircle(sketch, "E5.12.27.2", {"center": v(-609.98, 281.01) * mm, "radius": 1.6 * mm});
            skCircle(sketch, "E5.12.27.3", {"center": v(-604.98, 281.01) * mm, "radius": 1.6 * mm});
            skCircle(sketch, "E5.12.28.0", {"center": v(-612.48, 276.01) * mm, "radius": 1.6 * mm});
            skCircle(sketch, "E5.12.28.1", {"center": v(-607.48, 276.01) * mm, "radius": 1.6 * mm});
            skCircle(sketch, "E5.12.28.2", {"center": v(-609.98, 271.01) * mm, "radius": 1.6 * mm});
            skCircle(sketch, "E5.12.28.3", {"center": v(-604.98, 271.01) * mm, "radius": 1.6 * mm});
            skCircle(sketch, "E5.12.29.0", {"center": v(-612.48, 266.01) * mm, "radius": 1.6 * mm});
            skCircle(sketch, "E5.12.29.1", {"center": v(-607.48, 266.01) * mm, "radius": 1.6 * mm});
            skCircle(sketch, "E5.12.29.2", {"center": v(-609.98, 261.01) * mm, "radius": 1.6 * mm});
            skCircle(sketch, "E5.12.29.3", {"center": v(-604.98, 261.01) * mm, "radius": 1.6 * mm});
            skCircle(sketch, "E5.12.30.0", {"center": v(-612.48, 256.01) * mm, "radius": 1.6 * mm});
            skCircle(sketch, "E5.12.30.1", {"center": v(-607.48, 256.01) * mm, "radius": 1.6 * mm});
            skCircle(sketch, "E5.12.30.2", {"center": v(-609.98, 251.01) * mm, "radius": 1.6 * mm});
            skCircle(sketch, "E5.12.30.3", {"center": v(-604.98, 251.01) * mm, "radius": 1.6 * mm});
            skCircle(sketch, "E5.12.31.0", {"center": v(-612.48, 246.01) * mm, "radius": 1.6 * mm});
            skCircle(sketch, "E5.12.31.1", {"center": v(-607.48, 246.01) * mm, "radius": 1.6 * mm});
            skCircle(sketch, "E5.12.31.2", {"center": v(-609.98, 241.01) * mm, "radius": 1.6 * mm});
            skCircle(sketch, "E5.12.31.3", {"center": v(-604.98, 241.01) * mm, "radius": 1.6 * mm});
            skCircle(sketch, "E5.12.32.0", {"center": v(-612.48, 236.01) * mm, "radius": 1.6 * mm});
            skCircle(sketch, "E5.12.32.1", {"center": v(-607.48, 236.01) * mm, "radius": 1.6 * mm});
            skCircle(sketch, "E5.12.32.2", {"center": v(-609.98, 231.01) * mm, "radius": 1.6 * mm});
            skCircle(sketch, "E5.12.32.3", {"center": v(-604.98, 231.01) * mm, "radius": 1.6 * mm});
            skCircle(sketch, "E5.12.33.0", {"center": v(-612.48, 226.01) * mm, "radius": 1.6 * mm});
            skCircle(sketch, "E5.12.33.1", {"center": v(-607.48, 226.01) * mm, "radius": 1.6 * mm});
            skCircle(sketch, "E5.12.33.2", {"center": v(-609.98, 221.01) * mm, "radius": 1.6 * mm});
            skCircle(sketch, "E5.12.33.3", {"center": v(-604.98, 221.01) * mm, "radius": 1.6 * mm});
            skCircle(sketch, "E5.12.34.0", {"center": v(-612.48, 216.01) * mm, "radius": 1.6 * mm});
            skCircle(sketch, "E5.12.34.1", {"center": v(-607.48, 216.01) * mm, "radius": 1.6 * mm});
            skCircle(sketch, "E5.12.34.2", {"center": v(-609.98, 211.01) * mm, "radius": 1.6 * mm});
            skCircle(sketch, "E5.12.34.3", {"center": v(-604.98, 211.01) * mm, "radius": 1.6 * mm});
            skCircle(sketch, "E5.12.35.0", {"center": v(-612.48, 206.01) * mm, "radius": 1.6 * mm});
            skCircle(sketch, "E5.12.35.1", {"center": v(-607.48, 206.01) * mm, "radius": 1.6 * mm});
            skCircle(sketch, "E5.12.35.2", {"center": v(-609.98, 201.01) * mm, "radius": 1.6 * mm});
            skCircle(sketch, "E5.12.35.3", {"center": v(-604.98, 201.01) * mm, "radius": 1.6 * mm});
            skCircle(sketch, "E5.12.36.0", {"center": v(-612.48, 196.01) * mm, "radius": 1.6 * mm});
            skCircle(sketch, "E5.12.36.1", {"center": v(-607.48, 196.01) * mm, "radius": 1.6 * mm});
            skCircle(sketch, "E5.12.36.2", {"center": v(-609.98, 191.01) * mm, "radius": 1.6 * mm});
            skCircle(sketch, "E5.12.36.3", {"center": v(-604.98, 191.01) * mm, "radius": 1.6 * mm});
            skCircle(sketch, "E5.12.37.0", {"center": v(-612.48, 186.01) * mm, "radius": 1.6 * mm});
            skCircle(sketch, "E5.12.37.1", {"center": v(-607.48, 186.01) * mm, "radius": 1.6 * mm});
            skCircle(sketch, "E5.12.37.2", {"center": v(-609.98, 181.01) * mm, "radius": 1.6 * mm});
            skCircle(sketch, "E5.12.37.3", {"center": v(-604.98, 181.01) * mm, "radius": 1.6 * mm});
            skCircle(sketch, "E5.12.38.0", {"center": v(-612.48, 176.01) * mm, "radius": 1.6 * mm});
            skCircle(sketch, "E5.12.38.1", {"center": v(-607.48, 176.01) * mm, "radius": 1.6 * mm});
            skCircle(sketch, "E5.12.38.2", {"center": v(-609.98, 171.01) * mm, "radius": 1.6 * mm});
            skCircle(sketch, "E5.12.38.3", {"center": v(-604.98, 171.01) * mm, "radius": 1.6 * mm});
            skCircle(sketch, "E5.12.39.0", {"center": v(-612.48, 166.01) * mm, "radius": 1.6 * mm});
            skCircle(sketch, "E5.12.39.1", {"center": v(-607.48, 166.01) * mm, "radius": 1.6 * mm});
            skCircle(sketch, "E5.12.39.2", {"center": v(-609.98, 161.01) * mm, "radius": 1.6 * mm});
            skCircle(sketch, "E5.12.39.3", {"center": v(-604.98, 161.01) * mm, "radius": 1.6 * mm});
            skCircle(sketch, "E5.12.40.0", {"center": v(-612.48, 156.01) * mm, "radius": 1.6 * mm});
            skCircle(sketch, "E5.12.40.1", {"center": v(-607.48, 156.01) * mm, "radius": 1.6 * mm});
            skCircle(sketch, "E5.12.40.2", {"center": v(-609.98, 151.01) * mm, "radius": 1.6 * mm});
            skCircle(sketch, "E5.12.40.3", {"center": v(-604.98, 151.01) * mm, "radius": 1.6 * mm});
            skCircle(sketch, "E5.12.41.0", {"center": v(-612.48, 146.01) * mm, "radius": 1.6 * mm});
            skCircle(sketch, "E5.12.41.1", {"center": v(-607.48, 146.01) * mm, "radius": 1.6 * mm});
            skCircle(sketch, "E5.12.41.2", {"center": v(-609.98, 141.01) * mm, "radius": 1.6 * mm});
            skCircle(sketch, "E5.12.41.3", {"center": v(-604.98, 141.01) * mm, "radius": 1.6 * mm});
            skCircle(sketch, "E5.12.42.0", {"center": v(-612.48, 136.01) * mm, "radius": 1.6 * mm});
            skCircle(sketch, "E5.12.42.1", {"center": v(-607.48, 136.01) * mm, "radius": 1.6 * mm});
            skCircle(sketch, "E5.12.42.2", {"center": v(-609.98, 131.01) * mm, "radius": 1.6 * mm});
            skCircle(sketch, "E5.12.42.3", {"center": v(-604.98, 131.01) * mm, "radius": 1.6 * mm});
            skCircle(sketch, "E5.12.43.0", {"center": v(-612.48, 126.01) * mm, "radius": 1.6 * mm});
            skCircle(sketch, "E5.12.43.1", {"center": v(-607.48, 126.01) * mm, "radius": 1.6 * mm});
            skCircle(sketch, "E5.12.43.2", {"center": v(-609.98, 121.01) * mm, "radius": 1.6 * mm});
            skCircle(sketch, "E5.12.43.3", {"center": v(-604.98, 121.01) * mm, "radius": 1.6 * mm});
            skCircle(sketch, "E5.12.44.0", {"center": v(-612.48, 116.01) * mm, "radius": 1.6 * mm});
            skCircle(sketch, "E5.12.44.1", {"center": v(-607.48, 116.01) * mm, "radius": 1.6 * mm});
            skCircle(sketch, "E5.12.44.2", {"center": v(-609.98, 111.01) * mm, "radius": 1.6 * mm});
            skCircle(sketch, "E5.12.44.3", {"center": v(-604.98, 111.01) * mm, "radius": 1.6 * mm});
            skCircle(sketch, "E5.12.45.0", {"center": v(-612.48, 106.01) * mm, "radius": 1.6 * mm});
            skCircle(sketch, "E5.12.45.1", {"center": v(-607.48, 106.01) * mm, "radius": 1.6 * mm});
            skCircle(sketch, "E5.12.45.2", {"center": v(-609.98, 101.01) * mm, "radius": 1.6 * mm});
            skCircle(sketch, "E5.12.45.3", {"center": v(-604.98, 101.01) * mm, "radius": 1.6 * mm});
            skCircle(sketch, "E5.12.46.0", {"center": v(-612.48, 96.01) * mm, "radius": 1.6 * mm});
            skCircle(sketch, "E5.12.46.1", {"center": v(-607.48, 96.01) * mm, "radius": 1.6 * mm});
            skCircle(sketch, "E5.12.46.2", {"center": v(-609.98, 91.01) * mm, "radius": 1.6 * mm});
            skCircle(sketch, "E5.12.46.3", {"center": v(-604.98, 91.01) * mm, "radius": 1.6 * mm});
            skCircle(sketch, "E5.12.47.0", {"center": v(-612.48, 86.01) * mm, "radius": 1.6 * mm});
            skCircle(sketch, "E5.12.47.1", {"center": v(-607.48, 86.01) * mm, "radius": 1.6 * mm});
            skCircle(sketch, "E5.12.47.2", {"center": v(-609.98, 81.01) * mm, "radius": 1.6 * mm});
            skCircle(sketch, "E5.12.47.3", {"center": v(-604.98, 81.01) * mm, "radius": 1.6 * mm});
            skCircle(sketch, "E5.12.48.0", {"center": v(-612.48, 76.01) * mm, "radius": 1.6 * mm});
            skCircle(sketch, "E5.12.48.1", {"center": v(-607.48, 76.01) * mm, "radius": 1.6 * mm});
            skCircle(sketch, "E5.12.48.2", {"center": v(-609.98, 71.01) * mm, "radius": 1.6 * mm});
            skCircle(sketch, "E5.12.48.3", {"center": v(-604.98, 71.01) * mm, "radius": 1.6 * mm});
            skCircle(sketch, "E5.12.49.0", {"center": v(-612.48, 66.01) * mm, "radius": 1.6 * mm});
            skCircle(sketch, "E5.12.49.1", {"center": v(-607.48, 66.01) * mm, "radius": 1.6 * mm});
            skCircle(sketch, "E5.12.49.2", {"center": v(-609.98, 61.01) * mm, "radius": 1.6 * mm});
            skCircle(sketch, "E5.12.49.3", {"center": v(-604.98, 61.01) * mm, "radius": 1.6 * mm});
            skCircle(sketch, "E5.13.0.0", {"center": v(-602.48, 556.01) * mm, "radius": 1.6 * mm});
            skCircle(sketch, "E5.13.0.1", {"center": v(-597.48, 556.01) * mm, "radius": 1.6 * mm});
            skCircle(sketch, "E5.13.0.2", {"center": v(-599.98, 551.01) * mm, "radius": 1.6 * mm});
            skCircle(sketch, "E5.13.0.3", {"center": v(-594.98, 551.01) * mm, "radius": 1.6 * mm});
            skCircle(sketch, "E5.13.1.0", {"center": v(-602.48, 546.01) * mm, "radius": 1.6 * mm});
            skCircle(sketch, "E5.13.1.1", {"center": v(-597.48, 546.01) * mm, "radius": 1.6 * mm});
            skCircle(sketch, "E5.13.1.2", {"center": v(-599.98, 541.01) * mm, "radius": 1.6 * mm});
            skCircle(sketch, "E5.13.1.3", {"center": v(-594.98, 541.01) * mm, "radius": 1.6 * mm});
            skCircle(sketch, "E5.13.2.0", {"center": v(-602.48, 536.01) * mm, "radius": 1.6 * mm});
            skCircle(sketch, "E5.13.2.1", {"center": v(-597.48, 536.01) * mm, "radius": 1.6 * mm});
            skCircle(sketch, "E5.13.2.2", {"center": v(-599.98, 531.01) * mm, "radius": 1.6 * mm});
            skCircle(sketch, "E5.13.2.3", {"center": v(-594.98, 531.01) * mm, "radius": 1.6 * mm});
            skCircle(sketch, "E5.13.3.0", {"center": v(-602.48, 526.01) * mm, "radius": 1.6 * mm});
            skCircle(sketch, "E5.13.3.1", {"center": v(-597.48, 526.01) * mm, "radius": 1.6 * mm});
            skCircle(sketch, "E5.13.3.2", {"center": v(-599.98, 521.01) * mm, "radius": 1.6 * mm});
            skCircle(sketch, "E5.13.3.3", {"center": v(-594.98, 521.01) * mm, "radius": 1.6 * mm});
            skCircle(sketch, "E5.13.4.0", {"center": v(-602.48, 516.01) * mm, "radius": 1.6 * mm});
            skCircle(sketch, "E5.13.4.1", {"center": v(-597.48, 516.01) * mm, "radius": 1.6 * mm});
            skCircle(sketch, "E5.13.4.2", {"center": v(-599.98, 511.01) * mm, "radius": 1.6 * mm});
            skCircle(sketch, "E5.13.4.3", {"center": v(-594.98, 511.01) * mm, "radius": 1.6 * mm});
            skCircle(sketch, "E5.13.5.0", {"center": v(-602.48, 506.01) * mm, "radius": 1.6 * mm});
            skCircle(sketch, "E5.13.5.1", {"center": v(-597.48, 506.01) * mm, "radius": 1.6 * mm});
            skCircle(sketch, "E5.13.5.2", {"center": v(-599.98, 501.01) * mm, "radius": 1.6 * mm});
            skCircle(sketch, "E5.13.5.3", {"center": v(-594.98, 501.01) * mm, "radius": 1.6 * mm});
            skCircle(sketch, "E5.13.6.0", {"center": v(-602.48, 496.01) * mm, "radius": 1.6 * mm});
            skCircle(sketch, "E5.13.6.1", {"center": v(-597.48, 496.01) * mm, "radius": 1.6 * mm});
            skCircle(sketch, "E5.13.6.2", {"center": v(-599.98, 491.01) * mm, "radius": 1.6 * mm});
            skCircle(sketch, "E5.13.6.3", {"center": v(-594.98, 491.01) * mm, "radius": 1.6 * mm});
            skCircle(sketch, "E5.13.7.0", {"center": v(-602.48, 486.01) * mm, "radius": 1.6 * mm});
            skCircle(sketch, "E5.13.7.1", {"center": v(-597.48, 486.01) * mm, "radius": 1.6 * mm});
            skCircle(sketch, "E5.13.7.2", {"center": v(-599.98, 481.01) * mm, "radius": 1.6 * mm});
            skCircle(sketch, "E5.13.7.3", {"center": v(-594.98, 481.01) * mm, "radius": 1.6 * mm});
            skCircle(sketch, "E5.13.8.0", {"center": v(-602.48, 476.01) * mm, "radius": 1.6 * mm});
            skCircle(sketch, "E5.13.8.1", {"center": v(-597.48, 476.01) * mm, "radius": 1.6 * mm});
            skCircle(sketch, "E5.13.8.2", {"center": v(-599.98, 471.01) * mm, "radius": 1.6 * mm});
            skCircle(sketch, "E5.13.8.3", {"center": v(-594.98, 471.01) * mm, "radius": 1.6 * mm});
            skCircle(sketch, "E5.13.9.0", {"center": v(-602.48, 466.01) * mm, "radius": 1.6 * mm});
            skCircle(sketch, "E5.13.9.1", {"center": v(-597.48, 466.01) * mm, "radius": 1.6 * mm});
            skCircle(sketch, "E5.13.9.2", {"center": v(-599.98, 461.01) * mm, "radius": 1.6 * mm});
            skCircle(sketch, "E5.13.9.3", {"center": v(-594.98, 461.01) * mm, "radius": 1.6 * mm});
            skCircle(sketch, "E5.13.10.0", {"center": v(-602.48, 456.01) * mm, "radius": 1.6 * mm});
            skCircle(sketch, "E5.13.10.1", {"center": v(-597.48, 456.01) * mm, "radius": 1.6 * mm});
            skCircle(sketch, "E5.13.10.2", {"center": v(-599.98, 451.01) * mm, "radius": 1.6 * mm});
            skCircle(sketch, "E5.13.10.3", {"center": v(-594.98, 451.01) * mm, "radius": 1.6 * mm});
            skCircle(sketch, "E5.13.11.0", {"center": v(-602.48, 446.01) * mm, "radius": 1.6 * mm});
            skCircle(sketch, "E5.13.11.1", {"center": v(-597.48, 446.01) * mm, "radius": 1.6 * mm});
            skCircle(sketch, "E5.13.11.2", {"center": v(-599.98, 441.01) * mm, "radius": 1.6 * mm});
            skCircle(sketch, "E5.13.11.3", {"center": v(-594.98, 441.01) * mm, "radius": 1.6 * mm});
            skCircle(sketch, "E5.13.12.0", {"center": v(-602.48, 436.01) * mm, "radius": 1.6 * mm});
            skCircle(sketch, "E5.13.12.1", {"center": v(-597.48, 436.01) * mm, "radius": 1.6 * mm});
            skCircle(sketch, "E5.13.12.2", {"center": v(-599.98, 431.01) * mm, "radius": 1.6 * mm});
            skCircle(sketch, "E5.13.12.3", {"center": v(-594.98, 431.01) * mm, "radius": 1.6 * mm});
            skCircle(sketch, "E5.13.13.0", {"center": v(-602.48, 426.01) * mm, "radius": 1.6 * mm});
            skCircle(sketch, "E5.13.13.1", {"center": v(-597.48, 426.01) * mm, "radius": 1.6 * mm});
            skCircle(sketch, "E5.13.13.2", {"center": v(-599.98, 421.01) * mm, "radius": 1.6 * mm});
            skCircle(sketch, "E5.13.13.3", {"center": v(-594.98, 421.01) * mm, "radius": 1.6 * mm});
            skCircle(sketch, "E5.13.14.0", {"center": v(-602.48, 416.01) * mm, "radius": 1.6 * mm});
            skCircle(sketch, "E5.13.14.1", {"center": v(-597.48, 416.01) * mm, "radius": 1.6 * mm});
            skCircle(sketch, "E5.13.14.2", {"center": v(-599.98, 411.01) * mm, "radius": 1.6 * mm});
            skCircle(sketch, "E5.13.14.3", {"center": v(-594.98, 411.01) * mm, "radius": 1.6 * mm});
            skCircle(sketch, "E5.13.15.0", {"center": v(-602.48, 406.01) * mm, "radius": 1.6 * mm});
            skCircle(sketch, "E5.13.15.1", {"center": v(-597.48, 406.01) * mm, "radius": 1.6 * mm});
            skCircle(sketch, "E5.13.15.2", {"center": v(-599.98, 401.01) * mm, "radius": 1.6 * mm});
            skCircle(sketch, "E5.13.15.3", {"center": v(-594.98, 401.01) * mm, "radius": 1.6 * mm});
            skCircle(sketch, "E5.13.16.0", {"center": v(-602.48, 396.01) * mm, "radius": 1.6 * mm});
            skCircle(sketch, "E5.13.16.1", {"center": v(-597.48, 396.01) * mm, "radius": 1.6 * mm});
            skCircle(sketch, "E5.13.16.2", {"center": v(-599.98, 391.01) * mm, "radius": 1.6 * mm});
            skCircle(sketch, "E5.13.16.3", {"center": v(-594.98, 391.01) * mm, "radius": 1.6 * mm});
            skCircle(sketch, "E5.13.17.0", {"center": v(-602.48, 386.01) * mm, "radius": 1.6 * mm});
            skCircle(sketch, "E5.13.17.1", {"center": v(-597.48, 386.01) * mm, "radius": 1.6 * mm});
            skCircle(sketch, "E5.13.17.2", {"center": v(-599.98, 381.01) * mm, "radius": 1.6 * mm});
            skCircle(sketch, "E5.13.17.3", {"center": v(-594.98, 381.01) * mm, "radius": 1.6 * mm});
            skCircle(sketch, "E5.13.18.0", {"center": v(-602.48, 376.01) * mm, "radius": 1.6 * mm});
            skCircle(sketch, "E5.13.18.1", {"center": v(-597.48, 376.01) * mm, "radius": 1.6 * mm});
            skCircle(sketch, "E5.13.18.2", {"center": v(-599.98, 371.01) * mm, "radius": 1.6 * mm});
            skCircle(sketch, "E5.13.18.3", {"center": v(-594.98, 371.01) * mm, "radius": 1.6 * mm});
            skCircle(sketch, "E5.13.19.0", {"center": v(-602.48, 366.01) * mm, "radius": 1.6 * mm});
            skCircle(sketch, "E5.13.19.1", {"center": v(-597.48, 366.01) * mm, "radius": 1.6 * mm});
            skCircle(sketch, "E5.13.19.2", {"center": v(-599.98, 361.01) * mm, "radius": 1.6 * mm});
            skCircle(sketch, "E5.13.19.3", {"center": v(-594.98, 361.01) * mm, "radius": 1.6 * mm});
            skCircle(sketch, "E5.13.20.0", {"center": v(-602.48, 356.01) * mm, "radius": 1.6 * mm});
            skCircle(sketch, "E5.13.20.1", {"center": v(-597.48, 356.01) * mm, "radius": 1.6 * mm});
            skCircle(sketch, "E5.13.20.2", {"center": v(-599.98, 351.01) * mm, "radius": 1.6 * mm});
            skCircle(sketch, "E5.13.20.3", {"center": v(-594.98, 351.01) * mm, "radius": 1.6 * mm});
            skCircle(sketch, "E5.13.21.0", {"center": v(-602.48, 346.01) * mm, "radius": 1.6 * mm});
            skCircle(sketch, "E5.13.21.1", {"center": v(-597.48, 346.01) * mm, "radius": 1.6 * mm});
            skCircle(sketch, "E5.13.21.2", {"center": v(-599.98, 341.01) * mm, "radius": 1.6 * mm});
            skCircle(sketch, "E5.13.21.3", {"center": v(-594.98, 341.01) * mm, "radius": 1.6 * mm});
            skCircle(sketch, "E5.13.22.0", {"center": v(-602.48, 336.01) * mm, "radius": 1.6 * mm});
            skCircle(sketch, "E5.13.22.1", {"center": v(-597.48, 336.01) * mm, "radius": 1.6 * mm});
            skCircle(sketch, "E5.13.22.2", {"center": v(-599.98, 331.01) * mm, "radius": 1.6 * mm});
            skCircle(sketch, "E5.13.22.3", {"center": v(-594.98, 331.01) * mm, "radius": 1.6 * mm});
            skCircle(sketch, "E5.13.23.0", {"center": v(-602.48, 326.01) * mm, "radius": 1.6 * mm});
            skCircle(sketch, "E5.13.23.1", {"center": v(-597.48, 326.01) * mm, "radius": 1.6 * mm});
            skCircle(sketch, "E5.13.23.2", {"center": v(-599.98, 321.01) * mm, "radius": 1.6 * mm});
            skCircle(sketch, "E5.13.23.3", {"center": v(-594.98, 321.01) * mm, "radius": 1.6 * mm});
            skCircle(sketch, "E5.13.24.0", {"center": v(-602.48, 316.01) * mm, "radius": 1.6 * mm});
            skCircle(sketch, "E5.13.24.1", {"center": v(-597.48, 316.01) * mm, "radius": 1.6 * mm});
            skCircle(sketch, "E5.13.24.2", {"center": v(-599.98, 311.01) * mm, "radius": 1.6 * mm});
            skCircle(sketch, "E5.13.24.3", {"center": v(-594.98, 311.01) * mm, "radius": 1.6 * mm});
            skCircle(sketch, "E5.13.25.0", {"center": v(-602.48, 306.01) * mm, "radius": 1.6 * mm});
            skCircle(sketch, "E5.13.25.1", {"center": v(-597.48, 306.01) * mm, "radius": 1.6 * mm});
            skCircle(sketch, "E5.13.25.2", {"center": v(-599.98, 301.01) * mm, "radius": 1.6 * mm});
            skCircle(sketch, "E5.13.25.3", {"center": v(-594.98, 301.01) * mm, "radius": 1.6 * mm});
            skCircle(sketch, "E5.13.26.0", {"center": v(-602.48, 296.01) * mm, "radius": 1.6 * mm});
            skCircle(sketch, "E5.13.26.1", {"center": v(-597.48, 296.01) * mm, "radius": 1.6 * mm});
            skCircle(sketch, "E5.13.26.2", {"center": v(-599.98, 291.01) * mm, "radius": 1.6 * mm});
            skCircle(sketch, "E5.13.26.3", {"center": v(-594.98, 291.01) * mm, "radius": 1.6 * mm});
            skCircle(sketch, "E5.13.27.0", {"center": v(-602.48, 286.01) * mm, "radius": 1.6 * mm});
            skCircle(sketch, "E5.13.27.1", {"center": v(-597.48, 286.01) * mm, "radius": 1.6 * mm});
            skCircle(sketch, "E5.13.27.2", {"center": v(-599.98, 281.01) * mm, "radius": 1.6 * mm});
            skCircle(sketch, "E5.13.27.3", {"center": v(-594.98, 281.01) * mm, "radius": 1.6 * mm});
            skCircle(sketch, "E5.13.28.0", {"center": v(-602.48, 276.01) * mm, "radius": 1.6 * mm});
            skCircle(sketch, "E5.13.28.1", {"center": v(-597.48, 276.01) * mm, "radius": 1.6 * mm});
            skCircle(sketch, "E5.13.28.2", {"center": v(-599.98, 271.01) * mm, "radius": 1.6 * mm});
            skCircle(sketch, "E5.13.28.3", {"center": v(-594.98, 271.01) * mm, "radius": 1.6 * mm});
            skCircle(sketch, "E5.13.29.0", {"center": v(-602.48, 266.01) * mm, "radius": 1.6 * mm});
            skCircle(sketch, "E5.13.29.1", {"center": v(-597.48, 266.01) * mm, "radius": 1.6 * mm});
            skCircle(sketch, "E5.13.29.2", {"center": v(-599.98, 261.01) * mm, "radius": 1.6 * mm});
            skCircle(sketch, "E5.13.29.3", {"center": v(-594.98, 261.01) * mm, "radius": 1.6 * mm});
            skCircle(sketch, "E5.13.30.0", {"center": v(-602.48, 256.01) * mm, "radius": 1.6 * mm});
            skCircle(sketch, "E5.13.30.1", {"center": v(-597.48, 256.01) * mm, "radius": 1.6 * mm});
            skCircle(sketch, "E5.13.30.2", {"center": v(-599.98, 251.01) * mm, "radius": 1.6 * mm});
            skCircle(sketch, "E5.13.30.3", {"center": v(-594.98, 251.01) * mm, "radius": 1.6 * mm});
            skCircle(sketch, "E5.13.31.0", {"center": v(-602.48, 246.01) * mm, "radius": 1.6 * mm});
            skCircle(sketch, "E5.13.31.1", {"center": v(-597.48, 246.01) * mm, "radius": 1.6 * mm});
            skCircle(sketch, "E5.13.31.2", {"center": v(-599.98, 241.01) * mm, "radius": 1.6 * mm});
            skCircle(sketch, "E5.13.31.3", {"center": v(-594.98, 241.01) * mm, "radius": 1.6 * mm});
            skCircle(sketch, "E5.13.32.0", {"center": v(-602.48, 236.01) * mm, "radius": 1.6 * mm});
            skCircle(sketch, "E5.13.32.1", {"center": v(-597.48, 236.01) * mm, "radius": 1.6 * mm});
            skCircle(sketch, "E5.13.32.2", {"center": v(-599.98, 231.01) * mm, "radius": 1.6 * mm});
            skCircle(sketch, "E5.13.32.3", {"center": v(-594.98, 231.01) * mm, "radius": 1.6 * mm});
            skCircle(sketch, "E5.13.33.0", {"center": v(-602.48, 226.01) * mm, "radius": 1.6 * mm});
            skCircle(sketch, "E5.13.33.1", {"center": v(-597.48, 226.01) * mm, "radius": 1.6 * mm});
            skCircle(sketch, "E5.13.33.2", {"center": v(-599.98, 221.01) * mm, "radius": 1.6 * mm});
            skCircle(sketch, "E5.13.33.3", {"center": v(-594.98, 221.01) * mm, "radius": 1.6 * mm});
            skCircle(sketch, "E5.13.34.0", {"center": v(-602.48, 216.01) * mm, "radius": 1.6 * mm});
            skCircle(sketch, "E5.13.34.1", {"center": v(-597.48, 216.01) * mm, "radius": 1.6 * mm});
            skCircle(sketch, "E5.13.34.2", {"center": v(-599.98, 211.01) * mm, "radius": 1.6 * mm});
            skCircle(sketch, "E5.13.34.3", {"center": v(-594.98, 211.01) * mm, "radius": 1.6 * mm});
            skCircle(sketch, "E5.13.35.0", {"center": v(-602.48, 206.01) * mm, "radius": 1.6 * mm});
            skCircle(sketch, "E5.13.35.1", {"center": v(-597.48, 206.01) * mm, "radius": 1.6 * mm});
            skCircle(sketch, "E5.13.35.2", {"center": v(-599.98, 201.01) * mm, "radius": 1.6 * mm});
            skCircle(sketch, "E5.13.35.3", {"center": v(-594.98, 201.01) * mm, "radius": 1.6 * mm});
            skCircle(sketch, "E5.13.36.0", {"center": v(-602.48, 196.01) * mm, "radius": 1.6 * mm});
            skCircle(sketch, "E5.13.36.1", {"center": v(-597.48, 196.01) * mm, "radius": 1.6 * mm});
            skCircle(sketch, "E5.13.36.2", {"center": v(-599.98, 191.01) * mm, "radius": 1.6 * mm});
            skCircle(sketch, "E5.13.36.3", {"center": v(-594.98, 191.01) * mm, "radius": 1.6 * mm});
            skCircle(sketch, "E5.13.37.0", {"center": v(-602.48, 186.01) * mm, "radius": 1.6 * mm});
            skCircle(sketch, "E5.13.37.1", {"center": v(-597.48, 186.01) * mm, "radius": 1.6 * mm});
            skCircle(sketch, "E5.13.37.2", {"center": v(-599.98, 181.01) * mm, "radius": 1.6 * mm});
            skCircle(sketch, "E5.13.37.3", {"center": v(-594.98, 181.01) * mm, "radius": 1.6 * mm});
            skCircle(sketch, "E5.13.38.0", {"center": v(-602.48, 176.01) * mm, "radius": 1.6 * mm});
            skCircle(sketch, "E5.13.38.1", {"center": v(-597.48, 176.01) * mm, "radius": 1.6 * mm});
            skCircle(sketch, "E5.13.38.2", {"center": v(-599.98, 171.01) * mm, "radius": 1.6 * mm});
            skCircle(sketch, "E5.13.38.3", {"center": v(-594.98, 171.01) * mm, "radius": 1.6 * mm});
            skCircle(sketch, "E5.13.39.0", {"center": v(-602.48, 166.01) * mm, "radius": 1.6 * mm});
            skCircle(sketch, "E5.13.39.1", {"center": v(-597.48, 166.01) * mm, "radius": 1.6 * mm});
            skCircle(sketch, "E5.13.39.2", {"center": v(-599.98, 161.01) * mm, "radius": 1.6 * mm});
            skCircle(sketch, "E5.13.39.3", {"center": v(-594.98, 161.01) * mm, "radius": 1.6 * mm});
            skCircle(sketch, "E5.13.40.0", {"center": v(-602.48, 156.01) * mm, "radius": 1.6 * mm});
            skCircle(sketch, "E5.13.40.1", {"center": v(-597.48, 156.01) * mm, "radius": 1.6 * mm});
            skCircle(sketch, "E5.13.40.2", {"center": v(-599.98, 151.01) * mm, "radius": 1.6 * mm});
            skCircle(sketch, "E5.13.40.3", {"center": v(-594.98, 151.01) * mm, "radius": 1.6 * mm});
            skCircle(sketch, "E5.13.41.0", {"center": v(-602.48, 146.01) * mm, "radius": 1.6 * mm});
            skCircle(sketch, "E5.13.41.1", {"center": v(-597.48, 146.01) * mm, "radius": 1.6 * mm});
            skCircle(sketch, "E5.13.41.2", {"center": v(-599.98, 141.01) * mm, "radius": 1.6 * mm});
            skCircle(sketch, "E5.13.41.3", {"center": v(-594.98, 141.01) * mm, "radius": 1.6 * mm});
            skCircle(sketch, "E5.13.42.0", {"center": v(-602.48, 136.01) * mm, "radius": 1.6 * mm});
            skCircle(sketch, "E5.13.42.1", {"center": v(-597.48, 136.01) * mm, "radius": 1.6 * mm});
            skCircle(sketch, "E5.13.42.2", {"center": v(-599.98, 131.01) * mm, "radius": 1.6 * mm});
            skCircle(sketch, "E5.13.42.3", {"center": v(-594.98, 131.01) * mm, "radius": 1.6 * mm});
            skCircle(sketch, "E5.13.43.0", {"center": v(-602.48, 126.01) * mm, "radius": 1.6 * mm});
            skCircle(sketch, "E5.13.43.1", {"center": v(-597.48, 126.01) * mm, "radius": 1.6 * mm});
            skCircle(sketch, "E5.13.43.2", {"center": v(-599.98, 121.01) * mm, "radius": 1.6 * mm});
            skCircle(sketch, "E5.13.43.3", {"center": v(-594.98, 121.01) * mm, "radius": 1.6 * mm});
            skCircle(sketch, "E5.13.44.0", {"center": v(-602.48, 116.01) * mm, "radius": 1.6 * mm});
            skCircle(sketch, "E5.13.44.1", {"center": v(-597.48, 116.01) * mm, "radius": 1.6 * mm});
            skCircle(sketch, "E5.13.44.2", {"center": v(-599.98, 111.01) * mm, "radius": 1.6 * mm});
            skCircle(sketch, "E5.13.44.3", {"center": v(-594.98, 111.01) * mm, "radius": 1.6 * mm});
            skCircle(sketch, "E5.13.45.0", {"center": v(-602.48, 106.01) * mm, "radius": 1.6 * mm});
            skCircle(sketch, "E5.13.45.1", {"center": v(-597.48, 106.01) * mm, "radius": 1.6 * mm});
            skCircle(sketch, "E5.13.45.2", {"center": v(-599.98, 101.01) * mm, "radius": 1.6 * mm});
            skCircle(sketch, "E5.13.45.3", {"center": v(-594.98, 101.01) * mm, "radius": 1.6 * mm});
            skCircle(sketch, "E5.13.46.0", {"center": v(-602.48, 96.01) * mm, "radius": 1.6 * mm});
            skCircle(sketch, "E5.13.46.1", {"center": v(-597.48, 96.01) * mm, "radius": 1.6 * mm});
            skCircle(sketch, "E5.13.46.2", {"center": v(-599.98, 91.01) * mm, "radius": 1.6 * mm});
            skCircle(sketch, "E5.13.46.3", {"center": v(-594.98, 91.01) * mm, "radius": 1.6 * mm});
            skCircle(sketch, "E5.13.47.0", {"center": v(-602.48, 86.01) * mm, "radius": 1.6 * mm});
            skCircle(sketch, "E5.13.47.1", {"center": v(-597.48, 86.01) * mm, "radius": 1.6 * mm});
            skCircle(sketch, "E5.13.47.2", {"center": v(-599.98, 81.01) * mm, "radius": 1.6 * mm});
            skCircle(sketch, "E5.13.47.3", {"center": v(-594.98, 81.01) * mm, "radius": 1.6 * mm});
            skCircle(sketch, "E5.13.48.0", {"center": v(-602.48, 76.01) * mm, "radius": 1.6 * mm});
            skCircle(sketch, "E5.13.48.1", {"center": v(-597.48, 76.01) * mm, "radius": 1.6 * mm});
            skCircle(sketch, "E5.13.48.2", {"center": v(-599.98, 71.01) * mm, "radius": 1.6 * mm});
            skCircle(sketch, "E5.13.48.3", {"center": v(-594.98, 71.01) * mm, "radius": 1.6 * mm});
            skCircle(sketch, "E5.13.49.0", {"center": v(-602.48, 66.01) * mm, "radius": 1.6 * mm});
            skCircle(sketch, "E5.13.49.1", {"center": v(-597.48, 66.01) * mm, "radius": 1.6 * mm});
            skCircle(sketch, "E5.13.49.2", {"center": v(-599.98, 61.01) * mm, "radius": 1.6 * mm});
            skCircle(sketch, "E5.13.49.3", {"center": v(-594.98, 61.01) * mm, "radius": 1.6 * mm});
            skCircle(sketch, "E5.14.0.0", {"center": v(-592.48, 556.01) * mm, "radius": 1.6 * mm});
            skCircle(sketch, "E5.14.0.1", {"center": v(-587.48, 556.01) * mm, "radius": 1.6 * mm});
            skCircle(sketch, "E5.14.0.2", {"center": v(-589.98, 551.01) * mm, "radius": 1.6 * mm});
            skCircle(sketch, "E5.14.0.3", {"center": v(-584.98, 551.01) * mm, "radius": 1.6 * mm});
            skCircle(sketch, "E5.14.1.0", {"center": v(-592.48, 546.01) * mm, "radius": 1.6 * mm});
            skCircle(sketch, "E5.14.1.1", {"center": v(-587.48, 546.01) * mm, "radius": 1.6 * mm});
            skCircle(sketch, "E5.14.1.2", {"center": v(-589.98, 541.01) * mm, "radius": 1.6 * mm});
            skCircle(sketch, "E5.14.1.3", {"center": v(-584.98, 541.01) * mm, "radius": 1.6 * mm});
            skCircle(sketch, "E5.14.2.0", {"center": v(-592.48, 536.01) * mm, "radius": 1.6 * mm});
            skCircle(sketch, "E5.14.2.1", {"center": v(-587.48, 536.01) * mm, "radius": 1.6 * mm});
            skCircle(sketch, "E5.14.2.2", {"center": v(-589.98, 531.01) * mm, "radius": 1.6 * mm});
            skCircle(sketch, "E5.14.2.3", {"center": v(-584.98, 531.01) * mm, "radius": 1.6 * mm});
            skCircle(sketch, "E5.14.3.0", {"center": v(-592.48, 526.01) * mm, "radius": 1.6 * mm});
            skCircle(sketch, "E5.14.3.1", {"center": v(-587.48, 526.01) * mm, "radius": 1.6 * mm});
            skCircle(sketch, "E5.14.3.2", {"center": v(-589.98, 521.01) * mm, "radius": 1.6 * mm});
            skCircle(sketch, "E5.14.3.3", {"center": v(-584.98, 521.01) * mm, "radius": 1.6 * mm});
            skCircle(sketch, "E5.14.4.0", {"center": v(-592.48, 516.01) * mm, "radius": 1.6 * mm});
            skCircle(sketch, "E5.14.4.1", {"center": v(-587.48, 516.01) * mm, "radius": 1.6 * mm});
            skCircle(sketch, "E5.14.4.2", {"center": v(-589.98, 511.01) * mm, "radius": 1.6 * mm});
            skCircle(sketch, "E5.14.4.3", {"center": v(-584.98, 511.01) * mm, "radius": 1.6 * mm});
            skCircle(sketch, "E5.14.5.0", {"center": v(-592.48, 506.01) * mm, "radius": 1.6 * mm});
            skCircle(sketch, "E5.14.5.1", {"center": v(-587.48, 506.01) * mm, "radius": 1.6 * mm});
            skCircle(sketch, "E5.14.5.2", {"center": v(-589.98, 501.01) * mm, "radius": 1.6 * mm});
            skCircle(sketch, "E5.14.5.3", {"center": v(-584.98, 501.01) * mm, "radius": 1.6 * mm});
            skCircle(sketch, "E5.14.6.0", {"center": v(-592.48, 496.01) * mm, "radius": 1.6 * mm});
            skCircle(sketch, "E5.14.6.1", {"center": v(-587.48, 496.01) * mm, "radius": 1.6 * mm});
            skCircle(sketch, "E5.14.6.2", {"center": v(-589.98, 491.01) * mm, "radius": 1.6 * mm});
            skCircle(sketch, "E5.14.6.3", {"center": v(-584.98, 491.01) * mm, "radius": 1.6 * mm});
            skCircle(sketch, "E5.14.7.0", {"center": v(-592.48, 486.01) * mm, "radius": 1.6 * mm});
            skCircle(sketch, "E5.14.7.1", {"center": v(-587.48, 486.01) * mm, "radius": 1.6 * mm});
            skCircle(sketch, "E5.14.7.2", {"center": v(-589.98, 481.01) * mm, "radius": 1.6 * mm});
            skCircle(sketch, "E5.14.7.3", {"center": v(-584.98, 481.01) * mm, "radius": 1.6 * mm});
            skCircle(sketch, "E5.14.8.0", {"center": v(-592.48, 476.01) * mm, "radius": 1.6 * mm});
            skCircle(sketch, "E5.14.8.1", {"center": v(-587.48, 476.01) * mm, "radius": 1.6 * mm});
            skCircle(sketch, "E5.14.8.2", {"center": v(-589.98, 471.01) * mm, "radius": 1.6 * mm});
            skCircle(sketch, "E5.14.8.3", {"center": v(-584.98, 471.01) * mm, "radius": 1.6 * mm});
            skCircle(sketch, "E5.14.9.0", {"center": v(-592.48, 466.01) * mm, "radius": 1.6 * mm});
            skCircle(sketch, "E5.14.9.1", {"center": v(-587.48, 466.01) * mm, "radius": 1.6 * mm});
            skCircle(sketch, "E5.14.9.2", {"center": v(-589.98, 461.01) * mm, "radius": 1.6 * mm});
            skCircle(sketch, "E5.14.9.3", {"center": v(-584.98, 461.01) * mm, "radius": 1.6 * mm});
            skCircle(sketch, "E5.14.10.0", {"center": v(-592.48, 456.01) * mm, "radius": 1.6 * mm});
            skCircle(sketch, "E5.14.10.1", {"center": v(-587.48, 456.01) * mm, "radius": 1.6 * mm});
            skCircle(sketch, "E5.14.10.2", {"center": v(-589.98, 451.01) * mm, "radius": 1.6 * mm});
            skCircle(sketch, "E5.14.10.3", {"center": v(-584.98, 451.01) * mm, "radius": 1.6 * mm});
            skCircle(sketch, "E5.14.11.0", {"center": v(-592.48, 446.01) * mm, "radius": 1.6 * mm});
            skCircle(sketch, "E5.14.11.1", {"center": v(-587.48, 446.01) * mm, "radius": 1.6 * mm});
            skCircle(sketch, "E5.14.11.2", {"center": v(-589.98, 441.01) * mm, "radius": 1.6 * mm});
            skCircle(sketch, "E5.14.11.3", {"center": v(-584.98, 441.01) * mm, "radius": 1.6 * mm});
            skCircle(sketch, "E5.14.12.0", {"center": v(-592.48, 436.01) * mm, "radius": 1.6 * mm});
            skCircle(sketch, "E5.14.12.1", {"center": v(-587.48, 436.01) * mm, "radius": 1.6 * mm});
            skCircle(sketch, "E5.14.12.2", {"center": v(-589.98, 431.01) * mm, "radius": 1.6 * mm});
            skCircle(sketch, "E5.14.12.3", {"center": v(-584.98, 431.01) * mm, "radius": 1.6 * mm});
            skCircle(sketch, "E5.14.13.0", {"center": v(-592.48, 426.01) * mm, "radius": 1.6 * mm});
            skCircle(sketch, "E5.14.13.1", {"center": v(-587.48, 426.01) * mm, "radius": 1.6 * mm});
            skCircle(sketch, "E5.14.13.2", {"center": v(-589.98, 421.01) * mm, "radius": 1.6 * mm});
            skCircle(sketch, "E5.14.13.3", {"center": v(-584.98, 421.01) * mm, "radius": 1.6 * mm});
            skCircle(sketch, "E5.14.14.0", {"center": v(-592.48, 416.01) * mm, "radius": 1.6 * mm});
            skCircle(sketch, "E5.14.14.1", {"center": v(-587.48, 416.01) * mm, "radius": 1.6 * mm});
            skCircle(sketch, "E5.14.14.2", {"center": v(-589.98, 411.01) * mm, "radius": 1.6 * mm});
            skCircle(sketch, "E5.14.14.3", {"center": v(-584.98, 411.01) * mm, "radius": 1.6 * mm});
            skCircle(sketch, "E5.14.15.0", {"center": v(-592.48, 406.01) * mm, "radius": 1.6 * mm});
            skCircle(sketch, "E5.14.15.1", {"center": v(-587.48, 406.01) * mm, "radius": 1.6 * mm});
            skCircle(sketch, "E5.14.15.2", {"center": v(-589.98, 401.01) * mm, "radius": 1.6 * mm});
            skCircle(sketch, "E5.14.15.3", {"center": v(-584.98, 401.01) * mm, "radius": 1.6 * mm});
            skCircle(sketch, "E5.14.16.0", {"center": v(-592.48, 396.01) * mm, "radius": 1.6 * mm});
            skCircle(sketch, "E5.14.16.1", {"center": v(-587.48, 396.01) * mm, "radius": 1.6 * mm});
            skCircle(sketch, "E5.14.16.2", {"center": v(-589.98, 391.01) * mm, "radius": 1.6 * mm});
            skCircle(sketch, "E5.14.16.3", {"center": v(-584.98, 391.01) * mm, "radius": 1.6 * mm});
            skCircle(sketch, "E5.14.17.0", {"center": v(-592.48, 386.01) * mm, "radius": 1.6 * mm});
            skCircle(sketch, "E5.14.17.1", {"center": v(-587.48, 386.01) * mm, "radius": 1.6 * mm});
            skCircle(sketch, "E5.14.17.2", {"center": v(-589.98, 381.01) * mm, "radius": 1.6 * mm});
            skCircle(sketch, "E5.14.17.3", {"center": v(-584.98, 381.01) * mm, "radius": 1.6 * mm});
            skCircle(sketch, "E5.14.18.0", {"center": v(-592.48, 376.01) * mm, "radius": 1.6 * mm});
            skCircle(sketch, "E5.14.18.1", {"center": v(-587.48, 376.01) * mm, "radius": 1.6 * mm});
            skCircle(sketch, "E5.14.18.2", {"center": v(-589.98, 371.01) * mm, "radius": 1.6 * mm});
            skCircle(sketch, "E5.14.18.3", {"center": v(-584.98, 371.01) * mm, "radius": 1.6 * mm});
            skCircle(sketch, "E5.14.19.0", {"center": v(-592.48, 366.01) * mm, "radius": 1.6 * mm});
            skCircle(sketch, "E5.14.19.1", {"center": v(-587.48, 366.01) * mm, "radius": 1.6 * mm});
            skCircle(sketch, "E5.14.19.2", {"center": v(-589.98, 361.01) * mm, "radius": 1.6 * mm});
            skCircle(sketch, "E5.14.19.3", {"center": v(-584.98, 361.01) * mm, "radius": 1.6 * mm});
            skCircle(sketch, "E5.14.20.0", {"center": v(-592.48, 356.01) * mm, "radius": 1.6 * mm});
            skCircle(sketch, "E5.14.20.1", {"center": v(-587.48, 356.01) * mm, "radius": 1.6 * mm});
            skCircle(sketch, "E5.14.20.2", {"center": v(-589.98, 351.01) * mm, "radius": 1.6 * mm});
            skCircle(sketch, "E5.14.20.3", {"center": v(-584.98, 351.01) * mm, "radius": 1.6 * mm});
            skCircle(sketch, "E5.14.21.0", {"center": v(-592.48, 346.01) * mm, "radius": 1.6 * mm});
            skCircle(sketch, "E5.14.21.1", {"center": v(-587.48, 346.01) * mm, "radius": 1.6 * mm});
            skCircle(sketch, "E5.14.21.2", {"center": v(-589.98, 341.01) * mm, "radius": 1.6 * mm});
            skCircle(sketch, "E5.14.21.3", {"center": v(-584.98, 341.01) * mm, "radius": 1.6 * mm});
            skCircle(sketch, "E5.14.22.0", {"center": v(-592.48, 336.01) * mm, "radius": 1.6 * mm});
            skCircle(sketch, "E5.14.22.1", {"center": v(-587.48, 336.01) * mm, "radius": 1.6 * mm});
            skCircle(sketch, "E5.14.22.2", {"center": v(-589.98, 331.01) * mm, "radius": 1.6 * mm});
            skCircle(sketch, "E5.14.22.3", {"center": v(-584.98, 331.01) * mm, "radius": 1.6 * mm});
            skCircle(sketch, "E5.14.23.0", {"center": v(-592.48, 326.01) * mm, "radius": 1.6 * mm});
            skCircle(sketch, "E5.14.23.1", {"center": v(-587.48, 326.01) * mm, "radius": 1.6 * mm});
            skCircle(sketch, "E5.14.23.2", {"center": v(-589.98, 321.01) * mm, "radius": 1.6 * mm});
            skCircle(sketch, "E5.14.23.3", {"center": v(-584.98, 321.01) * mm, "radius": 1.6 * mm});
            skCircle(sketch, "E5.14.24.0", {"center": v(-592.48, 316.01) * mm, "radius": 1.6 * mm});
            skCircle(sketch, "E5.14.24.1", {"center": v(-587.48, 316.01) * mm, "radius": 1.6 * mm});
            skCircle(sketch, "E5.14.24.2", {"center": v(-589.98, 311.01) * mm, "radius": 1.6 * mm});
            skCircle(sketch, "E5.14.24.3", {"center": v(-584.98, 311.01) * mm, "radius": 1.6 * mm});
            skCircle(sketch, "E5.14.25.0", {"center": v(-592.48, 306.01) * mm, "radius": 1.6 * mm});
            skCircle(sketch, "E5.14.25.1", {"center": v(-587.48, 306.01) * mm, "radius": 1.6 * mm});
            skCircle(sketch, "E5.14.25.2", {"center": v(-589.98, 301.01) * mm, "radius": 1.6 * mm});
            skCircle(sketch, "E5.14.25.3", {"center": v(-584.98, 301.01) * mm, "radius": 1.6 * mm});
            skCircle(sketch, "E5.14.26.0", {"center": v(-592.48, 296.01) * mm, "radius": 1.6 * mm});
            skCircle(sketch, "E5.14.26.1", {"center": v(-587.48, 296.01) * mm, "radius": 1.6 * mm});
            skCircle(sketch, "E5.14.26.2", {"center": v(-589.98, 291.01) * mm, "radius": 1.6 * mm});
            skCircle(sketch, "E5.14.26.3", {"center": v(-584.98, 291.01) * mm, "radius": 1.6 * mm});
            skCircle(sketch, "E5.14.27.0", {"center": v(-592.48, 286.01) * mm, "radius": 1.6 * mm});
            skCircle(sketch, "E5.14.27.1", {"center": v(-587.48, 286.01) * mm, "radius": 1.6 * mm});
            skCircle(sketch, "E5.14.27.2", {"center": v(-589.98, 281.01) * mm, "radius": 1.6 * mm});
            skCircle(sketch, "E5.14.27.3", {"center": v(-584.98, 281.01) * mm, "radius": 1.6 * mm});
            skCircle(sketch, "E5.14.28.0", {"center": v(-592.48, 276.01) * mm, "radius": 1.6 * mm});
            skCircle(sketch, "E5.14.28.1", {"center": v(-587.48, 276.01) * mm, "radius": 1.6 * mm});
            skCircle(sketch, "E5.14.28.2", {"center": v(-589.98, 271.01) * mm, "radius": 1.6 * mm});
            skCircle(sketch, "E5.14.28.3", {"center": v(-584.98, 271.01) * mm, "radius": 1.6 * mm});
            skCircle(sketch, "E5.14.29.0", {"center": v(-592.48, 266.01) * mm, "radius": 1.6 * mm});
            skCircle(sketch, "E5.14.29.1", {"center": v(-587.48, 266.01) * mm, "radius": 1.6 * mm});
            skCircle(sketch, "E5.14.29.2", {"center": v(-589.98, 261.01) * mm, "radius": 1.6 * mm});
            skCircle(sketch, "E5.14.29.3", {"center": v(-584.98, 261.01) * mm, "radius": 1.6 * mm});
            skCircle(sketch, "E5.14.30.0", {"center": v(-592.48, 256.01) * mm, "radius": 1.6 * mm});
            skCircle(sketch, "E5.14.30.1", {"center": v(-587.48, 256.01) * mm, "radius": 1.6 * mm});
            skCircle(sketch, "E5.14.30.2", {"center": v(-589.98, 251.01) * mm, "radius": 1.6 * mm});
            skCircle(sketch, "E5.14.30.3", {"center": v(-584.98, 251.01) * mm, "radius": 1.6 * mm});
            skCircle(sketch, "E5.14.31.0", {"center": v(-592.48, 246.01) * mm, "radius": 1.6 * mm});
            skCircle(sketch, "E5.14.31.1", {"center": v(-587.48, 246.01) * mm, "radius": 1.6 * mm});
            skCircle(sketch, "E5.14.31.2", {"center": v(-589.98, 241.01) * mm, "radius": 1.6 * mm});
            skCircle(sketch, "E5.14.31.3", {"center": v(-584.98, 241.01) * mm, "radius": 1.6 * mm});
            skCircle(sketch, "E5.14.32.0", {"center": v(-592.48, 236.01) * mm, "radius": 1.6 * mm});
            skCircle(sketch, "E5.14.32.1", {"center": v(-587.48, 236.01) * mm, "radius": 1.6 * mm});
            skCircle(sketch, "E5.14.32.2", {"center": v(-589.98, 231.01) * mm, "radius": 1.6 * mm});
            skCircle(sketch, "E5.14.32.3", {"center": v(-584.98, 231.01) * mm, "radius": 1.6 * mm});
            skCircle(sketch, "E5.14.33.0", {"center": v(-592.48, 226.01) * mm, "radius": 1.6 * mm});
            skCircle(sketch, "E5.14.33.1", {"center": v(-587.48, 226.01) * mm, "radius": 1.6 * mm});
            skCircle(sketch, "E5.14.33.2", {"center": v(-589.98, 221.01) * mm, "radius": 1.6 * mm});
            skCircle(sketch, "E5.14.33.3", {"center": v(-584.98, 221.01) * mm, "radius": 1.6 * mm});
            skCircle(sketch, "E5.14.34.0", {"center": v(-592.48, 216.01) * mm, "radius": 1.6 * mm});
            skCircle(sketch, "E5.14.34.1", {"center": v(-587.48, 216.01) * mm, "radius": 1.6 * mm});
            skCircle(sketch, "E5.14.34.2", {"center": v(-589.98, 211.01) * mm, "radius": 1.6 * mm});
            skCircle(sketch, "E5.14.34.3", {"center": v(-584.98, 211.01) * mm, "radius": 1.6 * mm});
            skCircle(sketch, "E5.14.35.0", {"center": v(-592.48, 206.01) * mm, "radius": 1.6 * mm});
            skCircle(sketch, "E5.14.35.1", {"center": v(-587.48, 206.01) * mm, "radius": 1.6 * mm});
            skCircle(sketch, "E5.14.35.2", {"center": v(-589.98, 201.01) * mm, "radius": 1.6 * mm});
            skCircle(sketch, "E5.14.35.3", {"center": v(-584.98, 201.01) * mm, "radius": 1.6 * mm});
            skCircle(sketch, "E5.14.36.0", {"center": v(-592.48, 196.01) * mm, "radius": 1.6 * mm});
            skCircle(sketch, "E5.14.36.1", {"center": v(-587.48, 196.01) * mm, "radius": 1.6 * mm});
            skCircle(sketch, "E5.14.36.2", {"center": v(-589.98, 191.01) * mm, "radius": 1.6 * mm});
            skCircle(sketch, "E5.14.36.3", {"center": v(-584.98, 191.01) * mm, "radius": 1.6 * mm});
            skCircle(sketch, "E5.14.37.0", {"center": v(-592.48, 186.01) * mm, "radius": 1.6 * mm});
            skCircle(sketch, "E5.14.37.1", {"center": v(-587.48, 186.01) * mm, "radius": 1.6 * mm});
            skCircle(sketch, "E5.14.37.2", {"center": v(-589.98, 181.01) * mm, "radius": 1.6 * mm});
            skCircle(sketch, "E5.14.37.3", {"center": v(-584.98, 181.01) * mm, "radius": 1.6 * mm});
            skCircle(sketch, "E5.14.38.0", {"center": v(-592.48, 176.01) * mm, "radius": 1.6 * mm});
            skCircle(sketch, "E5.14.38.1", {"center": v(-587.48, 176.01) * mm, "radius": 1.6 * mm});
            skCircle(sketch, "E5.14.38.2", {"center": v(-589.98, 171.01) * mm, "radius": 1.6 * mm});
            skCircle(sketch, "E5.14.38.3", {"center": v(-584.98, 171.01) * mm, "radius": 1.6 * mm});
            skCircle(sketch, "E5.14.39.0", {"center": v(-592.48, 166.01) * mm, "radius": 1.6 * mm});
            skCircle(sketch, "E5.14.39.1", {"center": v(-587.48, 166.01) * mm, "radius": 1.6 * mm});
            skCircle(sketch, "E5.14.39.2", {"center": v(-589.98, 161.01) * mm, "radius": 1.6 * mm});
            skCircle(sketch, "E5.14.39.3", {"center": v(-584.98, 161.01) * mm, "radius": 1.6 * mm});
            skCircle(sketch, "E5.14.40.0", {"center": v(-592.48, 156.01) * mm, "radius": 1.6 * mm});
            skCircle(sketch, "E5.14.40.1", {"center": v(-587.48, 156.01) * mm, "radius": 1.6 * mm});
            skCircle(sketch, "E5.14.40.2", {"center": v(-589.98, 151.01) * mm, "radius": 1.6 * mm});
            skCircle(sketch, "E5.14.40.3", {"center": v(-584.98, 151.01) * mm, "radius": 1.6 * mm});
            skCircle(sketch, "E5.14.41.0", {"center": v(-592.48, 146.01) * mm, "radius": 1.6 * mm});
            skCircle(sketch, "E5.14.41.1", {"center": v(-587.48, 146.01) * mm, "radius": 1.6 * mm});
            skCircle(sketch, "E5.14.41.2", {"center": v(-589.98, 141.01) * mm, "radius": 1.6 * mm});
            skCircle(sketch, "E5.14.41.3", {"center": v(-584.98, 141.01) * mm, "radius": 1.6 * mm});
            skCircle(sketch, "E5.14.42.0", {"center": v(-592.48, 136.01) * mm, "radius": 1.6 * mm});
            skCircle(sketch, "E5.14.42.1", {"center": v(-587.48, 136.01) * mm, "radius": 1.6 * mm});
            skCircle(sketch, "E5.14.42.2", {"center": v(-589.98, 131.01) * mm, "radius": 1.6 * mm});
            skCircle(sketch, "E5.14.42.3", {"center": v(-584.98, 131.01) * mm, "radius": 1.6 * mm});
            skCircle(sketch, "E5.14.43.0", {"center": v(-592.48, 126.01) * mm, "radius": 1.6 * mm});
            skCircle(sketch, "E5.14.43.1", {"center": v(-587.48, 126.01) * mm, "radius": 1.6 * mm});
            skCircle(sketch, "E5.14.43.2", {"center": v(-589.98, 121.01) * mm, "radius": 1.6 * mm});
            skCircle(sketch, "E5.14.43.3", {"center": v(-584.98, 121.01) * mm, "radius": 1.6 * mm});
            skCircle(sketch, "E5.14.44.0", {"center": v(-592.48, 116.01) * mm, "radius": 1.6 * mm});
            skCircle(sketch, "E5.14.44.1", {"center": v(-587.48, 116.01) * mm, "radius": 1.6 * mm});
            skCircle(sketch, "E5.14.44.2", {"center": v(-589.98, 111.01) * mm, "radius": 1.6 * mm});
            skCircle(sketch, "E5.14.44.3", {"center": v(-584.98, 111.01) * mm, "radius": 1.6 * mm});
            skCircle(sketch, "E5.14.45.0", {"center": v(-592.48, 106.01) * mm, "radius": 1.6 * mm});
            skCircle(sketch, "E5.14.45.1", {"center": v(-587.48, 106.01) * mm, "radius": 1.6 * mm});
            skCircle(sketch, "E5.14.45.2", {"center": v(-589.98, 101.01) * mm, "radius": 1.6 * mm});
            skCircle(sketch, "E5.14.45.3", {"center": v(-584.98, 101.01) * mm, "radius": 1.6 * mm});
            skCircle(sketch, "E5.14.46.0", {"center": v(-592.48, 96.01) * mm, "radius": 1.6 * mm});
            skCircle(sketch, "E5.14.46.1", {"center": v(-587.48, 96.01) * mm, "radius": 1.6 * mm});
            skCircle(sketch, "E5.14.46.2", {"center": v(-589.98, 91.01) * mm, "radius": 1.6 * mm});
            skCircle(sketch, "E5.14.46.3", {"center": v(-584.98, 91.01) * mm, "radius": 1.6 * mm});
            skCircle(sketch, "E5.14.47.0", {"center": v(-592.48, 86.01) * mm, "radius": 1.6 * mm});
            skCircle(sketch, "E5.14.47.1", {"center": v(-587.48, 86.01) * mm, "radius": 1.6 * mm});
            skCircle(sketch, "E5.14.47.2", {"center": v(-589.98, 81.01) * mm, "radius": 1.6 * mm});
            skCircle(sketch, "E5.14.47.3", {"center": v(-584.98, 81.01) * mm, "radius": 1.6 * mm});
            skCircle(sketch, "E5.14.48.0", {"center": v(-592.48, 76.01) * mm, "radius": 1.6 * mm});
            skCircle(sketch, "E5.14.48.1", {"center": v(-587.48, 76.01) * mm, "radius": 1.6 * mm});
            skCircle(sketch, "E5.14.48.2", {"center": v(-589.98, 71.01) * mm, "radius": 1.6 * mm});
            skCircle(sketch, "E5.14.48.3", {"center": v(-584.98, 71.01) * mm, "radius": 1.6 * mm});
            skCircle(sketch, "E5.14.49.0", {"center": v(-592.48, 66.01) * mm, "radius": 1.6 * mm});
            skCircle(sketch, "E5.14.49.1", {"center": v(-587.48, 66.01) * mm, "radius": 1.6 * mm});
            skCircle(sketch, "E5.14.49.2", {"center": v(-589.98, 61.01) * mm, "radius": 1.6 * mm});
            skCircle(sketch, "E5.14.49.3", {"center": v(-584.98, 61.01) * mm, "radius": 1.6 * mm});
            skCircle(sketch, "E5.15.0.0", {"center": v(-582.48, 556.01) * mm, "radius": 1.6 * mm});
            skCircle(sketch, "E5.15.0.1", {"center": v(-577.48, 556.01) * mm, "radius": 1.6 * mm});
            skCircle(sketch, "E5.15.0.2", {"center": v(-579.98, 551.01) * mm, "radius": 1.6 * mm});
            skCircle(sketch, "E5.15.0.3", {"center": v(-574.98, 551.01) * mm, "radius": 1.6 * mm});
            skCircle(sketch, "E5.15.1.0", {"center": v(-582.48, 546.01) * mm, "radius": 1.6 * mm});
            skCircle(sketch, "E5.15.1.1", {"center": v(-577.48, 546.01) * mm, "radius": 1.6 * mm});
            skCircle(sketch, "E5.15.1.2", {"center": v(-579.98, 541.01) * mm, "radius": 1.6 * mm});
            skCircle(sketch, "E5.15.1.3", {"center": v(-574.98, 541.01) * mm, "radius": 1.6 * mm});
            skCircle(sketch, "E5.15.2.0", {"center": v(-582.48, 536.01) * mm, "radius": 1.6 * mm});
            skCircle(sketch, "E5.15.2.1", {"center": v(-577.48, 536.01) * mm, "radius": 1.6 * mm});
            skCircle(sketch, "E5.15.2.2", {"center": v(-579.98, 531.01) * mm, "radius": 1.6 * mm});
            skCircle(sketch, "E5.15.2.3", {"center": v(-574.98, 531.01) * mm, "radius": 1.6 * mm});
            skCircle(sketch, "E5.15.3.0", {"center": v(-582.48, 526.01) * mm, "radius": 1.6 * mm});
            skCircle(sketch, "E5.15.3.1", {"center": v(-577.48, 526.01) * mm, "radius": 1.6 * mm});
            skCircle(sketch, "E5.15.3.2", {"center": v(-579.98, 521.01) * mm, "radius": 1.6 * mm});
            skCircle(sketch, "E5.15.3.3", {"center": v(-574.98, 521.01) * mm, "radius": 1.6 * mm});
            skCircle(sketch, "E5.15.4.0", {"center": v(-582.48, 516.01) * mm, "radius": 1.6 * mm});
            skCircle(sketch, "E5.15.4.1", {"center": v(-577.48, 516.01) * mm, "radius": 1.6 * mm});
            skCircle(sketch, "E5.15.4.2", {"center": v(-579.98, 511.01) * mm, "radius": 1.6 * mm});
            skCircle(sketch, "E5.15.4.3", {"center": v(-574.98, 511.01) * mm, "radius": 1.6 * mm});
            skCircle(sketch, "E5.15.5.0", {"center": v(-582.48, 506.01) * mm, "radius": 1.6 * mm});
            skCircle(sketch, "E5.15.5.1", {"center": v(-577.48, 506.01) * mm, "radius": 1.6 * mm});
            skCircle(sketch, "E5.15.5.2", {"center": v(-579.98, 501.01) * mm, "radius": 1.6 * mm});
            skCircle(sketch, "E5.15.5.3", {"center": v(-574.98, 501.01) * mm, "radius": 1.6 * mm});
            skCircle(sketch, "E5.15.6.0", {"center": v(-582.48, 496.01) * mm, "radius": 1.6 * mm});
            skCircle(sketch, "E5.15.6.1", {"center": v(-577.48, 496.01) * mm, "radius": 1.6 * mm});
            skCircle(sketch, "E5.15.6.2", {"center": v(-579.98, 491.01) * mm, "radius": 1.6 * mm});
            skCircle(sketch, "E5.15.6.3", {"center": v(-574.98, 491.01) * mm, "radius": 1.6 * mm});
            skCircle(sketch, "E5.15.7.0", {"center": v(-582.48, 486.01) * mm, "radius": 1.6 * mm});
            skCircle(sketch, "E5.15.7.1", {"center": v(-577.48, 486.01) * mm, "radius": 1.6 * mm});
            skCircle(sketch, "E5.15.7.2", {"center": v(-579.98, 481.01) * mm, "radius": 1.6 * mm});
            skCircle(sketch, "E5.15.7.3", {"center": v(-574.98, 481.01) * mm, "radius": 1.6 * mm});
            skCircle(sketch, "E5.15.8.0", {"center": v(-582.48, 476.01) * mm, "radius": 1.6 * mm});
            skCircle(sketch, "E5.15.8.1", {"center": v(-577.48, 476.01) * mm, "radius": 1.6 * mm});
            skCircle(sketch, "E5.15.8.2", {"center": v(-579.98, 471.01) * mm, "radius": 1.6 * mm});
            skCircle(sketch, "E5.15.8.3", {"center": v(-574.98, 471.01) * mm, "radius": 1.6 * mm});
            skCircle(sketch, "E5.15.9.0", {"center": v(-582.48, 466.01) * mm, "radius": 1.6 * mm});
            skCircle(sketch, "E5.15.9.1", {"center": v(-577.48, 466.01) * mm, "radius": 1.6 * mm});
            skCircle(sketch, "E5.15.9.2", {"center": v(-579.98, 461.01) * mm, "radius": 1.6 * mm});
            skCircle(sketch, "E5.15.9.3", {"center": v(-574.98, 461.01) * mm, "radius": 1.6 * mm});
            skCircle(sketch, "E5.15.10.0", {"center": v(-582.48, 456.01) * mm, "radius": 1.6 * mm});
            skCircle(sketch, "E5.15.10.1", {"center": v(-577.48, 456.01) * mm, "radius": 1.6 * mm});
            skCircle(sketch, "E5.15.10.2", {"center": v(-579.98, 451.01) * mm, "radius": 1.6 * mm});
            skCircle(sketch, "E5.15.10.3", {"center": v(-574.98, 451.01) * mm, "radius": 1.6 * mm});
            skCircle(sketch, "E5.15.11.0", {"center": v(-582.48, 446.01) * mm, "radius": 1.6 * mm});
            skCircle(sketch, "E5.15.11.1", {"center": v(-577.48, 446.01) * mm, "radius": 1.6 * mm});
            skCircle(sketch, "E5.15.11.2", {"center": v(-579.98, 441.01) * mm, "radius": 1.6 * mm});
            skCircle(sketch, "E5.15.11.3", {"center": v(-574.98, 441.01) * mm, "radius": 1.6 * mm});
            skCircle(sketch, "E5.15.12.0", {"center": v(-582.48, 436.01) * mm, "radius": 1.6 * mm});
            skCircle(sketch, "E5.15.12.1", {"center": v(-577.48, 436.01) * mm, "radius": 1.6 * mm});
            skCircle(sketch, "E5.15.12.2", {"center": v(-579.98, 431.01) * mm, "radius": 1.6 * mm});
            skCircle(sketch, "E5.15.12.3", {"center": v(-574.98, 431.01) * mm, "radius": 1.6 * mm});
            skCircle(sketch, "E5.15.13.0", {"center": v(-582.48, 426.01) * mm, "radius": 1.6 * mm});
            skCircle(sketch, "E5.15.13.1", {"center": v(-577.48, 426.01) * mm, "radius": 1.6 * mm});
            skCircle(sketch, "E5.15.13.2", {"center": v(-579.98, 421.01) * mm, "radius": 1.6 * mm});
            skCircle(sketch, "E5.15.13.3", {"center": v(-574.98, 421.01) * mm, "radius": 1.6 * mm});
            skCircle(sketch, "E5.15.14.0", {"center": v(-582.48, 416.01) * mm, "radius": 1.6 * mm});
            skCircle(sketch, "E5.15.14.1", {"center": v(-577.48, 416.01) * mm, "radius": 1.6 * mm});
            skCircle(sketch, "E5.15.14.2", {"center": v(-579.98, 411.01) * mm, "radius": 1.6 * mm});
            skCircle(sketch, "E5.15.14.3", {"center": v(-574.98, 411.01) * mm, "radius": 1.6 * mm});
            skCircle(sketch, "E5.15.15.0", {"center": v(-582.48, 406.01) * mm, "radius": 1.6 * mm});
            skCircle(sketch, "E5.15.15.1", {"center": v(-577.48, 406.01) * mm, "radius": 1.6 * mm});
            skCircle(sketch, "E5.15.15.2", {"center": v(-579.98, 401.01) * mm, "radius": 1.6 * mm});
            skCircle(sketch, "E5.15.15.3", {"center": v(-574.98, 401.01) * mm, "radius": 1.6 * mm});
            skCircle(sketch, "E5.15.16.0", {"center": v(-582.48, 396.01) * mm, "radius": 1.6 * mm});
            skCircle(sketch, "E5.15.16.1", {"center": v(-577.48, 396.01) * mm, "radius": 1.6 * mm});
            skCircle(sketch, "E5.15.16.2", {"center": v(-579.98, 391.01) * mm, "radius": 1.6 * mm});
            skCircle(sketch, "E5.15.16.3", {"center": v(-574.98, 391.01) * mm, "radius": 1.6 * mm});
            skCircle(sketch, "E5.15.17.0", {"center": v(-582.48, 386.01) * mm, "radius": 1.6 * mm});
            skCircle(sketch, "E5.15.17.1", {"center": v(-577.48, 386.01) * mm, "radius": 1.6 * mm});
            skCircle(sketch, "E5.15.17.2", {"center": v(-579.98, 381.01) * mm, "radius": 1.6 * mm});
            skCircle(sketch, "E5.15.17.3", {"center": v(-574.98, 381.01) * mm, "radius": 1.6 * mm});
            skCircle(sketch, "E5.15.18.0", {"center": v(-582.48, 376.01) * mm, "radius": 1.6 * mm});
            skCircle(sketch, "E5.15.18.1", {"center": v(-577.48, 376.01) * mm, "radius": 1.6 * mm});
            skCircle(sketch, "E5.15.18.2", {"center": v(-579.98, 371.01) * mm, "radius": 1.6 * mm});
            skCircle(sketch, "E5.15.18.3", {"center": v(-574.98, 371.01) * mm, "radius": 1.6 * mm});
            skCircle(sketch, "E5.15.19.0", {"center": v(-582.48, 366.01) * mm, "radius": 1.6 * mm});
            skCircle(sketch, "E5.15.19.1", {"center": v(-577.48, 366.01) * mm, "radius": 1.6 * mm});
            skCircle(sketch, "E5.15.19.2", {"center": v(-579.98, 361.01) * mm, "radius": 1.6 * mm});
            skCircle(sketch, "E5.15.19.3", {"center": v(-574.98, 361.01) * mm, "radius": 1.6 * mm});
            skCircle(sketch, "E5.15.20.0", {"center": v(-582.48, 356.01) * mm, "radius": 1.6 * mm});
            skCircle(sketch, "E5.15.20.1", {"center": v(-577.48, 356.01) * mm, "radius": 1.6 * mm});
            skCircle(sketch, "E5.15.20.2", {"center": v(-579.98, 351.01) * mm, "radius": 1.6 * mm});
            skCircle(sketch, "E5.15.20.3", {"center": v(-574.98, 351.01) * mm, "radius": 1.6 * mm});
            skCircle(sketch, "E5.15.21.0", {"center": v(-582.48, 346.01) * mm, "radius": 1.6 * mm});
            skCircle(sketch, "E5.15.21.1", {"center": v(-577.48, 346.01) * mm, "radius": 1.6 * mm});
            skCircle(sketch, "E5.15.21.2", {"center": v(-579.98, 341.01) * mm, "radius": 1.6 * mm});
            skCircle(sketch, "E5.15.21.3", {"center": v(-574.98, 341.01) * mm, "radius": 1.6 * mm});
            skCircle(sketch, "E5.15.22.0", {"center": v(-582.48, 336.01) * mm, "radius": 1.6 * mm});
            skCircle(sketch, "E5.15.22.1", {"center": v(-577.48, 336.01) * mm, "radius": 1.6 * mm});
            skCircle(sketch, "E5.15.22.2", {"center": v(-579.98, 331.01) * mm, "radius": 1.6 * mm});
            skCircle(sketch, "E5.15.22.3", {"center": v(-574.98, 331.01) * mm, "radius": 1.6 * mm});
            skCircle(sketch, "E5.15.23.0", {"center": v(-582.48, 326.01) * mm, "radius": 1.6 * mm});
            skCircle(sketch, "E5.15.23.1", {"center": v(-577.48, 326.01) * mm, "radius": 1.6 * mm});
            skCircle(sketch, "E5.15.23.2", {"center": v(-579.98, 321.01) * mm, "radius": 1.6 * mm});
            skCircle(sketch, "E5.15.23.3", {"center": v(-574.98, 321.01) * mm, "radius": 1.6 * mm});
            skCircle(sketch, "E5.15.24.0", {"center": v(-582.48, 316.01) * mm, "radius": 1.6 * mm});
            skCircle(sketch, "E5.15.24.1", {"center": v(-577.48, 316.01) * mm, "radius": 1.6 * mm});
            skCircle(sketch, "E5.15.24.2", {"center": v(-579.98, 311.01) * mm, "radius": 1.6 * mm});
            skCircle(sketch, "E5.15.24.3", {"center": v(-574.98, 311.01) * mm, "radius": 1.6 * mm});
            skCircle(sketch, "E5.15.25.0", {"center": v(-582.48, 306.01) * mm, "radius": 1.6 * mm});
            skCircle(sketch, "E5.15.25.1", {"center": v(-577.48, 306.01) * mm, "radius": 1.6 * mm});
            skCircle(sketch, "E5.15.25.2", {"center": v(-579.98, 301.01) * mm, "radius": 1.6 * mm});
            skCircle(sketch, "E5.15.25.3", {"center": v(-574.98, 301.01) * mm, "radius": 1.6 * mm});
            skCircle(sketch, "E5.15.26.0", {"center": v(-582.48, 296.01) * mm, "radius": 1.6 * mm});
            skCircle(sketch, "E5.15.26.1", {"center": v(-577.48, 296.01) * mm, "radius": 1.6 * mm});
            skCircle(sketch, "E5.15.26.2", {"center": v(-579.98, 291.01) * mm, "radius": 1.6 * mm});
            skCircle(sketch, "E5.15.26.3", {"center": v(-574.98, 291.01) * mm, "radius": 1.6 * mm});
            skCircle(sketch, "E5.15.27.0", {"center": v(-582.48, 286.01) * mm, "radius": 1.6 * mm});
            skCircle(sketch, "E5.15.27.1", {"center": v(-577.48, 286.01) * mm, "radius": 1.6 * mm});
            skCircle(sketch, "E5.15.27.2", {"center": v(-579.98, 281.01) * mm, "radius": 1.6 * mm});
            skCircle(sketch, "E5.15.27.3", {"center": v(-574.98, 281.01) * mm, "radius": 1.6 * mm});
            skCircle(sketch, "E5.15.28.0", {"center": v(-582.48, 276.01) * mm, "radius": 1.6 * mm});
            skCircle(sketch, "E5.15.28.1", {"center": v(-577.48, 276.01) * mm, "radius": 1.6 * mm});
            skCircle(sketch, "E5.15.28.2", {"center": v(-579.98, 271.01) * mm, "radius": 1.6 * mm});
            skCircle(sketch, "E5.15.28.3", {"center": v(-574.98, 271.01) * mm, "radius": 1.6 * mm});
            skCircle(sketch, "E5.15.29.0", {"center": v(-582.48, 266.01) * mm, "radius": 1.6 * mm});
            skCircle(sketch, "E5.15.29.1", {"center": v(-577.48, 266.01) * mm, "radius": 1.6 * mm});
            skCircle(sketch, "E5.15.29.2", {"center": v(-579.98, 261.01) * mm, "radius": 1.6 * mm});
            skCircle(sketch, "E5.15.29.3", {"center": v(-574.98, 261.01) * mm, "radius": 1.6 * mm});
            skCircle(sketch, "E5.15.30.0", {"center": v(-582.48, 256.01) * mm, "radius": 1.6 * mm});
            skCircle(sketch, "E5.15.30.1", {"center": v(-577.48, 256.01) * mm, "radius": 1.6 * mm});
            skCircle(sketch, "E5.15.30.2", {"center": v(-579.98, 251.01) * mm, "radius": 1.6 * mm});
            skCircle(sketch, "E5.15.30.3", {"center": v(-574.98, 251.01) * mm, "radius": 1.6 * mm});
            skCircle(sketch, "E5.15.31.0", {"center": v(-582.48, 246.01) * mm, "radius": 1.6 * mm});
            skCircle(sketch, "E5.15.31.1", {"center": v(-577.48, 246.01) * mm, "radius": 1.6 * mm});
            skCircle(sketch, "E5.15.31.2", {"center": v(-579.98, 241.01) * mm, "radius": 1.6 * mm});
            skCircle(sketch, "E5.15.31.3", {"center": v(-574.98, 241.01) * mm, "radius": 1.6 * mm});
            skCircle(sketch, "E5.15.32.0", {"center": v(-582.48, 236.01) * mm, "radius": 1.6 * mm});
            skCircle(sketch, "E5.15.32.1", {"center": v(-577.48, 236.01) * mm, "radius": 1.6 * mm});
            skCircle(sketch, "E5.15.32.2", {"center": v(-579.98, 231.01) * mm, "radius": 1.6 * mm});
            skCircle(sketch, "E5.15.32.3", {"center": v(-574.98, 231.01) * mm, "radius": 1.6 * mm});
            skCircle(sketch, "E5.15.33.0", {"center": v(-582.48, 226.01) * mm, "radius": 1.6 * mm});
            skCircle(sketch, "E5.15.33.1", {"center": v(-577.48, 226.01) * mm, "radius": 1.6 * mm});
            skCircle(sketch, "E5.15.33.2", {"center": v(-579.98, 221.01) * mm, "radius": 1.6 * mm});
            skCircle(sketch, "E5.15.33.3", {"center": v(-574.98, 221.01) * mm, "radius": 1.6 * mm});
            skCircle(sketch, "E5.15.34.0", {"center": v(-582.48, 216.01) * mm, "radius": 1.6 * mm});
            skCircle(sketch, "E5.15.34.1", {"center": v(-577.48, 216.01) * mm, "radius": 1.6 * mm});
            skCircle(sketch, "E5.15.34.2", {"center": v(-579.98, 211.01) * mm, "radius": 1.6 * mm});
            skCircle(sketch, "E5.15.34.3", {"center": v(-574.98, 211.01) * mm, "radius": 1.6 * mm});
            skCircle(sketch, "E5.15.35.0", {"center": v(-582.48, 206.01) * mm, "radius": 1.6 * mm});
            skCircle(sketch, "E5.15.35.1", {"center": v(-577.48, 206.01) * mm, "radius": 1.6 * mm});
            skCircle(sketch, "E5.15.35.2", {"center": v(-579.98, 201.01) * mm, "radius": 1.6 * mm});
            skCircle(sketch, "E5.15.35.3", {"center": v(-574.98, 201.01) * mm, "radius": 1.6 * mm});
            skCircle(sketch, "E5.15.36.0", {"center": v(-582.48, 196.01) * mm, "radius": 1.6 * mm});
            skCircle(sketch, "E5.15.36.1", {"center": v(-577.48, 196.01) * mm, "radius": 1.6 * mm});
            skCircle(sketch, "E5.15.36.2", {"center": v(-579.98, 191.01) * mm, "radius": 1.6 * mm});
            skCircle(sketch, "E5.15.36.3", {"center": v(-574.98, 191.01) * mm, "radius": 1.6 * mm});
            skCircle(sketch, "E5.15.37.0", {"center": v(-582.48, 186.01) * mm, "radius": 1.6 * mm});
            skCircle(sketch, "E5.15.37.1", {"center": v(-577.48, 186.01) * mm, "radius": 1.6 * mm});
            skCircle(sketch, "E5.15.37.2", {"center": v(-579.98, 181.01) * mm, "radius": 1.6 * mm});
            skCircle(sketch, "E5.15.37.3", {"center": v(-574.98, 181.01) * mm, "radius": 1.6 * mm});
            skCircle(sketch, "E5.15.38.0", {"center": v(-582.48, 176.01) * mm, "radius": 1.6 * mm});
            skCircle(sketch, "E5.15.38.1", {"center": v(-577.48, 176.01) * mm, "radius": 1.6 * mm});
            skCircle(sketch, "E5.15.38.2", {"center": v(-579.98, 171.01) * mm, "radius": 1.6 * mm});
            skCircle(sketch, "E5.15.38.3", {"center": v(-574.98, 171.01) * mm, "radius": 1.6 * mm});
            skCircle(sketch, "E5.15.39.0", {"center": v(-582.48, 166.01) * mm, "radius": 1.6 * mm});
            skCircle(sketch, "E5.15.39.1", {"center": v(-577.48, 166.01) * mm, "radius": 1.6 * mm});
            skCircle(sketch, "E5.15.39.2", {"center": v(-579.98, 161.01) * mm, "radius": 1.6 * mm});
            skCircle(sketch, "E5.15.39.3", {"center": v(-574.98, 161.01) * mm, "radius": 1.6 * mm});
            skCircle(sketch, "E5.15.40.0", {"center": v(-582.48, 156.01) * mm, "radius": 1.6 * mm});
            skCircle(sketch, "E5.15.40.1", {"center": v(-577.48, 156.01) * mm, "radius": 1.6 * mm});
            skCircle(sketch, "E5.15.40.2", {"center": v(-579.98, 151.01) * mm, "radius": 1.6 * mm});
            skCircle(sketch, "E5.15.40.3", {"center": v(-574.98, 151.01) * mm, "radius": 1.6 * mm});
            skCircle(sketch, "E5.15.41.0", {"center": v(-582.48, 146.01) * mm, "radius": 1.6 * mm});
            skCircle(sketch, "E5.15.41.1", {"center": v(-577.48, 146.01) * mm, "radius": 1.6 * mm});
            skCircle(sketch, "E5.15.41.2", {"center": v(-579.98, 141.01) * mm, "radius": 1.6 * mm});
            skCircle(sketch, "E5.15.41.3", {"center": v(-574.98, 141.01) * mm, "radius": 1.6 * mm});
            skCircle(sketch, "E5.15.42.0", {"center": v(-582.48, 136.01) * mm, "radius": 1.6 * mm});
            skCircle(sketch, "E5.15.42.1", {"center": v(-577.48, 136.01) * mm, "radius": 1.6 * mm});
            skCircle(sketch, "E5.15.42.2", {"center": v(-579.98, 131.01) * mm, "radius": 1.6 * mm});
            skCircle(sketch, "E5.15.42.3", {"center": v(-574.98, 131.01) * mm, "radius": 1.6 * mm});
            skCircle(sketch, "E5.15.43.0", {"center": v(-582.48, 126.01) * mm, "radius": 1.6 * mm});
            skCircle(sketch, "E5.15.43.1", {"center": v(-577.48, 126.01) * mm, "radius": 1.6 * mm});
            skCircle(sketch, "E5.15.43.2", {"center": v(-579.98, 121.01) * mm, "radius": 1.6 * mm});
            skCircle(sketch, "E5.15.43.3", {"center": v(-574.98, 121.01) * mm, "radius": 1.6 * mm});
            skCircle(sketch, "E5.15.44.0", {"center": v(-582.48, 116.01) * mm, "radius": 1.6 * mm});
            skCircle(sketch, "E5.15.44.1", {"center": v(-577.48, 116.01) * mm, "radius": 1.6 * mm});
            skCircle(sketch, "E5.15.44.2", {"center": v(-579.98, 111.01) * mm, "radius": 1.6 * mm});
            skCircle(sketch, "E5.15.44.3", {"center": v(-574.98, 111.01) * mm, "radius": 1.6 * mm});
            skCircle(sketch, "E5.15.45.0", {"center": v(-582.48, 106.01) * mm, "radius": 1.6 * mm});
            skCircle(sketch, "E5.15.45.1", {"center": v(-577.48, 106.01) * mm, "radius": 1.6 * mm});
            skCircle(sketch, "E5.15.45.2", {"center": v(-579.98, 101.01) * mm, "radius": 1.6 * mm});
            skCircle(sketch, "E5.15.45.3", {"center": v(-574.98, 101.01) * mm, "radius": 1.6 * mm});
            skCircle(sketch, "E5.15.46.0", {"center": v(-582.48, 96.01) * mm, "radius": 1.6 * mm});
            skCircle(sketch, "E5.15.46.1", {"center": v(-577.48, 96.01) * mm, "radius": 1.6 * mm});
            skCircle(sketch, "E5.15.46.2", {"center": v(-579.98, 91.01) * mm, "radius": 1.6 * mm});
            skCircle(sketch, "E5.15.46.3", {"center": v(-574.98, 91.01) * mm, "radius": 1.6 * mm});
            skCircle(sketch, "E5.15.47.0", {"center": v(-582.48, 86.01) * mm, "radius": 1.6 * mm});
            skCircle(sketch, "E5.15.47.1", {"center": v(-577.48, 86.01) * mm, "radius": 1.6 * mm});
            skCircle(sketch, "E5.15.47.2", {"center": v(-579.98, 81.01) * mm, "radius": 1.6 * mm});
            skCircle(sketch, "E5.15.47.3", {"center": v(-574.98, 81.01) * mm, "radius": 1.6 * mm});
            skCircle(sketch, "E5.15.48.0", {"center": v(-582.48, 76.01) * mm, "radius": 1.6 * mm});
            skCircle(sketch, "E5.15.48.1", {"center": v(-577.48, 76.01) * mm, "radius": 1.6 * mm});
            skCircle(sketch, "E5.15.48.2", {"center": v(-579.98, 71.01) * mm, "radius": 1.6 * mm});
            skCircle(sketch, "E5.15.48.3", {"center": v(-574.98, 71.01) * mm, "radius": 1.6 * mm});
            skCircle(sketch, "E5.15.49.0", {"center": v(-582.48, 66.01) * mm, "radius": 1.6 * mm});
            skCircle(sketch, "E5.15.49.1", {"center": v(-577.48, 66.01) * mm, "radius": 1.6 * mm});
            skCircle(sketch, "E5.15.49.2", {"center": v(-579.98, 61.01) * mm, "radius": 1.6 * mm});
            skCircle(sketch, "E5.15.49.3", {"center": v(-574.98, 61.01) * mm, "radius": 1.6 * mm});
            skCircle(sketch, "E5.16.0.0", {"center": v(-572.48, 556.01) * mm, "radius": 1.6 * mm});
            skCircle(sketch, "E5.16.0.1", {"center": v(-567.48, 556.01) * mm, "radius": 1.6 * mm});
            skCircle(sketch, "E5.16.0.2", {"center": v(-569.98, 551.01) * mm, "radius": 1.6 * mm});
            skCircle(sketch, "E5.16.0.3", {"center": v(-564.98, 551.01) * mm, "radius": 1.6 * mm});
            skCircle(sketch, "E5.16.1.0", {"center": v(-572.48, 546.01) * mm, "radius": 1.6 * mm});
            skCircle(sketch, "E5.16.1.1", {"center": v(-567.48, 546.01) * mm, "radius": 1.6 * mm});
            skCircle(sketch, "E5.16.1.2", {"center": v(-569.98, 541.01) * mm, "radius": 1.6 * mm});
            skCircle(sketch, "E5.16.1.3", {"center": v(-564.98, 541.01) * mm, "radius": 1.6 * mm});
            skCircle(sketch, "E5.16.2.0", {"center": v(-572.48, 536.01) * mm, "radius": 1.6 * mm});
            skCircle(sketch, "E5.16.2.1", {"center": v(-567.48, 536.01) * mm, "radius": 1.6 * mm});
            skCircle(sketch, "E5.16.2.2", {"center": v(-569.98, 531.01) * mm, "radius": 1.6 * mm});
            skCircle(sketch, "E5.16.2.3", {"center": v(-564.98, 531.01) * mm, "radius": 1.6 * mm});
            skCircle(sketch, "E5.16.3.0", {"center": v(-572.48, 526.01) * mm, "radius": 1.6 * mm});
            skCircle(sketch, "E5.16.3.1", {"center": v(-567.48, 526.01) * mm, "radius": 1.6 * mm});
            skCircle(sketch, "E5.16.3.2", {"center": v(-569.98, 521.01) * mm, "radius": 1.6 * mm});
            skCircle(sketch, "E5.16.3.3", {"center": v(-564.98, 521.01) * mm, "radius": 1.6 * mm});
            skCircle(sketch, "E5.16.4.0", {"center": v(-572.48, 516.01) * mm, "radius": 1.6 * mm});
            skCircle(sketch, "E5.16.4.1", {"center": v(-567.48, 516.01) * mm, "radius": 1.6 * mm});
            skCircle(sketch, "E5.16.4.2", {"center": v(-569.98, 511.01) * mm, "radius": 1.6 * mm});
            skCircle(sketch, "E5.16.4.3", {"center": v(-564.98, 511.01) * mm, "radius": 1.6 * mm});
            skCircle(sketch, "E5.16.5.0", {"center": v(-572.48, 506.01) * mm, "radius": 1.6 * mm});
            skCircle(sketch, "E5.16.5.1", {"center": v(-567.48, 506.01) * mm, "radius": 1.6 * mm});
            skCircle(sketch, "E5.16.5.2", {"center": v(-569.98, 501.01) * mm, "radius": 1.6 * mm});
            skCircle(sketch, "E5.16.5.3", {"center": v(-564.98, 501.01) * mm, "radius": 1.6 * mm});
            skCircle(sketch, "E5.16.6.0", {"center": v(-572.48, 496.01) * mm, "radius": 1.6 * mm});
            skCircle(sketch, "E5.16.6.1", {"center": v(-567.48, 496.01) * mm, "radius": 1.6 * mm});
            skCircle(sketch, "E5.16.6.2", {"center": v(-569.98, 491.01) * mm, "radius": 1.6 * mm});
            skCircle(sketch, "E5.16.6.3", {"center": v(-564.98, 491.01) * mm, "radius": 1.6 * mm});
            skCircle(sketch, "E5.16.7.0", {"center": v(-572.48, 486.01) * mm, "radius": 1.6 * mm});
            skCircle(sketch, "E5.16.7.1", {"center": v(-567.48, 486.01) * mm, "radius": 1.6 * mm});
            skCircle(sketch, "E5.16.7.2", {"center": v(-569.98, 481.01) * mm, "radius": 1.6 * mm});
            skCircle(sketch, "E5.16.7.3", {"center": v(-564.98, 481.01) * mm, "radius": 1.6 * mm});
            skCircle(sketch, "E5.16.8.0", {"center": v(-572.48, 476.01) * mm, "radius": 1.6 * mm});
            skCircle(sketch, "E5.16.8.1", {"center": v(-567.48, 476.01) * mm, "radius": 1.6 * mm});
            skCircle(sketch, "E5.16.8.2", {"center": v(-569.98, 471.01) * mm, "radius": 1.6 * mm});
            skCircle(sketch, "E5.16.8.3", {"center": v(-564.98, 471.01) * mm, "radius": 1.6 * mm});
            skCircle(sketch, "E5.16.9.0", {"center": v(-572.48, 466.01) * mm, "radius": 1.6 * mm});
            skCircle(sketch, "E5.16.9.1", {"center": v(-567.48, 466.01) * mm, "radius": 1.6 * mm});
            skCircle(sketch, "E5.16.9.2", {"center": v(-569.98, 461.01) * mm, "radius": 1.6 * mm});
            skCircle(sketch, "E5.16.9.3", {"center": v(-564.98, 461.01) * mm, "radius": 1.6 * mm});
            skCircle(sketch, "E5.16.10.0", {"center": v(-572.48, 456.01) * mm, "radius": 1.6 * mm});
            skCircle(sketch, "E5.16.10.1", {"center": v(-567.48, 456.01) * mm, "radius": 1.6 * mm});
            skCircle(sketch, "E5.16.10.2", {"center": v(-569.98, 451.01) * mm, "radius": 1.6 * mm});
            skCircle(sketch, "E5.16.10.3", {"center": v(-564.98, 451.01) * mm, "radius": 1.6 * mm});
            skCircle(sketch, "E5.16.11.0", {"center": v(-572.48, 446.01) * mm, "radius": 1.6 * mm});
            skCircle(sketch, "E5.16.11.1", {"center": v(-567.48, 446.01) * mm, "radius": 1.6 * mm});
            skCircle(sketch, "E5.16.11.2", {"center": v(-569.98, 441.01) * mm, "radius": 1.6 * mm});
            skCircle(sketch, "E5.16.11.3", {"center": v(-564.98, 441.01) * mm, "radius": 1.6 * mm});
            skCircle(sketch, "E5.16.12.0", {"center": v(-572.48, 436.01) * mm, "radius": 1.6 * mm});
            skCircle(sketch, "E5.16.12.1", {"center": v(-567.48, 436.01) * mm, "radius": 1.6 * mm});
            skCircle(sketch, "E5.16.12.2", {"center": v(-569.98, 431.01) * mm, "radius": 1.6 * mm});
            skCircle(sketch, "E5.16.12.3", {"center": v(-564.98, 431.01) * mm, "radius": 1.6 * mm});
            skCircle(sketch, "E5.16.13.0", {"center": v(-572.48, 426.01) * mm, "radius": 1.6 * mm});
            skCircle(sketch, "E5.16.13.1", {"center": v(-567.48, 426.01) * mm, "radius": 1.6 * mm});
            skCircle(sketch, "E5.16.13.2", {"center": v(-569.98, 421.01) * mm, "radius": 1.6 * mm});
            skCircle(sketch, "E5.16.13.3", {"center": v(-564.98, 421.01) * mm, "radius": 1.6 * mm});
            skCircle(sketch, "E5.16.14.0", {"center": v(-572.48, 416.01) * mm, "radius": 1.6 * mm});
            skCircle(sketch, "E5.16.14.1", {"center": v(-567.48, 416.01) * mm, "radius": 1.6 * mm});
            skCircle(sketch, "E5.16.14.2", {"center": v(-569.98, 411.01) * mm, "radius": 1.6 * mm});
            skCircle(sketch, "E5.16.14.3", {"center": v(-564.98, 411.01) * mm, "radius": 1.6 * mm});
            skCircle(sketch, "E5.16.15.0", {"center": v(-572.48, 406.01) * mm, "radius": 1.6 * mm});
            skCircle(sketch, "E5.16.15.1", {"center": v(-567.48, 406.01) * mm, "radius": 1.6 * mm});
            skCircle(sketch, "E5.16.15.2", {"center": v(-569.98, 401.01) * mm, "radius": 1.6 * mm});
            skCircle(sketch, "E5.16.15.3", {"center": v(-564.98, 401.01) * mm, "radius": 1.6 * mm});
            skCircle(sketch, "E5.16.16.0", {"center": v(-572.48, 396.01) * mm, "radius": 1.6 * mm});
            skCircle(sketch, "E5.16.16.1", {"center": v(-567.48, 396.01) * mm, "radius": 1.6 * mm});
            skCircle(sketch, "E5.16.16.2", {"center": v(-569.98, 391.01) * mm, "radius": 1.6 * mm});
            skCircle(sketch, "E5.16.16.3", {"center": v(-564.98, 391.01) * mm, "radius": 1.6 * mm});
            skCircle(sketch, "E5.16.17.0", {"center": v(-572.48, 386.01) * mm, "radius": 1.6 * mm});
            skCircle(sketch, "E5.16.17.1", {"center": v(-567.48, 386.01) * mm, "radius": 1.6 * mm});
            skCircle(sketch, "E5.16.17.2", {"center": v(-569.98, 381.01) * mm, "radius": 1.6 * mm});
            skCircle(sketch, "E5.16.17.3", {"center": v(-564.98, 381.01) * mm, "radius": 1.6 * mm});
            skCircle(sketch, "E5.16.18.0", {"center": v(-572.48, 376.01) * mm, "radius": 1.6 * mm});
            skCircle(sketch, "E5.16.18.1", {"center": v(-567.48, 376.01) * mm, "radius": 1.6 * mm});
            skCircle(sketch, "E5.16.18.2", {"center": v(-569.98, 371.01) * mm, "radius": 1.6 * mm});
            skCircle(sketch, "E5.16.18.3", {"center": v(-564.98, 371.01) * mm, "radius": 1.6 * mm});
            skCircle(sketch, "E5.16.19.0", {"center": v(-572.48, 366.01) * mm, "radius": 1.6 * mm});
            skCircle(sketch, "E5.16.19.1", {"center": v(-567.48, 366.01) * mm, "radius": 1.6 * mm});
            skCircle(sketch, "E5.16.19.2", {"center": v(-569.98, 361.01) * mm, "radius": 1.6 * mm});
            skCircle(sketch, "E5.16.19.3", {"center": v(-564.98, 361.01) * mm, "radius": 1.6 * mm});
            skCircle(sketch, "E5.16.20.0", {"center": v(-572.48, 356.01) * mm, "radius": 1.6 * mm});
            skCircle(sketch, "E5.16.20.1", {"center": v(-567.48, 356.01) * mm, "radius": 1.6 * mm});
            skCircle(sketch, "E5.16.20.2", {"center": v(-569.98, 351.01) * mm, "radius": 1.6 * mm});
            skCircle(sketch, "E5.16.20.3", {"center": v(-564.98, 351.01) * mm, "radius": 1.6 * mm});
            skCircle(sketch, "E5.16.21.0", {"center": v(-572.48, 346.01) * mm, "radius": 1.6 * mm});
            skCircle(sketch, "E5.16.21.1", {"center": v(-567.48, 346.01) * mm, "radius": 1.6 * mm});
            skCircle(sketch, "E5.16.21.2", {"center": v(-569.98, 341.01) * mm, "radius": 1.6 * mm});
            skCircle(sketch, "E5.16.21.3", {"center": v(-564.98, 341.01) * mm, "radius": 1.6 * mm});
            skCircle(sketch, "E5.16.22.0", {"center": v(-572.48, 336.01) * mm, "radius": 1.6 * mm});
            skCircle(sketch, "E5.16.22.1", {"center": v(-567.48, 336.01) * mm, "radius": 1.6 * mm});
            skCircle(sketch, "E5.16.22.2", {"center": v(-569.98, 331.01) * mm, "radius": 1.6 * mm});
            skCircle(sketch, "E5.16.22.3", {"center": v(-564.98, 331.01) * mm, "radius": 1.6 * mm});
            skCircle(sketch, "E5.16.23.0", {"center": v(-572.48, 326.01) * mm, "radius": 1.6 * mm});
            skCircle(sketch, "E5.16.23.1", {"center": v(-567.48, 326.01) * mm, "radius": 1.6 * mm});
            skCircle(sketch, "E5.16.23.2", {"center": v(-569.98, 321.01) * mm, "radius": 1.6 * mm});
            skCircle(sketch, "E5.16.23.3", {"center": v(-564.98, 321.01) * mm, "radius": 1.6 * mm});
            skCircle(sketch, "E5.16.24.0", {"center": v(-572.48, 316.01) * mm, "radius": 1.6 * mm});
            skCircle(sketch, "E5.16.24.1", {"center": v(-567.48, 316.01) * mm, "radius": 1.6 * mm});
            skCircle(sketch, "E5.16.24.2", {"center": v(-569.98, 311.01) * mm, "radius": 1.6 * mm});
            skCircle(sketch, "E5.16.24.3", {"center": v(-564.98, 311.01) * mm, "radius": 1.6 * mm});
            skCircle(sketch, "E5.16.25.0", {"center": v(-572.48, 306.01) * mm, "radius": 1.6 * mm});
            skCircle(sketch, "E5.16.25.1", {"center": v(-567.48, 306.01) * mm, "radius": 1.6 * mm});
            skCircle(sketch, "E5.16.25.2", {"center": v(-569.98, 301.01) * mm, "radius": 1.6 * mm});
            skCircle(sketch, "E5.16.25.3", {"center": v(-564.98, 301.01) * mm, "radius": 1.6 * mm});
            skCircle(sketch, "E5.16.26.0", {"center": v(-572.48, 296.01) * mm, "radius": 1.6 * mm});
            skCircle(sketch, "E5.16.26.1", {"center": v(-567.48, 296.01) * mm, "radius": 1.6 * mm});
            skCircle(sketch, "E5.16.26.2", {"center": v(-569.98, 291.01) * mm, "radius": 1.6 * mm});
            skCircle(sketch, "E5.16.26.3", {"center": v(-564.98, 291.01) * mm, "radius": 1.6 * mm});
            skCircle(sketch, "E5.16.27.0", {"center": v(-572.48, 286.01) * mm, "radius": 1.6 * mm});
            skCircle(sketch, "E5.16.27.1", {"center": v(-567.48, 286.01) * mm, "radius": 1.6 * mm});
            skCircle(sketch, "E5.16.27.2", {"center": v(-569.98, 281.01) * mm, "radius": 1.6 * mm});
            skCircle(sketch, "E5.16.27.3", {"center": v(-564.98, 281.01) * mm, "radius": 1.6 * mm});
            skCircle(sketch, "E5.16.28.0", {"center": v(-572.48, 276.01) * mm, "radius": 1.6 * mm});
            skCircle(sketch, "E5.16.28.1", {"center": v(-567.48, 276.01) * mm, "radius": 1.6 * mm});
            skCircle(sketch, "E5.16.28.2", {"center": v(-569.98, 271.01) * mm, "radius": 1.6 * mm});
            skCircle(sketch, "E5.16.28.3", {"center": v(-564.98, 271.01) * mm, "radius": 1.6 * mm});
            skCircle(sketch, "E5.16.29.0", {"center": v(-572.48, 266.01) * mm, "radius": 1.6 * mm});
            skCircle(sketch, "E5.16.29.1", {"center": v(-567.48, 266.01) * mm, "radius": 1.6 * mm});
            skCircle(sketch, "E5.16.29.2", {"center": v(-569.98, 261.01) * mm, "radius": 1.6 * mm});
            skCircle(sketch, "E5.16.29.3", {"center": v(-564.98, 261.01) * mm, "radius": 1.6 * mm});
            skCircle(sketch, "E5.16.30.0", {"center": v(-572.48, 256.01) * mm, "radius": 1.6 * mm});
            skCircle(sketch, "E5.16.30.1", {"center": v(-567.48, 256.01) * mm, "radius": 1.6 * mm});
            skCircle(sketch, "E5.16.30.2", {"center": v(-569.98, 251.01) * mm, "radius": 1.6 * mm});
            skCircle(sketch, "E5.16.30.3", {"center": v(-564.98, 251.01) * mm, "radius": 1.6 * mm});
            skCircle(sketch, "E5.16.31.0", {"center": v(-572.48, 246.01) * mm, "radius": 1.6 * mm});
            skCircle(sketch, "E5.16.31.1", {"center": v(-567.48, 246.01) * mm, "radius": 1.6 * mm});
            skCircle(sketch, "E5.16.31.2", {"center": v(-569.98, 241.01) * mm, "radius": 1.6 * mm});
            skCircle(sketch, "E5.16.31.3", {"center": v(-564.98, 241.01) * mm, "radius": 1.6 * mm});
            skCircle(sketch, "E5.16.32.0", {"center": v(-572.48, 236.01) * mm, "radius": 1.6 * mm});
            skCircle(sketch, "E5.16.32.1", {"center": v(-567.48, 236.01) * mm, "radius": 1.6 * mm});
            skCircle(sketch, "E5.16.32.2", {"center": v(-569.98, 231.01) * mm, "radius": 1.6 * mm});
            skCircle(sketch, "E5.16.32.3", {"center": v(-564.98, 231.01) * mm, "radius": 1.6 * mm});
            skCircle(sketch, "E5.16.33.0", {"center": v(-572.48, 226.01) * mm, "radius": 1.6 * mm});
            skCircle(sketch, "E5.16.33.1", {"center": v(-567.48, 226.01) * mm, "radius": 1.6 * mm});
            skCircle(sketch, "E5.16.33.2", {"center": v(-569.98, 221.01) * mm, "radius": 1.6 * mm});
            skCircle(sketch, "E5.16.33.3", {"center": v(-564.98, 221.01) * mm, "radius": 1.6 * mm});
            skCircle(sketch, "E5.16.34.0", {"center": v(-572.48, 216.01) * mm, "radius": 1.6 * mm});
            skCircle(sketch, "E5.16.34.1", {"center": v(-567.48, 216.01) * mm, "radius": 1.6 * mm});
            skCircle(sketch, "E5.16.34.2", {"center": v(-569.98, 211.01) * mm, "radius": 1.6 * mm});
            skCircle(sketch, "E5.16.34.3", {"center": v(-564.98, 211.01) * mm, "radius": 1.6 * mm});
            skCircle(sketch, "E5.16.35.0", {"center": v(-572.48, 206.01) * mm, "radius": 1.6 * mm});
            skCircle(sketch, "E5.16.35.1", {"center": v(-567.48, 206.01) * mm, "radius": 1.6 * mm});
            skCircle(sketch, "E5.16.35.2", {"center": v(-569.98, 201.01) * mm, "radius": 1.6 * mm});
            skCircle(sketch, "E5.16.35.3", {"center": v(-564.98, 201.01) * mm, "radius": 1.6 * mm});
            skCircle(sketch, "E5.16.36.0", {"center": v(-572.48, 196.01) * mm, "radius": 1.6 * mm});
            skCircle(sketch, "E5.16.36.1", {"center": v(-567.48, 196.01) * mm, "radius": 1.6 * mm});
            skCircle(sketch, "E5.16.36.2", {"center": v(-569.98, 191.01) * mm, "radius": 1.6 * mm});
            skCircle(sketch, "E5.16.36.3", {"center": v(-564.98, 191.01) * mm, "radius": 1.6 * mm});
            skCircle(sketch, "E5.16.37.0", {"center": v(-572.48, 186.01) * mm, "radius": 1.6 * mm});
            skCircle(sketch, "E5.16.37.1", {"center": v(-567.48, 186.01) * mm, "radius": 1.6 * mm});
            skCircle(sketch, "E5.16.37.2", {"center": v(-569.98, 181.01) * mm, "radius": 1.6 * mm});
            skCircle(sketch, "E5.16.37.3", {"center": v(-564.98, 181.01) * mm, "radius": 1.6 * mm});
            skCircle(sketch, "E5.16.38.0", {"center": v(-572.48, 176.01) * mm, "radius": 1.6 * mm});
            skCircle(sketch, "E5.16.38.1", {"center": v(-567.48, 176.01) * mm, "radius": 1.6 * mm});
            skCircle(sketch, "E5.16.38.2", {"center": v(-569.98, 171.01) * mm, "radius": 1.6 * mm});
            skCircle(sketch, "E5.16.38.3", {"center": v(-564.98, 171.01) * mm, "radius": 1.6 * mm});
            skCircle(sketch, "E5.16.39.0", {"center": v(-572.48, 166.01) * mm, "radius": 1.6 * mm});
            skCircle(sketch, "E5.16.39.1", {"center": v(-567.48, 166.01) * mm, "radius": 1.6 * mm});
            skCircle(sketch, "E5.16.39.2", {"center": v(-569.98, 161.01) * mm, "radius": 1.6 * mm});
            skCircle(sketch, "E5.16.39.3", {"center": v(-564.98, 161.01) * mm, "radius": 1.6 * mm});
            skCircle(sketch, "E5.16.40.0", {"center": v(-572.48, 156.01) * mm, "radius": 1.6 * mm});
            skCircle(sketch, "E5.16.40.1", {"center": v(-567.48, 156.01) * mm, "radius": 1.6 * mm});
            skCircle(sketch, "E5.16.40.2", {"center": v(-569.98, 151.01) * mm, "radius": 1.6 * mm});
            skCircle(sketch, "E5.16.40.3", {"center": v(-564.98, 151.01) * mm, "radius": 1.6 * mm});
            skCircle(sketch, "E5.16.41.0", {"center": v(-572.48, 146.01) * mm, "radius": 1.6 * mm});
            skCircle(sketch, "E5.16.41.1", {"center": v(-567.48, 146.01) * mm, "radius": 1.6 * mm});
            skCircle(sketch, "E5.16.41.2", {"center": v(-569.98, 141.01) * mm, "radius": 1.6 * mm});
            skCircle(sketch, "E5.16.41.3", {"center": v(-564.98, 141.01) * mm, "radius": 1.6 * mm});
            skCircle(sketch, "E5.16.42.0", {"center": v(-572.48, 136.01) * mm, "radius": 1.6 * mm});
            skCircle(sketch, "E5.16.42.1", {"center": v(-567.48, 136.01) * mm, "radius": 1.6 * mm});
            skCircle(sketch, "E5.16.42.2", {"center": v(-569.98, 131.01) * mm, "radius": 1.6 * mm});
            skCircle(sketch, "E5.16.42.3", {"center": v(-564.98, 131.01) * mm, "radius": 1.6 * mm});
            skCircle(sketch, "E5.16.43.0", {"center": v(-572.48, 126.01) * mm, "radius": 1.6 * mm});
            skCircle(sketch, "E5.16.43.1", {"center": v(-567.48, 126.01) * mm, "radius": 1.6 * mm});
            skCircle(sketch, "E5.16.43.2", {"center": v(-569.98, 121.01) * mm, "radius": 1.6 * mm});
            skCircle(sketch, "E5.16.43.3", {"center": v(-564.98, 121.01) * mm, "radius": 1.6 * mm});
            skCircle(sketch, "E5.16.44.0", {"center": v(-572.48, 116.01) * mm, "radius": 1.6 * mm});
            skCircle(sketch, "E5.16.44.1", {"center": v(-567.48, 116.01) * mm, "radius": 1.6 * mm});
            skCircle(sketch, "E5.16.44.2", {"center": v(-569.98, 111.01) * mm, "radius": 1.6 * mm});
            skCircle(sketch, "E5.16.44.3", {"center": v(-564.98, 111.01) * mm, "radius": 1.6 * mm});
            skCircle(sketch, "E5.16.45.0", {"center": v(-572.48, 106.01) * mm, "radius": 1.6 * mm});
            skCircle(sketch, "E5.16.45.1", {"center": v(-567.48, 106.01) * mm, "radius": 1.6 * mm});
            skCircle(sketch, "E5.16.45.2", {"center": v(-569.98, 101.01) * mm, "radius": 1.6 * mm});
            skCircle(sketch, "E5.16.45.3", {"center": v(-564.98, 101.01) * mm, "radius": 1.6 * mm});
            skCircle(sketch, "E5.16.46.0", {"center": v(-572.48, 96.01) * mm, "radius": 1.6 * mm});
            skCircle(sketch, "E5.16.46.1", {"center": v(-567.48, 96.01) * mm, "radius": 1.6 * mm});
            skCircle(sketch, "E5.16.46.2", {"center": v(-569.98, 91.01) * mm, "radius": 1.6 * mm});
            skCircle(sketch, "E5.16.46.3", {"center": v(-564.98, 91.01) * mm, "radius": 1.6 * mm});
            skCircle(sketch, "E5.16.47.0", {"center": v(-572.48, 86.01) * mm, "radius": 1.6 * mm});
            skCircle(sketch, "E5.16.47.1", {"center": v(-567.48, 86.01) * mm, "radius": 1.6 * mm});
            skCircle(sketch, "E5.16.47.2", {"center": v(-569.98, 81.01) * mm, "radius": 1.6 * mm});
            skCircle(sketch, "E5.16.47.3", {"center": v(-564.98, 81.01) * mm, "radius": 1.6 * mm});
            skCircle(sketch, "E5.16.48.0", {"center": v(-572.48, 76.01) * mm, "radius": 1.6 * mm});
            skCircle(sketch, "E5.16.48.1", {"center": v(-567.48, 76.01) * mm, "radius": 1.6 * mm});
            skCircle(sketch, "E5.16.48.2", {"center": v(-569.98, 71.01) * mm, "radius": 1.6 * mm});
            skCircle(sketch, "E5.16.48.3", {"center": v(-564.98, 71.01) * mm, "radius": 1.6 * mm});
            skCircle(sketch, "E5.16.49.0", {"center": v(-572.48, 66.01) * mm, "radius": 1.6 * mm});
            skCircle(sketch, "E5.16.49.1", {"center": v(-567.48, 66.01) * mm, "radius": 1.6 * mm});
            skCircle(sketch, "E5.16.49.2", {"center": v(-569.98, 61.01) * mm, "radius": 1.6 * mm});
            skCircle(sketch, "E5.16.49.3", {"center": v(-564.98, 61.01) * mm, "radius": 1.6 * mm});
            skCircle(sketch, "E5.17.0.0", {"center": v(-562.48, 556.01) * mm, "radius": 1.6 * mm});
            skCircle(sketch, "E5.17.0.1", {"center": v(-557.48, 556.01) * mm, "radius": 1.6 * mm});
            skCircle(sketch, "E5.17.0.2", {"center": v(-559.98, 551.01) * mm, "radius": 1.6 * mm});
            skCircle(sketch, "E5.17.0.3", {"center": v(-554.98, 551.01) * mm, "radius": 1.6 * mm});
            skCircle(sketch, "E5.17.1.0", {"center": v(-562.48, 546.01) * mm, "radius": 1.6 * mm});
            skCircle(sketch, "E5.17.1.1", {"center": v(-557.48, 546.01) * mm, "radius": 1.6 * mm});
            skCircle(sketch, "E5.17.1.2", {"center": v(-559.98, 541.01) * mm, "radius": 1.6 * mm});
            skCircle(sketch, "E5.17.1.3", {"center": v(-554.98, 541.01) * mm, "radius": 1.6 * mm});
            skCircle(sketch, "E5.17.2.0", {"center": v(-562.48, 536.01) * mm, "radius": 1.6 * mm});
            skCircle(sketch, "E5.17.2.1", {"center": v(-557.48, 536.01) * mm, "radius": 1.6 * mm});
            skCircle(sketch, "E5.17.2.2", {"center": v(-559.98, 531.01) * mm, "radius": 1.6 * mm});
            skCircle(sketch, "E5.17.2.3", {"center": v(-554.98, 531.01) * mm, "radius": 1.6 * mm});
            skCircle(sketch, "E5.17.3.0", {"center": v(-562.48, 526.01) * mm, "radius": 1.6 * mm});
            skCircle(sketch, "E5.17.3.1", {"center": v(-557.48, 526.01) * mm, "radius": 1.6 * mm});
            skCircle(sketch, "E5.17.3.2", {"center": v(-559.98, 521.01) * mm, "radius": 1.6 * mm});
            skCircle(sketch, "E5.17.3.3", {"center": v(-554.98, 521.01) * mm, "radius": 1.6 * mm});
            skCircle(sketch, "E5.17.4.0", {"center": v(-562.48, 516.01) * mm, "radius": 1.6 * mm});
            skCircle(sketch, "E5.17.4.1", {"center": v(-557.48, 516.01) * mm, "radius": 1.6 * mm});
            skCircle(sketch, "E5.17.4.2", {"center": v(-559.98, 511.01) * mm, "radius": 1.6 * mm});
            skCircle(sketch, "E5.17.4.3", {"center": v(-554.98, 511.01) * mm, "radius": 1.6 * mm});
            skCircle(sketch, "E5.17.5.0", {"center": v(-562.48, 506.01) * mm, "radius": 1.6 * mm});
            skCircle(sketch, "E5.17.5.1", {"center": v(-557.48, 506.01) * mm, "radius": 1.6 * mm});
            skCircle(sketch, "E5.17.5.2", {"center": v(-559.98, 501.01) * mm, "radius": 1.6 * mm});
            skCircle(sketch, "E5.17.5.3", {"center": v(-554.98, 501.01) * mm, "radius": 1.6 * mm});
            skCircle(sketch, "E5.17.6.0", {"center": v(-562.48, 496.01) * mm, "radius": 1.6 * mm});
            skCircle(sketch, "E5.17.6.1", {"center": v(-557.48, 496.01) * mm, "radius": 1.6 * mm});
            skCircle(sketch, "E5.17.6.2", {"center": v(-559.98, 491.01) * mm, "radius": 1.6 * mm});
            skCircle(sketch, "E5.17.6.3", {"center": v(-554.98, 491.01) * mm, "radius": 1.6 * mm});
            skCircle(sketch, "E5.17.7.0", {"center": v(-562.48, 486.01) * mm, "radius": 1.6 * mm});
            skCircle(sketch, "E5.17.7.1", {"center": v(-557.48, 486.01) * mm, "radius": 1.6 * mm});
            skCircle(sketch, "E5.17.7.2", {"center": v(-559.98, 481.01) * mm, "radius": 1.6 * mm});
            skCircle(sketch, "E5.17.7.3", {"center": v(-554.98, 481.01) * mm, "radius": 1.6 * mm});
            skCircle(sketch, "E5.17.8.0", {"center": v(-562.48, 476.01) * mm, "radius": 1.6 * mm});
            skCircle(sketch, "E5.17.8.1", {"center": v(-557.48, 476.01) * mm, "radius": 1.6 * mm});
            skCircle(sketch, "E5.17.8.2", {"center": v(-559.98, 471.01) * mm, "radius": 1.6 * mm});
            skCircle(sketch, "E5.17.8.3", {"center": v(-554.98, 471.01) * mm, "radius": 1.6 * mm});
            skCircle(sketch, "E5.17.9.0", {"center": v(-562.48, 466.01) * mm, "radius": 1.6 * mm});
            skCircle(sketch, "E5.17.9.1", {"center": v(-557.48, 466.01) * mm, "radius": 1.6 * mm});
            skCircle(sketch, "E5.17.9.2", {"center": v(-559.98, 461.01) * mm, "radius": 1.6 * mm});
            skCircle(sketch, "E5.17.9.3", {"center": v(-554.98, 461.01) * mm, "radius": 1.6 * mm});
            skCircle(sketch, "E5.17.10.0", {"center": v(-562.48, 456.01) * mm, "radius": 1.6 * mm});
            skCircle(sketch, "E5.17.10.1", {"center": v(-557.48, 456.01) * mm, "radius": 1.6 * mm});
            skCircle(sketch, "E5.17.10.2", {"center": v(-559.98, 451.01) * mm, "radius": 1.6 * mm});
            skCircle(sketch, "E5.17.10.3", {"center": v(-554.98, 451.01) * mm, "radius": 1.6 * mm});
            skCircle(sketch, "E5.17.11.0", {"center": v(-562.48, 446.01) * mm, "radius": 1.6 * mm});
            skCircle(sketch, "E5.17.11.1", {"center": v(-557.48, 446.01) * mm, "radius": 1.6 * mm});
            skCircle(sketch, "E5.17.11.2", {"center": v(-559.98, 441.01) * mm, "radius": 1.6 * mm});
            skCircle(sketch, "E5.17.11.3", {"center": v(-554.98, 441.01) * mm, "radius": 1.6 * mm});
            skCircle(sketch, "E5.17.12.0", {"center": v(-562.48, 436.01) * mm, "radius": 1.6 * mm});
            skCircle(sketch, "E5.17.12.1", {"center": v(-557.48, 436.01) * mm, "radius": 1.6 * mm});
            skCircle(sketch, "E5.17.12.2", {"center": v(-559.98, 431.01) * mm, "radius": 1.6 * mm});
            skCircle(sketch, "E5.17.12.3", {"center": v(-554.98, 431.01) * mm, "radius": 1.6 * mm});
            skCircle(sketch, "E5.17.13.0", {"center": v(-562.48, 426.01) * mm, "radius": 1.6 * mm});
            skCircle(sketch, "E5.17.13.1", {"center": v(-557.48, 426.01) * mm, "radius": 1.6 * mm});
            skCircle(sketch, "E5.17.13.2", {"center": v(-559.98, 421.01) * mm, "radius": 1.6 * mm});
            skCircle(sketch, "E5.17.13.3", {"center": v(-554.98, 421.01) * mm, "radius": 1.6 * mm});
            skCircle(sketch, "E5.17.14.0", {"center": v(-562.48, 416.01) * mm, "radius": 1.6 * mm});
            skCircle(sketch, "E5.17.14.1", {"center": v(-557.48, 416.01) * mm, "radius": 1.6 * mm});
            skCircle(sketch, "E5.17.14.2", {"center": v(-559.98, 411.01) * mm, "radius": 1.6 * mm});
            skCircle(sketch, "E5.17.14.3", {"center": v(-554.98, 411.01) * mm, "radius": 1.6 * mm});
            skCircle(sketch, "E5.17.15.0", {"center": v(-562.48, 406.01) * mm, "radius": 1.6 * mm});
            skCircle(sketch, "E5.17.15.1", {"center": v(-557.48, 406.01) * mm, "radius": 1.6 * mm});
            skCircle(sketch, "E5.17.15.2", {"center": v(-559.98, 401.01) * mm, "radius": 1.6 * mm});
            skCircle(sketch, "E5.17.15.3", {"center": v(-554.98, 401.01) * mm, "radius": 1.6 * mm});
            skCircle(sketch, "E5.17.16.0", {"center": v(-562.48, 396.01) * mm, "radius": 1.6 * mm});
            skCircle(sketch, "E5.17.16.1", {"center": v(-557.48, 396.01) * mm, "radius": 1.6 * mm});
            skCircle(sketch, "E5.17.16.2", {"center": v(-559.98, 391.01) * mm, "radius": 1.6 * mm});
            skCircle(sketch, "E5.17.16.3", {"center": v(-554.98, 391.01) * mm, "radius": 1.6 * mm});
            skCircle(sketch, "E5.17.17.0", {"center": v(-562.48, 386.01) * mm, "radius": 1.6 * mm});
            skCircle(sketch, "E5.17.17.1", {"center": v(-557.48, 386.01) * mm, "radius": 1.6 * mm});
            skCircle(sketch, "E5.17.17.2", {"center": v(-559.98, 381.01) * mm, "radius": 1.6 * mm});
            skCircle(sketch, "E5.17.17.3", {"center": v(-554.98, 381.01) * mm, "radius": 1.6 * mm});
            skCircle(sketch, "E5.17.18.0", {"center": v(-562.48, 376.01) * mm, "radius": 1.6 * mm});
            skCircle(sketch, "E5.17.18.1", {"center": v(-557.48, 376.01) * mm, "radius": 1.6 * mm});
            skCircle(sketch, "E5.17.18.2", {"center": v(-559.98, 371.01) * mm, "radius": 1.6 * mm});
            skCircle(sketch, "E5.17.18.3", {"center": v(-554.98, 371.01) * mm, "radius": 1.6 * mm});
            skCircle(sketch, "E5.17.19.0", {"center": v(-562.48, 366.01) * mm, "radius": 1.6 * mm});
            skCircle(sketch, "E5.17.19.1", {"center": v(-557.48, 366.01) * mm, "radius": 1.6 * mm});
            skCircle(sketch, "E5.17.19.2", {"center": v(-559.98, 361.01) * mm, "radius": 1.6 * mm});
            skCircle(sketch, "E5.17.19.3", {"center": v(-554.98, 361.01) * mm, "radius": 1.6 * mm});
            skCircle(sketch, "E5.17.20.0", {"center": v(-562.48, 356.01) * mm, "radius": 1.6 * mm});
            skCircle(sketch, "E5.17.20.1", {"center": v(-557.48, 356.01) * mm, "radius": 1.6 * mm});
            skCircle(sketch, "E5.17.20.2", {"center": v(-559.98, 351.01) * mm, "radius": 1.6 * mm});
            skCircle(sketch, "E5.17.20.3", {"center": v(-554.98, 351.01) * mm, "radius": 1.6 * mm});
            skCircle(sketch, "E5.17.21.0", {"center": v(-562.48, 346.01) * mm, "radius": 1.6 * mm});
            skCircle(sketch, "E5.17.21.1", {"center": v(-557.48, 346.01) * mm, "radius": 1.6 * mm});
            skCircle(sketch, "E5.17.21.2", {"center": v(-559.98, 341.01) * mm, "radius": 1.6 * mm});
            skCircle(sketch, "E5.17.21.3", {"center": v(-554.98, 341.01) * mm, "radius": 1.6 * mm});
            skCircle(sketch, "E5.17.22.0", {"center": v(-562.48, 336.01) * mm, "radius": 1.6 * mm});
            skCircle(sketch, "E5.17.22.1", {"center": v(-557.48, 336.01) * mm, "radius": 1.6 * mm});
            skCircle(sketch, "E5.17.22.2", {"center": v(-559.98, 331.01) * mm, "radius": 1.6 * mm});
            skCircle(sketch, "E5.17.22.3", {"center": v(-554.98, 331.01) * mm, "radius": 1.6 * mm});
            skCircle(sketch, "E5.17.23.0", {"center": v(-562.48, 326.01) * mm, "radius": 1.6 * mm});
            skCircle(sketch, "E5.17.23.1", {"center": v(-557.48, 326.01) * mm, "radius": 1.6 * mm});
            skCircle(sketch, "E5.17.23.2", {"center": v(-559.98, 321.01) * mm, "radius": 1.6 * mm});
            skCircle(sketch, "E5.17.23.3", {"center": v(-554.98, 321.01) * mm, "radius": 1.6 * mm});
            skCircle(sketch, "E5.17.24.0", {"center": v(-562.48, 316.01) * mm, "radius": 1.6 * mm});
            skCircle(sketch, "E5.17.24.1", {"center": v(-557.48, 316.01) * mm, "radius": 1.6 * mm});
            skCircle(sketch, "E5.17.24.2", {"center": v(-559.98, 311.01) * mm, "radius": 1.6 * mm});
            skCircle(sketch, "E5.17.24.3", {"center": v(-554.98, 311.01) * mm, "radius": 1.6 * mm});
            skCircle(sketch, "E5.17.25.0", {"center": v(-562.48, 306.01) * mm, "radius": 1.6 * mm});
            skCircle(sketch, "E5.17.25.1", {"center": v(-557.48, 306.01) * mm, "radius": 1.6 * mm});
            skCircle(sketch, "E5.17.25.2", {"center": v(-559.98, 301.01) * mm, "radius": 1.6 * mm});
            skCircle(sketch, "E5.17.25.3", {"center": v(-554.98, 301.01) * mm, "radius": 1.6 * mm});
            skCircle(sketch, "E5.17.26.0", {"center": v(-562.48, 296.01) * mm, "radius": 1.6 * mm});
            skCircle(sketch, "E5.17.26.1", {"center": v(-557.48, 296.01) * mm, "radius": 1.6 * mm});
            skCircle(sketch, "E5.17.26.2", {"center": v(-559.98, 291.01) * mm, "radius": 1.6 * mm});
            skCircle(sketch, "E5.17.26.3", {"center": v(-554.98, 291.01) * mm, "radius": 1.6 * mm});
            skCircle(sketch, "E5.17.27.0", {"center": v(-562.48, 286.01) * mm, "radius": 1.6 * mm});
            skCircle(sketch, "E5.17.27.1", {"center": v(-557.48, 286.01) * mm, "radius": 1.6 * mm});
            skCircle(sketch, "E5.17.27.2", {"center": v(-559.98, 281.01) * mm, "radius": 1.6 * mm});
            skCircle(sketch, "E5.17.27.3", {"center": v(-554.98, 281.01) * mm, "radius": 1.6 * mm});
            skCircle(sketch, "E5.17.28.0", {"center": v(-562.48, 276.01) * mm, "radius": 1.6 * mm});
            skCircle(sketch, "E5.17.28.1", {"center": v(-557.48, 276.01) * mm, "radius": 1.6 * mm});
            skCircle(sketch, "E5.17.28.2", {"center": v(-559.98, 271.01) * mm, "radius": 1.6 * mm});
            skCircle(sketch, "E5.17.28.3", {"center": v(-554.98, 271.01) * mm, "radius": 1.6 * mm});
            skCircle(sketch, "E5.17.29.0", {"center": v(-562.48, 266.01) * mm, "radius": 1.6 * mm});
            skCircle(sketch, "E5.17.29.1", {"center": v(-557.48, 266.01) * mm, "radius": 1.6 * mm});
            skCircle(sketch, "E5.17.29.2", {"center": v(-559.98, 261.01) * mm, "radius": 1.6 * mm});
            skCircle(sketch, "E5.17.29.3", {"center": v(-554.98, 261.01) * mm, "radius": 1.6 * mm});
            skCircle(sketch, "E5.17.30.0", {"center": v(-562.48, 256.01) * mm, "radius": 1.6 * mm});
            skCircle(sketch, "E5.17.30.1", {"center": v(-557.48, 256.01) * mm, "radius": 1.6 * mm});
            skCircle(sketch, "E5.17.30.2", {"center": v(-559.98, 251.01) * mm, "radius": 1.6 * mm});
            skCircle(sketch, "E5.17.30.3", {"center": v(-554.98, 251.01) * mm, "radius": 1.6 * mm});
            skCircle(sketch, "E5.17.31.0", {"center": v(-562.48, 246.01) * mm, "radius": 1.6 * mm});
            skCircle(sketch, "E5.17.31.1", {"center": v(-557.48, 246.01) * mm, "radius": 1.6 * mm});
            skCircle(sketch, "E5.17.31.2", {"center": v(-559.98, 241.01) * mm, "radius": 1.6 * mm});
            skCircle(sketch, "E5.17.31.3", {"center": v(-554.98, 241.01) * mm, "radius": 1.6 * mm});
            skCircle(sketch, "E5.17.32.0", {"center": v(-562.48, 236.01) * mm, "radius": 1.6 * mm});
            skCircle(sketch, "E5.17.32.1", {"center": v(-557.48, 236.01) * mm, "radius": 1.6 * mm});
            skCircle(sketch, "E5.17.32.2", {"center": v(-559.98, 231.01) * mm, "radius": 1.6 * mm});
            skCircle(sketch, "E5.17.32.3", {"center": v(-554.98, 231.01) * mm, "radius": 1.6 * mm});
            skCircle(sketch, "E5.17.33.0", {"center": v(-562.48, 226.01) * mm, "radius": 1.6 * mm});
            skCircle(sketch, "E5.17.33.1", {"center": v(-557.48, 226.01) * mm, "radius": 1.6 * mm});
            skCircle(sketch, "E5.17.33.2", {"center": v(-559.98, 221.01) * mm, "radius": 1.6 * mm});
            skCircle(sketch, "E5.17.33.3", {"center": v(-554.98, 221.01) * mm, "radius": 1.6 * mm});
            skCircle(sketch, "E5.17.34.0", {"center": v(-562.48, 216.01) * mm, "radius": 1.6 * mm});
            skCircle(sketch, "E5.17.34.1", {"center": v(-557.48, 216.01) * mm, "radius": 1.6 * mm});
            skCircle(sketch, "E5.17.34.2", {"center": v(-559.98, 211.01) * mm, "radius": 1.6 * mm});
            skCircle(sketch, "E5.17.34.3", {"center": v(-554.98, 211.01) * mm, "radius": 1.6 * mm});
            skCircle(sketch, "E5.17.35.0", {"center": v(-562.48, 206.01) * mm, "radius": 1.6 * mm});
            skCircle(sketch, "E5.17.35.1", {"center": v(-557.48, 206.01) * mm, "radius": 1.6 * mm});
            skCircle(sketch, "E5.17.35.2", {"center": v(-559.98, 201.01) * mm, "radius": 1.6 * mm});
            skCircle(sketch, "E5.17.35.3", {"center": v(-554.98, 201.01) * mm, "radius": 1.6 * mm});
            skCircle(sketch, "E5.17.36.0", {"center": v(-562.48, 196.01) * mm, "radius": 1.6 * mm});
            skCircle(sketch, "E5.17.36.1", {"center": v(-557.48, 196.01) * mm, "radius": 1.6 * mm});
            skCircle(sketch, "E5.17.36.2", {"center": v(-559.98, 191.01) * mm, "radius": 1.6 * mm});
            skCircle(sketch, "E5.17.36.3", {"center": v(-554.98, 191.01) * mm, "radius": 1.6 * mm});
            skCircle(sketch, "E5.17.37.0", {"center": v(-562.48, 186.01) * mm, "radius": 1.6 * mm});
            skCircle(sketch, "E5.17.37.1", {"center": v(-557.48, 186.01) * mm, "radius": 1.6 * mm});
            skCircle(sketch, "E5.17.37.2", {"center": v(-559.98, 181.01) * mm, "radius": 1.6 * mm});
            skCircle(sketch, "E5.17.37.3", {"center": v(-554.98, 181.01) * mm, "radius": 1.6 * mm});
            skCircle(sketch, "E5.17.38.0", {"center": v(-562.48, 176.01) * mm, "radius": 1.6 * mm});
            skCircle(sketch, "E5.17.38.1", {"center": v(-557.48, 176.01) * mm, "radius": 1.6 * mm});
            skCircle(sketch, "E5.17.38.2", {"center": v(-559.98, 171.01) * mm, "radius": 1.6 * mm});
            skCircle(sketch, "E5.17.38.3", {"center": v(-554.98, 171.01) * mm, "radius": 1.6 * mm});
            skCircle(sketch, "E5.17.39.0", {"center": v(-562.48, 166.01) * mm, "radius": 1.6 * mm});
            skCircle(sketch, "E5.17.39.1", {"center": v(-557.48, 166.01) * mm, "radius": 1.6 * mm});
            skCircle(sketch, "E5.17.39.2", {"center": v(-559.98, 161.01) * mm, "radius": 1.6 * mm});
            skCircle(sketch, "E5.17.39.3", {"center": v(-554.98, 161.01) * mm, "radius": 1.6 * mm});
            skCircle(sketch, "E5.17.40.0", {"center": v(-562.48, 156.01) * mm, "radius": 1.6 * mm});
            skCircle(sketch, "E5.17.40.1", {"center": v(-557.48, 156.01) * mm, "radius": 1.6 * mm});
            skCircle(sketch, "E5.17.40.2", {"center": v(-559.98, 151.01) * mm, "radius": 1.6 * mm});
            skCircle(sketch, "E5.17.40.3", {"center": v(-554.98, 151.01) * mm, "radius": 1.6 * mm});
            skCircle(sketch, "E5.17.41.0", {"center": v(-562.48, 146.01) * mm, "radius": 1.6 * mm});
            skCircle(sketch, "E5.17.41.1", {"center": v(-557.48, 146.01) * mm, "radius": 1.6 * mm});
            skCircle(sketch, "E5.17.41.2", {"center": v(-559.98, 141.01) * mm, "radius": 1.6 * mm});
            skCircle(sketch, "E5.17.41.3", {"center": v(-554.98, 141.01) * mm, "radius": 1.6 * mm});
            skCircle(sketch, "E5.17.42.0", {"center": v(-562.48, 136.01) * mm, "radius": 1.6 * mm});
            skCircle(sketch, "E5.17.42.1", {"center": v(-557.48, 136.01) * mm, "radius": 1.6 * mm});
            skCircle(sketch, "E5.17.42.2", {"center": v(-559.98, 131.01) * mm, "radius": 1.6 * mm});
            skCircle(sketch, "E5.17.42.3", {"center": v(-554.98, 131.01) * mm, "radius": 1.6 * mm});
            skCircle(sketch, "E5.17.43.0", {"center": v(-562.48, 126.01) * mm, "radius": 1.6 * mm});
            skCircle(sketch, "E5.17.43.1", {"center": v(-557.48, 126.01) * mm, "radius": 1.6 * mm});
            skCircle(sketch, "E5.17.43.2", {"center": v(-559.98, 121.01) * mm, "radius": 1.6 * mm});
            skCircle(sketch, "E5.17.43.3", {"center": v(-554.98, 121.01) * mm, "radius": 1.6 * mm});
            skCircle(sketch, "E5.17.44.0", {"center": v(-562.48, 116.01) * mm, "radius": 1.6 * mm});
            skCircle(sketch, "E5.17.44.1", {"center": v(-557.48, 116.01) * mm, "radius": 1.6 * mm});
            skCircle(sketch, "E5.17.44.2", {"center": v(-559.98, 111.01) * mm, "radius": 1.6 * mm});
            skCircle(sketch, "E5.17.44.3", {"center": v(-554.98, 111.01) * mm, "radius": 1.6 * mm});
            skCircle(sketch, "E5.17.45.0", {"center": v(-562.48, 106.01) * mm, "radius": 1.6 * mm});
            skCircle(sketch, "E5.17.45.1", {"center": v(-557.48, 106.01) * mm, "radius": 1.6 * mm});
            skCircle(sketch, "E5.17.45.2", {"center": v(-559.98, 101.01) * mm, "radius": 1.6 * mm});
            skCircle(sketch, "E5.17.45.3", {"center": v(-554.98, 101.01) * mm, "radius": 1.6 * mm});
            skCircle(sketch, "E5.17.46.0", {"center": v(-562.48, 96.01) * mm, "radius": 1.6 * mm});
            skCircle(sketch, "E5.17.46.1", {"center": v(-557.48, 96.01) * mm, "radius": 1.6 * mm});
            skCircle(sketch, "E5.17.46.2", {"center": v(-559.98, 91.01) * mm, "radius": 1.6 * mm});
            skCircle(sketch, "E5.17.46.3", {"center": v(-554.98, 91.01) * mm, "radius": 1.6 * mm});
            skCircle(sketch, "E5.17.47.0", {"center": v(-562.48, 86.01) * mm, "radius": 1.6 * mm});
            skCircle(sketch, "E5.17.47.1", {"center": v(-557.48, 86.01) * mm, "radius": 1.6 * mm});
            skCircle(sketch, "E5.17.47.2", {"center": v(-559.98, 81.01) * mm, "radius": 1.6 * mm});
            skCircle(sketch, "E5.17.47.3", {"center": v(-554.98, 81.01) * mm, "radius": 1.6 * mm});
            skCircle(sketch, "E5.17.48.0", {"center": v(-562.48, 76.01) * mm, "radius": 1.6 * mm});
            skCircle(sketch, "E5.17.48.1", {"center": v(-557.48, 76.01) * mm, "radius": 1.6 * mm});
            skCircle(sketch, "E5.17.48.2", {"center": v(-559.98, 71.01) * mm, "radius": 1.6 * mm});
            skCircle(sketch, "E5.17.48.3", {"center": v(-554.98, 71.01) * mm, "radius": 1.6 * mm});
            skCircle(sketch, "E5.17.49.0", {"center": v(-562.48, 66.01) * mm, "radius": 1.6 * mm});
            skCircle(sketch, "E5.17.49.1", {"center": v(-557.48, 66.01) * mm, "radius": 1.6 * mm});
            skCircle(sketch, "E5.17.49.2", {"center": v(-559.98, 61.01) * mm, "radius": 1.6 * mm});
            skCircle(sketch, "E5.17.49.3", {"center": v(-554.98, 61.01) * mm, "radius": 1.6 * mm});
            skCircle(sketch, "E5.18.0.0", {"center": v(-552.48, 556.01) * mm, "radius": 1.6 * mm});
            skCircle(sketch, "E5.18.0.1", {"center": v(-547.48, 556.01) * mm, "radius": 1.6 * mm});
            skCircle(sketch, "E5.18.0.2", {"center": v(-549.98, 551.01) * mm, "radius": 1.6 * mm});
            skCircle(sketch, "E5.18.0.3", {"center": v(-544.98, 551.01) * mm, "radius": 1.6 * mm});
            skCircle(sketch, "E5.18.1.0", {"center": v(-552.48, 546.01) * mm, "radius": 1.6 * mm});
            skCircle(sketch, "E5.18.1.1", {"center": v(-547.48, 546.01) * mm, "radius": 1.6 * mm});
            skCircle(sketch, "E5.18.1.2", {"center": v(-549.98, 541.01) * mm, "radius": 1.6 * mm});
            skCircle(sketch, "E5.18.1.3", {"center": v(-544.98, 541.01) * mm, "radius": 1.6 * mm});
            skCircle(sketch, "E5.18.2.0", {"center": v(-552.48, 536.01) * mm, "radius": 1.6 * mm});
            skCircle(sketch, "E5.18.2.1", {"center": v(-547.48, 536.01) * mm, "radius": 1.6 * mm});
            skCircle(sketch, "E5.18.2.2", {"center": v(-549.98, 531.01) * mm, "radius": 1.6 * mm});
            skCircle(sketch, "E5.18.2.3", {"center": v(-544.98, 531.01) * mm, "radius": 1.6 * mm});
            skCircle(sketch, "E5.18.3.0", {"center": v(-552.48, 526.01) * mm, "radius": 1.6 * mm});
            skCircle(sketch, "E5.18.3.1", {"center": v(-547.48, 526.01) * mm, "radius": 1.6 * mm});
            skCircle(sketch, "E5.18.3.2", {"center": v(-549.98, 521.01) * mm, "radius": 1.6 * mm});
            skCircle(sketch, "E5.18.3.3", {"center": v(-544.98, 521.01) * mm, "radius": 1.6 * mm});
            skCircle(sketch, "E5.18.4.0", {"center": v(-552.48, 516.01) * mm, "radius": 1.6 * mm});
            skCircle(sketch, "E5.18.4.1", {"center": v(-547.48, 516.01) * mm, "radius": 1.6 * mm});
            skCircle(sketch, "E5.18.4.2", {"center": v(-549.98, 511.01) * mm, "radius": 1.6 * mm});
            skCircle(sketch, "E5.18.4.3", {"center": v(-544.98, 511.01) * mm, "radius": 1.6 * mm});
            skCircle(sketch, "E5.18.5.0", {"center": v(-552.48, 506.01) * mm, "radius": 1.6 * mm});
            skCircle(sketch, "E5.18.5.1", {"center": v(-547.48, 506.01) * mm, "radius": 1.6 * mm});
            skCircle(sketch, "E5.18.5.2", {"center": v(-549.98, 501.01) * mm, "radius": 1.6 * mm});
            skCircle(sketch, "E5.18.5.3", {"center": v(-544.98, 501.01) * mm, "radius": 1.6 * mm});
            skCircle(sketch, "E5.18.6.0", {"center": v(-552.48, 496.01) * mm, "radius": 1.6 * mm});
            skCircle(sketch, "E5.18.6.1", {"center": v(-547.48, 496.01) * mm, "radius": 1.6 * mm});
            skCircle(sketch, "E5.18.6.2", {"center": v(-549.98, 491.01) * mm, "radius": 1.6 * mm});
            skCircle(sketch, "E5.18.6.3", {"center": v(-544.98, 491.01) * mm, "radius": 1.6 * mm});
            skCircle(sketch, "E5.18.7.0", {"center": v(-552.48, 486.01) * mm, "radius": 1.6 * mm});
            skCircle(sketch, "E5.18.7.1", {"center": v(-547.48, 486.01) * mm, "radius": 1.6 * mm});
            skCircle(sketch, "E5.18.7.2", {"center": v(-549.98, 481.01) * mm, "radius": 1.6 * mm});
            skCircle(sketch, "E5.18.7.3", {"center": v(-544.98, 481.01) * mm, "radius": 1.6 * mm});
            skCircle(sketch, "E5.18.8.0", {"center": v(-552.48, 476.01) * mm, "radius": 1.6 * mm});
            skCircle(sketch, "E5.18.8.1", {"center": v(-547.48, 476.01) * mm, "radius": 1.6 * mm});
            skCircle(sketch, "E5.18.8.2", {"center": v(-549.98, 471.01) * mm, "radius": 1.6 * mm});
            skCircle(sketch, "E5.18.8.3", {"center": v(-544.98, 471.01) * mm, "radius": 1.6 * mm});
            skCircle(sketch, "E5.18.9.0", {"center": v(-552.48, 466.01) * mm, "radius": 1.6 * mm});
            skCircle(sketch, "E5.18.9.1", {"center": v(-547.48, 466.01) * mm, "radius": 1.6 * mm});
            skCircle(sketch, "E5.18.9.2", {"center": v(-549.98, 461.01) * mm, "radius": 1.6 * mm});
            skCircle(sketch, "E5.18.9.3", {"center": v(-544.98, 461.01) * mm, "radius": 1.6 * mm});
            skCircle(sketch, "E5.18.10.0", {"center": v(-552.48, 456.01) * mm, "radius": 1.6 * mm});
            skCircle(sketch, "E5.18.10.1", {"center": v(-547.48, 456.01) * mm, "radius": 1.6 * mm});
            skCircle(sketch, "E5.18.10.2", {"center": v(-549.98, 451.01) * mm, "radius": 1.6 * mm});
            skCircle(sketch, "E5.18.10.3", {"center": v(-544.98, 451.01) * mm, "radius": 1.6 * mm});
            skCircle(sketch, "E5.18.11.0", {"center": v(-552.48, 446.01) * mm, "radius": 1.6 * mm});
            skCircle(sketch, "E5.18.11.1", {"center": v(-547.48, 446.01) * mm, "radius": 1.6 * mm});
            skCircle(sketch, "E5.18.11.2", {"center": v(-549.98, 441.01) * mm, "radius": 1.6 * mm});
            skCircle(sketch, "E5.18.11.3", {"center": v(-544.98, 441.01) * mm, "radius": 1.6 * mm});
            skCircle(sketch, "E5.18.12.0", {"center": v(-552.48, 436.01) * mm, "radius": 1.6 * mm});
            skCircle(sketch, "E5.18.12.1", {"center": v(-547.48, 436.01) * mm, "radius": 1.6 * mm});
            skCircle(sketch, "E5.18.12.2", {"center": v(-549.98, 431.01) * mm, "radius": 1.6 * mm});
            skCircle(sketch, "E5.18.12.3", {"center": v(-544.98, 431.01) * mm, "radius": 1.6 * mm});
            skCircle(sketch, "E5.18.13.0", {"center": v(-552.48, 426.01) * mm, "radius": 1.6 * mm});
            skCircle(sketch, "E5.18.13.1", {"center": v(-547.48, 426.01) * mm, "radius": 1.6 * mm});
            skCircle(sketch, "E5.18.13.2", {"center": v(-549.98, 421.01) * mm, "radius": 1.6 * mm});
            skCircle(sketch, "E5.18.13.3", {"center": v(-544.98, 421.01) * mm, "radius": 1.6 * mm});
            skCircle(sketch, "E5.18.14.0", {"center": v(-552.48, 416.01) * mm, "radius": 1.6 * mm});
            skCircle(sketch, "E5.18.14.1", {"center": v(-547.48, 416.01) * mm, "radius": 1.6 * mm});
            skCircle(sketch, "E5.18.14.2", {"center": v(-549.98, 411.01) * mm, "radius": 1.6 * mm});
            skCircle(sketch, "E5.18.14.3", {"center": v(-544.98, 411.01) * mm, "radius": 1.6 * mm});
            skCircle(sketch, "E5.18.15.0", {"center": v(-552.48, 406.01) * mm, "radius": 1.6 * mm});
            skCircle(sketch, "E5.18.15.1", {"center": v(-547.48, 406.01) * mm, "radius": 1.6 * mm});
            skCircle(sketch, "E5.18.15.2", {"center": v(-549.98, 401.01) * mm, "radius": 1.6 * mm});
            skCircle(sketch, "E5.18.15.3", {"center": v(-544.98, 401.01) * mm, "radius": 1.6 * mm});
            skCircle(sketch, "E5.18.16.0", {"center": v(-552.48, 396.01) * mm, "radius": 1.6 * mm});
            skCircle(sketch, "E5.18.16.1", {"center": v(-547.48, 396.01) * mm, "radius": 1.6 * mm});
            skCircle(sketch, "E5.18.16.2", {"center": v(-549.98, 391.01) * mm, "radius": 1.6 * mm});
            skCircle(sketch, "E5.18.16.3", {"center": v(-544.98, 391.01) * mm, "radius": 1.6 * mm});
            skCircle(sketch, "E5.18.17.0", {"center": v(-552.48, 386.01) * mm, "radius": 1.6 * mm});
            skCircle(sketch, "E5.18.17.1", {"center": v(-547.48, 386.01) * mm, "radius": 1.6 * mm});
            skCircle(sketch, "E5.18.17.2", {"center": v(-549.98, 381.01) * mm, "radius": 1.6 * mm});
            skCircle(sketch, "E5.18.17.3", {"center": v(-544.98, 381.01) * mm, "radius": 1.6 * mm});
            skCircle(sketch, "E5.18.18.0", {"center": v(-552.48, 376.01) * mm, "radius": 1.6 * mm});
            skCircle(sketch, "E5.18.18.1", {"center": v(-547.48, 376.01) * mm, "radius": 1.6 * mm});
            skCircle(sketch, "E5.18.18.2", {"center": v(-549.98, 371.01) * mm, "radius": 1.6 * mm});
            skCircle(sketch, "E5.18.18.3", {"center": v(-544.98, 371.01) * mm, "radius": 1.6 * mm});
            skCircle(sketch, "E5.18.19.0", {"center": v(-552.48, 366.01) * mm, "radius": 1.6 * mm});
            skCircle(sketch, "E5.18.19.1", {"center": v(-547.48, 366.01) * mm, "radius": 1.6 * mm});
            skCircle(sketch, "E5.18.19.2", {"center": v(-549.98, 361.01) * mm, "radius": 1.6 * mm});
            skCircle(sketch, "E5.18.19.3", {"center": v(-544.98, 361.01) * mm, "radius": 1.6 * mm});
            skCircle(sketch, "E5.18.20.0", {"center": v(-552.48, 356.01) * mm, "radius": 1.6 * mm});
            skCircle(sketch, "E5.18.20.1", {"center": v(-547.48, 356.01) * mm, "radius": 1.6 * mm});
            skCircle(sketch, "E5.18.20.2", {"center": v(-549.98, 351.01) * mm, "radius": 1.6 * mm});
            skCircle(sketch, "E5.18.20.3", {"center": v(-544.98, 351.01) * mm, "radius": 1.6 * mm});
            skCircle(sketch, "E5.18.21.0", {"center": v(-552.48, 346.01) * mm, "radius": 1.6 * mm});
            skCircle(sketch, "E5.18.21.1", {"center": v(-547.48, 346.01) * mm, "radius": 1.6 * mm});
            skCircle(sketch, "E5.18.21.2", {"center": v(-549.98, 341.01) * mm, "radius": 1.6 * mm});
            skCircle(sketch, "E5.18.21.3", {"center": v(-544.98, 341.01) * mm, "radius": 1.6 * mm});
            skCircle(sketch, "E5.18.22.0", {"center": v(-552.48, 336.01) * mm, "radius": 1.6 * mm});
            skCircle(sketch, "E5.18.22.1", {"center": v(-547.48, 336.01) * mm, "radius": 1.6 * mm});
            skCircle(sketch, "E5.18.22.2", {"center": v(-549.98, 331.01) * mm, "radius": 1.6 * mm});
            skCircle(sketch, "E5.18.22.3", {"center": v(-544.98, 331.01) * mm, "radius": 1.6 * mm});
            skCircle(sketch, "E5.18.23.0", {"center": v(-552.48, 326.01) * mm, "radius": 1.6 * mm});
            skCircle(sketch, "E5.18.23.1", {"center": v(-547.48, 326.01) * mm, "radius": 1.6 * mm});
            skCircle(sketch, "E5.18.23.2", {"center": v(-549.98, 321.01) * mm, "radius": 1.6 * mm});
            skCircle(sketch, "E5.18.23.3", {"center": v(-544.98, 321.01) * mm, "radius": 1.6 * mm});
            skCircle(sketch, "E5.18.24.0", {"center": v(-552.48, 316.01) * mm, "radius": 1.6 * mm});
            skCircle(sketch, "E5.18.24.1", {"center": v(-547.48, 316.01) * mm, "radius": 1.6 * mm});
            skCircle(sketch, "E5.18.24.2", {"center": v(-549.98, 311.01) * mm, "radius": 1.6 * mm});
            skCircle(sketch, "E5.18.24.3", {"center": v(-544.98, 311.01) * mm, "radius": 1.6 * mm});
            skCircle(sketch, "E5.18.25.0", {"center": v(-552.48, 306.01) * mm, "radius": 1.6 * mm});
            skCircle(sketch, "E5.18.25.1", {"center": v(-547.48, 306.01) * mm, "radius": 1.6 * mm});
            skCircle(sketch, "E5.18.25.2", {"center": v(-549.98, 301.01) * mm, "radius": 1.6 * mm});
            skCircle(sketch, "E5.18.25.3", {"center": v(-544.98, 301.01) * mm, "radius": 1.6 * mm});
            skCircle(sketch, "E5.18.26.0", {"center": v(-552.48, 296.01) * mm, "radius": 1.6 * mm});
            skCircle(sketch, "E5.18.26.1", {"center": v(-547.48, 296.01) * mm, "radius": 1.6 * mm});
            skCircle(sketch, "E5.18.26.2", {"center": v(-549.98, 291.01) * mm, "radius": 1.6 * mm});
            skCircle(sketch, "E5.18.26.3", {"center": v(-544.98, 291.01) * mm, "radius": 1.6 * mm});
            skCircle(sketch, "E5.18.27.0", {"center": v(-552.48, 286.01) * mm, "radius": 1.6 * mm});
            skCircle(sketch, "E5.18.27.1", {"center": v(-547.48, 286.01) * mm, "radius": 1.6 * mm});
            skCircle(sketch, "E5.18.27.2", {"center": v(-549.98, 281.01) * mm, "radius": 1.6 * mm});
            skCircle(sketch, "E5.18.27.3", {"center": v(-544.98, 281.01) * mm, "radius": 1.6 * mm});
            skCircle(sketch, "E5.18.28.0", {"center": v(-552.48, 276.01) * mm, "radius": 1.6 * mm});
            skCircle(sketch, "E5.18.28.1", {"center": v(-547.48, 276.01) * mm, "radius": 1.6 * mm});
            skCircle(sketch, "E5.18.28.2", {"center": v(-549.98, 271.01) * mm, "radius": 1.6 * mm});
            skCircle(sketch, "E5.18.28.3", {"center": v(-544.98, 271.01) * mm, "radius": 1.6 * mm});
            skCircle(sketch, "E5.18.29.0", {"center": v(-552.48, 266.01) * mm, "radius": 1.6 * mm});
            skCircle(sketch, "E5.18.29.1", {"center": v(-547.48, 266.01) * mm, "radius": 1.6 * mm});
            skCircle(sketch, "E5.18.29.2", {"center": v(-549.98, 261.01) * mm, "radius": 1.6 * mm});
            skCircle(sketch, "E5.18.29.3", {"center": v(-544.98, 261.01) * mm, "radius": 1.6 * mm});
            skCircle(sketch, "E5.18.30.0", {"center": v(-552.48, 256.01) * mm, "radius": 1.6 * mm});
            skCircle(sketch, "E5.18.30.1", {"center": v(-547.48, 256.01) * mm, "radius": 1.6 * mm});
            skCircle(sketch, "E5.18.30.2", {"center": v(-549.98, 251.01) * mm, "radius": 1.6 * mm});
            skCircle(sketch, "E5.18.30.3", {"center": v(-544.98, 251.01) * mm, "radius": 1.6 * mm});
            skCircle(sketch, "E5.18.31.0", {"center": v(-552.48, 246.01) * mm, "radius": 1.6 * mm});
            skCircle(sketch, "E5.18.31.1", {"center": v(-547.48, 246.01) * mm, "radius": 1.6 * mm});
            skCircle(sketch, "E5.18.31.2", {"center": v(-549.98, 241.01) * mm, "radius": 1.6 * mm});
            skCircle(sketch, "E5.18.31.3", {"center": v(-544.98, 241.01) * mm, "radius": 1.6 * mm});
            skCircle(sketch, "E5.18.32.0", {"center": v(-552.48, 236.01) * mm, "radius": 1.6 * mm});
            skCircle(sketch, "E5.18.32.1", {"center": v(-547.48, 236.01) * mm, "radius": 1.6 * mm});
            skCircle(sketch, "E5.18.32.2", {"center": v(-549.98, 231.01) * mm, "radius": 1.6 * mm});
            skCircle(sketch, "E5.18.32.3", {"center": v(-544.98, 231.01) * mm, "radius": 1.6 * mm});
            skCircle(sketch, "E5.18.33.0", {"center": v(-552.48, 226.01) * mm, "radius": 1.6 * mm});
            skCircle(sketch, "E5.18.33.1", {"center": v(-547.48, 226.01) * mm, "radius": 1.6 * mm});
            skCircle(sketch, "E5.18.33.2", {"center": v(-549.98, 221.01) * mm, "radius": 1.6 * mm});
            skCircle(sketch, "E5.18.33.3", {"center": v(-544.98, 221.01) * mm, "radius": 1.6 * mm});
            skCircle(sketch, "E5.18.34.0", {"center": v(-552.48, 216.01) * mm, "radius": 1.6 * mm});
            skCircle(sketch, "E5.18.34.1", {"center": v(-547.48, 216.01) * mm, "radius": 1.6 * mm});
            skCircle(sketch, "E5.18.34.2", {"center": v(-549.98, 211.01) * mm, "radius": 1.6 * mm});
            skCircle(sketch, "E5.18.34.3", {"center": v(-544.98, 211.01) * mm, "radius": 1.6 * mm});
            skCircle(sketch, "E5.18.35.0", {"center": v(-552.48, 206.01) * mm, "radius": 1.6 * mm});
            skCircle(sketch, "E5.18.35.1", {"center": v(-547.48, 206.01) * mm, "radius": 1.6 * mm});
            skCircle(sketch, "E5.18.35.2", {"center": v(-549.98, 201.01) * mm, "radius": 1.6 * mm});
            skCircle(sketch, "E5.18.35.3", {"center": v(-544.98, 201.01) * mm, "radius": 1.6 * mm});
            skCircle(sketch, "E5.18.36.0", {"center": v(-552.48, 196.01) * mm, "radius": 1.6 * mm});
            skCircle(sketch, "E5.18.36.1", {"center": v(-547.48, 196.01) * mm, "radius": 1.6 * mm});
            skCircle(sketch, "E5.18.36.2", {"center": v(-549.98, 191.01) * mm, "radius": 1.6 * mm});
            skCircle(sketch, "E5.18.36.3", {"center": v(-544.98, 191.01) * mm, "radius": 1.6 * mm});
            skCircle(sketch, "E5.18.37.0", {"center": v(-552.48, 186.01) * mm, "radius": 1.6 * mm});
            skCircle(sketch, "E5.18.37.1", {"center": v(-547.48, 186.01) * mm, "radius": 1.6 * mm});
            skCircle(sketch, "E5.18.37.2", {"center": v(-549.98, 181.01) * mm, "radius": 1.6 * mm});
            skCircle(sketch, "E5.18.37.3", {"center": v(-544.98, 181.01) * mm, "radius": 1.6 * mm});
            skCircle(sketch, "E5.18.38.0", {"center": v(-552.48, 176.01) * mm, "radius": 1.6 * mm});
            skCircle(sketch, "E5.18.38.1", {"center": v(-547.48, 176.01) * mm, "radius": 1.6 * mm});
            skCircle(sketch, "E5.18.38.2", {"center": v(-549.98, 171.01) * mm, "radius": 1.6 * mm});
            skCircle(sketch, "E5.18.38.3", {"center": v(-544.98, 171.01) * mm, "radius": 1.6 * mm});
            skCircle(sketch, "E5.18.39.0", {"center": v(-552.48, 166.01) * mm, "radius": 1.6 * mm});
            skCircle(sketch, "E5.18.39.1", {"center": v(-547.48, 166.01) * mm, "radius": 1.6 * mm});
            skCircle(sketch, "E5.18.39.2", {"center": v(-549.98, 161.01) * mm, "radius": 1.6 * mm});
            skCircle(sketch, "E5.18.39.3", {"center": v(-544.98, 161.01) * mm, "radius": 1.6 * mm});
            skCircle(sketch, "E5.18.40.0", {"center": v(-552.48, 156.01) * mm, "radius": 1.6 * mm});
            skCircle(sketch, "E5.18.40.1", {"center": v(-547.48, 156.01) * mm, "radius": 1.6 * mm});
            skCircle(sketch, "E5.18.40.2", {"center": v(-549.98, 151.01) * mm, "radius": 1.6 * mm});
            skCircle(sketch, "E5.18.40.3", {"center": v(-544.98, 151.01) * mm, "radius": 1.6 * mm});
            skCircle(sketch, "E5.18.41.0", {"center": v(-552.48, 146.01) * mm, "radius": 1.6 * mm});
            skCircle(sketch, "E5.18.41.1", {"center": v(-547.48, 146.01) * mm, "radius": 1.6 * mm});
            skCircle(sketch, "E5.18.41.2", {"center": v(-549.98, 141.01) * mm, "radius": 1.6 * mm});
            skCircle(sketch, "E5.18.41.3", {"center": v(-544.98, 141.01) * mm, "radius": 1.6 * mm});
            skCircle(sketch, "E5.18.42.0", {"center": v(-552.48, 136.01) * mm, "radius": 1.6 * mm});
            skCircle(sketch, "E5.18.42.1", {"center": v(-547.48, 136.01) * mm, "radius": 1.6 * mm});
            skCircle(sketch, "E5.18.42.2", {"center": v(-549.98, 131.01) * mm, "radius": 1.6 * mm});
            skCircle(sketch, "E5.18.42.3", {"center": v(-544.98, 131.01) * mm, "radius": 1.6 * mm});
            skCircle(sketch, "E5.18.43.0", {"center": v(-552.48, 126.01) * mm, "radius": 1.6 * mm});
            skCircle(sketch, "E5.18.43.1", {"center": v(-547.48, 126.01) * mm, "radius": 1.6 * mm});
            skCircle(sketch, "E5.18.43.2", {"center": v(-549.98, 121.01) * mm, "radius": 1.6 * mm});
            skCircle(sketch, "E5.18.43.3", {"center": v(-544.98, 121.01) * mm, "radius": 1.6 * mm});
            skCircle(sketch, "E5.18.44.0", {"center": v(-552.48, 116.01) * mm, "radius": 1.6 * mm});
            skCircle(sketch, "E5.18.44.1", {"center": v(-547.48, 116.01) * mm, "radius": 1.6 * mm});
            skCircle(sketch, "E5.18.44.2", {"center": v(-549.98, 111.01) * mm, "radius": 1.6 * mm});
            skCircle(sketch, "E5.18.44.3", {"center": v(-544.98, 111.01) * mm, "radius": 1.6 * mm});
            skCircle(sketch, "E5.18.45.0", {"center": v(-552.48, 106.01) * mm, "radius": 1.6 * mm});
            skCircle(sketch, "E5.18.45.1", {"center": v(-547.48, 106.01) * mm, "radius": 1.6 * mm});
            skCircle(sketch, "E5.18.45.2", {"center": v(-549.98, 101.01) * mm, "radius": 1.6 * mm});
            skCircle(sketch, "E5.18.45.3", {"center": v(-544.98, 101.01) * mm, "radius": 1.6 * mm});
            skCircle(sketch, "E5.18.46.0", {"center": v(-552.48, 96.01) * mm, "radius": 1.6 * mm});
            skCircle(sketch, "E5.18.46.1", {"center": v(-547.48, 96.01) * mm, "radius": 1.6 * mm});
            skCircle(sketch, "E5.18.46.2", {"center": v(-549.98, 91.01) * mm, "radius": 1.6 * mm});
            skCircle(sketch, "E5.18.46.3", {"center": v(-544.98, 91.01) * mm, "radius": 1.6 * mm});
            skCircle(sketch, "E5.18.47.0", {"center": v(-552.48, 86.01) * mm, "radius": 1.6 * mm});
            skCircle(sketch, "E5.18.47.1", {"center": v(-547.48, 86.01) * mm, "radius": 1.6 * mm});
            skCircle(sketch, "E5.18.47.2", {"center": v(-549.98, 81.01) * mm, "radius": 1.6 * mm});
            skCircle(sketch, "E5.18.47.3", {"center": v(-544.98, 81.01) * mm, "radius": 1.6 * mm});
            skCircle(sketch, "E5.18.48.0", {"center": v(-552.48, 76.01) * mm, "radius": 1.6 * mm});
            skCircle(sketch, "E5.18.48.1", {"center": v(-547.48, 76.01) * mm, "radius": 1.6 * mm});
            skCircle(sketch, "E5.18.48.2", {"center": v(-549.98, 71.01) * mm, "radius": 1.6 * mm});
            skCircle(sketch, "E5.18.48.3", {"center": v(-544.98, 71.01) * mm, "radius": 1.6 * mm});
            skCircle(sketch, "E5.18.49.0", {"center": v(-552.48, 66.01) * mm, "radius": 1.6 * mm});
            skCircle(sketch, "E5.18.49.1", {"center": v(-547.48, 66.01) * mm, "radius": 1.6 * mm});
            skCircle(sketch, "E5.18.49.2", {"center": v(-549.98, 61.01) * mm, "radius": 1.6 * mm});
            skCircle(sketch, "E5.18.49.3", {"center": v(-544.98, 61.01) * mm, "radius": 1.6 * mm});
            skLineSegment(sketch, "E5.direction1", {"start": v(-732.48, 556.01) * mm, "end": v(-722.48, 556.01) * mm, "construction": true});
            skLineSegment(sketch, "E5.direction2", {"start": v(-732.48, 556.01) * mm, "end": v(-732.48, 546.01) * mm, "construction": true});
            skSolve(sketch);
        }
        {
            var Q0;
            Q0=makeQuery(id+"F0.imprint","IMPRINT",FACE,{"disambiguationData":[TD([[makeQuery(id+"F0.imprint","IMPRINT",EDGE,{"derivedFrom":sQuery(id+"F0.wireOp",EDGE,"E0.bottom")}),-1.0]])]});
            extrude(context, id + "F1", {"entities" : qUnion([Q0]), "depth" : 3 * mm, "offsetDistance" : 25 * mm});
        }
    });
